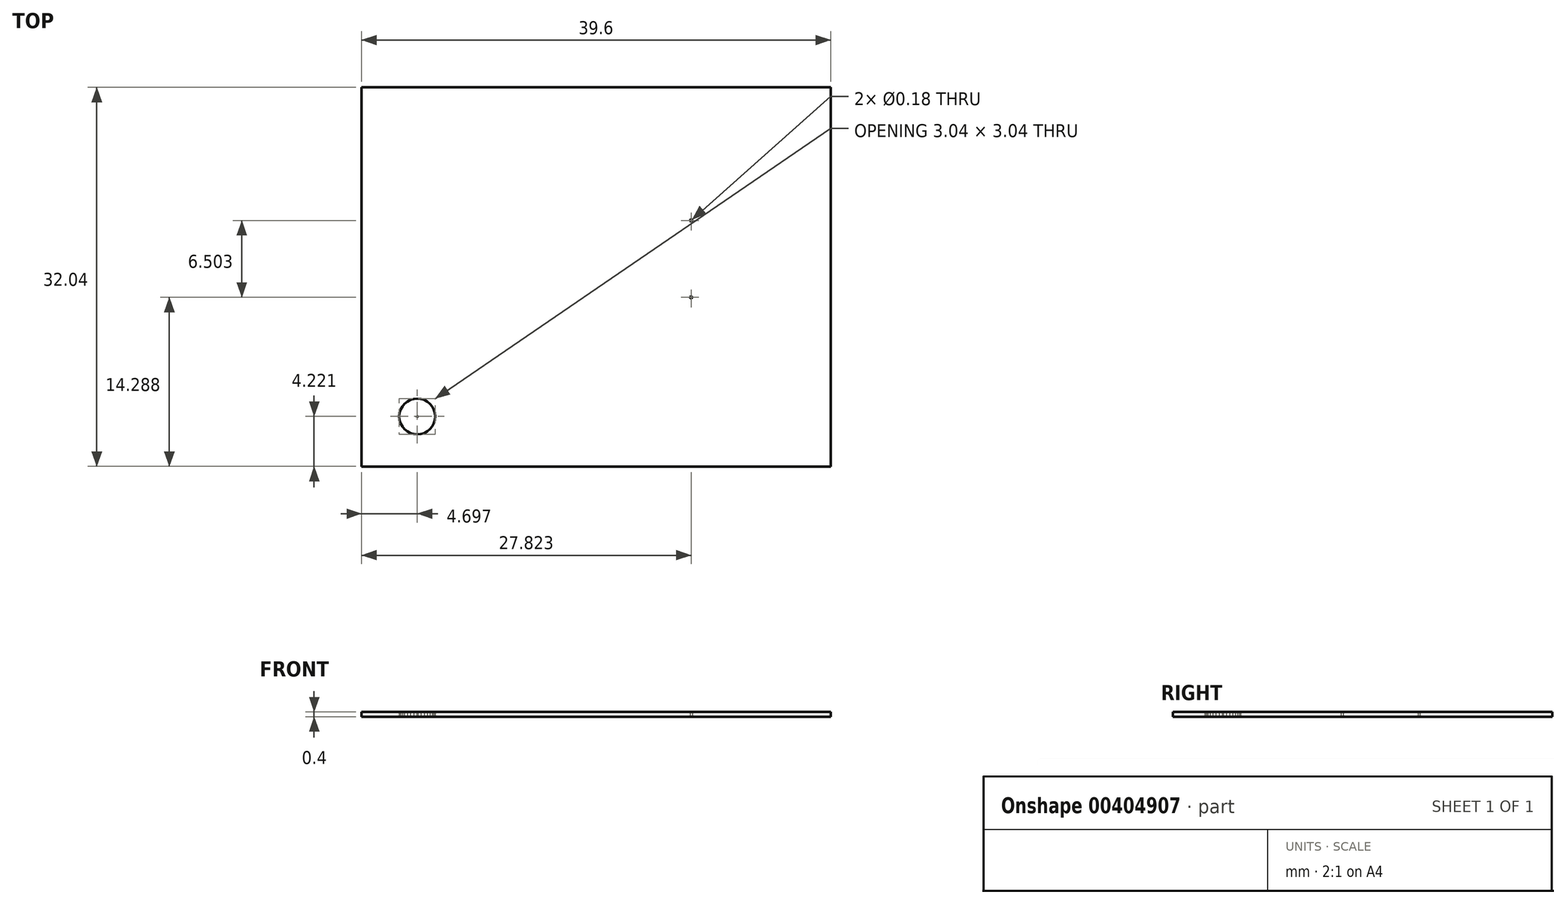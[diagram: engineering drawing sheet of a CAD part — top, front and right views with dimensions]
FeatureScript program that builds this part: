
annotation { "Feature Type Name" : "Feature", "Feature Type Description" : "" }
export const myFeature = defineFeature(function(context is Context, id is Id, definition is map)
    precondition{}
    {
        {
            var Q0;
            Q0=qCreatedBy(makeId("Top.planeOp"),FACE);
            var sketch = newSketch(context, id + "F0", { "sketchPlane" : qUnion([Q0])});
            skLineSegment(sketch, "E0", {"start": v(8.02, -8.23) * mm, "end": v(8.12, -8.23) * mm});
            skCircle(sketch, "E1", {"center": v(8.02, -8.23) * mm, "radius": 0.1 * mm});
            skLineSegment(sketch, "E2", {"start": v(8.02, -4.98) * mm, "end": v(8.12, -4.98) * mm});
            skCircle(sketch, "E3", {"center": v(8.02, -4.98) * mm, "radius": 0.1 * mm});
            skLineSegment(sketch, "E4", {"start": v(8.02, -1.73) * mm, "end": v(8.12, -1.73) * mm});
            skCircle(sketch, "E5", {"center": v(8.02, -1.73) * mm, "radius": 0.1 * mm});
            skLineSegment(sketch, "E6", {"start": v(8.02, 1.52) * mm, "end": v(8.12, 1.52) * mm});
            skCircle(sketch, "E7", {"center": v(8.02, 1.52) * mm, "radius": 0.1 * mm});
            skLineSegment(sketch, "E8", {"start": v(8.02, 4.77) * mm, "end": v(8.12, 4.77) * mm});
            skCircle(sketch, "E9", {"center": v(8.02, 4.77) * mm, "radius": 0.1 * mm});
            skLineSegment(sketch, "E10", {"start": v(8.02, 8.02) * mm, "end": v(8.12, 8.02) * mm});
            skCircle(sketch, "E11", {"center": v(8.02, 8.02) * mm, "radius": 0.1 * mm});
            skLineSegment(sketch, "E12", {"start": v(15.1, -11.8) * mm, "end": v(15.15, -11.8) * mm});
            skCircle(sketch, "E13", {"center": v(15.1, -11.8) * mm, "radius": 0.05 * mm});
            skLineSegment(sketch, "E14", {"start": v(15.1, 11.8) * mm, "end": v(15.15, 11.8) * mm});
            skCircle(sketch, "E15", {"center": v(15.1, 11.8) * mm, "radius": 0.05 * mm});
            skLineSegment(sketch, "E16", {"start": v(-15.1, -11.8) * mm, "end": v(-15.06, -11.8) * mm});
            skCircle(sketch, "E17", {"center": v(-15.1, -11.8) * mm, "radius": 0.05 * mm});
            skLineSegment(sketch, "E18", {"start": v(-15.1, 11.8) * mm, "end": v(-15.06, 11.8) * mm});
            skCircle(sketch, "E19", {"center": v(-15.1, 11.8) * mm, "radius": 0.05 * mm});
            skLineSegment(sketch, "E20", {"start": v(16.5, -12.38) * mm, "end": v(16.6, -12.1) * mm});
            skLineSegment(sketch, "E21", {"start": v(16.6, -12.1) * mm, "end": v(16.62, -11.8) * mm});
            skLineSegment(sketch, "E22", {"start": v(16.62, -11.8) * mm, "end": v(16.6, -11.5) * mm});
            skLineSegment(sketch, "E23", {"start": v(16.6, -11.5) * mm, "end": v(16.5, -11.22) * mm});
            skLineSegment(sketch, "E24", {"start": v(16.5, -11.22) * mm, "end": v(16.36, -10.96) * mm});
            skLineSegment(sketch, "E25", {"start": v(16.36, -10.96) * mm, "end": v(16.18, -10.73) * mm});
            skLineSegment(sketch, "E26", {"start": v(16.18, -10.73) * mm, "end": v(15.95, -10.54) * mm});
            skLineSegment(sketch, "E27", {"start": v(15.95, -10.54) * mm, "end": v(15.68, -10.4) * mm});
            skLineSegment(sketch, "E28", {"start": v(15.68, -10.4) * mm, "end": v(15.4, -10.31) * mm});
            skLineSegment(sketch, "E29", {"start": v(15.4, -10.31) * mm, "end": v(15.1, -10.28) * mm});
            skLineSegment(sketch, "E30", {"start": v(15.1, -10.28) * mm, "end": v(14.8, -10.31) * mm});
            skLineSegment(sketch, "E31", {"start": v(14.8, -10.31) * mm, "end": v(14.52, -10.4) * mm});
            skLineSegment(sketch, "E32", {"start": v(14.52, -10.4) * mm, "end": v(14.26, -10.54) * mm});
            skLineSegment(sketch, "E33", {"start": v(14.26, -10.54) * mm, "end": v(14.03, -10.73) * mm});
            skLineSegment(sketch, "E34", {"start": v(14.03, -10.73) * mm, "end": v(13.84, -10.96) * mm});
            skLineSegment(sketch, "E35", {"start": v(13.84, -10.96) * mm, "end": v(13.7, -11.22) * mm});
            skLineSegment(sketch, "E36", {"start": v(13.7, -11.22) * mm, "end": v(13.61, -11.5) * mm});
            skLineSegment(sketch, "E37", {"start": v(13.61, -11.5) * mm, "end": v(13.59, -11.8) * mm});
            skLineSegment(sketch, "E38", {"start": v(13.59, -11.8) * mm, "end": v(13.61, -12.1) * mm});
            skLineSegment(sketch, "E39", {"start": v(13.61, -12.1) * mm, "end": v(13.7, -12.38) * mm});
            skLineSegment(sketch, "E40", {"start": v(13.7, -12.38) * mm, "end": v(13.84, -12.64) * mm});
            skLineSegment(sketch, "E41", {"start": v(13.84, -12.64) * mm, "end": v(14.03, -12.87) * mm});
            skLineSegment(sketch, "E42", {"start": v(14.03, -12.87) * mm, "end": v(14.26, -13.06) * mm});
            skLineSegment(sketch, "E43", {"start": v(14.26, -13.06) * mm, "end": v(14.52, -13.2) * mm});
            skLineSegment(sketch, "E44", {"start": v(14.52, -13.2) * mm, "end": v(14.8, -13.29) * mm});
            skLineSegment(sketch, "E45", {"start": v(14.8, -13.29) * mm, "end": v(15.1, -13.32) * mm});
            skLineSegment(sketch, "E46", {"start": v(15.1, -13.32) * mm, "end": v(15.4, -13.29) * mm});
            skLineSegment(sketch, "E47", {"start": v(15.4, -13.29) * mm, "end": v(15.68, -13.2) * mm});
            skLineSegment(sketch, "E48", {"start": v(15.68, -13.2) * mm, "end": v(15.95, -13.06) * mm});
            skLineSegment(sketch, "E49", {"start": v(15.95, -13.06) * mm, "end": v(16.18, -12.87) * mm});
            skLineSegment(sketch, "E50", {"start": v(16.18, -12.87) * mm, "end": v(16.36, -12.64) * mm});
            skLineSegment(sketch, "E51", {"start": v(16.36, -12.64) * mm, "end": v(16.5, -12.38) * mm});
            skLineSegment(sketch, "E52", {"start": v(16.48, -12.37) * mm, "end": v(16.56, -12.09) * mm});
            skLineSegment(sketch, "E53", {"start": v(16.56, -12.09) * mm, "end": v(16.59, -11.8) * mm});
            skLineSegment(sketch, "E54", {"start": v(16.59, -11.8) * mm, "end": v(16.56, -11.5) * mm});
            skLineSegment(sketch, "E55", {"start": v(16.56, -11.5) * mm, "end": v(16.48, -11.23) * mm});
            skLineSegment(sketch, "E56", {"start": v(16.48, -11.23) * mm, "end": v(16.34, -10.97) * mm});
            skLineSegment(sketch, "E57", {"start": v(16.34, -10.97) * mm, "end": v(16.15, -10.75) * mm});
            skLineSegment(sketch, "E58", {"start": v(16.15, -10.75) * mm, "end": v(15.93, -10.56) * mm});
            skLineSegment(sketch, "E59", {"start": v(15.93, -10.56) * mm, "end": v(15.67, -10.43) * mm});
            skLineSegment(sketch, "E60", {"start": v(15.67, -10.43) * mm, "end": v(15.4, -10.34) * mm});
            skLineSegment(sketch, "E61", {"start": v(15.4, -10.34) * mm, "end": v(15.1, -10.31) * mm});
            skLineSegment(sketch, "E62", {"start": v(15.1, -10.31) * mm, "end": v(14.81, -10.34) * mm});
            skLineSegment(sketch, "E63", {"start": v(14.81, -10.34) * mm, "end": v(14.53, -10.43) * mm});
            skLineSegment(sketch, "E64", {"start": v(14.53, -10.43) * mm, "end": v(14.28, -10.56) * mm});
            skLineSegment(sketch, "E65", {"start": v(14.28, -10.56) * mm, "end": v(14.05, -10.75) * mm});
            skLineSegment(sketch, "E66", {"start": v(14.05, -10.75) * mm, "end": v(13.87, -10.97) * mm});
            skLineSegment(sketch, "E67", {"start": v(13.87, -10.97) * mm, "end": v(13.73, -11.23) * mm});
            skLineSegment(sketch, "E68", {"start": v(13.73, -11.23) * mm, "end": v(13.64, -11.5) * mm});
            skLineSegment(sketch, "E69", {"start": v(13.64, -11.5) * mm, "end": v(13.62, -11.8) * mm});
            skLineSegment(sketch, "E70", {"start": v(13.62, -11.8) * mm, "end": v(13.64, -12.09) * mm});
            skLineSegment(sketch, "E71", {"start": v(13.64, -12.09) * mm, "end": v(13.73, -12.37) * mm});
            skLineSegment(sketch, "E72", {"start": v(13.73, -12.37) * mm, "end": v(13.87, -12.62) * mm});
            skLineSegment(sketch, "E73", {"start": v(13.87, -12.62) * mm, "end": v(14.05, -12.85) * mm});
            skLineSegment(sketch, "E74", {"start": v(14.05, -12.85) * mm, "end": v(14.28, -13.03) * mm});
            skLineSegment(sketch, "E75", {"start": v(14.28, -13.03) * mm, "end": v(14.53, -13.17) * mm});
            skLineSegment(sketch, "E76", {"start": v(14.53, -13.17) * mm, "end": v(14.81, -13.26) * mm});
            skLineSegment(sketch, "E77", {"start": v(14.81, -13.26) * mm, "end": v(15.1, -13.29) * mm});
            skLineSegment(sketch, "E78", {"start": v(15.1, -13.29) * mm, "end": v(15.4, -13.26) * mm});
            skLineSegment(sketch, "E79", {"start": v(15.4, -13.26) * mm, "end": v(15.67, -13.17) * mm});
            skLineSegment(sketch, "E80", {"start": v(15.67, -13.17) * mm, "end": v(15.93, -13.03) * mm});
            skLineSegment(sketch, "E81", {"start": v(15.93, -13.03) * mm, "end": v(16.15, -12.85) * mm});
            skLineSegment(sketch, "E82", {"start": v(16.15, -12.85) * mm, "end": v(16.34, -12.62) * mm});
            skLineSegment(sketch, "E83", {"start": v(16.34, -12.62) * mm, "end": v(16.48, -12.37) * mm});
            skLineSegment(sketch, "E84", {"start": v(10.57, -8.15) * mm, "end": v(10.59, -8.1) * mm});
            skLineSegment(sketch, "E85", {"start": v(10.59, -8.1) * mm, "end": v(10.6, -8.07) * mm});
            skLineSegment(sketch, "E86", {"start": v(10.6, -8.07) * mm, "end": v(10.6, -8.02) * mm});
            skLineSegment(sketch, "E87", {"start": v(10.6, -8.02) * mm, "end": v(10.6, -1.65) * mm});
            skLineSegment(sketch, "E88", {"start": v(10.6, -1.65) * mm, "end": v(10.6, 4.72) * mm});
            skLineSegment(sketch, "E89", {"start": v(10.6, 4.72) * mm, "end": v(10.6, 8.97) * mm});
            skLineSegment(sketch, "E90", {"start": v(10.6, 8.97) * mm, "end": v(10.6, 9.01) * mm});
            skLineSegment(sketch, "E91", {"start": v(10.6, 9.01) * mm, "end": v(10.59, 9.05) * mm});
            skLineSegment(sketch, "E92", {"start": v(10.59, 9.05) * mm, "end": v(10.57, 9.1) * mm});
            skLineSegment(sketch, "E93", {"start": v(10.57, 9.1) * mm, "end": v(10.54, 9.13) * mm});
            skLineSegment(sketch, "E94", {"start": v(10.54, 9.13) * mm, "end": v(6.3, 13.37) * mm});
            skLineSegment(sketch, "E95", {"start": v(6.3, 13.37) * mm, "end": v(6.26, 13.4) * mm});
            skLineSegment(sketch, "E96", {"start": v(6.26, 13.4) * mm, "end": v(6.22, 13.42) * mm});
            skLineSegment(sketch, "E97", {"start": v(6.22, 13.42) * mm, "end": v(6.18, 13.43) * mm});
            skLineSegment(sketch, "E98", {"start": v(6.18, 13.43) * mm, "end": v(6.14, 13.44) * mm});
            skLineSegment(sketch, "E99", {"start": v(6.14, 13.44) * mm, "end": v(-0.94, 13.44) * mm});
            skLineSegment(sketch, "E100", {"start": v(-0.94, 13.44) * mm, "end": v(-7.08, 13.44) * mm});
            skLineSegment(sketch, "E101", {"start": v(-7.08, 13.44) * mm, "end": v(-7.12, 13.43) * mm});
            skLineSegment(sketch, "E102", {"start": v(-7.12, 13.43) * mm, "end": v(-7.16, 13.42) * mm});
            skLineSegment(sketch, "E103", {"start": v(-7.16, 13.42) * mm, "end": v(-7.2, 13.4) * mm});
            skLineSegment(sketch, "E104", {"start": v(-7.2, 13.4) * mm, "end": v(-7.24, 13.37) * mm});
            skLineSegment(sketch, "E105", {"start": v(-7.24, 13.37) * mm, "end": v(-12.9, 7.7) * mm});
            skLineSegment(sketch, "E106", {"start": v(-12.9, 7.7) * mm, "end": v(-12.93, 7.68) * mm});
            skLineSegment(sketch, "E107", {"start": v(-12.93, 7.68) * mm, "end": v(-12.95, 7.64) * mm});
            skLineSegment(sketch, "E108", {"start": v(-12.95, 7.64) * mm, "end": v(-12.96, 7.6) * mm});
            skLineSegment(sketch, "E109", {"start": v(-12.96, 7.6) * mm, "end": v(-12.97, 7.55) * mm});
            skLineSegment(sketch, "E110", {"start": v(-12.97, 7.55) * mm, "end": v(-12.97, 6.37) * mm});
            skLineSegment(sketch, "E111", {"start": v(-12.97, 6.37) * mm, "end": v(-13.03, 6.35) * mm});
            skLineSegment(sketch, "E112", {"start": v(-13.03, 6.35) * mm, "end": v(-13.16, 6.28) * mm});
            skLineSegment(sketch, "E113", {"start": v(-13.16, 6.28) * mm, "end": v(-13.27, 6.19) * mm});
            skLineSegment(sketch, "E114", {"start": v(-13.27, 6.19) * mm, "end": v(-13.36, 6.08) * mm});
            skLineSegment(sketch, "E115", {"start": v(-13.36, 6.08) * mm, "end": v(-13.43, 5.95) * mm});
            skLineSegment(sketch, "E116", {"start": v(-13.43, 5.95) * mm, "end": v(-13.47, 5.8) * mm});
            skLineSegment(sketch, "E117", {"start": v(-13.47, 5.8) * mm, "end": v(-13.49, 5.66) * mm});
            skLineSegment(sketch, "E118", {"start": v(-13.49, 5.66) * mm, "end": v(-13.47, 5.52) * mm});
            skLineSegment(sketch, "E119", {"start": v(-13.47, 5.52) * mm, "end": v(-13.43, 5.38) * mm});
            skLineSegment(sketch, "E120", {"start": v(-13.43, 5.38) * mm, "end": v(-13.36, 5.25) * mm});
            skLineSegment(sketch, "E121", {"start": v(-13.36, 5.25) * mm, "end": v(-13.27, 5.14) * mm});
            skLineSegment(sketch, "E122", {"start": v(-13.27, 5.14) * mm, "end": v(-13.16, 5.05) * mm});
            skLineSegment(sketch, "E123", {"start": v(-13.16, 5.05) * mm, "end": v(-13.03, 4.98) * mm});
            skLineSegment(sketch, "E124", {"start": v(-13.03, 4.98) * mm, "end": v(-12.89, 4.93) * mm});
            skLineSegment(sketch, "E125", {"start": v(-12.89, 4.93) * mm, "end": v(-12.74, 4.92) * mm});
            skLineSegment(sketch, "E126", {"start": v(-12.74, 4.92) * mm, "end": v(-12.6, 4.93) * mm});
            skLineSegment(sketch, "E127", {"start": v(-12.6, 4.93) * mm, "end": v(-12.46, 4.98) * mm});
            skLineSegment(sketch, "E128", {"start": v(-12.46, 4.98) * mm, "end": v(-12.33, 5.05) * mm});
            skLineSegment(sketch, "E129", {"start": v(-12.33, 5.05) * mm, "end": v(-12.22, 5.14) * mm});
            skLineSegment(sketch, "E130", {"start": v(-12.22, 5.14) * mm, "end": v(-12.12, 5.25) * mm});
            skLineSegment(sketch, "E131", {"start": v(-12.12, 5.25) * mm, "end": v(-12.06, 5.38) * mm});
            skLineSegment(sketch, "E132", {"start": v(-12.06, 5.38) * mm, "end": v(-12.01, 5.52) * mm});
            skLineSegment(sketch, "E133", {"start": v(-12.01, 5.52) * mm, "end": v(-12, 5.66) * mm});
            skLineSegment(sketch, "E134", {"start": v(-12, 5.66) * mm, "end": v(-12.01, 5.8) * mm});
            skLineSegment(sketch, "E135", {"start": v(-12.01, 5.8) * mm, "end": v(-12.06, 5.95) * mm});
            skLineSegment(sketch, "E136", {"start": v(-12.06, 5.95) * mm, "end": v(-12.12, 6.08) * mm});
            skLineSegment(sketch, "E137", {"start": v(-12.12, 6.08) * mm, "end": v(-12.22, 6.19) * mm});
            skLineSegment(sketch, "E138", {"start": v(-12.22, 6.19) * mm, "end": v(-12.33, 6.28) * mm});
            skLineSegment(sketch, "E139", {"start": v(-12.33, 6.28) * mm, "end": v(-12.46, 6.35) * mm});
            skLineSegment(sketch, "E140", {"start": v(-12.46, 6.35) * mm, "end": v(-12.52, 6.37) * mm});
            skLineSegment(sketch, "E141", {"start": v(-12.52, 6.37) * mm, "end": v(-12.52, 7.46) * mm});
            skLineSegment(sketch, "E142", {"start": v(-12.52, 7.46) * mm, "end": v(-6.99, 13) * mm});
            skLineSegment(sketch, "E143", {"start": v(-6.99, 13) * mm, "end": v(-1.17, 13) * mm});
            skLineSegment(sketch, "E144", {"start": v(-1.17, 13) * mm, "end": v(-1.17, 6.12) * mm});
            skLineSegment(sketch, "E145", {"start": v(-1.17, 6.12) * mm, "end": v(-1.18, 6.12) * mm});
            skLineSegment(sketch, "E146", {"start": v(-1.18, 6.12) * mm, "end": v(-3.54, 6.12) * mm});
            skLineSegment(sketch, "E147", {"start": v(-3.54, 6.12) * mm, "end": v(-3.56, 6.18) * mm});
            skLineSegment(sketch, "E148", {"start": v(-3.56, 6.18) * mm, "end": v(-3.63, 6.31) * mm});
            skLineSegment(sketch, "E149", {"start": v(-3.63, 6.31) * mm, "end": v(-3.72, 6.43) * mm});
            skLineSegment(sketch, "E150", {"start": v(-3.72, 6.43) * mm, "end": v(-3.83, 6.52) * mm});
            skLineSegment(sketch, "E151", {"start": v(-3.83, 6.52) * mm, "end": v(-3.96, 6.59) * mm});
            skLineSegment(sketch, "E152", {"start": v(-3.96, 6.59) * mm, "end": v(-4.1, 6.63) * mm});
            skLineSegment(sketch, "E153", {"start": v(-4.1, 6.63) * mm, "end": v(-4.25, 6.64) * mm});
            skLineSegment(sketch, "E154", {"start": v(-4.25, 6.64) * mm, "end": v(-4.4, 6.63) * mm});
            skLineSegment(sketch, "E155", {"start": v(-4.4, 6.63) * mm, "end": v(-4.53, 6.59) * mm});
            skLineSegment(sketch, "E156", {"start": v(-4.53, 6.59) * mm, "end": v(-4.66, 6.52) * mm});
            skLineSegment(sketch, "E157", {"start": v(-4.66, 6.52) * mm, "end": v(-4.77, 6.43) * mm});
            skLineSegment(sketch, "E158", {"start": v(-4.77, 6.43) * mm, "end": v(-4.87, 6.31) * mm});
            skLineSegment(sketch, "E159", {"start": v(-4.87, 6.31) * mm, "end": v(-4.93, 6.18) * mm});
            skLineSegment(sketch, "E160", {"start": v(-4.93, 6.18) * mm, "end": v(-4.98, 6.04) * mm});
            skLineSegment(sketch, "E161", {"start": v(-4.98, 6.04) * mm, "end": v(-5, 5.9) * mm});
            skLineSegment(sketch, "E162", {"start": v(-5, 5.9) * mm, "end": v(-4.98, 5.75) * mm});
            skLineSegment(sketch, "E163", {"start": v(-4.98, 5.75) * mm, "end": v(-4.93, 5.62) * mm});
            skLineSegment(sketch, "E164", {"start": v(-4.93, 5.62) * mm, "end": v(-4.87, 5.49) * mm});
            skLineSegment(sketch, "E165", {"start": v(-4.87, 5.49) * mm, "end": v(-4.77, 5.37) * mm});
            skLineSegment(sketch, "E166", {"start": v(-4.77, 5.37) * mm, "end": v(-4.66, 5.28) * mm});
            skLineSegment(sketch, "E167", {"start": v(-4.66, 5.28) * mm, "end": v(-4.53, 5.21) * mm});
            skLineSegment(sketch, "E168", {"start": v(-4.53, 5.21) * mm, "end": v(-4.4, 5.17) * mm});
            skLineSegment(sketch, "E169", {"start": v(-4.4, 5.17) * mm, "end": v(-4.25, 5.16) * mm});
            skLineSegment(sketch, "E170", {"start": v(-4.25, 5.16) * mm, "end": v(-4.1, 5.17) * mm});
            skLineSegment(sketch, "E171", {"start": v(-4.1, 5.17) * mm, "end": v(-3.96, 5.21) * mm});
            skLineSegment(sketch, "E172", {"start": v(-3.96, 5.21) * mm, "end": v(-3.83, 5.28) * mm});
            skLineSegment(sketch, "E173", {"start": v(-3.83, 5.28) * mm, "end": v(-3.72, 5.37) * mm});
            skLineSegment(sketch, "E174", {"start": v(-3.72, 5.37) * mm, "end": v(-3.63, 5.49) * mm});
            skLineSegment(sketch, "E175", {"start": v(-3.63, 5.49) * mm, "end": v(-3.56, 5.62) * mm});
            skLineSegment(sketch, "E176", {"start": v(-3.56, 5.62) * mm, "end": v(-3.54, 5.68) * mm});
            skLineSegment(sketch, "E177", {"start": v(-3.54, 5.68) * mm, "end": v(-1.27, 5.68) * mm});
            skLineSegment(sketch, "E178", {"start": v(-1.27, 5.68) * mm, "end": v(-1.17, 5.57) * mm});
            skLineSegment(sketch, "E179", {"start": v(-1.17, 5.57) * mm, "end": v(-1.17, -2.27) * mm});
            skLineSegment(sketch, "E180", {"start": v(-1.17, -2.27) * mm, "end": v(-1.27, -2.37) * mm});
            skLineSegment(sketch, "E181", {"start": v(-1.27, -2.37) * mm, "end": v(-3.54, -2.37) * mm});
            skLineSegment(sketch, "E182", {"start": v(-3.54, -2.37) * mm, "end": v(-3.56, -2.31) * mm});
            skLineSegment(sketch, "E183", {"start": v(-3.56, -2.31) * mm, "end": v(-3.63, -2.18) * mm});
            skLineSegment(sketch, "E184", {"start": v(-3.63, -2.18) * mm, "end": v(-3.72, -2.07) * mm});
            skLineSegment(sketch, "E185", {"start": v(-3.72, -2.07) * mm, "end": v(-3.83, -1.98) * mm});
            skLineSegment(sketch, "E186", {"start": v(-3.83, -1.98) * mm, "end": v(-3.96, -1.9) * mm});
            skLineSegment(sketch, "E187", {"start": v(-3.96, -1.9) * mm, "end": v(-4.1, -1.87) * mm});
            skLineSegment(sketch, "E188", {"start": v(-4.1, -1.87) * mm, "end": v(-4.25, -1.85) * mm});
            skLineSegment(sketch, "E189", {"start": v(-4.25, -1.85) * mm, "end": v(-4.4, -1.87) * mm});
            skLineSegment(sketch, "E190", {"start": v(-4.4, -1.87) * mm, "end": v(-4.53, -1.9) * mm});
            skLineSegment(sketch, "E191", {"start": v(-4.53, -1.9) * mm, "end": v(-4.66, -1.98) * mm});
            skLineSegment(sketch, "E192", {"start": v(-4.66, -1.98) * mm, "end": v(-4.77, -2.07) * mm});
            skLineSegment(sketch, "E193", {"start": v(-4.77, -2.07) * mm, "end": v(-4.87, -2.18) * mm});
            skLineSegment(sketch, "E194", {"start": v(-4.87, -2.18) * mm, "end": v(-4.93, -2.31) * mm});
            skLineSegment(sketch, "E195", {"start": v(-4.93, -2.31) * mm, "end": v(-4.98, -2.45) * mm});
            skLineSegment(sketch, "E196", {"start": v(-4.98, -2.45) * mm, "end": v(-5, -2.6) * mm});
            skLineSegment(sketch, "E197", {"start": v(-5, -2.6) * mm, "end": v(-4.98, -2.74) * mm});
            skLineSegment(sketch, "E198", {"start": v(-4.98, -2.74) * mm, "end": v(-4.93, -2.88) * mm});
            skLineSegment(sketch, "E199", {"start": v(-4.93, -2.88) * mm, "end": v(-4.87, -3) * mm});
            skLineSegment(sketch, "E200", {"start": v(-4.87, -3) * mm, "end": v(-4.77, -3.12) * mm});
            skLineSegment(sketch, "E201", {"start": v(-4.77, -3.12) * mm, "end": v(-4.66, -3.21) * mm});
            skLineSegment(sketch, "E202", {"start": v(-4.66, -3.21) * mm, "end": v(-4.53, -3.28) * mm});
            skLineSegment(sketch, "E203", {"start": v(-4.53, -3.28) * mm, "end": v(-4.4, -3.32) * mm});
            skLineSegment(sketch, "E204", {"start": v(-4.4, -3.32) * mm, "end": v(-4.25, -3.34) * mm});
            skLineSegment(sketch, "E205", {"start": v(-4.25, -3.34) * mm, "end": v(-4.1, -3.32) * mm});
            skLineSegment(sketch, "E206", {"start": v(-4.1, -3.32) * mm, "end": v(-3.96, -3.28) * mm});
            skLineSegment(sketch, "E207", {"start": v(-3.96, -3.28) * mm, "end": v(-3.83, -3.21) * mm});
            skLineSegment(sketch, "E208", {"start": v(-3.83, -3.21) * mm, "end": v(-3.72, -3.12) * mm});
            skLineSegment(sketch, "E209", {"start": v(-3.72, -3.12) * mm, "end": v(-3.63, -3) * mm});
            skLineSegment(sketch, "E210", {"start": v(-3.63, -3) * mm, "end": v(-3.56, -2.88) * mm});
            skLineSegment(sketch, "E211", {"start": v(-3.56, -2.88) * mm, "end": v(-3.54, -2.82) * mm});
            skLineSegment(sketch, "E212", {"start": v(-3.54, -2.82) * mm, "end": v(-1.18, -2.82) * mm});
            skLineSegment(sketch, "E213", {"start": v(-1.18, -2.82) * mm, "end": v(-1.17, -2.82) * mm});
            skLineSegment(sketch, "E214", {"start": v(-1.17, -2.82) * mm, "end": v(-1.17, -10.3) * mm});
            skLineSegment(sketch, "E215", {"start": v(-1.17, -10.3) * mm, "end": v(-1.74, -10.87) * mm});
            skLineSegment(sketch, "E216", {"start": v(-1.74, -10.87) * mm, "end": v(-3.54, -10.87) * mm});
            skLineSegment(sketch, "E217", {"start": v(-3.54, -10.87) * mm, "end": v(-3.56, -10.8) * mm});
            skLineSegment(sketch, "E218", {"start": v(-3.56, -10.8) * mm, "end": v(-3.63, -10.68) * mm});
            skLineSegment(sketch, "E219", {"start": v(-3.63, -10.68) * mm, "end": v(-3.72, -10.57) * mm});
            skLineSegment(sketch, "E220", {"start": v(-3.72, -10.57) * mm, "end": v(-3.83, -10.47) * mm});
            skLineSegment(sketch, "E221", {"start": v(-3.83, -10.47) * mm, "end": v(-3.96, -10.4) * mm});
            skLineSegment(sketch, "E222", {"start": v(-3.96, -10.4) * mm, "end": v(-4.1, -10.36) * mm});
            skLineSegment(sketch, "E223", {"start": v(-4.1, -10.36) * mm, "end": v(-4.25, -10.35) * mm});
            skLineSegment(sketch, "E224", {"start": v(-4.25, -10.35) * mm, "end": v(-4.4, -10.36) * mm});
            skLineSegment(sketch, "E225", {"start": v(-4.4, -10.36) * mm, "end": v(-4.53, -10.4) * mm});
            skLineSegment(sketch, "E226", {"start": v(-4.53, -10.4) * mm, "end": v(-4.66, -10.47) * mm});
            skLineSegment(sketch, "E227", {"start": v(-4.66, -10.47) * mm, "end": v(-4.77, -10.57) * mm});
            skLineSegment(sketch, "E228", {"start": v(-4.77, -10.57) * mm, "end": v(-4.87, -10.68) * mm});
            skLineSegment(sketch, "E229", {"start": v(-4.87, -10.68) * mm, "end": v(-4.93, -10.8) * mm});
            skLineSegment(sketch, "E230", {"start": v(-4.93, -10.8) * mm, "end": v(-4.98, -10.95) * mm});
            skLineSegment(sketch, "E231", {"start": v(-4.98, -10.95) * mm, "end": v(-5, -11.1) * mm});
            skLineSegment(sketch, "E232", {"start": v(-5, -11.1) * mm, "end": v(-4.98, -11.24) * mm});
            skLineSegment(sketch, "E233", {"start": v(-4.98, -11.24) * mm, "end": v(-4.93, -11.38) * mm});
            skLineSegment(sketch, "E234", {"start": v(-4.93, -11.38) * mm, "end": v(-4.87, -11.5) * mm});
            skLineSegment(sketch, "E235", {"start": v(-4.87, -11.5) * mm, "end": v(-4.77, -11.62) * mm});
            skLineSegment(sketch, "E236", {"start": v(-4.77, -11.62) * mm, "end": v(-4.66, -11.7) * mm});
            skLineSegment(sketch, "E237", {"start": v(-4.66, -11.7) * mm, "end": v(-4.53, -11.78) * mm});
            skLineSegment(sketch, "E238", {"start": v(-4.53, -11.78) * mm, "end": v(-4.4, -11.82) * mm});
            skLineSegment(sketch, "E239", {"start": v(-4.4, -11.82) * mm, "end": v(-4.25, -11.83) * mm});
            skLineSegment(sketch, "E240", {"start": v(-4.25, -11.83) * mm, "end": v(-4.1, -11.82) * mm});
            skLineSegment(sketch, "E241", {"start": v(-4.1, -11.82) * mm, "end": v(-3.96, -11.78) * mm});
            skLineSegment(sketch, "E242", {"start": v(-3.96, -11.78) * mm, "end": v(-3.83, -11.7) * mm});
            skLineSegment(sketch, "E243", {"start": v(-3.83, -11.7) * mm, "end": v(-3.72, -11.62) * mm});
            skLineSegment(sketch, "E244", {"start": v(-3.72, -11.62) * mm, "end": v(-3.63, -11.5) * mm});
            skLineSegment(sketch, "E245", {"start": v(-3.63, -11.5) * mm, "end": v(-3.56, -11.38) * mm});
            skLineSegment(sketch, "E246", {"start": v(-3.56, -11.38) * mm, "end": v(-3.54, -11.31) * mm});
            skLineSegment(sketch, "E247", {"start": v(-3.54, -11.31) * mm, "end": v(-1.65, -11.31) * mm});
            skLineSegment(sketch, "E248", {"start": v(-1.65, -11.31) * mm, "end": v(-1.6, -11.31) * mm});
            skLineSegment(sketch, "E249", {"start": v(-1.6, -11.31) * mm, "end": v(-1.57, -11.3) * mm});
            skLineSegment(sketch, "E250", {"start": v(-1.57, -11.3) * mm, "end": v(-1.53, -11.28) * mm});
            skLineSegment(sketch, "E251", {"start": v(-1.53, -11.28) * mm, "end": v(-1.5, -11.25) * mm});
            skLineSegment(sketch, "E252", {"start": v(-1.5, -11.25) * mm, "end": v(-0.79, -10.54) * mm});
            skLineSegment(sketch, "E253", {"start": v(-0.79, -10.54) * mm, "end": v(-0.76, -10.5) * mm});
            skLineSegment(sketch, "E254", {"start": v(-0.76, -10.5) * mm, "end": v(-0.74, -10.47) * mm});
            skLineSegment(sketch, "E255", {"start": v(-0.74, -10.47) * mm, "end": v(-0.72, -10.43) * mm});
            skLineSegment(sketch, "E256", {"start": v(-0.72, -10.43) * mm, "end": v(-0.72, -10.38) * mm});
            skLineSegment(sketch, "E257", {"start": v(-0.72, -10.38) * mm, "end": v(-0.72, -2.36) * mm});
            skLineSegment(sketch, "E258", {"start": v(-0.72, -2.36) * mm, "end": v(-0.72, 5.66) * mm});
            skLineSegment(sketch, "E259", {"start": v(-0.72, 5.66) * mm, "end": v(-0.72, 13) * mm});
            skLineSegment(sketch, "E260", {"start": v(-0.72, 13) * mm, "end": v(6.04, 13) * mm});
            skLineSegment(sketch, "E261", {"start": v(6.04, 13) * mm, "end": v(10.16, 8.87) * mm});
            skLineSegment(sketch, "E262", {"start": v(10.16, 8.87) * mm, "end": v(10.16, 4.94) * mm});
            skLineSegment(sketch, "E263", {"start": v(10.16, 4.94) * mm, "end": v(9.12, 4.94) * mm});
            skLineSegment(sketch, "E264", {"start": v(9.12, 4.94) * mm, "end": v(9.12, 4.99) * mm});
            skLineSegment(sketch, "E265", {"start": v(9.12, 4.99) * mm, "end": v(9.05, 5.2) * mm});
            skLineSegment(sketch, "E266", {"start": v(9.05, 5.2) * mm, "end": v(8.95, 5.4) * mm});
            skLineSegment(sketch, "E267", {"start": v(8.95, 5.4) * mm, "end": v(8.81, 5.56) * mm});
            skLineSegment(sketch, "E268", {"start": v(8.81, 5.56) * mm, "end": v(8.64, 5.7) * mm});
            skLineSegment(sketch, "E269", {"start": v(8.64, 5.7) * mm, "end": v(8.45, 5.8) * mm});
            skLineSegment(sketch, "E270", {"start": v(8.45, 5.8) * mm, "end": v(8.24, 5.87) * mm});
            skLineSegment(sketch, "E271", {"start": v(8.24, 5.87) * mm, "end": v(8.02, 5.89) * mm});
            skLineSegment(sketch, "E272", {"start": v(8.02, 5.89) * mm, "end": v(7.8, 5.87) * mm});
            skLineSegment(sketch, "E273", {"start": v(7.8, 5.87) * mm, "end": v(7.6, 5.8) * mm});
            skLineSegment(sketch, "E274", {"start": v(7.6, 5.8) * mm, "end": v(7.4, 5.7) * mm});
            skLineSegment(sketch, "E275", {"start": v(7.4, 5.7) * mm, "end": v(7.23, 5.56) * mm});
            skLineSegment(sketch, "E276", {"start": v(7.23, 5.56) * mm, "end": v(7.1, 5.4) * mm});
            skLineSegment(sketch, "E277", {"start": v(7.1, 5.4) * mm, "end": v(7, 5.2) * mm});
            skLineSegment(sketch, "E278", {"start": v(7, 5.2) * mm, "end": v(6.93, 4.99) * mm});
            skLineSegment(sketch, "E279", {"start": v(6.93, 4.99) * mm, "end": v(6.9, 4.77) * mm});
            skLineSegment(sketch, "E280", {"start": v(6.9, 4.77) * mm, "end": v(6.93, 4.55) * mm});
            skLineSegment(sketch, "E281", {"start": v(6.93, 4.55) * mm, "end": v(7, 4.35) * mm});
            skLineSegment(sketch, "E282", {"start": v(7, 4.35) * mm, "end": v(7.1, 4.15) * mm});
            skLineSegment(sketch, "E283", {"start": v(7.1, 4.15) * mm, "end": v(7.23, 3.98) * mm});
            skLineSegment(sketch, "E284", {"start": v(7.23, 3.98) * mm, "end": v(7.4, 3.84) * mm});
            skLineSegment(sketch, "E285", {"start": v(7.4, 3.84) * mm, "end": v(7.6, 3.74) * mm});
            skLineSegment(sketch, "E286", {"start": v(7.6, 3.74) * mm, "end": v(7.8, 3.68) * mm});
            skLineSegment(sketch, "E287", {"start": v(7.8, 3.68) * mm, "end": v(8.02, 3.66) * mm});
            skLineSegment(sketch, "E288", {"start": v(8.02, 3.66) * mm, "end": v(8.24, 3.68) * mm});
            skLineSegment(sketch, "E289", {"start": v(8.24, 3.68) * mm, "end": v(8.45, 3.74) * mm});
            skLineSegment(sketch, "E290", {"start": v(8.45, 3.74) * mm, "end": v(8.64, 3.84) * mm});
            skLineSegment(sketch, "E291", {"start": v(8.64, 3.84) * mm, "end": v(8.81, 3.98) * mm});
            skLineSegment(sketch, "E292", {"start": v(8.81, 3.98) * mm, "end": v(8.95, 4.15) * mm});
            skLineSegment(sketch, "E293", {"start": v(8.95, 4.15) * mm, "end": v(9.05, 4.35) * mm});
            skLineSegment(sketch, "E294", {"start": v(9.05, 4.35) * mm, "end": v(9.1, 4.5) * mm});
            skLineSegment(sketch, "E295", {"start": v(9.1, 4.5) * mm, "end": v(10.16, 4.5) * mm});
            skLineSegment(sketch, "E296", {"start": v(10.16, 4.5) * mm, "end": v(10.16, -1.5) * mm});
            skLineSegment(sketch, "E297", {"start": v(10.16, -1.5) * mm, "end": v(9.11, -1.5) * mm});
            skLineSegment(sketch, "E298", {"start": v(9.11, -1.5) * mm, "end": v(9.05, -1.3) * mm});
            skLineSegment(sketch, "E299", {"start": v(9.05, -1.3) * mm, "end": v(8.95, -1.11) * mm});
            skLineSegment(sketch, "E300", {"start": v(8.95, -1.11) * mm, "end": v(8.81, -0.94) * mm});
            skLineSegment(sketch, "E301", {"start": v(8.81, -0.94) * mm, "end": v(8.64, -0.8) * mm});
            skLineSegment(sketch, "E302", {"start": v(8.64, -0.8) * mm, "end": v(8.45, -0.7) * mm});
            skLineSegment(sketch, "E303", {"start": v(8.45, -0.7) * mm, "end": v(8.24, -0.64) * mm});
            skLineSegment(sketch, "E304", {"start": v(8.24, -0.64) * mm, "end": v(8.02, -0.62) * mm});
            skLineSegment(sketch, "E305", {"start": v(8.02, -0.62) * mm, "end": v(7.8, -0.64) * mm});
            skLineSegment(sketch, "E306", {"start": v(7.8, -0.64) * mm, "end": v(7.6, -0.7) * mm});
            skLineSegment(sketch, "E307", {"start": v(7.6, -0.7) * mm, "end": v(7.4, -0.8) * mm});
            skLineSegment(sketch, "E308", {"start": v(7.4, -0.8) * mm, "end": v(7.23, -0.94) * mm});
            skLineSegment(sketch, "E309", {"start": v(7.23, -0.94) * mm, "end": v(7.1, -1.11) * mm});
            skLineSegment(sketch, "E310", {"start": v(7.1, -1.11) * mm, "end": v(7, -1.3) * mm});
            skLineSegment(sketch, "E311", {"start": v(7, -1.3) * mm, "end": v(6.93, -1.51) * mm});
            skLineSegment(sketch, "E312", {"start": v(6.93, -1.51) * mm, "end": v(6.9, -1.73) * mm});
            skLineSegment(sketch, "E313", {"start": v(6.9, -1.73) * mm, "end": v(6.93, -1.95) * mm});
            skLineSegment(sketch, "E314", {"start": v(6.93, -1.95) * mm, "end": v(7, -2.16) * mm});
            skLineSegment(sketch, "E315", {"start": v(7, -2.16) * mm, "end": v(7.1, -2.35) * mm});
            skLineSegment(sketch, "E316", {"start": v(7.1, -2.35) * mm, "end": v(7.23, -2.52) * mm});
            skLineSegment(sketch, "E317", {"start": v(7.23, -2.52) * mm, "end": v(7.4, -2.66) * mm});
            skLineSegment(sketch, "E318", {"start": v(7.4, -2.66) * mm, "end": v(7.6, -2.76) * mm});
            skLineSegment(sketch, "E319", {"start": v(7.6, -2.76) * mm, "end": v(7.8, -2.83) * mm});
            skLineSegment(sketch, "E320", {"start": v(7.8, -2.83) * mm, "end": v(8.02, -2.85) * mm});
            skLineSegment(sketch, "E321", {"start": v(8.02, -2.85) * mm, "end": v(8.24, -2.83) * mm});
            skLineSegment(sketch, "E322", {"start": v(8.24, -2.83) * mm, "end": v(8.45, -2.76) * mm});
            skLineSegment(sketch, "E323", {"start": v(8.45, -2.76) * mm, "end": v(8.64, -2.66) * mm});
            skLineSegment(sketch, "E324", {"start": v(8.64, -2.66) * mm, "end": v(8.81, -2.52) * mm});
            skLineSegment(sketch, "E325", {"start": v(8.81, -2.52) * mm, "end": v(8.95, -2.35) * mm});
            skLineSegment(sketch, "E326", {"start": v(8.95, -2.35) * mm, "end": v(9.05, -2.16) * mm});
            skLineSegment(sketch, "E327", {"start": v(9.05, -2.16) * mm, "end": v(9.11, -1.96) * mm});
            skLineSegment(sketch, "E328", {"start": v(9.11, -1.96) * mm, "end": v(10.16, -1.96) * mm});
            skLineSegment(sketch, "E329", {"start": v(10.16, -1.96) * mm, "end": v(10.16, -7.93) * mm});
            skLineSegment(sketch, "E330", {"start": v(10.16, -7.93) * mm, "end": v(10.08, -8.01) * mm});
            skLineSegment(sketch, "E331", {"start": v(10.08, -8.01) * mm, "end": v(9.11, -8.01) * mm});
            skLineSegment(sketch, "E332", {"start": v(9.11, -8.01) * mm, "end": v(9.05, -7.8) * mm});
            skLineSegment(sketch, "E333", {"start": v(9.05, -7.8) * mm, "end": v(8.95, -7.62) * mm});
            skLineSegment(sketch, "E334", {"start": v(8.95, -7.62) * mm, "end": v(8.81, -7.45) * mm});
            skLineSegment(sketch, "E335", {"start": v(8.81, -7.45) * mm, "end": v(8.64, -7.3) * mm});
            skLineSegment(sketch, "E336", {"start": v(8.64, -7.3) * mm, "end": v(8.45, -7.2) * mm});
            skLineSegment(sketch, "E337", {"start": v(8.45, -7.2) * mm, "end": v(8.24, -7.14) * mm});
            skLineSegment(sketch, "E338", {"start": v(8.24, -7.14) * mm, "end": v(8.02, -7.12) * mm});
            skLineSegment(sketch, "E339", {"start": v(8.02, -7.12) * mm, "end": v(7.8, -7.14) * mm});
            skLineSegment(sketch, "E340", {"start": v(7.8, -7.14) * mm, "end": v(7.6, -7.2) * mm});
            skLineSegment(sketch, "E341", {"start": v(7.6, -7.2) * mm, "end": v(7.4, -7.3) * mm});
            skLineSegment(sketch, "E342", {"start": v(7.4, -7.3) * mm, "end": v(7.23, -7.45) * mm});
            skLineSegment(sketch, "E343", {"start": v(7.23, -7.45) * mm, "end": v(7.1, -7.62) * mm});
            skLineSegment(sketch, "E344", {"start": v(7.1, -7.62) * mm, "end": v(7, -7.8) * mm});
            skLineSegment(sketch, "E345", {"start": v(7, -7.8) * mm, "end": v(6.93, -8.02) * mm});
            skLineSegment(sketch, "E346", {"start": v(6.93, -8.02) * mm, "end": v(6.9, -8.23) * mm});
            skLineSegment(sketch, "E347", {"start": v(6.9, -8.23) * mm, "end": v(6.93, -8.45) * mm});
            skLineSegment(sketch, "E348", {"start": v(6.93, -8.45) * mm, "end": v(7, -8.66) * mm});
            skLineSegment(sketch, "E349", {"start": v(7, -8.66) * mm, "end": v(7.1, -8.85) * mm});
            skLineSegment(sketch, "E350", {"start": v(7.1, -8.85) * mm, "end": v(7.23, -9.02) * mm});
            skLineSegment(sketch, "E351", {"start": v(7.23, -9.02) * mm, "end": v(7.4, -9.16) * mm});
            skLineSegment(sketch, "E352", {"start": v(7.4, -9.16) * mm, "end": v(7.6, -9.26) * mm});
            skLineSegment(sketch, "E353", {"start": v(7.6, -9.26) * mm, "end": v(7.8, -9.33) * mm});
            skLineSegment(sketch, "E354", {"start": v(7.8, -9.33) * mm, "end": v(8.02, -9.35) * mm});
            skLineSegment(sketch, "E355", {"start": v(8.02, -9.35) * mm, "end": v(8.24, -9.33) * mm});
            skLineSegment(sketch, "E356", {"start": v(8.24, -9.33) * mm, "end": v(8.45, -9.26) * mm});
            skLineSegment(sketch, "E357", {"start": v(8.45, -9.26) * mm, "end": v(8.64, -9.16) * mm});
            skLineSegment(sketch, "E358", {"start": v(8.64, -9.16) * mm, "end": v(8.81, -9.02) * mm});
            skLineSegment(sketch, "E359", {"start": v(8.81, -9.02) * mm, "end": v(8.95, -8.85) * mm});
            skLineSegment(sketch, "E360", {"start": v(8.95, -8.85) * mm, "end": v(9.05, -8.66) * mm});
            skLineSegment(sketch, "E361", {"start": v(9.05, -8.66) * mm, "end": v(9.11, -8.46) * mm});
            skLineSegment(sketch, "E362", {"start": v(9.11, -8.46) * mm, "end": v(10.17, -8.46) * mm});
            skLineSegment(sketch, "E363", {"start": v(10.17, -8.46) * mm, "end": v(10.22, -8.45) * mm});
            skLineSegment(sketch, "E364", {"start": v(10.22, -8.45) * mm, "end": v(10.26, -8.44) * mm});
            skLineSegment(sketch, "E365", {"start": v(10.26, -8.44) * mm, "end": v(10.3, -8.42) * mm});
            skLineSegment(sketch, "E366", {"start": v(10.3, -8.42) * mm, "end": v(10.33, -8.4) * mm});
            skLineSegment(sketch, "E367", {"start": v(10.33, -8.4) * mm, "end": v(10.54, -8.18) * mm});
            skLineSegment(sketch, "E368", {"start": v(10.54, -8.18) * mm, "end": v(10.57, -8.15) * mm});
            skLineSegment(sketch, "E369", {"start": v(9.15, -8.01) * mm, "end": v(9.08, -7.8) * mm});
            skLineSegment(sketch, "E370", {"start": v(9.08, -7.8) * mm, "end": v(8.98, -7.6) * mm});
            skLineSegment(sketch, "E371", {"start": v(8.98, -7.6) * mm, "end": v(8.83, -7.42) * mm});
            skLineSegment(sketch, "E372", {"start": v(8.83, -7.42) * mm, "end": v(8.66, -7.28) * mm});
            skLineSegment(sketch, "E373", {"start": v(8.66, -7.28) * mm, "end": v(8.46, -7.18) * mm});
            skLineSegment(sketch, "E374", {"start": v(8.46, -7.18) * mm, "end": v(8.25, -7.11) * mm});
            skLineSegment(sketch, "E375", {"start": v(8.25, -7.11) * mm, "end": v(8.02, -7.09) * mm});
            skLineSegment(sketch, "E376", {"start": v(8.02, -7.09) * mm, "end": v(7.8, -7.11) * mm});
            skLineSegment(sketch, "E377", {"start": v(7.8, -7.11) * mm, "end": v(7.58, -7.18) * mm});
            skLineSegment(sketch, "E378", {"start": v(7.58, -7.18) * mm, "end": v(7.39, -7.28) * mm});
            skLineSegment(sketch, "E379", {"start": v(7.39, -7.28) * mm, "end": v(7.21, -7.42) * mm});
            skLineSegment(sketch, "E380", {"start": v(7.21, -7.42) * mm, "end": v(7.07, -7.6) * mm});
            skLineSegment(sketch, "E381", {"start": v(7.07, -7.6) * mm, "end": v(6.96, -7.8) * mm});
            skLineSegment(sketch, "E382", {"start": v(6.96, -7.8) * mm, "end": v(6.9, -8.01) * mm});
            skLineSegment(sketch, "E383", {"start": v(6.9, -8.01) * mm, "end": v(6.88, -8.23) * mm});
            skLineSegment(sketch, "E384", {"start": v(6.88, -8.23) * mm, "end": v(6.9, -8.46) * mm});
            skLineSegment(sketch, "E385", {"start": v(6.9, -8.46) * mm, "end": v(6.96, -8.67) * mm});
            skLineSegment(sketch, "E386", {"start": v(6.96, -8.67) * mm, "end": v(7.07, -8.87) * mm});
            skLineSegment(sketch, "E387", {"start": v(7.07, -8.87) * mm, "end": v(7.21, -9.05) * mm});
            skLineSegment(sketch, "E388", {"start": v(7.21, -9.05) * mm, "end": v(7.39, -9.19) * mm});
            skLineSegment(sketch, "E389", {"start": v(7.39, -9.19) * mm, "end": v(7.58, -9.3) * mm});
            skLineSegment(sketch, "E390", {"start": v(7.58, -9.3) * mm, "end": v(7.8, -9.36) * mm});
            skLineSegment(sketch, "E391", {"start": v(7.8, -9.36) * mm, "end": v(8.02, -9.38) * mm});
            skLineSegment(sketch, "E392", {"start": v(8.02, -9.38) * mm, "end": v(8.25, -9.36) * mm});
            skLineSegment(sketch, "E393", {"start": v(8.25, -9.36) * mm, "end": v(8.46, -9.3) * mm});
            skLineSegment(sketch, "E394", {"start": v(8.46, -9.3) * mm, "end": v(8.66, -9.19) * mm});
            skLineSegment(sketch, "E395", {"start": v(8.66, -9.19) * mm, "end": v(8.83, -9.05) * mm});
            skLineSegment(sketch, "E396", {"start": v(8.83, -9.05) * mm, "end": v(8.98, -8.87) * mm});
            skLineSegment(sketch, "E397", {"start": v(8.98, -8.87) * mm, "end": v(9.08, -8.67) * mm});
            skLineSegment(sketch, "E398", {"start": v(9.08, -8.67) * mm, "end": v(9.15, -8.46) * mm});
            skLineSegment(sketch, "E399", {"start": v(9.04, -5.84) * mm, "end": v(9.1, -5.74) * mm});
            skLineSegment(sketch, "E400", {"start": v(9.1, -5.74) * mm, "end": v(9.13, -5.63) * mm});
            skLineSegment(sketch, "E401", {"start": v(9.13, -5.63) * mm, "end": v(9.13, -5.56) * mm});
            skLineSegment(sketch, "E402", {"start": v(9.13, -5.56) * mm, "end": v(9.14, -5.56) * mm});
            skLineSegment(sketch, "E403", {"start": v(9.14, -5.56) * mm, "end": v(9.14, -5.51) * mm});
            skLineSegment(sketch, "E404", {"start": v(9.14, -5.51) * mm, "end": v(9.14, -4.45) * mm});
            skLineSegment(sketch, "E405", {"start": v(9.14, -4.45) * mm, "end": v(9.14, -4.4) * mm});
            skLineSegment(sketch, "E406", {"start": v(9.14, -4.4) * mm, "end": v(9.13, -4.4) * mm});
            skLineSegment(sketch, "E407", {"start": v(9.13, -4.4) * mm, "end": v(9.13, -4.34) * mm});
            skLineSegment(sketch, "E408", {"start": v(9.13, -4.34) * mm, "end": v(9.1, -4.23) * mm});
            skLineSegment(sketch, "E409", {"start": v(9.1, -4.23) * mm, "end": v(9.04, -4.13) * mm});
            skLineSegment(sketch, "E410", {"start": v(9.04, -4.13) * mm, "end": v(8.97, -4.04) * mm});
            skLineSegment(sketch, "E411", {"start": v(8.97, -4.04) * mm, "end": v(8.88, -3.97) * mm});
            skLineSegment(sketch, "E412", {"start": v(8.88, -3.97) * mm, "end": v(8.78, -3.91) * mm});
            skLineSegment(sketch, "E413", {"start": v(8.78, -3.91) * mm, "end": v(8.67, -3.88) * mm});
            skLineSegment(sketch, "E414", {"start": v(8.67, -3.88) * mm, "end": v(8.6, -3.87) * mm});
            skLineSegment(sketch, "E415", {"start": v(8.6, -3.87) * mm, "end": v(8.6, -3.87) * mm});
            skLineSegment(sketch, "E416", {"start": v(8.6, -3.87) * mm, "end": v(8.55, -3.87) * mm});
            skLineSegment(sketch, "E417", {"start": v(8.55, -3.87) * mm, "end": v(7.5, -3.87) * mm});
            skLineSegment(sketch, "E418", {"start": v(7.5, -3.87) * mm, "end": v(7.44, -3.87) * mm});
            skLineSegment(sketch, "E419", {"start": v(7.44, -3.87) * mm, "end": v(7.44, -3.87) * mm});
            skLineSegment(sketch, "E420", {"start": v(7.44, -3.87) * mm, "end": v(7.38, -3.88) * mm});
            skLineSegment(sketch, "E421", {"start": v(7.38, -3.88) * mm, "end": v(7.27, -3.91) * mm});
            skLineSegment(sketch, "E422", {"start": v(7.27, -3.91) * mm, "end": v(7.17, -3.97) * mm});
            skLineSegment(sketch, "E423", {"start": v(7.17, -3.97) * mm, "end": v(7.08, -4.04) * mm});
            skLineSegment(sketch, "E424", {"start": v(7.08, -4.04) * mm, "end": v(7, -4.13) * mm});
            skLineSegment(sketch, "E425", {"start": v(7, -4.13) * mm, "end": v(6.95, -4.23) * mm});
            skLineSegment(sketch, "E426", {"start": v(6.95, -4.23) * mm, "end": v(6.92, -4.34) * mm});
            skLineSegment(sketch, "E427", {"start": v(6.92, -4.34) * mm, "end": v(6.91, -4.4) * mm});
            skLineSegment(sketch, "E428", {"start": v(6.91, -4.4) * mm, "end": v(6.9, -4.4) * mm});
            skLineSegment(sketch, "E429", {"start": v(6.9, -4.4) * mm, "end": v(6.9, -4.45) * mm});
            skLineSegment(sketch, "E430", {"start": v(6.9, -4.45) * mm, "end": v(6.9, -5.51) * mm});
            skLineSegment(sketch, "E431", {"start": v(6.9, -5.51) * mm, "end": v(6.9, -5.56) * mm});
            skLineSegment(sketch, "E432", {"start": v(6.9, -5.56) * mm, "end": v(6.91, -5.56) * mm});
            skLineSegment(sketch, "E433", {"start": v(6.91, -5.56) * mm, "end": v(6.92, -5.63) * mm});
            skLineSegment(sketch, "E434", {"start": v(6.92, -5.63) * mm, "end": v(6.95, -5.74) * mm});
            skLineSegment(sketch, "E435", {"start": v(6.95, -5.74) * mm, "end": v(6.95, -5.74) * mm});
            skLineSegment(sketch, "E436", {"start": v(6.95, -5.74) * mm, "end": v(5.03, -7.66) * mm});
            skLineSegment(sketch, "E437", {"start": v(5.03, -7.66) * mm, "end": v(5, -7.7) * mm});
            skLineSegment(sketch, "E438", {"start": v(5, -7.7) * mm, "end": v(4.99, -7.73) * mm});
            skLineSegment(sketch, "E439", {"start": v(4.99, -7.73) * mm, "end": v(4.97, -7.77) * mm});
            skLineSegment(sketch, "E440", {"start": v(4.97, -7.77) * mm, "end": v(4.97, -7.82) * mm});
            skLineSegment(sketch, "E441", {"start": v(4.97, -7.82) * mm, "end": v(4.97, -9.35) * mm});
            skLineSegment(sketch, "E442", {"start": v(4.97, -9.35) * mm, "end": v(3.51, -10.8) * mm});
            skLineSegment(sketch, "E443", {"start": v(3.51, -10.8) * mm, "end": v(3.45, -10.68) * mm});
            skLineSegment(sketch, "E444", {"start": v(3.45, -10.68) * mm, "end": v(3.36, -10.57) * mm});
            skLineSegment(sketch, "E445", {"start": v(3.36, -10.57) * mm, "end": v(3.24, -10.47) * mm});
            skLineSegment(sketch, "E446", {"start": v(3.24, -10.47) * mm, "end": v(3.12, -10.4) * mm});
            skLineSegment(sketch, "E447", {"start": v(3.12, -10.4) * mm, "end": v(2.98, -10.36) * mm});
            skLineSegment(sketch, "E448", {"start": v(2.98, -10.36) * mm, "end": v(2.83, -10.35) * mm});
            skLineSegment(sketch, "E449", {"start": v(2.83, -10.35) * mm, "end": v(2.69, -10.36) * mm});
            skLineSegment(sketch, "E450", {"start": v(2.69, -10.36) * mm, "end": v(2.55, -10.4) * mm});
            skLineSegment(sketch, "E451", {"start": v(2.55, -10.4) * mm, "end": v(2.42, -10.47) * mm});
            skLineSegment(sketch, "E452", {"start": v(2.42, -10.47) * mm, "end": v(2.3, -10.57) * mm});
            skLineSegment(sketch, "E453", {"start": v(2.3, -10.57) * mm, "end": v(2.21, -10.68) * mm});
            skLineSegment(sketch, "E454", {"start": v(2.21, -10.68) * mm, "end": v(2.15, -10.8) * mm});
            skLineSegment(sketch, "E455", {"start": v(2.15, -10.8) * mm, "end": v(2.1, -10.95) * mm});
            skLineSegment(sketch, "E456", {"start": v(2.1, -10.95) * mm, "end": v(2.09, -11.1) * mm});
            skLineSegment(sketch, "E457", {"start": v(2.09, -11.1) * mm, "end": v(2.1, -11.24) * mm});
            skLineSegment(sketch, "E458", {"start": v(2.1, -11.24) * mm, "end": v(2.15, -11.38) * mm});
            skLineSegment(sketch, "E459", {"start": v(2.15, -11.38) * mm, "end": v(2.21, -11.5) * mm});
            skLineSegment(sketch, "E460", {"start": v(2.21, -11.5) * mm, "end": v(2.3, -11.62) * mm});
            skLineSegment(sketch, "E461", {"start": v(2.3, -11.62) * mm, "end": v(2.42, -11.7) * mm});
            skLineSegment(sketch, "E462", {"start": v(2.42, -11.7) * mm, "end": v(2.55, -11.78) * mm});
            skLineSegment(sketch, "E463", {"start": v(2.55, -11.78) * mm, "end": v(2.69, -11.82) * mm});
            skLineSegment(sketch, "E464", {"start": v(2.69, -11.82) * mm, "end": v(2.83, -11.83) * mm});
            skLineSegment(sketch, "E465", {"start": v(2.83, -11.83) * mm, "end": v(2.98, -11.82) * mm});
            skLineSegment(sketch, "E466", {"start": v(2.98, -11.82) * mm, "end": v(3.12, -11.78) * mm});
            skLineSegment(sketch, "E467", {"start": v(3.12, -11.78) * mm, "end": v(3.24, -11.7) * mm});
            skLineSegment(sketch, "E468", {"start": v(3.24, -11.7) * mm, "end": v(3.36, -11.62) * mm});
            skLineSegment(sketch, "E469", {"start": v(3.36, -11.62) * mm, "end": v(3.45, -11.5) * mm});
            skLineSegment(sketch, "E470", {"start": v(3.45, -11.5) * mm, "end": v(3.52, -11.38) * mm});
            skLineSegment(sketch, "E471", {"start": v(3.52, -11.38) * mm, "end": v(3.54, -11.31) * mm});
            skLineSegment(sketch, "E472", {"start": v(3.54, -11.31) * mm, "end": v(3.54, -11.31) * mm});
            skLineSegment(sketch, "E473", {"start": v(3.54, -11.31) * mm, "end": v(3.58, -11.31) * mm});
            skLineSegment(sketch, "E474", {"start": v(3.58, -11.31) * mm, "end": v(3.63, -11.3) * mm});
            skLineSegment(sketch, "E475", {"start": v(3.63, -11.3) * mm, "end": v(3.66, -11.28) * mm});
            skLineSegment(sketch, "E476", {"start": v(3.66, -11.28) * mm, "end": v(3.7, -11.25) * mm});
            skLineSegment(sketch, "E477", {"start": v(3.7, -11.25) * mm, "end": v(5.35, -9.6) * mm});
            skLineSegment(sketch, "E478", {"start": v(5.35, -9.6) * mm, "end": v(5.38, -9.56) * mm});
            skLineSegment(sketch, "E479", {"start": v(5.38, -9.56) * mm, "end": v(5.4, -9.52) * mm});
            skLineSegment(sketch, "E480", {"start": v(5.4, -9.52) * mm, "end": v(5.41, -9.48) * mm});
            skLineSegment(sketch, "E481", {"start": v(5.41, -9.48) * mm, "end": v(5.41, -9.44) * mm});
            skLineSegment(sketch, "E482", {"start": v(5.41, -9.44) * mm, "end": v(5.41, -7.9) * mm});
            skLineSegment(sketch, "E483", {"start": v(5.41, -7.9) * mm, "end": v(7.27, -6.05) * mm});
            skLineSegment(sketch, "E484", {"start": v(7.27, -6.05) * mm, "end": v(7.27, -6.05) * mm});
            skLineSegment(sketch, "E485", {"start": v(7.27, -6.05) * mm, "end": v(7.38, -6.09) * mm});
            skLineSegment(sketch, "E486", {"start": v(7.38, -6.09) * mm, "end": v(7.44, -6.1) * mm});
            skLineSegment(sketch, "E487", {"start": v(7.44, -6.1) * mm, "end": v(7.44, -6.1) * mm});
            skLineSegment(sketch, "E488", {"start": v(7.44, -6.1) * mm, "end": v(7.5, -6.1) * mm});
            skLineSegment(sketch, "E489", {"start": v(7.5, -6.1) * mm, "end": v(8.55, -6.1) * mm});
            skLineSegment(sketch, "E490", {"start": v(8.55, -6.1) * mm, "end": v(8.6, -6.1) * mm});
            skLineSegment(sketch, "E491", {"start": v(8.6, -6.1) * mm, "end": v(8.6, -6.1) * mm});
            skLineSegment(sketch, "E492", {"start": v(8.6, -6.1) * mm, "end": v(8.67, -6.09) * mm});
            skLineSegment(sketch, "E493", {"start": v(8.67, -6.09) * mm, "end": v(8.78, -6.05) * mm});
            skLineSegment(sketch, "E494", {"start": v(8.78, -6.05) * mm, "end": v(8.88, -6) * mm});
            skLineSegment(sketch, "E495", {"start": v(8.88, -6) * mm, "end": v(8.97, -5.93) * mm});
            skLineSegment(sketch, "E496", {"start": v(8.97, -5.93) * mm, "end": v(9.04, -5.84) * mm});
            skLineSegment(sketch, "E497", {"start": v(8.64, -6.13) * mm, "end": v(8.64, -6.12) * mm});
            skLineSegment(sketch, "E498", {"start": v(8.64, -6.12) * mm, "end": v(8.56, -6.13) * mm});
            skLineSegment(sketch, "E499", {"start": v(8.56, -6.13) * mm, "end": v(8.64, -6.13) * mm});
            skLineSegment(sketch, "E500", {"start": v(7.5, -6.13) * mm, "end": v(8.55, -6.13) * mm});
            skLineSegment(sketch, "E501", {"start": v(7.48, -6.13) * mm, "end": v(7.41, -6.12) * mm});
            skLineSegment(sketch, "E502", {"start": v(7.41, -6.12) * mm, "end": v(7.41, -6.13) * mm});
            skLineSegment(sketch, "E503", {"start": v(7.41, -6.13) * mm, "end": v(7.48, -6.13) * mm});
            skLineSegment(sketch, "E504", {"start": v(8.64, -3.84) * mm, "end": v(8.64, -3.84) * mm});
            skLineSegment(sketch, "E505", {"start": v(8.64, -3.84) * mm, "end": v(8.56, -3.84) * mm});
            skLineSegment(sketch, "E506", {"start": v(8.56, -3.84) * mm, "end": v(8.64, -3.84) * mm});
            skLineSegment(sketch, "E507", {"start": v(8.55, -3.84) * mm, "end": v(7.5, -3.84) * mm});
            skLineSegment(sketch, "E508", {"start": v(9.15, -1.5) * mm, "end": v(9.08, -1.3) * mm});
            skLineSegment(sketch, "E509", {"start": v(9.08, -1.3) * mm, "end": v(8.98, -1.1) * mm});
            skLineSegment(sketch, "E510", {"start": v(8.98, -1.1) * mm, "end": v(8.83, -0.92) * mm});
            skLineSegment(sketch, "E511", {"start": v(8.83, -0.92) * mm, "end": v(8.66, -0.78) * mm});
            skLineSegment(sketch, "E512", {"start": v(8.66, -0.78) * mm, "end": v(8.46, -0.67) * mm});
            skLineSegment(sketch, "E513", {"start": v(8.46, -0.67) * mm, "end": v(8.25, -0.6) * mm});
            skLineSegment(sketch, "E514", {"start": v(8.25, -0.6) * mm, "end": v(8.02, -0.59) * mm});
            skLineSegment(sketch, "E515", {"start": v(8.02, -0.59) * mm, "end": v(7.8, -0.6) * mm});
            skLineSegment(sketch, "E516", {"start": v(7.8, -0.6) * mm, "end": v(7.58, -0.67) * mm});
            skLineSegment(sketch, "E517", {"start": v(7.58, -0.67) * mm, "end": v(7.39, -0.78) * mm});
            skLineSegment(sketch, "E518", {"start": v(7.39, -0.78) * mm, "end": v(7.21, -0.92) * mm});
            skLineSegment(sketch, "E519", {"start": v(7.21, -0.92) * mm, "end": v(7.07, -1.1) * mm});
            skLineSegment(sketch, "E520", {"start": v(7.07, -1.1) * mm, "end": v(6.96, -1.3) * mm});
            skLineSegment(sketch, "E521", {"start": v(6.96, -1.3) * mm, "end": v(6.9, -1.5) * mm});
            skLineSegment(sketch, "E522", {"start": v(6.9, -1.5) * mm, "end": v(6.88, -1.73) * mm});
            skLineSegment(sketch, "E523", {"start": v(6.88, -1.73) * mm, "end": v(6.9, -1.96) * mm});
            skLineSegment(sketch, "E524", {"start": v(6.9, -1.96) * mm, "end": v(6.96, -2.17) * mm});
            skLineSegment(sketch, "E525", {"start": v(6.96, -2.17) * mm, "end": v(7.07, -2.37) * mm});
            skLineSegment(sketch, "E526", {"start": v(7.07, -2.37) * mm, "end": v(7.21, -2.54) * mm});
            skLineSegment(sketch, "E527", {"start": v(7.21, -2.54) * mm, "end": v(7.39, -2.68) * mm});
            skLineSegment(sketch, "E528", {"start": v(7.39, -2.68) * mm, "end": v(7.58, -2.8) * mm});
            skLineSegment(sketch, "E529", {"start": v(7.58, -2.8) * mm, "end": v(7.8, -2.86) * mm});
            skLineSegment(sketch, "E530", {"start": v(7.8, -2.86) * mm, "end": v(8.02, -2.88) * mm});
            skLineSegment(sketch, "E531", {"start": v(8.02, -2.88) * mm, "end": v(8.25, -2.86) * mm});
            skLineSegment(sketch, "E532", {"start": v(8.25, -2.86) * mm, "end": v(8.46, -2.8) * mm});
            skLineSegment(sketch, "E533", {"start": v(8.46, -2.8) * mm, "end": v(8.66, -2.68) * mm});
            skLineSegment(sketch, "E534", {"start": v(8.66, -2.68) * mm, "end": v(8.83, -2.54) * mm});
            skLineSegment(sketch, "E535", {"start": v(8.83, -2.54) * mm, "end": v(8.98, -2.37) * mm});
            skLineSegment(sketch, "E536", {"start": v(8.98, -2.37) * mm, "end": v(9.08, -2.17) * mm});
            skLineSegment(sketch, "E537", {"start": v(9.08, -2.17) * mm, "end": v(9.15, -1.96) * mm});
            skLineSegment(sketch, "E538", {"start": v(7.48, -3.84) * mm, "end": v(7.41, -3.84) * mm});
            skLineSegment(sketch, "E539", {"start": v(7.41, -3.84) * mm, "end": v(7.41, -3.84) * mm});
            skLineSegment(sketch, "E540", {"start": v(7.41, -3.84) * mm, "end": v(7.48, -3.84) * mm});
            skLineSegment(sketch, "E541", {"start": v(3.54, -10.78) * mm, "end": v(3.48, -10.66) * mm});
            skLineSegment(sketch, "E542", {"start": v(3.48, -10.66) * mm, "end": v(3.38, -10.54) * mm});
            skLineSegment(sketch, "E543", {"start": v(3.38, -10.54) * mm, "end": v(3.26, -10.45) * mm});
            skLineSegment(sketch, "E544", {"start": v(3.26, -10.45) * mm, "end": v(3.13, -10.38) * mm});
            skLineSegment(sketch, "E545", {"start": v(3.13, -10.38) * mm, "end": v(2.98, -10.33) * mm});
            skLineSegment(sketch, "E546", {"start": v(2.98, -10.33) * mm, "end": v(2.83, -10.32) * mm});
            skLineSegment(sketch, "E547", {"start": v(2.83, -10.32) * mm, "end": v(2.68, -10.33) * mm});
            skLineSegment(sketch, "E548", {"start": v(2.68, -10.33) * mm, "end": v(2.54, -10.38) * mm});
            skLineSegment(sketch, "E549", {"start": v(2.54, -10.38) * mm, "end": v(2.4, -10.45) * mm});
            skLineSegment(sketch, "E550", {"start": v(2.4, -10.45) * mm, "end": v(2.28, -10.54) * mm});
            skLineSegment(sketch, "E551", {"start": v(2.28, -10.54) * mm, "end": v(2.19, -10.66) * mm});
            skLineSegment(sketch, "E552", {"start": v(2.19, -10.66) * mm, "end": v(2.12, -10.8) * mm});
            skLineSegment(sketch, "E553", {"start": v(2.12, -10.8) * mm, "end": v(2.07, -10.94) * mm});
            skLineSegment(sketch, "E554", {"start": v(2.07, -10.94) * mm, "end": v(2.06, -11.1) * mm});
            skLineSegment(sketch, "E555", {"start": v(2.06, -11.1) * mm, "end": v(2.07, -11.24) * mm});
            skLineSegment(sketch, "E556", {"start": v(2.07, -11.24) * mm, "end": v(2.12, -11.39) * mm});
            skLineSegment(sketch, "E557", {"start": v(2.12, -11.39) * mm, "end": v(2.19, -11.52) * mm});
            skLineSegment(sketch, "E558", {"start": v(2.19, -11.52) * mm, "end": v(2.28, -11.64) * mm});
            skLineSegment(sketch, "E559", {"start": v(2.28, -11.64) * mm, "end": v(2.4, -11.73) * mm});
            skLineSegment(sketch, "E560", {"start": v(2.4, -11.73) * mm, "end": v(2.54, -11.8) * mm});
            skLineSegment(sketch, "E561", {"start": v(2.54, -11.8) * mm, "end": v(2.68, -11.85) * mm});
            skLineSegment(sketch, "E562", {"start": v(2.68, -11.85) * mm, "end": v(2.83, -11.87) * mm});
            skLineSegment(sketch, "E563", {"start": v(2.83, -11.87) * mm, "end": v(2.98, -11.85) * mm});
            skLineSegment(sketch, "E564", {"start": v(2.98, -11.85) * mm, "end": v(3.13, -11.8) * mm});
            skLineSegment(sketch, "E565", {"start": v(3.13, -11.8) * mm, "end": v(3.26, -11.73) * mm});
            skLineSegment(sketch, "E566", {"start": v(3.26, -11.73) * mm, "end": v(3.38, -11.64) * mm});
            skLineSegment(sketch, "E567", {"start": v(3.38, -11.64) * mm, "end": v(3.48, -11.52) * mm});
            skLineSegment(sketch, "E568", {"start": v(3.48, -11.52) * mm, "end": v(3.55, -11.39) * mm});
            skLineSegment(sketch, "E569", {"start": v(3.55, -11.39) * mm, "end": v(3.57, -11.31) * mm});
            skLineSegment(sketch, "E570", {"start": v(2.6, -7.96) * mm, "end": v(2.06, -7.96) * mm});
            skLineSegment(sketch, "E571", {"start": v(2.06, -7.96) * mm, "end": v(2.06, -9.5) * mm});
            skLineSegment(sketch, "E572", {"start": v(2.06, -9.5) * mm, "end": v(3.6, -9.5) * mm});
            skLineSegment(sketch, "E573", {"start": v(3.6, -9.5) * mm, "end": v(3.6, -7.96) * mm});
            skLineSegment(sketch, "E574", {"start": v(3.6, -7.96) * mm, "end": v(3.06, -7.96) * mm});
            skLineSegment(sketch, "E575", {"start": v(3.58, -9.47) * mm, "end": v(3.58, -7.99) * mm});
            skLineSegment(sketch, "E576", {"start": v(3.58, -7.99) * mm, "end": v(3.06, -7.99) * mm});
            skLineSegment(sketch, "E577", {"start": v(3.06, -7.99) * mm, "end": v(3.06, -6.13) * mm});
            skLineSegment(sketch, "E578", {"start": v(3.06, -6.13) * mm, "end": v(3.12, -6.11) * mm});
            skLineSegment(sketch, "E579", {"start": v(3.12, -6.11) * mm, "end": v(3.24, -6.05) * mm});
            skLineSegment(sketch, "E580", {"start": v(3.24, -6.05) * mm, "end": v(3.36, -5.95) * mm});
            skLineSegment(sketch, "E581", {"start": v(3.36, -5.95) * mm, "end": v(3.45, -5.84) * mm});
            skLineSegment(sketch, "E582", {"start": v(3.45, -5.84) * mm, "end": v(3.52, -5.71) * mm});
            skLineSegment(sketch, "E583", {"start": v(3.52, -5.71) * mm, "end": v(3.56, -5.57) * mm});
            skLineSegment(sketch, "E584", {"start": v(3.56, -5.57) * mm, "end": v(3.58, -5.43) * mm});
            skLineSegment(sketch, "E585", {"start": v(3.58, -5.43) * mm, "end": v(3.56, -5.28) * mm});
            skLineSegment(sketch, "E586", {"start": v(3.56, -5.28) * mm, "end": v(3.52, -5.14) * mm});
            skLineSegment(sketch, "E587", {"start": v(3.52, -5.14) * mm, "end": v(3.45, -5.01) * mm});
            skLineSegment(sketch, "E588", {"start": v(3.45, -5.01) * mm, "end": v(3.36, -4.9) * mm});
            skLineSegment(sketch, "E589", {"start": v(3.36, -4.9) * mm, "end": v(3.24, -4.8) * mm});
            skLineSegment(sketch, "E590", {"start": v(3.24, -4.8) * mm, "end": v(3.12, -4.74) * mm});
            skLineSegment(sketch, "E591", {"start": v(3.12, -4.74) * mm, "end": v(2.98, -4.7) * mm});
            skLineSegment(sketch, "E592", {"start": v(2.98, -4.7) * mm, "end": v(2.83, -4.68) * mm});
            skLineSegment(sketch, "E593", {"start": v(2.83, -4.68) * mm, "end": v(2.69, -4.7) * mm});
            skLineSegment(sketch, "E594", {"start": v(2.69, -4.7) * mm, "end": v(2.55, -4.74) * mm});
            skLineSegment(sketch, "E595", {"start": v(2.55, -4.74) * mm, "end": v(2.42, -4.8) * mm});
            skLineSegment(sketch, "E596", {"start": v(2.42, -4.8) * mm, "end": v(2.3, -4.9) * mm});
            skLineSegment(sketch, "E597", {"start": v(2.3, -4.9) * mm, "end": v(2.21, -5.01) * mm});
            skLineSegment(sketch, "E598", {"start": v(2.21, -5.01) * mm, "end": v(2.15, -5.14) * mm});
            skLineSegment(sketch, "E599", {"start": v(2.15, -5.14) * mm, "end": v(2.1, -5.28) * mm});
            skLineSegment(sketch, "E600", {"start": v(2.1, -5.28) * mm, "end": v(2.09, -5.43) * mm});
            skLineSegment(sketch, "E601", {"start": v(2.09, -5.43) * mm, "end": v(2.1, -5.57) * mm});
            skLineSegment(sketch, "E602", {"start": v(2.1, -5.57) * mm, "end": v(2.15, -5.71) * mm});
            skLineSegment(sketch, "E603", {"start": v(2.15, -5.71) * mm, "end": v(2.21, -5.84) * mm});
            skLineSegment(sketch, "E604", {"start": v(2.21, -5.84) * mm, "end": v(2.3, -5.95) * mm});
            skLineSegment(sketch, "E605", {"start": v(2.3, -5.95) * mm, "end": v(2.42, -6.05) * mm});
            skLineSegment(sketch, "E606", {"start": v(2.42, -6.05) * mm, "end": v(2.55, -6.11) * mm});
            skLineSegment(sketch, "E607", {"start": v(2.55, -6.11) * mm, "end": v(2.6, -6.13) * mm});
            skLineSegment(sketch, "E608", {"start": v(2.6, -6.13) * mm, "end": v(2.6, -7.99) * mm});
            skLineSegment(sketch, "E609", {"start": v(2.6, -7.99) * mm, "end": v(2.09, -7.99) * mm});
            skLineSegment(sketch, "E610", {"start": v(2.09, -7.99) * mm, "end": v(2.09, -9.47) * mm});
            skLineSegment(sketch, "E611", {"start": v(2.09, -9.47) * mm, "end": v(3.58, -9.47) * mm});
            skLineSegment(sketch, "E612", {"start": v(8.97, 0.57) * mm, "end": v(9.04, 0.66) * mm});
            skLineSegment(sketch, "E613", {"start": v(9.04, 0.66) * mm, "end": v(9.1, 0.76) * mm});
            skLineSegment(sketch, "E614", {"start": v(9.1, 0.76) * mm, "end": v(9.13, 0.87) * mm});
            skLineSegment(sketch, "E615", {"start": v(9.13, 0.87) * mm, "end": v(9.13, 0.94) * mm});
            skLineSegment(sketch, "E616", {"start": v(9.13, 0.94) * mm, "end": v(9.14, 0.94) * mm});
            skLineSegment(sketch, "E617", {"start": v(9.14, 0.94) * mm, "end": v(9.14, 0.99) * mm});
            skLineSegment(sketch, "E618", {"start": v(9.14, 0.99) * mm, "end": v(9.14, 2.06) * mm});
            skLineSegment(sketch, "E619", {"start": v(9.14, 2.06) * mm, "end": v(9.14, 2.1) * mm});
            skLineSegment(sketch, "E620", {"start": v(9.14, 2.1) * mm, "end": v(9.13, 2.1) * mm});
            skLineSegment(sketch, "E621", {"start": v(9.13, 2.1) * mm, "end": v(9.13, 2.17) * mm});
            skLineSegment(sketch, "E622", {"start": v(9.13, 2.17) * mm, "end": v(9.1, 2.28) * mm});
            skLineSegment(sketch, "E623", {"start": v(9.1, 2.28) * mm, "end": v(9.04, 2.38) * mm});
            skLineSegment(sketch, "E624", {"start": v(9.04, 2.38) * mm, "end": v(8.97, 2.46) * mm});
            skLineSegment(sketch, "E625", {"start": v(8.97, 2.46) * mm, "end": v(8.88, 2.54) * mm});
            skLineSegment(sketch, "E626", {"start": v(8.88, 2.54) * mm, "end": v(8.78, 2.6) * mm});
            skLineSegment(sketch, "E627", {"start": v(8.78, 2.6) * mm, "end": v(8.67, 2.62) * mm});
            skLineSegment(sketch, "E628", {"start": v(8.67, 2.62) * mm, "end": v(8.6, 2.63) * mm});
            skLineSegment(sketch, "E629", {"start": v(8.6, 2.63) * mm, "end": v(8.6, 2.63) * mm});
            skLineSegment(sketch, "E630", {"start": v(8.6, 2.63) * mm, "end": v(8.55, 2.63) * mm});
            skLineSegment(sketch, "E631", {"start": v(8.55, 2.63) * mm, "end": v(7.5, 2.63) * mm});
            skLineSegment(sketch, "E632", {"start": v(7.5, 2.63) * mm, "end": v(7.44, 2.63) * mm});
            skLineSegment(sketch, "E633", {"start": v(7.44, 2.63) * mm, "end": v(7.44, 2.63) * mm});
            skLineSegment(sketch, "E634", {"start": v(7.44, 2.63) * mm, "end": v(7.38, 2.62) * mm});
            skLineSegment(sketch, "E635", {"start": v(7.38, 2.62) * mm, "end": v(7.27, 2.6) * mm});
            skLineSegment(sketch, "E636", {"start": v(7.27, 2.6) * mm, "end": v(7.17, 2.54) * mm});
            skLineSegment(sketch, "E637", {"start": v(7.17, 2.54) * mm, "end": v(7.08, 2.46) * mm});
            skLineSegment(sketch, "E638", {"start": v(7.08, 2.46) * mm, "end": v(7, 2.38) * mm});
            skLineSegment(sketch, "E639", {"start": v(7, 2.38) * mm, "end": v(6.95, 2.28) * mm});
            skLineSegment(sketch, "E640", {"start": v(6.95, 2.28) * mm, "end": v(6.92, 2.17) * mm});
            skLineSegment(sketch, "E641", {"start": v(6.92, 2.17) * mm, "end": v(6.91, 2.1) * mm});
            skLineSegment(sketch, "E642", {"start": v(6.91, 2.1) * mm, "end": v(6.9, 2.1) * mm});
            skLineSegment(sketch, "E643", {"start": v(6.9, 2.1) * mm, "end": v(6.9, 2.06) * mm});
            skLineSegment(sketch, "E644", {"start": v(6.9, 2.06) * mm, "end": v(6.9, 0.99) * mm});
            skLineSegment(sketch, "E645", {"start": v(6.9, 0.99) * mm, "end": v(6.9, 0.94) * mm});
            skLineSegment(sketch, "E646", {"start": v(6.9, 0.94) * mm, "end": v(6.91, 0.94) * mm});
            skLineSegment(sketch, "E647", {"start": v(6.91, 0.94) * mm, "end": v(6.92, 0.87) * mm});
            skLineSegment(sketch, "E648", {"start": v(6.92, 0.87) * mm, "end": v(6.95, 0.76) * mm});
            skLineSegment(sketch, "E649", {"start": v(6.95, 0.76) * mm, "end": v(6.95, 0.76) * mm});
            skLineSegment(sketch, "E650", {"start": v(6.95, 0.76) * mm, "end": v(3.82, -2.37) * mm});
            skLineSegment(sketch, "E651", {"start": v(3.82, -2.37) * mm, "end": v(3.54, -2.37) * mm});
            skLineSegment(sketch, "E652", {"start": v(3.54, -2.37) * mm, "end": v(3.52, -2.31) * mm});
            skLineSegment(sketch, "E653", {"start": v(3.52, -2.31) * mm, "end": v(3.45, -2.18) * mm});
            skLineSegment(sketch, "E654", {"start": v(3.45, -2.18) * mm, "end": v(3.36, -2.07) * mm});
            skLineSegment(sketch, "E655", {"start": v(3.36, -2.07) * mm, "end": v(3.24, -1.98) * mm});
            skLineSegment(sketch, "E656", {"start": v(3.24, -1.98) * mm, "end": v(3.12, -1.9) * mm});
            skLineSegment(sketch, "E657", {"start": v(3.12, -1.9) * mm, "end": v(2.98, -1.87) * mm});
            skLineSegment(sketch, "E658", {"start": v(2.98, -1.87) * mm, "end": v(2.83, -1.85) * mm});
            skLineSegment(sketch, "E659", {"start": v(2.83, -1.85) * mm, "end": v(2.69, -1.87) * mm});
            skLineSegment(sketch, "E660", {"start": v(2.69, -1.87) * mm, "end": v(2.55, -1.9) * mm});
            skLineSegment(sketch, "E661", {"start": v(2.55, -1.9) * mm, "end": v(2.42, -1.98) * mm});
            skLineSegment(sketch, "E662", {"start": v(2.42, -1.98) * mm, "end": v(2.3, -2.07) * mm});
            skLineSegment(sketch, "E663", {"start": v(2.3, -2.07) * mm, "end": v(2.21, -2.18) * mm});
            skLineSegment(sketch, "E664", {"start": v(2.21, -2.18) * mm, "end": v(2.15, -2.31) * mm});
            skLineSegment(sketch, "E665", {"start": v(2.15, -2.31) * mm, "end": v(2.1, -2.45) * mm});
            skLineSegment(sketch, "E666", {"start": v(2.1, -2.45) * mm, "end": v(2.09, -2.6) * mm});
            skLineSegment(sketch, "E667", {"start": v(2.09, -2.6) * mm, "end": v(2.1, -2.74) * mm});
            skLineSegment(sketch, "E668", {"start": v(2.1, -2.74) * mm, "end": v(2.15, -2.88) * mm});
            skLineSegment(sketch, "E669", {"start": v(2.15, -2.88) * mm, "end": v(2.21, -3) * mm});
            skLineSegment(sketch, "E670", {"start": v(2.21, -3) * mm, "end": v(2.3, -3.12) * mm});
            skLineSegment(sketch, "E671", {"start": v(2.3, -3.12) * mm, "end": v(2.42, -3.21) * mm});
            skLineSegment(sketch, "E672", {"start": v(2.42, -3.21) * mm, "end": v(2.55, -3.28) * mm});
            skLineSegment(sketch, "E673", {"start": v(2.55, -3.28) * mm, "end": v(2.69, -3.32) * mm});
            skLineSegment(sketch, "E674", {"start": v(2.69, -3.32) * mm, "end": v(2.83, -3.34) * mm});
            skLineSegment(sketch, "E675", {"start": v(2.83, -3.34) * mm, "end": v(2.98, -3.32) * mm});
            skLineSegment(sketch, "E676", {"start": v(2.98, -3.32) * mm, "end": v(3.12, -3.28) * mm});
            skLineSegment(sketch, "E677", {"start": v(3.12, -3.28) * mm, "end": v(3.24, -3.21) * mm});
            skLineSegment(sketch, "E678", {"start": v(3.24, -3.21) * mm, "end": v(3.36, -3.12) * mm});
            skLineSegment(sketch, "E679", {"start": v(3.36, -3.12) * mm, "end": v(3.45, -3) * mm});
            skLineSegment(sketch, "E680", {"start": v(3.45, -3) * mm, "end": v(3.52, -2.88) * mm});
            skLineSegment(sketch, "E681", {"start": v(3.52, -2.88) * mm, "end": v(3.54, -2.82) * mm});
            skLineSegment(sketch, "E682", {"start": v(3.54, -2.82) * mm, "end": v(3.9, -2.82) * mm});
            skLineSegment(sketch, "E683", {"start": v(3.9, -2.82) * mm, "end": v(3.95, -2.81) * mm});
            skLineSegment(sketch, "E684", {"start": v(3.95, -2.81) * mm, "end": v(4, -2.8) * mm});
            skLineSegment(sketch, "E685", {"start": v(4, -2.8) * mm, "end": v(4.03, -2.78) * mm});
            skLineSegment(sketch, "E686", {"start": v(4.03, -2.78) * mm, "end": v(4.07, -2.75) * mm});
            skLineSegment(sketch, "E687", {"start": v(4.07, -2.75) * mm, "end": v(7.27, 0.45) * mm});
            skLineSegment(sketch, "E688", {"start": v(7.27, 0.45) * mm, "end": v(7.27, 0.45) * mm});
            skLineSegment(sketch, "E689", {"start": v(7.27, 0.45) * mm, "end": v(7.38, 0.42) * mm});
            skLineSegment(sketch, "E690", {"start": v(7.38, 0.42) * mm, "end": v(7.44, 0.4) * mm});
            skLineSegment(sketch, "E691", {"start": v(7.44, 0.4) * mm, "end": v(7.44, 0.4) * mm});
            skLineSegment(sketch, "E692", {"start": v(7.44, 0.4) * mm, "end": v(7.5, 0.4) * mm});
            skLineSegment(sketch, "E693", {"start": v(7.5, 0.4) * mm, "end": v(8.55, 0.4) * mm});
            skLineSegment(sketch, "E694", {"start": v(8.55, 0.4) * mm, "end": v(8.6, 0.4) * mm});
            skLineSegment(sketch, "E695", {"start": v(8.6, 0.4) * mm, "end": v(8.6, 0.4) * mm});
            skLineSegment(sketch, "E696", {"start": v(8.6, 0.4) * mm, "end": v(8.67, 0.42) * mm});
            skLineSegment(sketch, "E697", {"start": v(8.67, 0.42) * mm, "end": v(8.78, 0.45) * mm});
            skLineSegment(sketch, "E698", {"start": v(8.78, 0.45) * mm, "end": v(8.88, 0.5) * mm});
            skLineSegment(sketch, "E699", {"start": v(8.88, 0.5) * mm, "end": v(8.97, 0.57) * mm});
            skLineSegment(sketch, "E700", {"start": v(8.64, 0.37) * mm, "end": v(8.64, 0.38) * mm});
            skLineSegment(sketch, "E701", {"start": v(8.64, 0.38) * mm, "end": v(8.56, 0.37) * mm});
            skLineSegment(sketch, "E702", {"start": v(8.56, 0.37) * mm, "end": v(8.64, 0.37) * mm});
            skLineSegment(sketch, "E703", {"start": v(3.06, -6.17) * mm, "end": v(3.13, -6.14) * mm});
            skLineSegment(sketch, "E704", {"start": v(3.13, -6.14) * mm, "end": v(3.26, -6.07) * mm});
            skLineSegment(sketch, "E705", {"start": v(3.26, -6.07) * mm, "end": v(3.38, -5.98) * mm});
            skLineSegment(sketch, "E706", {"start": v(3.38, -5.98) * mm, "end": v(3.48, -5.86) * mm});
            skLineSegment(sketch, "E707", {"start": v(3.48, -5.86) * mm, "end": v(3.55, -5.72) * mm});
            skLineSegment(sketch, "E708", {"start": v(3.55, -5.72) * mm, "end": v(3.6, -5.58) * mm});
            skLineSegment(sketch, "E709", {"start": v(3.6, -5.58) * mm, "end": v(3.6, -5.43) * mm});
            skLineSegment(sketch, "E710", {"start": v(3.6, -5.43) * mm, "end": v(3.6, -5.28) * mm});
            skLineSegment(sketch, "E711", {"start": v(3.6, -5.28) * mm, "end": v(3.55, -5.13) * mm});
            skLineSegment(sketch, "E712", {"start": v(3.55, -5.13) * mm, "end": v(3.48, -5) * mm});
            skLineSegment(sketch, "E713", {"start": v(3.48, -5) * mm, "end": v(3.38, -4.88) * mm});
            skLineSegment(sketch, "E714", {"start": v(3.38, -4.88) * mm, "end": v(3.26, -4.78) * mm});
            skLineSegment(sketch, "E715", {"start": v(3.26, -4.78) * mm, "end": v(3.13, -4.71) * mm});
            skLineSegment(sketch, "E716", {"start": v(3.13, -4.71) * mm, "end": v(2.98, -4.67) * mm});
            skLineSegment(sketch, "E717", {"start": v(2.98, -4.67) * mm, "end": v(2.83, -4.65) * mm});
            skLineSegment(sketch, "E718", {"start": v(2.83, -4.65) * mm, "end": v(2.68, -4.67) * mm});
            skLineSegment(sketch, "E719", {"start": v(2.68, -4.67) * mm, "end": v(2.54, -4.71) * mm});
            skLineSegment(sketch, "E720", {"start": v(2.54, -4.71) * mm, "end": v(2.4, -4.78) * mm});
            skLineSegment(sketch, "E721", {"start": v(2.4, -4.78) * mm, "end": v(2.28, -4.88) * mm});
            skLineSegment(sketch, "E722", {"start": v(2.28, -4.88) * mm, "end": v(2.19, -5) * mm});
            skLineSegment(sketch, "E723", {"start": v(2.19, -5) * mm, "end": v(2.12, -5.13) * mm});
            skLineSegment(sketch, "E724", {"start": v(2.12, -5.13) * mm, "end": v(2.07, -5.28) * mm});
            skLineSegment(sketch, "E725", {"start": v(2.07, -5.28) * mm, "end": v(2.06, -5.43) * mm});
            skLineSegment(sketch, "E726", {"start": v(2.06, -5.43) * mm, "end": v(2.07, -5.58) * mm});
            skLineSegment(sketch, "E727", {"start": v(2.07, -5.58) * mm, "end": v(2.12, -5.72) * mm});
            skLineSegment(sketch, "E728", {"start": v(2.12, -5.72) * mm, "end": v(2.19, -5.86) * mm});
            skLineSegment(sketch, "E729", {"start": v(2.19, -5.86) * mm, "end": v(2.28, -5.98) * mm});
            skLineSegment(sketch, "E730", {"start": v(2.28, -5.98) * mm, "end": v(2.4, -6.07) * mm});
            skLineSegment(sketch, "E731", {"start": v(2.4, -6.07) * mm, "end": v(2.54, -6.14) * mm});
            skLineSegment(sketch, "E732", {"start": v(2.54, -6.14) * mm, "end": v(2.6, -6.17) * mm});
            skLineSegment(sketch, "E733", {"start": v(7.5, 0.37) * mm, "end": v(8.55, 0.37) * mm});
            skLineSegment(sketch, "E734", {"start": v(7.48, 0.37) * mm, "end": v(7.41, 0.38) * mm});
            skLineSegment(sketch, "E735", {"start": v(7.41, 0.38) * mm, "end": v(7.41, 0.37) * mm});
            skLineSegment(sketch, "E736", {"start": v(7.41, 0.37) * mm, "end": v(7.48, 0.37) * mm});
            skLineSegment(sketch, "E737", {"start": v(3.57, -2.37) * mm, "end": v(3.55, -2.3) * mm});
            skLineSegment(sketch, "E738", {"start": v(3.55, -2.3) * mm, "end": v(3.48, -2.17) * mm});
            skLineSegment(sketch, "E739", {"start": v(3.48, -2.17) * mm, "end": v(3.38, -2.05) * mm});
            skLineSegment(sketch, "E740", {"start": v(3.38, -2.05) * mm, "end": v(3.26, -1.95) * mm});
            skLineSegment(sketch, "E741", {"start": v(3.26, -1.95) * mm, "end": v(3.13, -1.88) * mm});
            skLineSegment(sketch, "E742", {"start": v(3.13, -1.88) * mm, "end": v(2.98, -1.84) * mm});
            skLineSegment(sketch, "E743", {"start": v(2.98, -1.84) * mm, "end": v(2.83, -1.82) * mm});
            skLineSegment(sketch, "E744", {"start": v(2.83, -1.82) * mm, "end": v(2.68, -1.84) * mm});
            skLineSegment(sketch, "E745", {"start": v(2.68, -1.84) * mm, "end": v(2.54, -1.88) * mm});
            skLineSegment(sketch, "E746", {"start": v(2.54, -1.88) * mm, "end": v(2.4, -1.95) * mm});
            skLineSegment(sketch, "E747", {"start": v(2.4, -1.95) * mm, "end": v(2.28, -2.05) * mm});
            skLineSegment(sketch, "E748", {"start": v(2.28, -2.05) * mm, "end": v(2.19, -2.17) * mm});
            skLineSegment(sketch, "E749", {"start": v(2.19, -2.17) * mm, "end": v(2.12, -2.3) * mm});
            skLineSegment(sketch, "E750", {"start": v(2.12, -2.3) * mm, "end": v(2.07, -2.44) * mm});
            skLineSegment(sketch, "E751", {"start": v(2.07, -2.44) * mm, "end": v(2.06, -2.6) * mm});
            skLineSegment(sketch, "E752", {"start": v(2.06, -2.6) * mm, "end": v(2.07, -2.75) * mm});
            skLineSegment(sketch, "E753", {"start": v(2.07, -2.75) * mm, "end": v(2.12, -2.9) * mm});
            skLineSegment(sketch, "E754", {"start": v(2.12, -2.9) * mm, "end": v(2.19, -3.03) * mm});
            skLineSegment(sketch, "E755", {"start": v(2.19, -3.03) * mm, "end": v(2.28, -3.14) * mm});
            skLineSegment(sketch, "E756", {"start": v(2.28, -3.14) * mm, "end": v(2.4, -3.24) * mm});
            skLineSegment(sketch, "E757", {"start": v(2.4, -3.24) * mm, "end": v(2.54, -3.31) * mm});
            skLineSegment(sketch, "E758", {"start": v(2.54, -3.31) * mm, "end": v(2.68, -3.36) * mm});
            skLineSegment(sketch, "E759", {"start": v(2.68, -3.36) * mm, "end": v(2.83, -3.37) * mm});
            skLineSegment(sketch, "E760", {"start": v(2.83, -3.37) * mm, "end": v(2.98, -3.36) * mm});
            skLineSegment(sketch, "E761", {"start": v(2.98, -3.36) * mm, "end": v(3.13, -3.31) * mm});
            skLineSegment(sketch, "E762", {"start": v(3.13, -3.31) * mm, "end": v(3.26, -3.24) * mm});
            skLineSegment(sketch, "E763", {"start": v(3.26, -3.24) * mm, "end": v(3.38, -3.14) * mm});
            skLineSegment(sketch, "E764", {"start": v(3.38, -3.14) * mm, "end": v(3.48, -3.03) * mm});
            skLineSegment(sketch, "E765", {"start": v(3.48, -3.03) * mm, "end": v(3.55, -2.9) * mm});
            skLineSegment(sketch, "E766", {"start": v(3.55, -2.9) * mm, "end": v(3.57, -2.82) * mm});
            skLineSegment(sketch, "E767", {"start": v(8.64, 2.66) * mm, "end": v(8.64, 2.67) * mm});
            skLineSegment(sketch, "E768", {"start": v(8.64, 2.67) * mm, "end": v(8.56, 2.67) * mm});
            skLineSegment(sketch, "E769", {"start": v(8.56, 2.67) * mm, "end": v(8.64, 2.66) * mm});
            skLineSegment(sketch, "E770", {"start": v(8.55, 2.67) * mm, "end": v(7.5, 2.67) * mm});
            skLineSegment(sketch, "E771", {"start": v(7.48, 2.67) * mm, "end": v(7.41, 2.67) * mm});
            skLineSegment(sketch, "E772", {"start": v(7.41, 2.67) * mm, "end": v(7.41, 2.66) * mm});
            skLineSegment(sketch, "E773", {"start": v(7.41, 2.66) * mm, "end": v(7.48, 2.67) * mm});
            skLineSegment(sketch, "E774", {"start": v(9.15, 4.94) * mm, "end": v(9.15, 5) * mm});
            skLineSegment(sketch, "E775", {"start": v(9.15, 5) * mm, "end": v(9.08, 5.21) * mm});
            skLineSegment(sketch, "E776", {"start": v(9.08, 5.21) * mm, "end": v(8.98, 5.4) * mm});
            skLineSegment(sketch, "E777", {"start": v(8.98, 5.4) * mm, "end": v(8.83, 5.58) * mm});
            skLineSegment(sketch, "E778", {"start": v(8.83, 5.58) * mm, "end": v(8.66, 5.72) * mm});
            skLineSegment(sketch, "E779", {"start": v(8.66, 5.72) * mm, "end": v(8.46, 5.83) * mm});
            skLineSegment(sketch, "E780", {"start": v(8.46, 5.83) * mm, "end": v(8.25, 5.9) * mm});
            skLineSegment(sketch, "E781", {"start": v(8.25, 5.9) * mm, "end": v(8.02, 5.92) * mm});
            skLineSegment(sketch, "E782", {"start": v(8.02, 5.92) * mm, "end": v(7.8, 5.9) * mm});
            skLineSegment(sketch, "E783", {"start": v(7.8, 5.9) * mm, "end": v(7.58, 5.83) * mm});
            skLineSegment(sketch, "E784", {"start": v(7.58, 5.83) * mm, "end": v(7.39, 5.72) * mm});
            skLineSegment(sketch, "E785", {"start": v(7.39, 5.72) * mm, "end": v(7.21, 5.58) * mm});
            skLineSegment(sketch, "E786", {"start": v(7.21, 5.58) * mm, "end": v(7.07, 5.4) * mm});
            skLineSegment(sketch, "E787", {"start": v(7.07, 5.4) * mm, "end": v(6.96, 5.21) * mm});
            skLineSegment(sketch, "E788", {"start": v(6.96, 5.21) * mm, "end": v(6.9, 5) * mm});
            skLineSegment(sketch, "E789", {"start": v(6.9, 5) * mm, "end": v(6.88, 4.77) * mm});
            skLineSegment(sketch, "E790", {"start": v(6.88, 4.77) * mm, "end": v(6.9, 4.55) * mm});
            skLineSegment(sketch, "E791", {"start": v(6.9, 4.55) * mm, "end": v(6.96, 4.33) * mm});
            skLineSegment(sketch, "E792", {"start": v(6.96, 4.33) * mm, "end": v(7.07, 4.14) * mm});
            skLineSegment(sketch, "E793", {"start": v(7.07, 4.14) * mm, "end": v(7.21, 3.96) * mm});
            skLineSegment(sketch, "E794", {"start": v(7.21, 3.96) * mm, "end": v(7.39, 3.82) * mm});
            skLineSegment(sketch, "E795", {"start": v(7.39, 3.82) * mm, "end": v(7.58, 3.71) * mm});
            skLineSegment(sketch, "E796", {"start": v(7.58, 3.71) * mm, "end": v(7.8, 3.65) * mm});
            skLineSegment(sketch, "E797", {"start": v(7.8, 3.65) * mm, "end": v(8.02, 3.63) * mm});
            skLineSegment(sketch, "E798", {"start": v(8.02, 3.63) * mm, "end": v(8.25, 3.65) * mm});
            skLineSegment(sketch, "E799", {"start": v(8.25, 3.65) * mm, "end": v(8.46, 3.71) * mm});
            skLineSegment(sketch, "E800", {"start": v(8.46, 3.71) * mm, "end": v(8.66, 3.82) * mm});
            skLineSegment(sketch, "E801", {"start": v(8.66, 3.82) * mm, "end": v(8.83, 3.96) * mm});
            skLineSegment(sketch, "E802", {"start": v(8.83, 3.96) * mm, "end": v(8.98, 4.14) * mm});
            skLineSegment(sketch, "E803", {"start": v(8.98, 4.14) * mm, "end": v(9.08, 4.33) * mm});
            skLineSegment(sketch, "E804", {"start": v(9.08, 4.33) * mm, "end": v(9.13, 4.5) * mm});
            skLineSegment(sketch, "E805", {"start": v(2.6, 0.54) * mm, "end": v(2.06, 0.54) * mm});
            skLineSegment(sketch, "E806", {"start": v(2.06, 0.54) * mm, "end": v(2.06, -1.01) * mm});
            skLineSegment(sketch, "E807", {"start": v(2.06, -1.01) * mm, "end": v(3.6, -1.01) * mm});
            skLineSegment(sketch, "E808", {"start": v(3.6, -1.01) * mm, "end": v(3.6, 0.54) * mm});
            skLineSegment(sketch, "E809", {"start": v(3.6, 0.54) * mm, "end": v(3.06, 0.54) * mm});
            skLineSegment(sketch, "E810", {"start": v(3.58, -0.98) * mm, "end": v(3.58, 0.5) * mm});
            skLineSegment(sketch, "E811", {"start": v(3.58, 0.5) * mm, "end": v(3.06, 0.5) * mm});
            skLineSegment(sketch, "E812", {"start": v(3.06, 0.5) * mm, "end": v(3.06, 2.36) * mm});
            skLineSegment(sketch, "E813", {"start": v(3.06, 2.36) * mm, "end": v(3.12, 2.38) * mm});
            skLineSegment(sketch, "E814", {"start": v(3.12, 2.38) * mm, "end": v(3.24, 2.45) * mm});
            skLineSegment(sketch, "E815", {"start": v(3.24, 2.45) * mm, "end": v(3.36, 2.54) * mm});
            skLineSegment(sketch, "E816", {"start": v(3.36, 2.54) * mm, "end": v(3.45, 2.66) * mm});
            skLineSegment(sketch, "E817", {"start": v(3.45, 2.66) * mm, "end": v(3.52, 2.78) * mm});
            skLineSegment(sketch, "E818", {"start": v(3.52, 2.78) * mm, "end": v(3.56, 2.92) * mm});
            skLineSegment(sketch, "E819", {"start": v(3.56, 2.92) * mm, "end": v(3.58, 3.07) * mm});
            skLineSegment(sketch, "E820", {"start": v(3.58, 3.07) * mm, "end": v(3.56, 3.21) * mm});
            skLineSegment(sketch, "E821", {"start": v(3.56, 3.21) * mm, "end": v(3.52, 3.35) * mm});
            skLineSegment(sketch, "E822", {"start": v(3.52, 3.35) * mm, "end": v(3.45, 3.48) * mm});
            skLineSegment(sketch, "E823", {"start": v(3.45, 3.48) * mm, "end": v(3.36, 3.6) * mm});
            skLineSegment(sketch, "E824", {"start": v(3.36, 3.6) * mm, "end": v(3.24, 3.69) * mm});
            skLineSegment(sketch, "E825", {"start": v(3.24, 3.69) * mm, "end": v(3.12, 3.75) * mm});
            skLineSegment(sketch, "E826", {"start": v(3.12, 3.75) * mm, "end": v(2.98, 3.8) * mm});
            skLineSegment(sketch, "E827", {"start": v(2.98, 3.8) * mm, "end": v(2.83, 3.81) * mm});
            skLineSegment(sketch, "E828", {"start": v(2.83, 3.81) * mm, "end": v(2.69, 3.8) * mm});
            skLineSegment(sketch, "E829", {"start": v(2.69, 3.8) * mm, "end": v(2.55, 3.75) * mm});
            skLineSegment(sketch, "E830", {"start": v(2.55, 3.75) * mm, "end": v(2.42, 3.69) * mm});
            skLineSegment(sketch, "E831", {"start": v(2.42, 3.69) * mm, "end": v(2.3, 3.6) * mm});
            skLineSegment(sketch, "E832", {"start": v(2.3, 3.6) * mm, "end": v(2.21, 3.48) * mm});
            skLineSegment(sketch, "E833", {"start": v(2.21, 3.48) * mm, "end": v(2.15, 3.35) * mm});
            skLineSegment(sketch, "E834", {"start": v(2.15, 3.35) * mm, "end": v(2.1, 3.21) * mm});
            skLineSegment(sketch, "E835", {"start": v(2.1, 3.21) * mm, "end": v(2.09, 3.07) * mm});
            skLineSegment(sketch, "E836", {"start": v(2.09, 3.07) * mm, "end": v(2.1, 2.92) * mm});
            skLineSegment(sketch, "E837", {"start": v(2.1, 2.92) * mm, "end": v(2.15, 2.78) * mm});
            skLineSegment(sketch, "E838", {"start": v(2.15, 2.78) * mm, "end": v(2.21, 2.66) * mm});
            skLineSegment(sketch, "E839", {"start": v(2.21, 2.66) * mm, "end": v(2.3, 2.54) * mm});
            skLineSegment(sketch, "E840", {"start": v(2.3, 2.54) * mm, "end": v(2.42, 2.45) * mm});
            skLineSegment(sketch, "E841", {"start": v(2.42, 2.45) * mm, "end": v(2.55, 2.38) * mm});
            skLineSegment(sketch, "E842", {"start": v(2.55, 2.38) * mm, "end": v(2.6, 2.36) * mm});
            skLineSegment(sketch, "E843", {"start": v(2.6, 2.36) * mm, "end": v(2.6, 0.5) * mm});
            skLineSegment(sketch, "E844", {"start": v(2.6, 0.5) * mm, "end": v(2.09, 0.5) * mm});
            skLineSegment(sketch, "E845", {"start": v(2.09, 0.5) * mm, "end": v(2.09, -0.98) * mm});
            skLineSegment(sketch, "E846", {"start": v(2.09, -0.98) * mm, "end": v(3.58, -0.98) * mm});
            skLineSegment(sketch, "E847", {"start": v(3.06, 2.33) * mm, "end": v(3.13, 2.35) * mm});
            skLineSegment(sketch, "E848", {"start": v(3.13, 2.35) * mm, "end": v(3.26, 2.42) * mm});
            skLineSegment(sketch, "E849", {"start": v(3.26, 2.42) * mm, "end": v(3.38, 2.52) * mm});
            skLineSegment(sketch, "E850", {"start": v(3.38, 2.52) * mm, "end": v(3.48, 2.64) * mm});
            skLineSegment(sketch, "E851", {"start": v(3.48, 2.64) * mm, "end": v(3.55, 2.77) * mm});
            skLineSegment(sketch, "E852", {"start": v(3.55, 2.77) * mm, "end": v(3.6, 2.92) * mm});
            skLineSegment(sketch, "E853", {"start": v(3.6, 2.92) * mm, "end": v(3.6, 3.07) * mm});
            skLineSegment(sketch, "E854", {"start": v(3.6, 3.07) * mm, "end": v(3.6, 3.22) * mm});
            skLineSegment(sketch, "E855", {"start": v(3.6, 3.22) * mm, "end": v(3.55, 3.36) * mm});
            skLineSegment(sketch, "E856", {"start": v(3.55, 3.36) * mm, "end": v(3.48, 3.5) * mm});
            skLineSegment(sketch, "E857", {"start": v(3.48, 3.5) * mm, "end": v(3.38, 3.62) * mm});
            skLineSegment(sketch, "E858", {"start": v(3.38, 3.62) * mm, "end": v(3.26, 3.71) * mm});
            skLineSegment(sketch, "E859", {"start": v(3.26, 3.71) * mm, "end": v(3.13, 3.78) * mm});
            skLineSegment(sketch, "E860", {"start": v(3.13, 3.78) * mm, "end": v(2.98, 3.83) * mm});
            skLineSegment(sketch, "E861", {"start": v(2.98, 3.83) * mm, "end": v(2.83, 3.84) * mm});
            skLineSegment(sketch, "E862", {"start": v(2.83, 3.84) * mm, "end": v(2.68, 3.83) * mm});
            skLineSegment(sketch, "E863", {"start": v(2.68, 3.83) * mm, "end": v(2.54, 3.78) * mm});
            skLineSegment(sketch, "E864", {"start": v(2.54, 3.78) * mm, "end": v(2.4, 3.71) * mm});
            skLineSegment(sketch, "E865", {"start": v(2.4, 3.71) * mm, "end": v(2.28, 3.62) * mm});
            skLineSegment(sketch, "E866", {"start": v(2.28, 3.62) * mm, "end": v(2.19, 3.5) * mm});
            skLineSegment(sketch, "E867", {"start": v(2.19, 3.5) * mm, "end": v(2.12, 3.36) * mm});
            skLineSegment(sketch, "E868", {"start": v(2.12, 3.36) * mm, "end": v(2.07, 3.22) * mm});
            skLineSegment(sketch, "E869", {"start": v(2.07, 3.22) * mm, "end": v(2.06, 3.07) * mm});
            skLineSegment(sketch, "E870", {"start": v(2.06, 3.07) * mm, "end": v(2.07, 2.92) * mm});
            skLineSegment(sketch, "E871", {"start": v(2.07, 2.92) * mm, "end": v(2.12, 2.77) * mm});
            skLineSegment(sketch, "E872", {"start": v(2.12, 2.77) * mm, "end": v(2.19, 2.64) * mm});
            skLineSegment(sketch, "E873", {"start": v(2.19, 2.64) * mm, "end": v(2.28, 2.52) * mm});
            skLineSegment(sketch, "E874", {"start": v(2.28, 2.52) * mm, "end": v(2.4, 2.42) * mm});
            skLineSegment(sketch, "E875", {"start": v(2.4, 2.42) * mm, "end": v(2.54, 2.35) * mm});
            skLineSegment(sketch, "E876", {"start": v(2.54, 2.35) * mm, "end": v(2.6, 2.33) * mm});
            skLineSegment(sketch, "E877", {"start": v(8.88, 7) * mm, "end": v(8.97, 7.08) * mm});
            skLineSegment(sketch, "E878", {"start": v(8.97, 7.08) * mm, "end": v(9.04, 7.17) * mm});
            skLineSegment(sketch, "E879", {"start": v(9.04, 7.17) * mm, "end": v(9.1, 7.27) * mm});
            skLineSegment(sketch, "E880", {"start": v(9.1, 7.27) * mm, "end": v(9.13, 7.38) * mm});
            skLineSegment(sketch, "E881", {"start": v(9.13, 7.38) * mm, "end": v(9.13, 7.44) * mm});
            skLineSegment(sketch, "E882", {"start": v(9.13, 7.44) * mm, "end": v(9.14, 7.44) * mm});
            skLineSegment(sketch, "E883", {"start": v(9.14, 7.44) * mm, "end": v(9.14, 7.5) * mm});
            skLineSegment(sketch, "E884", {"start": v(9.14, 7.5) * mm, "end": v(9.14, 8.56) * mm});
            skLineSegment(sketch, "E885", {"start": v(9.14, 8.56) * mm, "end": v(9.14, 8.6) * mm});
            skLineSegment(sketch, "E886", {"start": v(9.14, 8.6) * mm, "end": v(9.13, 8.6) * mm});
            skLineSegment(sketch, "E887", {"start": v(9.13, 8.6) * mm, "end": v(9.13, 8.67) * mm});
            skLineSegment(sketch, "E888", {"start": v(9.13, 8.67) * mm, "end": v(9.1, 8.78) * mm});
            skLineSegment(sketch, "E889", {"start": v(9.1, 8.78) * mm, "end": v(9.04, 8.88) * mm});
            skLineSegment(sketch, "E890", {"start": v(9.04, 8.88) * mm, "end": v(8.97, 8.97) * mm});
            skLineSegment(sketch, "E891", {"start": v(8.97, 8.97) * mm, "end": v(8.88, 9.04) * mm});
            skLineSegment(sketch, "E892", {"start": v(8.88, 9.04) * mm, "end": v(8.78, 9.1) * mm});
            skLineSegment(sketch, "E893", {"start": v(8.78, 9.1) * mm, "end": v(8.67, 9.13) * mm});
            skLineSegment(sketch, "E894", {"start": v(8.67, 9.13) * mm, "end": v(8.6, 9.13) * mm});
            skLineSegment(sketch, "E895", {"start": v(8.6, 9.13) * mm, "end": v(8.6, 9.14) * mm});
            skLineSegment(sketch, "E896", {"start": v(8.6, 9.14) * mm, "end": v(8.55, 9.14) * mm});
            skLineSegment(sketch, "E897", {"start": v(8.55, 9.14) * mm, "end": v(7.5, 9.14) * mm});
            skLineSegment(sketch, "E898", {"start": v(7.5, 9.14) * mm, "end": v(7.44, 9.14) * mm});
            skLineSegment(sketch, "E899", {"start": v(7.44, 9.14) * mm, "end": v(7.44, 9.13) * mm});
            skLineSegment(sketch, "E900", {"start": v(7.44, 9.13) * mm, "end": v(7.38, 9.13) * mm});
            skLineSegment(sketch, "E901", {"start": v(7.38, 9.13) * mm, "end": v(7.27, 9.1) * mm});
            skLineSegment(sketch, "E902", {"start": v(7.27, 9.1) * mm, "end": v(7.17, 9.04) * mm});
            skLineSegment(sketch, "E903", {"start": v(7.17, 9.04) * mm, "end": v(7.08, 8.97) * mm});
            skLineSegment(sketch, "E904", {"start": v(7.08, 8.97) * mm, "end": v(7, 8.88) * mm});
            skLineSegment(sketch, "E905", {"start": v(7, 8.88) * mm, "end": v(6.95, 8.78) * mm});
            skLineSegment(sketch, "E906", {"start": v(6.95, 8.78) * mm, "end": v(6.92, 8.67) * mm});
            skLineSegment(sketch, "E907", {"start": v(6.92, 8.67) * mm, "end": v(6.91, 8.6) * mm});
            skLineSegment(sketch, "E908", {"start": v(6.91, 8.6) * mm, "end": v(6.9, 8.6) * mm});
            skLineSegment(sketch, "E909", {"start": v(6.9, 8.6) * mm, "end": v(6.9, 8.56) * mm});
            skLineSegment(sketch, "E910", {"start": v(6.9, 8.56) * mm, "end": v(6.9, 8.25) * mm});
            skLineSegment(sketch, "E911", {"start": v(6.9, 8.25) * mm, "end": v(6.6, 8.25) * mm});
            skLineSegment(sketch, "E912", {"start": v(6.6, 8.25) * mm, "end": v(6.56, 8.24) * mm});
            skLineSegment(sketch, "E913", {"start": v(6.56, 8.24) * mm, "end": v(6.52, 8.23) * mm});
            skLineSegment(sketch, "E914", {"start": v(6.52, 8.23) * mm, "end": v(6.48, 8.2) * mm});
            skLineSegment(sketch, "E915", {"start": v(6.48, 8.2) * mm, "end": v(6.45, 8.18) * mm});
            skLineSegment(sketch, "E916", {"start": v(6.45, 8.18) * mm, "end": v(4.4, 6.12) * mm});
            skLineSegment(sketch, "E917", {"start": v(4.4, 6.12) * mm, "end": v(3.54, 6.12) * mm});
            skLineSegment(sketch, "E918", {"start": v(3.54, 6.12) * mm, "end": v(3.52, 6.18) * mm});
            skLineSegment(sketch, "E919", {"start": v(3.52, 6.18) * mm, "end": v(3.45, 6.31) * mm});
            skLineSegment(sketch, "E920", {"start": v(3.45, 6.31) * mm, "end": v(3.36, 6.43) * mm});
            skLineSegment(sketch, "E921", {"start": v(3.36, 6.43) * mm, "end": v(3.24, 6.52) * mm});
            skLineSegment(sketch, "E922", {"start": v(3.24, 6.52) * mm, "end": v(3.12, 6.59) * mm});
            skLineSegment(sketch, "E923", {"start": v(3.12, 6.59) * mm, "end": v(2.98, 6.63) * mm});
            skLineSegment(sketch, "E924", {"start": v(2.98, 6.63) * mm, "end": v(2.83, 6.64) * mm});
            skLineSegment(sketch, "E925", {"start": v(2.83, 6.64) * mm, "end": v(2.69, 6.63) * mm});
            skLineSegment(sketch, "E926", {"start": v(2.69, 6.63) * mm, "end": v(2.55, 6.59) * mm});
            skLineSegment(sketch, "E927", {"start": v(2.55, 6.59) * mm, "end": v(2.42, 6.52) * mm});
            skLineSegment(sketch, "E928", {"start": v(2.42, 6.52) * mm, "end": v(2.3, 6.43) * mm});
            skLineSegment(sketch, "E929", {"start": v(2.3, 6.43) * mm, "end": v(2.21, 6.31) * mm});
            skLineSegment(sketch, "E930", {"start": v(2.21, 6.31) * mm, "end": v(2.15, 6.18) * mm});
            skLineSegment(sketch, "E931", {"start": v(2.15, 6.18) * mm, "end": v(2.1, 6.04) * mm});
            skLineSegment(sketch, "E932", {"start": v(2.1, 6.04) * mm, "end": v(2.09, 5.9) * mm});
            skLineSegment(sketch, "E933", {"start": v(2.09, 5.9) * mm, "end": v(2.1, 5.75) * mm});
            skLineSegment(sketch, "E934", {"start": v(2.1, 5.75) * mm, "end": v(2.15, 5.62) * mm});
            skLineSegment(sketch, "E935", {"start": v(2.15, 5.62) * mm, "end": v(2.21, 5.49) * mm});
            skLineSegment(sketch, "E936", {"start": v(2.21, 5.49) * mm, "end": v(2.3, 5.37) * mm});
            skLineSegment(sketch, "E937", {"start": v(2.3, 5.37) * mm, "end": v(2.42, 5.28) * mm});
            skLineSegment(sketch, "E938", {"start": v(2.42, 5.28) * mm, "end": v(2.55, 5.21) * mm});
            skLineSegment(sketch, "E939", {"start": v(2.55, 5.21) * mm, "end": v(2.69, 5.17) * mm});
            skLineSegment(sketch, "E940", {"start": v(2.69, 5.17) * mm, "end": v(2.83, 5.16) * mm});
            skLineSegment(sketch, "E941", {"start": v(2.83, 5.16) * mm, "end": v(2.98, 5.17) * mm});
            skLineSegment(sketch, "E942", {"start": v(2.98, 5.17) * mm, "end": v(3.12, 5.21) * mm});
            skLineSegment(sketch, "E943", {"start": v(3.12, 5.21) * mm, "end": v(3.24, 5.28) * mm});
            skLineSegment(sketch, "E944", {"start": v(3.24, 5.28) * mm, "end": v(3.36, 5.37) * mm});
            skLineSegment(sketch, "E945", {"start": v(3.36, 5.37) * mm, "end": v(3.45, 5.49) * mm});
            skLineSegment(sketch, "E946", {"start": v(3.45, 5.49) * mm, "end": v(3.52, 5.62) * mm});
            skLineSegment(sketch, "E947", {"start": v(3.52, 5.62) * mm, "end": v(3.54, 5.68) * mm});
            skLineSegment(sketch, "E948", {"start": v(3.54, 5.68) * mm, "end": v(4.48, 5.68) * mm});
            skLineSegment(sketch, "E949", {"start": v(4.48, 5.68) * mm, "end": v(4.53, 5.68) * mm});
            skLineSegment(sketch, "E950", {"start": v(4.53, 5.68) * mm, "end": v(4.57, 5.7) * mm});
            skLineSegment(sketch, "E951", {"start": v(4.57, 5.7) * mm, "end": v(4.6, 5.71) * mm});
            skLineSegment(sketch, "E952", {"start": v(4.6, 5.71) * mm, "end": v(4.64, 5.74) * mm});
            skLineSegment(sketch, "E953", {"start": v(4.64, 5.74) * mm, "end": v(6.7, 7.8) * mm});
            skLineSegment(sketch, "E954", {"start": v(6.7, 7.8) * mm, "end": v(6.9, 7.8) * mm});
            skLineSegment(sketch, "E955", {"start": v(6.9, 7.8) * mm, "end": v(6.9, 7.5) * mm});
            skLineSegment(sketch, "E956", {"start": v(6.9, 7.5) * mm, "end": v(6.9, 7.44) * mm});
            skLineSegment(sketch, "E957", {"start": v(6.9, 7.44) * mm, "end": v(6.91, 7.44) * mm});
            skLineSegment(sketch, "E958", {"start": v(6.91, 7.44) * mm, "end": v(6.92, 7.38) * mm});
            skLineSegment(sketch, "E959", {"start": v(6.92, 7.38) * mm, "end": v(6.95, 7.27) * mm});
            skLineSegment(sketch, "E960", {"start": v(6.95, 7.27) * mm, "end": v(7, 7.17) * mm});
            skLineSegment(sketch, "E961", {"start": v(7, 7.17) * mm, "end": v(7.08, 7.08) * mm});
            skLineSegment(sketch, "E962", {"start": v(7.08, 7.08) * mm, "end": v(7.17, 7) * mm});
            skLineSegment(sketch, "E963", {"start": v(7.17, 7) * mm, "end": v(7.27, 6.95) * mm});
            skLineSegment(sketch, "E964", {"start": v(7.27, 6.95) * mm, "end": v(7.38, 6.92) * mm});
            skLineSegment(sketch, "E965", {"start": v(7.38, 6.92) * mm, "end": v(7.44, 6.91) * mm});
            skLineSegment(sketch, "E966", {"start": v(7.44, 6.91) * mm, "end": v(7.44, 6.9) * mm});
            skLineSegment(sketch, "E967", {"start": v(7.44, 6.9) * mm, "end": v(7.5, 6.9) * mm});
            skLineSegment(sketch, "E968", {"start": v(7.5, 6.9) * mm, "end": v(8.55, 6.9) * mm});
            skLineSegment(sketch, "E969", {"start": v(8.55, 6.9) * mm, "end": v(8.6, 6.9) * mm});
            skLineSegment(sketch, "E970", {"start": v(8.6, 6.9) * mm, "end": v(8.6, 6.91) * mm});
            skLineSegment(sketch, "E971", {"start": v(8.6, 6.91) * mm, "end": v(8.67, 6.92) * mm});
            skLineSegment(sketch, "E972", {"start": v(8.67, 6.92) * mm, "end": v(8.78, 6.95) * mm});
            skLineSegment(sketch, "E973", {"start": v(8.78, 6.95) * mm, "end": v(8.88, 7) * mm});
            skLineSegment(sketch, "E974", {"start": v(8.64, 6.88) * mm, "end": v(8.64, 6.88) * mm});
            skLineSegment(sketch, "E975", {"start": v(8.64, 6.88) * mm, "end": v(8.56, 6.88) * mm});
            skLineSegment(sketch, "E976", {"start": v(8.56, 6.88) * mm, "end": v(8.64, 6.88) * mm});
            skLineSegment(sketch, "E977", {"start": v(-3.51, -10.87) * mm, "end": v(-3.53, -10.8) * mm});
            skLineSegment(sketch, "E978", {"start": v(-3.53, -10.8) * mm, "end": v(-3.6, -10.66) * mm});
            skLineSegment(sketch, "E979", {"start": v(-3.6, -10.66) * mm, "end": v(-3.7, -10.54) * mm});
            skLineSegment(sketch, "E980", {"start": v(-3.7, -10.54) * mm, "end": v(-3.82, -10.45) * mm});
            skLineSegment(sketch, "E981", {"start": v(-3.82, -10.45) * mm, "end": v(-3.95, -10.38) * mm});
            skLineSegment(sketch, "E982", {"start": v(-3.95, -10.38) * mm, "end": v(-4.1, -10.33) * mm});
            skLineSegment(sketch, "E983", {"start": v(-4.1, -10.33) * mm, "end": v(-4.25, -10.32) * mm});
            skLineSegment(sketch, "E984", {"start": v(-4.25, -10.32) * mm, "end": v(-4.4, -10.33) * mm});
            skLineSegment(sketch, "E985", {"start": v(-4.4, -10.33) * mm, "end": v(-4.54, -10.38) * mm});
            skLineSegment(sketch, "E986", {"start": v(-4.54, -10.38) * mm, "end": v(-4.68, -10.45) * mm});
            skLineSegment(sketch, "E987", {"start": v(-4.68, -10.45) * mm, "end": v(-4.8, -10.54) * mm});
            skLineSegment(sketch, "E988", {"start": v(-4.8, -10.54) * mm, "end": v(-4.9, -10.66) * mm});
            skLineSegment(sketch, "E989", {"start": v(-4.9, -10.66) * mm, "end": v(-4.96, -10.8) * mm});
            skLineSegment(sketch, "E990", {"start": v(-4.96, -10.8) * mm, "end": v(-5, -10.94) * mm});
            skLineSegment(sketch, "E991", {"start": v(-5, -10.94) * mm, "end": v(-5.02, -11.1) * mm});
            skLineSegment(sketch, "E992", {"start": v(-5.02, -11.1) * mm, "end": v(-5, -11.24) * mm});
            skLineSegment(sketch, "E993", {"start": v(-5, -11.24) * mm, "end": v(-4.96, -11.39) * mm});
            skLineSegment(sketch, "E994", {"start": v(-4.96, -11.39) * mm, "end": v(-4.9, -11.52) * mm});
            skLineSegment(sketch, "E995", {"start": v(-4.9, -11.52) * mm, "end": v(-4.8, -11.64) * mm});
            skLineSegment(sketch, "E996", {"start": v(-4.8, -11.64) * mm, "end": v(-4.68, -11.73) * mm});
            skLineSegment(sketch, "E997", {"start": v(-4.68, -11.73) * mm, "end": v(-4.54, -11.8) * mm});
            skLineSegment(sketch, "E998", {"start": v(-4.54, -11.8) * mm, "end": v(-4.4, -11.85) * mm});
            skLineSegment(sketch, "E999", {"start": v(-4.4, -11.85) * mm, "end": v(-4.25, -11.87) * mm});
            skLineSegment(sketch, "E1000", {"start": v(-4.25, -11.87) * mm, "end": v(-4.1, -11.85) * mm});
            skLineSegment(sketch, "E1001", {"start": v(-4.1, -11.85) * mm, "end": v(-3.95, -11.8) * mm});
            skLineSegment(sketch, "E1002", {"start": v(-3.95, -11.8) * mm, "end": v(-3.82, -11.73) * mm});
            skLineSegment(sketch, "E1003", {"start": v(-3.82, -11.73) * mm, "end": v(-3.7, -11.64) * mm});
            skLineSegment(sketch, "E1004", {"start": v(-3.7, -11.64) * mm, "end": v(-3.6, -11.52) * mm});
            skLineSegment(sketch, "E1005", {"start": v(-3.6, -11.52) * mm, "end": v(-3.53, -11.39) * mm});
            skLineSegment(sketch, "E1006", {"start": v(-3.53, -11.39) * mm, "end": v(-3.51, -11.31) * mm});
            skLineSegment(sketch, "E1007", {"start": v(7.5, 6.88) * mm, "end": v(8.55, 6.88) * mm});
            skLineSegment(sketch, "E1008", {"start": v(7.48, 6.88) * mm, "end": v(7.41, 6.88) * mm});
            skLineSegment(sketch, "E1009", {"start": v(7.41, 6.88) * mm, "end": v(7.41, 6.88) * mm});
            skLineSegment(sketch, "E1010", {"start": v(7.41, 6.88) * mm, "end": v(7.48, 6.88) * mm});
            skLineSegment(sketch, "E1011", {"start": v(15.4, 10.31) * mm, "end": v(15.68, 10.4) * mm});
            skLineSegment(sketch, "E1012", {"start": v(15.68, 10.4) * mm, "end": v(15.95, 10.54) * mm});
            skLineSegment(sketch, "E1013", {"start": v(15.95, 10.54) * mm, "end": v(16.18, 10.73) * mm});
            skLineSegment(sketch, "E1014", {"start": v(16.18, 10.73) * mm, "end": v(16.36, 10.96) * mm});
            skLineSegment(sketch, "E1015", {"start": v(16.36, 10.96) * mm, "end": v(16.5, 11.22) * mm});
            skLineSegment(sketch, "E1016", {"start": v(16.5, 11.22) * mm, "end": v(16.6, 11.5) * mm});
            skLineSegment(sketch, "E1017", {"start": v(16.6, 11.5) * mm, "end": v(16.62, 11.8) * mm});
            skLineSegment(sketch, "E1018", {"start": v(16.62, 11.8) * mm, "end": v(16.6, 12.1) * mm});
            skLineSegment(sketch, "E1019", {"start": v(16.6, 12.1) * mm, "end": v(16.5, 12.38) * mm});
            skLineSegment(sketch, "E1020", {"start": v(16.5, 12.38) * mm, "end": v(16.36, 12.64) * mm});
            skLineSegment(sketch, "E1021", {"start": v(16.36, 12.64) * mm, "end": v(16.18, 12.87) * mm});
            skLineSegment(sketch, "E1022", {"start": v(16.18, 12.87) * mm, "end": v(15.95, 13.06) * mm});
            skLineSegment(sketch, "E1023", {"start": v(15.95, 13.06) * mm, "end": v(15.68, 13.2) * mm});
            skLineSegment(sketch, "E1024", {"start": v(15.68, 13.2) * mm, "end": v(15.4, 13.29) * mm});
            skLineSegment(sketch, "E1025", {"start": v(15.4, 13.29) * mm, "end": v(15.1, 13.32) * mm});
            skLineSegment(sketch, "E1026", {"start": v(15.1, 13.32) * mm, "end": v(14.8, 13.29) * mm});
            skLineSegment(sketch, "E1027", {"start": v(14.8, 13.29) * mm, "end": v(14.52, 13.2) * mm});
            skLineSegment(sketch, "E1028", {"start": v(14.52, 13.2) * mm, "end": v(14.26, 13.06) * mm});
            skLineSegment(sketch, "E1029", {"start": v(14.26, 13.06) * mm, "end": v(14.03, 12.87) * mm});
            skLineSegment(sketch, "E1030", {"start": v(14.03, 12.87) * mm, "end": v(13.84, 12.64) * mm});
            skLineSegment(sketch, "E1031", {"start": v(13.84, 12.64) * mm, "end": v(13.7, 12.38) * mm});
            skLineSegment(sketch, "E1032", {"start": v(13.7, 12.38) * mm, "end": v(13.61, 12.1) * mm});
            skLineSegment(sketch, "E1033", {"start": v(13.61, 12.1) * mm, "end": v(13.59, 11.8) * mm});
            skLineSegment(sketch, "E1034", {"start": v(13.59, 11.8) * mm, "end": v(13.61, 11.5) * mm});
            skLineSegment(sketch, "E1035", {"start": v(13.61, 11.5) * mm, "end": v(13.7, 11.22) * mm});
            skLineSegment(sketch, "E1036", {"start": v(13.7, 11.22) * mm, "end": v(13.84, 10.96) * mm});
            skLineSegment(sketch, "E1037", {"start": v(13.84, 10.96) * mm, "end": v(14.03, 10.73) * mm});
            skLineSegment(sketch, "E1038", {"start": v(14.03, 10.73) * mm, "end": v(14.26, 10.54) * mm});
            skLineSegment(sketch, "E1039", {"start": v(14.26, 10.54) * mm, "end": v(14.52, 10.4) * mm});
            skLineSegment(sketch, "E1040", {"start": v(14.52, 10.4) * mm, "end": v(14.8, 10.31) * mm});
            skLineSegment(sketch, "E1041", {"start": v(14.8, 10.31) * mm, "end": v(15.1, 10.28) * mm});
            skLineSegment(sketch, "E1042", {"start": v(15.1, 10.28) * mm, "end": v(15.4, 10.31) * mm});
            skLineSegment(sketch, "E1043", {"start": v(15.4, 10.34) * mm, "end": v(15.67, 10.43) * mm});
            skLineSegment(sketch, "E1044", {"start": v(15.67, 10.43) * mm, "end": v(15.93, 10.56) * mm});
            skLineSegment(sketch, "E1045", {"start": v(15.93, 10.56) * mm, "end": v(16.15, 10.75) * mm});
            skLineSegment(sketch, "E1046", {"start": v(16.15, 10.75) * mm, "end": v(16.34, 10.97) * mm});
            skLineSegment(sketch, "E1047", {"start": v(16.34, 10.97) * mm, "end": v(16.48, 11.23) * mm});
            skLineSegment(sketch, "E1048", {"start": v(16.48, 11.23) * mm, "end": v(16.56, 11.5) * mm});
            skLineSegment(sketch, "E1049", {"start": v(16.56, 11.5) * mm, "end": v(16.59, 11.8) * mm});
            skLineSegment(sketch, "E1050", {"start": v(16.59, 11.8) * mm, "end": v(16.56, 12.09) * mm});
            skLineSegment(sketch, "E1051", {"start": v(16.56, 12.09) * mm, "end": v(16.48, 12.37) * mm});
            skLineSegment(sketch, "E1052", {"start": v(16.48, 12.37) * mm, "end": v(16.34, 12.63) * mm});
            skLineSegment(sketch, "E1053", {"start": v(16.34, 12.63) * mm, "end": v(16.15, 12.85) * mm});
            skLineSegment(sketch, "E1054", {"start": v(16.15, 12.85) * mm, "end": v(15.93, 13.04) * mm});
            skLineSegment(sketch, "E1055", {"start": v(15.93, 13.04) * mm, "end": v(15.67, 13.17) * mm});
            skLineSegment(sketch, "E1056", {"start": v(15.67, 13.17) * mm, "end": v(15.4, 13.26) * mm});
            skLineSegment(sketch, "E1057", {"start": v(15.4, 13.26) * mm, "end": v(15.1, 13.29) * mm});
            skLineSegment(sketch, "E1058", {"start": v(15.1, 13.29) * mm, "end": v(14.81, 13.26) * mm});
            skLineSegment(sketch, "E1059", {"start": v(14.81, 13.26) * mm, "end": v(14.53, 13.17) * mm});
            skLineSegment(sketch, "E1060", {"start": v(14.53, 13.17) * mm, "end": v(14.28, 13.04) * mm});
            skLineSegment(sketch, "E1061", {"start": v(14.28, 13.04) * mm, "end": v(14.05, 12.85) * mm});
            skLineSegment(sketch, "E1062", {"start": v(14.05, 12.85) * mm, "end": v(13.87, 12.63) * mm});
            skLineSegment(sketch, "E1063", {"start": v(13.87, 12.63) * mm, "end": v(13.73, 12.37) * mm});
            skLineSegment(sketch, "E1064", {"start": v(13.73, 12.37) * mm, "end": v(13.64, 12.09) * mm});
            skLineSegment(sketch, "E1065", {"start": v(13.64, 12.09) * mm, "end": v(13.62, 11.8) * mm});
            skLineSegment(sketch, "E1066", {"start": v(13.62, 11.8) * mm, "end": v(13.64, 11.5) * mm});
            skLineSegment(sketch, "E1067", {"start": v(13.64, 11.5) * mm, "end": v(13.73, 11.23) * mm});
            skLineSegment(sketch, "E1068", {"start": v(13.73, 11.23) * mm, "end": v(13.87, 10.97) * mm});
            skLineSegment(sketch, "E1069", {"start": v(13.87, 10.97) * mm, "end": v(14.05, 10.75) * mm});
            skLineSegment(sketch, "E1070", {"start": v(14.05, 10.75) * mm, "end": v(14.28, 10.56) * mm});
            skLineSegment(sketch, "E1071", {"start": v(14.28, 10.56) * mm, "end": v(14.53, 10.43) * mm});
            skLineSegment(sketch, "E1072", {"start": v(14.53, 10.43) * mm, "end": v(14.81, 10.34) * mm});
            skLineSegment(sketch, "E1073", {"start": v(14.81, 10.34) * mm, "end": v(15.1, 10.31) * mm});
            skLineSegment(sketch, "E1074", {"start": v(15.1, 10.31) * mm, "end": v(15.4, 10.34) * mm});
            skLineSegment(sketch, "E1075", {"start": v(-4.99, -8.95) * mm, "end": v(-4.96, -9.03) * mm});
            skLineSegment(sketch, "E1076", {"start": v(-4.96, -9.03) * mm, "end": v(-4.9, -9.16) * mm});
            skLineSegment(sketch, "E1077", {"start": v(-4.9, -9.16) * mm, "end": v(-4.8, -9.28) * mm});
            skLineSegment(sketch, "E1078", {"start": v(-4.8, -9.28) * mm, "end": v(-4.68, -9.37) * mm});
            skLineSegment(sketch, "E1079", {"start": v(-4.68, -9.37) * mm, "end": v(-4.54, -9.45) * mm});
            skLineSegment(sketch, "E1080", {"start": v(-4.54, -9.45) * mm, "end": v(-4.4, -9.5) * mm});
            skLineSegment(sketch, "E1081", {"start": v(-4.4, -9.5) * mm, "end": v(-4.25, -9.5) * mm});
            skLineSegment(sketch, "E1082", {"start": v(-4.25, -9.5) * mm, "end": v(-4.1, -9.5) * mm});
            skLineSegment(sketch, "E1083", {"start": v(-4.1, -9.5) * mm, "end": v(-3.95, -9.45) * mm});
            skLineSegment(sketch, "E1084", {"start": v(-3.95, -9.45) * mm, "end": v(-3.82, -9.37) * mm});
            skLineSegment(sketch, "E1085", {"start": v(-3.82, -9.37) * mm, "end": v(-3.7, -9.28) * mm});
            skLineSegment(sketch, "E1086", {"start": v(-3.7, -9.28) * mm, "end": v(-3.6, -9.16) * mm});
            skLineSegment(sketch, "E1087", {"start": v(-3.6, -9.16) * mm, "end": v(-3.53, -9.03) * mm});
            skLineSegment(sketch, "E1088", {"start": v(-3.53, -9.03) * mm, "end": v(-3.49, -8.88) * mm});
            skLineSegment(sketch, "E1089", {"start": v(-3.49, -8.88) * mm, "end": v(-3.47, -8.73) * mm});
            skLineSegment(sketch, "E1090", {"start": v(-3.47, -8.73) * mm, "end": v(-3.49, -8.58) * mm});
            skLineSegment(sketch, "E1091", {"start": v(-3.49, -8.58) * mm, "end": v(-3.53, -8.43) * mm});
            skLineSegment(sketch, "E1092", {"start": v(-3.53, -8.43) * mm, "end": v(-3.6, -8.3) * mm});
            skLineSegment(sketch, "E1093", {"start": v(-3.6, -8.3) * mm, "end": v(-3.7, -8.18) * mm});
            skLineSegment(sketch, "E1094", {"start": v(-3.7, -8.18) * mm, "end": v(-3.82, -8.09) * mm});
            skLineSegment(sketch, "E1095", {"start": v(-3.82, -8.09) * mm, "end": v(-3.95, -8.02) * mm});
            skLineSegment(sketch, "E1096", {"start": v(-3.95, -8.02) * mm, "end": v(-4.1, -7.97) * mm});
            skLineSegment(sketch, "E1097", {"start": v(-4.1, -7.97) * mm, "end": v(-4.25, -7.96) * mm});
            skLineSegment(sketch, "E1098", {"start": v(-4.25, -7.96) * mm, "end": v(-4.4, -7.97) * mm});
            skLineSegment(sketch, "E1099", {"start": v(-4.4, -7.97) * mm, "end": v(-4.54, -8.02) * mm});
            skLineSegment(sketch, "E1100", {"start": v(-4.54, -8.02) * mm, "end": v(-4.68, -8.09) * mm});
            skLineSegment(sketch, "E1101", {"start": v(-4.68, -8.09) * mm, "end": v(-4.8, -8.18) * mm});
            skLineSegment(sketch, "E1102", {"start": v(-4.8, -8.18) * mm, "end": v(-4.9, -8.3) * mm});
            skLineSegment(sketch, "E1103", {"start": v(-4.9, -8.3) * mm, "end": v(-4.96, -8.43) * mm});
            skLineSegment(sketch, "E1104", {"start": v(-4.96, -8.43) * mm, "end": v(-4.99, -8.5) * mm});
            skLineSegment(sketch, "E1105", {"start": v(-3.52, -8.88) * mm, "end": v(-3.5, -8.73) * mm});
            skLineSegment(sketch, "E1106", {"start": v(-3.5, -8.73) * mm, "end": v(-3.52, -8.59) * mm});
            skLineSegment(sketch, "E1107", {"start": v(-3.52, -8.59) * mm, "end": v(-3.56, -8.45) * mm});
            skLineSegment(sketch, "E1108", {"start": v(-3.56, -8.45) * mm, "end": v(-3.63, -8.32) * mm});
            skLineSegment(sketch, "E1109", {"start": v(-3.63, -8.32) * mm, "end": v(-3.72, -8.2) * mm});
            skLineSegment(sketch, "E1110", {"start": v(-3.72, -8.2) * mm, "end": v(-3.83, -8.11) * mm});
            skLineSegment(sketch, "E1111", {"start": v(-3.83, -8.11) * mm, "end": v(-3.96, -8.04) * mm});
            skLineSegment(sketch, "E1112", {"start": v(-3.96, -8.04) * mm, "end": v(-4.1, -8) * mm});
            skLineSegment(sketch, "E1113", {"start": v(-4.1, -8) * mm, "end": v(-4.25, -7.99) * mm});
            skLineSegment(sketch, "E1114", {"start": v(-4.25, -7.99) * mm, "end": v(-4.4, -8) * mm});
            skLineSegment(sketch, "E1115", {"start": v(-4.4, -8) * mm, "end": v(-4.53, -8.04) * mm});
            skLineSegment(sketch, "E1116", {"start": v(-4.53, -8.04) * mm, "end": v(-4.66, -8.11) * mm});
            skLineSegment(sketch, "E1117", {"start": v(-4.66, -8.11) * mm, "end": v(-4.77, -8.2) * mm});
            skLineSegment(sketch, "E1118", {"start": v(-4.77, -8.2) * mm, "end": v(-4.87, -8.32) * mm});
            skLineSegment(sketch, "E1119", {"start": v(-4.87, -8.32) * mm, "end": v(-4.93, -8.45) * mm});
            skLineSegment(sketch, "E1120", {"start": v(-4.93, -8.45) * mm, "end": v(-4.95, -8.5) * mm});
            skLineSegment(sketch, "E1121", {"start": v(-4.95, -8.5) * mm, "end": v(-8.73, -8.5) * mm});
            skLineSegment(sketch, "E1122", {"start": v(-8.73, -8.5) * mm, "end": v(-8.77, -8.51) * mm});
            skLineSegment(sketch, "E1123", {"start": v(-8.77, -8.51) * mm, "end": v(-8.82, -8.52) * mm});
            skLineSegment(sketch, "E1124", {"start": v(-8.82, -8.52) * mm, "end": v(-8.86, -8.55) * mm});
            skLineSegment(sketch, "E1125", {"start": v(-8.86, -8.55) * mm, "end": v(-8.89, -8.57) * mm});
            skLineSegment(sketch, "E1126", {"start": v(-8.89, -8.57) * mm, "end": v(-9.33, -9.01) * mm});
            skLineSegment(sketch, "E1127", {"start": v(-9.33, -9.01) * mm, "end": v(-9.34, -9) * mm});
            skLineSegment(sketch, "E1128", {"start": v(-9.34, -9) * mm, "end": v(-9.41, -8.96) * mm});
            skLineSegment(sketch, "E1129", {"start": v(-9.41, -8.96) * mm, "end": v(-9.49, -8.94) * mm});
            skLineSegment(sketch, "E1130", {"start": v(-9.49, -8.94) * mm, "end": v(-9.52, -8.94) * mm});
            skLineSegment(sketch, "E1131", {"start": v(-9.52, -8.94) * mm, "end": v(-9.52, -8.93) * mm});
            skLineSegment(sketch, "E1132", {"start": v(-9.52, -8.93) * mm, "end": v(-9.56, -8.93) * mm});
            skLineSegment(sketch, "E1133", {"start": v(-9.56, -8.93) * mm, "end": v(-9.69, -8.93) * mm});
            skLineSegment(sketch, "E1134", {"start": v(-9.69, -8.93) * mm, "end": v(-9.69, -5.66) * mm});
            skLineSegment(sketch, "E1135", {"start": v(-9.69, -5.66) * mm, "end": v(-9.7, -5.62) * mm});
            skLineSegment(sketch, "E1136", {"start": v(-9.7, -5.62) * mm, "end": v(-9.7, -5.58) * mm});
            skLineSegment(sketch, "E1137", {"start": v(-9.7, -5.58) * mm, "end": v(-9.73, -5.54) * mm});
            skLineSegment(sketch, "E1138", {"start": v(-9.73, -5.54) * mm, "end": v(-9.75, -5.5) * mm});
            skLineSegment(sketch, "E1139", {"start": v(-9.75, -5.5) * mm, "end": v(-11.64, -3.62) * mm});
            skLineSegment(sketch, "E1140", {"start": v(-11.64, -3.62) * mm, "end": v(-11.67, -3.59) * mm});
            skLineSegment(sketch, "E1141", {"start": v(-11.67, -3.59) * mm, "end": v(-11.71, -3.57) * mm});
            skLineSegment(sketch, "E1142", {"start": v(-11.71, -3.57) * mm, "end": v(-11.76, -3.56) * mm});
            skLineSegment(sketch, "E1143", {"start": v(-11.76, -3.56) * mm, "end": v(-11.8, -3.55) * mm});
            skLineSegment(sketch, "E1144", {"start": v(-11.8, -3.55) * mm, "end": v(-12, -3.55) * mm});
            skLineSegment(sketch, "E1145", {"start": v(-12, -3.55) * mm, "end": v(-12, -3.43) * mm});
            skLineSegment(sketch, "E1146", {"start": v(-12, -3.43) * mm, "end": v(-12, -3.38) * mm});
            skLineSegment(sketch, "E1147", {"start": v(-12, -3.38) * mm, "end": v(-12, -3.38) * mm});
            skLineSegment(sketch, "E1148", {"start": v(-12, -3.38) * mm, "end": v(-12, -3.35) * mm});
            skLineSegment(sketch, "E1149", {"start": v(-12, -3.35) * mm, "end": v(-12.03, -3.28) * mm});
            skLineSegment(sketch, "E1150", {"start": v(-12.03, -3.28) * mm, "end": v(-12.07, -3.2) * mm});
            skLineSegment(sketch, "E1151", {"start": v(-12.07, -3.2) * mm, "end": v(-12.12, -3.15) * mm});
            skLineSegment(sketch, "E1152", {"start": v(-12.12, -3.15) * mm, "end": v(-12.18, -3.1) * mm});
            skLineSegment(sketch, "E1153", {"start": v(-12.18, -3.1) * mm, "end": v(-12.24, -3.06) * mm});
            skLineSegment(sketch, "E1154", {"start": v(-12.24, -3.06) * mm, "end": v(-12.32, -3.04) * mm});
            skLineSegment(sketch, "E1155", {"start": v(-12.32, -3.04) * mm, "end": v(-12.35, -3.04) * mm});
            skLineSegment(sketch, "E1156", {"start": v(-12.35, -3.04) * mm, "end": v(-12.35, -3.03) * mm});
            skLineSegment(sketch, "E1157", {"start": v(-12.35, -3.03) * mm, "end": v(-12.4, -3.03) * mm});
            skLineSegment(sketch, "E1158", {"start": v(-12.4, -3.03) * mm, "end": v(-13.1, -3.03) * mm});
            skLineSegment(sketch, "E1159", {"start": v(-13.1, -3.03) * mm, "end": v(-13.14, -3.03) * mm});
            skLineSegment(sketch, "E1160", {"start": v(-13.14, -3.03) * mm, "end": v(-13.14, -3.04) * mm});
            skLineSegment(sketch, "E1161", {"start": v(-13.14, -3.04) * mm, "end": v(-13.17, -3.04) * mm});
            skLineSegment(sketch, "E1162", {"start": v(-13.17, -3.04) * mm, "end": v(-13.24, -3.06) * mm});
            skLineSegment(sketch, "E1163", {"start": v(-13.24, -3.06) * mm, "end": v(-13.31, -3.1) * mm});
            skLineSegment(sketch, "E1164", {"start": v(-13.31, -3.1) * mm, "end": v(-13.37, -3.15) * mm});
            skLineSegment(sketch, "E1165", {"start": v(-13.37, -3.15) * mm, "end": v(-13.42, -3.2) * mm});
            skLineSegment(sketch, "E1166", {"start": v(-13.42, -3.2) * mm, "end": v(-13.46, -3.28) * mm});
            skLineSegment(sketch, "E1167", {"start": v(-13.46, -3.28) * mm, "end": v(-13.48, -3.35) * mm});
            skLineSegment(sketch, "E1168", {"start": v(-13.48, -3.35) * mm, "end": v(-13.48, -3.38) * mm});
            skLineSegment(sketch, "E1169", {"start": v(-13.48, -3.38) * mm, "end": v(-13.49, -3.38) * mm});
            skLineSegment(sketch, "E1170", {"start": v(-13.49, -3.38) * mm, "end": v(-13.49, -3.43) * mm});
            skLineSegment(sketch, "E1171", {"start": v(-13.49, -3.43) * mm, "end": v(-13.49, -4.12) * mm});
            skLineSegment(sketch, "E1172", {"start": v(-13.49, -4.12) * mm, "end": v(-13.49, -4.17) * mm});
            skLineSegment(sketch, "E1173", {"start": v(-13.49, -4.17) * mm, "end": v(-13.48, -4.17) * mm});
            skLineSegment(sketch, "E1174", {"start": v(-13.48, -4.17) * mm, "end": v(-13.48, -4.2) * mm});
            skLineSegment(sketch, "E1175", {"start": v(-13.48, -4.2) * mm, "end": v(-13.46, -4.28) * mm});
            skLineSegment(sketch, "E1176", {"start": v(-13.46, -4.28) * mm, "end": v(-13.42, -4.34) * mm});
            skLineSegment(sketch, "E1177", {"start": v(-13.42, -4.34) * mm, "end": v(-13.37, -4.4) * mm});
            skLineSegment(sketch, "E1178", {"start": v(-13.37, -4.4) * mm, "end": v(-13.31, -4.45) * mm});
            skLineSegment(sketch, "E1179", {"start": v(-13.31, -4.45) * mm, "end": v(-13.24, -4.49) * mm});
            skLineSegment(sketch, "E1180", {"start": v(-13.24, -4.49) * mm, "end": v(-13.17, -4.51) * mm});
            skLineSegment(sketch, "E1181", {"start": v(-13.17, -4.51) * mm, "end": v(-13.14, -4.51) * mm});
            skLineSegment(sketch, "E1182", {"start": v(-13.14, -4.51) * mm, "end": v(-13.14, -4.52) * mm});
            skLineSegment(sketch, "E1183", {"start": v(-13.14, -4.52) * mm, "end": v(-13.1, -4.52) * mm});
            skLineSegment(sketch, "E1184", {"start": v(-13.1, -4.52) * mm, "end": v(-12.4, -4.52) * mm});
            skLineSegment(sketch, "E1185", {"start": v(-12.4, -4.52) * mm, "end": v(-12.35, -4.52) * mm});
            skLineSegment(sketch, "E1186", {"start": v(-12.35, -4.52) * mm, "end": v(-12.35, -4.51) * mm});
            skLineSegment(sketch, "E1187", {"start": v(-12.35, -4.51) * mm, "end": v(-12.32, -4.51) * mm});
            skLineSegment(sketch, "E1188", {"start": v(-12.32, -4.51) * mm, "end": v(-12.24, -4.49) * mm});
            skLineSegment(sketch, "E1189", {"start": v(-12.24, -4.49) * mm, "end": v(-12.18, -4.45) * mm});
            skLineSegment(sketch, "E1190", {"start": v(-12.18, -4.45) * mm, "end": v(-12.12, -4.4) * mm});
            skLineSegment(sketch, "E1191", {"start": v(-12.12, -4.4) * mm, "end": v(-12.07, -4.34) * mm});
            skLineSegment(sketch, "E1192", {"start": v(-12.07, -4.34) * mm, "end": v(-12.03, -4.28) * mm});
            skLineSegment(sketch, "E1193", {"start": v(-12.03, -4.28) * mm, "end": v(-12, -4.2) * mm});
            skLineSegment(sketch, "E1194", {"start": v(-12, -4.2) * mm, "end": v(-12, -4.17) * mm});
            skLineSegment(sketch, "E1195", {"start": v(-12, -4.17) * mm, "end": v(-12, -4.17) * mm});
            skLineSegment(sketch, "E1196", {"start": v(-12, -4.17) * mm, "end": v(-12, -4.12) * mm});
            skLineSegment(sketch, "E1197", {"start": v(-12, -4.12) * mm, "end": v(-12, -4) * mm});
            skLineSegment(sketch, "E1198", {"start": v(-12, -4) * mm, "end": v(-11.9, -4) * mm});
            skLineSegment(sketch, "E1199", {"start": v(-11.9, -4) * mm, "end": v(-10.13, -5.76) * mm});
            skLineSegment(sketch, "E1200", {"start": v(-10.13, -5.76) * mm, "end": v(-10.13, -8.93) * mm});
            skLineSegment(sketch, "E1201", {"start": v(-10.13, -8.93) * mm, "end": v(-10.26, -8.93) * mm});
            skLineSegment(sketch, "E1202", {"start": v(-10.26, -8.93) * mm, "end": v(-10.3, -8.93) * mm});
            skLineSegment(sketch, "E1203", {"start": v(-10.3, -8.93) * mm, "end": v(-10.3, -8.94) * mm});
            skLineSegment(sketch, "E1204", {"start": v(-10.3, -8.94) * mm, "end": v(-10.34, -8.94) * mm});
            skLineSegment(sketch, "E1205", {"start": v(-10.34, -8.94) * mm, "end": v(-10.41, -8.96) * mm});
            skLineSegment(sketch, "E1206", {"start": v(-10.41, -8.96) * mm, "end": v(-10.48, -9) * mm});
            skLineSegment(sketch, "E1207", {"start": v(-10.48, -9) * mm, "end": v(-10.54, -9.05) * mm});
            skLineSegment(sketch, "E1208", {"start": v(-10.54, -9.05) * mm, "end": v(-10.59, -9.1) * mm});
            skLineSegment(sketch, "E1209", {"start": v(-10.59, -9.1) * mm, "end": v(-10.62, -9.18) * mm});
            skLineSegment(sketch, "E1210", {"start": v(-10.62, -9.18) * mm, "end": v(-10.65, -9.25) * mm});
            skLineSegment(sketch, "E1211", {"start": v(-10.65, -9.25) * mm, "end": v(-10.65, -9.28) * mm});
            skLineSegment(sketch, "E1212", {"start": v(-10.65, -9.28) * mm, "end": v(-10.65, -9.28) * mm});
            skLineSegment(sketch, "E1213", {"start": v(-10.65, -9.28) * mm, "end": v(-10.65, -9.33) * mm});
            skLineSegment(sketch, "E1214", {"start": v(-10.65, -9.33) * mm, "end": v(-10.65, -10.02) * mm});
            skLineSegment(sketch, "E1215", {"start": v(-10.65, -10.02) * mm, "end": v(-10.65, -10.07) * mm});
            skLineSegment(sketch, "E1216", {"start": v(-10.65, -10.07) * mm, "end": v(-10.65, -10.07) * mm});
            skLineSegment(sketch, "E1217", {"start": v(-10.65, -10.07) * mm, "end": v(-10.65, -10.1) * mm});
            skLineSegment(sketch, "E1218", {"start": v(-10.65, -10.1) * mm, "end": v(-10.62, -10.17) * mm});
            skLineSegment(sketch, "E1219", {"start": v(-10.62, -10.17) * mm, "end": v(-10.59, -10.24) * mm});
            skLineSegment(sketch, "E1220", {"start": v(-10.59, -10.24) * mm, "end": v(-10.54, -10.3) * mm});
            skLineSegment(sketch, "E1221", {"start": v(-10.54, -10.3) * mm, "end": v(-10.48, -10.35) * mm});
            skLineSegment(sketch, "E1222", {"start": v(-10.48, -10.35) * mm, "end": v(-10.41, -10.39) * mm});
            skLineSegment(sketch, "E1223", {"start": v(-10.41, -10.39) * mm, "end": v(-10.34, -10.41) * mm});
            skLineSegment(sketch, "E1224", {"start": v(-10.34, -10.41) * mm, "end": v(-10.3, -10.41) * mm});
            skLineSegment(sketch, "E1225", {"start": v(-10.3, -10.41) * mm, "end": v(-10.3, -10.42) * mm});
            skLineSegment(sketch, "E1226", {"start": v(-10.3, -10.42) * mm, "end": v(-10.26, -10.42) * mm});
            skLineSegment(sketch, "E1227", {"start": v(-10.26, -10.42) * mm, "end": v(-9.56, -10.42) * mm});
            skLineSegment(sketch, "E1228", {"start": v(-9.56, -10.42) * mm, "end": v(-9.52, -10.42) * mm});
            skLineSegment(sketch, "E1229", {"start": v(-9.52, -10.42) * mm, "end": v(-9.52, -10.41) * mm});
            skLineSegment(sketch, "E1230", {"start": v(-9.52, -10.41) * mm, "end": v(-9.49, -10.41) * mm});
            skLineSegment(sketch, "E1231", {"start": v(-9.49, -10.41) * mm, "end": v(-9.41, -10.39) * mm});
            skLineSegment(sketch, "E1232", {"start": v(-9.41, -10.39) * mm, "end": v(-9.34, -10.35) * mm});
            skLineSegment(sketch, "E1233", {"start": v(-9.34, -10.35) * mm, "end": v(-9.28, -10.3) * mm});
            skLineSegment(sketch, "E1234", {"start": v(-9.28, -10.3) * mm, "end": v(-9.23, -10.24) * mm});
            skLineSegment(sketch, "E1235", {"start": v(-9.23, -10.24) * mm, "end": v(-9.2, -10.17) * mm});
            skLineSegment(sketch, "E1236", {"start": v(-9.2, -10.17) * mm, "end": v(-9.18, -10.1) * mm});
            skLineSegment(sketch, "E1237", {"start": v(-9.18, -10.1) * mm, "end": v(-9.17, -10.07) * mm});
            skLineSegment(sketch, "E1238", {"start": v(-9.17, -10.07) * mm, "end": v(-9.17, -10.07) * mm});
            skLineSegment(sketch, "E1239", {"start": v(-9.17, -10.07) * mm, "end": v(-9.17, -10.02) * mm});
            skLineSegment(sketch, "E1240", {"start": v(-9.17, -10.02) * mm, "end": v(-9.17, -9.48) * mm});
            skLineSegment(sketch, "E1241", {"start": v(-9.17, -9.48) * mm, "end": v(-8.64, -8.95) * mm});
            skLineSegment(sketch, "E1242", {"start": v(-8.64, -8.95) * mm, "end": v(-4.95, -8.95) * mm});
            skLineSegment(sketch, "E1243", {"start": v(-4.95, -8.95) * mm, "end": v(-4.93, -9.02) * mm});
            skLineSegment(sketch, "E1244", {"start": v(-4.93, -9.02) * mm, "end": v(-4.87, -9.14) * mm});
            skLineSegment(sketch, "E1245", {"start": v(-4.87, -9.14) * mm, "end": v(-4.77, -9.26) * mm});
            skLineSegment(sketch, "E1246", {"start": v(-4.77, -9.26) * mm, "end": v(-4.66, -9.35) * mm});
            skLineSegment(sketch, "E1247", {"start": v(-4.66, -9.35) * mm, "end": v(-4.53, -9.42) * mm});
            skLineSegment(sketch, "E1248", {"start": v(-4.53, -9.42) * mm, "end": v(-4.4, -9.46) * mm});
            skLineSegment(sketch, "E1249", {"start": v(-4.4, -9.46) * mm, "end": v(-4.25, -9.47) * mm});
            skLineSegment(sketch, "E1250", {"start": v(-4.25, -9.47) * mm, "end": v(-4.1, -9.46) * mm});
            skLineSegment(sketch, "E1251", {"start": v(-4.1, -9.46) * mm, "end": v(-3.96, -9.42) * mm});
            skLineSegment(sketch, "E1252", {"start": v(-3.96, -9.42) * mm, "end": v(-3.83, -9.35) * mm});
            skLineSegment(sketch, "E1253", {"start": v(-3.83, -9.35) * mm, "end": v(-3.72, -9.26) * mm});
            skLineSegment(sketch, "E1254", {"start": v(-3.72, -9.26) * mm, "end": v(-3.63, -9.14) * mm});
            skLineSegment(sketch, "E1255", {"start": v(-3.63, -9.14) * mm, "end": v(-3.56, -9.02) * mm});
            skLineSegment(sketch, "E1256", {"start": v(-3.56, -9.02) * mm, "end": v(-3.52, -8.88) * mm});
            skLineSegment(sketch, "E1257", {"start": v(-3.47, -5.85) * mm, "end": v(-3.47, -5.77) * mm});
            skLineSegment(sketch, "E1258", {"start": v(-3.47, -5.77) * mm, "end": v(-3.48, -5.85) * mm});
            skLineSegment(sketch, "E1259", {"start": v(-3.48, -5.85) * mm, "end": v(-3.47, -5.85) * mm});
            skLineSegment(sketch, "E1260", {"start": v(-3.47, -5.77) * mm, "end": v(-3.47, -5.08) * mm});
            skLineSegment(sketch, "E1261", {"start": v(-3.53, -5.93) * mm, "end": v(-3.51, -5.85) * mm});
            skLineSegment(sketch, "E1262", {"start": v(-3.51, -5.85) * mm, "end": v(-3.5, -5.82) * mm});
            skLineSegment(sketch, "E1263", {"start": v(-3.5, -5.82) * mm, "end": v(-3.5, -5.82) * mm});
            skLineSegment(sketch, "E1264", {"start": v(-3.5, -5.82) * mm, "end": v(-3.5, -5.77) * mm});
            skLineSegment(sketch, "E1265", {"start": v(-3.5, -5.77) * mm, "end": v(-3.5, -5.08) * mm});
            skLineSegment(sketch, "E1266", {"start": v(-3.5, -5.08) * mm, "end": v(-3.5, -5.03) * mm});
            skLineSegment(sketch, "E1267", {"start": v(-3.5, -5.03) * mm, "end": v(-3.5, -5.03) * mm});
            skLineSegment(sketch, "E1268", {"start": v(-3.5, -5.03) * mm, "end": v(-3.51, -5) * mm});
            skLineSegment(sketch, "E1269", {"start": v(-3.51, -5) * mm, "end": v(-3.53, -4.93) * mm});
            skLineSegment(sketch, "E1270", {"start": v(-3.53, -4.93) * mm, "end": v(-3.57, -4.86) * mm});
            skLineSegment(sketch, "E1271", {"start": v(-3.57, -4.86) * mm, "end": v(-3.62, -4.8) * mm});
            skLineSegment(sketch, "E1272", {"start": v(-3.62, -4.8) * mm, "end": v(-3.68, -4.75) * mm});
            skLineSegment(sketch, "E1273", {"start": v(-3.68, -4.75) * mm, "end": v(-3.75, -4.71) * mm});
            skLineSegment(sketch, "E1274", {"start": v(-3.75, -4.71) * mm, "end": v(-3.82, -4.7) * mm});
            skLineSegment(sketch, "E1275", {"start": v(-3.82, -4.7) * mm, "end": v(-3.85, -4.69) * mm});
            skLineSegment(sketch, "E1276", {"start": v(-3.85, -4.69) * mm, "end": v(-3.85, -4.68) * mm});
            skLineSegment(sketch, "E1277", {"start": v(-3.85, -4.68) * mm, "end": v(-3.9, -4.68) * mm});
            skLineSegment(sketch, "E1278", {"start": v(-3.9, -4.68) * mm, "end": v(-4.6, -4.68) * mm});
            skLineSegment(sketch, "E1279", {"start": v(-4.6, -4.68) * mm, "end": v(-4.64, -4.68) * mm});
            skLineSegment(sketch, "E1280", {"start": v(-4.64, -4.68) * mm, "end": v(-4.64, -4.69) * mm});
            skLineSegment(sketch, "E1281", {"start": v(-4.64, -4.69) * mm, "end": v(-4.67, -4.7) * mm});
            skLineSegment(sketch, "E1282", {"start": v(-4.67, -4.7) * mm, "end": v(-4.75, -4.71) * mm});
            skLineSegment(sketch, "E1283", {"start": v(-4.75, -4.71) * mm, "end": v(-4.82, -4.75) * mm});
            skLineSegment(sketch, "E1284", {"start": v(-4.82, -4.75) * mm, "end": v(-4.88, -4.8) * mm});
            skLineSegment(sketch, "E1285", {"start": v(-4.88, -4.8) * mm, "end": v(-4.92, -4.86) * mm});
            skLineSegment(sketch, "E1286", {"start": v(-4.92, -4.86) * mm, "end": v(-4.96, -4.93) * mm});
            skLineSegment(sketch, "E1287", {"start": v(-4.96, -4.93) * mm, "end": v(-4.98, -5) * mm});
            skLineSegment(sketch, "E1288", {"start": v(-4.98, -5) * mm, "end": v(-4.99, -5.03) * mm});
            skLineSegment(sketch, "E1289", {"start": v(-4.99, -5.03) * mm, "end": v(-5, -5.03) * mm});
            skLineSegment(sketch, "E1290", {"start": v(-5, -5.03) * mm, "end": v(-5, -5.08) * mm});
            skLineSegment(sketch, "E1291", {"start": v(-5, -5.08) * mm, "end": v(-5, -5.2) * mm});
            skLineSegment(sketch, "E1292", {"start": v(-5, -5.2) * mm, "end": v(-7.1, -5.2) * mm});
            skLineSegment(sketch, "E1293", {"start": v(-7.1, -5.2) * mm, "end": v(-7.1, -5.2) * mm});
            skLineSegment(sketch, "E1294", {"start": v(-7.1, -5.2) * mm, "end": v(-7.1, -5.15) * mm});
            skLineSegment(sketch, "E1295", {"start": v(-7.1, -5.15) * mm, "end": v(-7.1, -5.1) * mm});
            skLineSegment(sketch, "E1296", {"start": v(-7.1, -5.1) * mm, "end": v(-7.13, -5.07) * mm});
            skLineSegment(sketch, "E1297", {"start": v(-7.13, -5.07) * mm, "end": v(-7.16, -5.03) * mm});
            skLineSegment(sketch, "E1298", {"start": v(-7.16, -5.03) * mm, "end": v(-9.25, -2.94) * mm});
            skLineSegment(sketch, "E1299", {"start": v(-9.25, -2.94) * mm, "end": v(-9.22, -2.88) * mm});
            skLineSegment(sketch, "E1300", {"start": v(-9.22, -2.88) * mm, "end": v(-9.18, -2.74) * mm});
            skLineSegment(sketch, "E1301", {"start": v(-9.18, -2.74) * mm, "end": v(-9.17, -2.6) * mm});
            skLineSegment(sketch, "E1302", {"start": v(-9.17, -2.6) * mm, "end": v(-9.18, -2.45) * mm});
            skLineSegment(sketch, "E1303", {"start": v(-9.18, -2.45) * mm, "end": v(-9.22, -2.31) * mm});
            skLineSegment(sketch, "E1304", {"start": v(-9.22, -2.31) * mm, "end": v(-9.3, -2.18) * mm});
            skLineSegment(sketch, "E1305", {"start": v(-9.3, -2.18) * mm, "end": v(-9.39, -2.07) * mm});
            skLineSegment(sketch, "E1306", {"start": v(-9.39, -2.07) * mm, "end": v(-9.5, -1.98) * mm});
            skLineSegment(sketch, "E1307", {"start": v(-9.5, -1.98) * mm, "end": v(-9.63, -1.9) * mm});
            skLineSegment(sketch, "E1308", {"start": v(-9.63, -1.9) * mm, "end": v(-9.77, -1.87) * mm});
            skLineSegment(sketch, "E1309", {"start": v(-9.77, -1.87) * mm, "end": v(-9.91, -1.85) * mm});
            skLineSegment(sketch, "E1310", {"start": v(-9.91, -1.85) * mm, "end": v(-10.06, -1.87) * mm});
            skLineSegment(sketch, "E1311", {"start": v(-10.06, -1.87) * mm, "end": v(-10.2, -1.9) * mm});
            skLineSegment(sketch, "E1312", {"start": v(-10.2, -1.9) * mm, "end": v(-10.32, -1.98) * mm});
            skLineSegment(sketch, "E1313", {"start": v(-10.32, -1.98) * mm, "end": v(-10.44, -2.07) * mm});
            skLineSegment(sketch, "E1314", {"start": v(-10.44, -2.07) * mm, "end": v(-10.53, -2.18) * mm});
            skLineSegment(sketch, "E1315", {"start": v(-10.53, -2.18) * mm, "end": v(-10.6, -2.31) * mm});
            skLineSegment(sketch, "E1316", {"start": v(-10.6, -2.31) * mm, "end": v(-10.62, -2.37) * mm});
            skLineSegment(sketch, "E1317", {"start": v(-10.62, -2.37) * mm, "end": v(-13.36, -2.37) * mm});
            skLineSegment(sketch, "E1318", {"start": v(-13.36, -2.37) * mm, "end": v(-13.94, -1.8) * mm});
            skLineSegment(sketch, "E1319", {"start": v(-13.94, -1.8) * mm, "end": v(-13.94, -0.39) * mm});
            skLineSegment(sketch, "E1320", {"start": v(-13.94, -0.39) * mm, "end": v(-11.96, -0.39) * mm});
            skLineSegment(sketch, "E1321", {"start": v(-11.96, -0.39) * mm, "end": v(-11.92, -0.38) * mm});
            skLineSegment(sketch, "E1322", {"start": v(-11.92, -0.38) * mm, "end": v(-11.88, -0.37) * mm});
            skLineSegment(sketch, "E1323", {"start": v(-11.88, -0.37) * mm, "end": v(-11.84, -0.35) * mm});
            skLineSegment(sketch, "E1324", {"start": v(-11.84, -0.35) * mm, "end": v(-11.8, -0.32) * mm});
            skLineSegment(sketch, "E1325", {"start": v(-11.8, -0.32) * mm, "end": v(-9.82, 1.66) * mm});
            skLineSegment(sketch, "E1326", {"start": v(-9.82, 1.66) * mm, "end": v(-5.43, 1.66) * mm});
            skLineSegment(sketch, "E1327", {"start": v(-5.43, 1.66) * mm, "end": v(-5.38, 1.67) * mm});
            skLineSegment(sketch, "E1328", {"start": v(-5.38, 1.67) * mm, "end": v(-5.34, 1.68) * mm});
            skLineSegment(sketch, "E1329", {"start": v(-5.34, 1.68) * mm, "end": v(-5.3, 1.7) * mm});
            skLineSegment(sketch, "E1330", {"start": v(-5.3, 1.7) * mm, "end": v(-5.27, 1.73) * mm});
            skLineSegment(sketch, "E1331", {"start": v(-5.27, 1.73) * mm, "end": v(-4.67, 2.33) * mm});
            skLineSegment(sketch, "E1332", {"start": v(-4.67, 2.33) * mm, "end": v(-4.64, 2.33) * mm});
            skLineSegment(sketch, "E1333", {"start": v(-4.64, 2.33) * mm, "end": v(-4.64, 2.32) * mm});
            skLineSegment(sketch, "E1334", {"start": v(-4.64, 2.32) * mm, "end": v(-4.6, 2.32) * mm});
            skLineSegment(sketch, "E1335", {"start": v(-4.6, 2.32) * mm, "end": v(-3.9, 2.32) * mm});
            skLineSegment(sketch, "E1336", {"start": v(-3.9, 2.32) * mm, "end": v(-3.85, 2.32) * mm});
            skLineSegment(sketch, "E1337", {"start": v(-3.85, 2.32) * mm, "end": v(-3.85, 2.33) * mm});
            skLineSegment(sketch, "E1338", {"start": v(-3.85, 2.33) * mm, "end": v(-3.82, 2.33) * mm});
            skLineSegment(sketch, "E1339", {"start": v(-3.82, 2.33) * mm, "end": v(-3.75, 2.35) * mm});
            skLineSegment(sketch, "E1340", {"start": v(-3.75, 2.35) * mm, "end": v(-3.68, 2.4) * mm});
            skLineSegment(sketch, "E1341", {"start": v(-3.68, 2.4) * mm, "end": v(-3.62, 2.44) * mm});
            skLineSegment(sketch, "E1342", {"start": v(-3.62, 2.44) * mm, "end": v(-3.57, 2.5) * mm});
            skLineSegment(sketch, "E1343", {"start": v(-3.57, 2.5) * mm, "end": v(-3.53, 2.57) * mm});
            skLineSegment(sketch, "E1344", {"start": v(-3.53, 2.57) * mm, "end": v(-3.51, 2.64) * mm});
            skLineSegment(sketch, "E1345", {"start": v(-3.51, 2.64) * mm, "end": v(-3.5, 2.67) * mm});
            skLineSegment(sketch, "E1346", {"start": v(-3.5, 2.67) * mm, "end": v(-3.5, 2.67) * mm});
            skLineSegment(sketch, "E1347", {"start": v(-3.5, 2.67) * mm, "end": v(-3.5, 2.72) * mm});
            skLineSegment(sketch, "E1348", {"start": v(-3.5, 2.72) * mm, "end": v(-3.5, 3.42) * mm});
            skLineSegment(sketch, "E1349", {"start": v(-3.5, 3.42) * mm, "end": v(-3.5, 3.46) * mm});
            skLineSegment(sketch, "E1350", {"start": v(-3.5, 3.46) * mm, "end": v(-3.5, 3.46) * mm});
            skLineSegment(sketch, "E1351", {"start": v(-3.5, 3.46) * mm, "end": v(-3.51, 3.5) * mm});
            skLineSegment(sketch, "E1352", {"start": v(-3.51, 3.5) * mm, "end": v(-3.53, 3.57) * mm});
            skLineSegment(sketch, "E1353", {"start": v(-3.53, 3.57) * mm, "end": v(-3.57, 3.64) * mm});
            skLineSegment(sketch, "E1354", {"start": v(-3.57, 3.64) * mm, "end": v(-3.62, 3.7) * mm});
            skLineSegment(sketch, "E1355", {"start": v(-3.62, 3.7) * mm, "end": v(-3.68, 3.74) * mm});
            skLineSegment(sketch, "E1356", {"start": v(-3.68, 3.74) * mm, "end": v(-3.75, 3.78) * mm});
            skLineSegment(sketch, "E1357", {"start": v(-3.75, 3.78) * mm, "end": v(-3.82, 3.8) * mm});
            skLineSegment(sketch, "E1358", {"start": v(-3.82, 3.8) * mm, "end": v(-3.85, 3.8) * mm});
            skLineSegment(sketch, "E1359", {"start": v(-3.85, 3.8) * mm, "end": v(-3.85, 3.81) * mm});
            skLineSegment(sketch, "E1360", {"start": v(-3.85, 3.81) * mm, "end": v(-3.9, 3.81) * mm});
            skLineSegment(sketch, "E1361", {"start": v(-3.9, 3.81) * mm, "end": v(-4.6, 3.81) * mm});
            skLineSegment(sketch, "E1362", {"start": v(-4.6, 3.81) * mm, "end": v(-4.64, 3.81) * mm});
            skLineSegment(sketch, "E1363", {"start": v(-4.64, 3.81) * mm, "end": v(-4.64, 3.8) * mm});
            skLineSegment(sketch, "E1364", {"start": v(-4.64, 3.8) * mm, "end": v(-4.67, 3.8) * mm});
            skLineSegment(sketch, "E1365", {"start": v(-4.67, 3.8) * mm, "end": v(-4.75, 3.78) * mm});
            skLineSegment(sketch, "E1366", {"start": v(-4.75, 3.78) * mm, "end": v(-4.82, 3.74) * mm});
            skLineSegment(sketch, "E1367", {"start": v(-4.82, 3.74) * mm, "end": v(-4.88, 3.7) * mm});
            skLineSegment(sketch, "E1368", {"start": v(-4.88, 3.7) * mm, "end": v(-4.92, 3.64) * mm});
            skLineSegment(sketch, "E1369", {"start": v(-4.92, 3.64) * mm, "end": v(-4.96, 3.57) * mm});
            skLineSegment(sketch, "E1370", {"start": v(-4.96, 3.57) * mm, "end": v(-4.98, 3.5) * mm});
            skLineSegment(sketch, "E1371", {"start": v(-4.98, 3.5) * mm, "end": v(-4.99, 3.46) * mm});
            skLineSegment(sketch, "E1372", {"start": v(-4.99, 3.46) * mm, "end": v(-5, 3.46) * mm});
            skLineSegment(sketch, "E1373", {"start": v(-5, 3.46) * mm, "end": v(-5, 3.42) * mm});
            skLineSegment(sketch, "E1374", {"start": v(-5, 3.42) * mm, "end": v(-5, 2.72) * mm});
            skLineSegment(sketch, "E1375", {"start": v(-5, 2.72) * mm, "end": v(-5, 2.67) * mm});
            skLineSegment(sketch, "E1376", {"start": v(-5, 2.67) * mm, "end": v(-4.99, 2.67) * mm});
            skLineSegment(sketch, "E1377", {"start": v(-4.99, 2.67) * mm, "end": v(-4.98, 2.65) * mm});
            skLineSegment(sketch, "E1378", {"start": v(-4.98, 2.65) * mm, "end": v(-5.52, 2.11) * mm});
            skLineSegment(sketch, "E1379", {"start": v(-5.52, 2.11) * mm, "end": v(-9.91, 2.11) * mm});
            skLineSegment(sketch, "E1380", {"start": v(-9.91, 2.11) * mm, "end": v(-9.95, 2.1) * mm});
            skLineSegment(sketch, "E1381", {"start": v(-9.95, 2.1) * mm, "end": v(-10, 2.1) * mm});
            skLineSegment(sketch, "E1382", {"start": v(-10, 2.1) * mm, "end": v(-10.04, 2.07) * mm});
            skLineSegment(sketch, "E1383", {"start": v(-10.04, 2.07) * mm, "end": v(-10.07, 2.05) * mm});
            skLineSegment(sketch, "E1384", {"start": v(-10.07, 2.05) * mm, "end": v(-12.06, 0.06) * mm});
            skLineSegment(sketch, "E1385", {"start": v(-12.06, 0.06) * mm, "end": v(-13.94, 0.06) * mm});
            skLineSegment(sketch, "E1386", {"start": v(-13.94, 0.06) * mm, "end": v(-13.94, 2.27) * mm});
            skLineSegment(sketch, "E1387", {"start": v(-13.94, 2.27) * mm, "end": v(-13.34, 2.86) * mm});
            skLineSegment(sketch, "E1388", {"start": v(-13.34, 2.86) * mm, "end": v(-13.27, 2.78) * mm});
            skLineSegment(sketch, "E1389", {"start": v(-13.27, 2.78) * mm, "end": v(-13.16, 2.69) * mm});
            skLineSegment(sketch, "E1390", {"start": v(-13.16, 2.69) * mm, "end": v(-13.03, 2.62) * mm});
            skLineSegment(sketch, "E1391", {"start": v(-13.03, 2.62) * mm, "end": v(-12.89, 2.57) * mm});
            skLineSegment(sketch, "E1392", {"start": v(-12.89, 2.57) * mm, "end": v(-12.74, 2.56) * mm});
            skLineSegment(sketch, "E1393", {"start": v(-12.74, 2.56) * mm, "end": v(-12.6, 2.57) * mm});
            skLineSegment(sketch, "E1394", {"start": v(-12.6, 2.57) * mm, "end": v(-12.46, 2.62) * mm});
            skLineSegment(sketch, "E1395", {"start": v(-12.46, 2.62) * mm, "end": v(-12.33, 2.69) * mm});
            skLineSegment(sketch, "E1396", {"start": v(-12.33, 2.69) * mm, "end": v(-12.22, 2.78) * mm});
            skLineSegment(sketch, "E1397", {"start": v(-12.22, 2.78) * mm, "end": v(-12.12, 2.9) * mm});
            skLineSegment(sketch, "E1398", {"start": v(-12.12, 2.9) * mm, "end": v(-12.06, 3.02) * mm});
            skLineSegment(sketch, "E1399", {"start": v(-12.06, 3.02) * mm, "end": v(-12.01, 3.16) * mm});
            skLineSegment(sketch, "E1400", {"start": v(-12.01, 3.16) * mm, "end": v(-12, 3.3) * mm});
            skLineSegment(sketch, "E1401", {"start": v(-12, 3.3) * mm, "end": v(-12.01, 3.45) * mm});
            skLineSegment(sketch, "E1402", {"start": v(-12.01, 3.45) * mm, "end": v(-12.06, 3.59) * mm});
            skLineSegment(sketch, "E1403", {"start": v(-12.06, 3.59) * mm, "end": v(-12.09, 3.64) * mm});
            skLineSegment(sketch, "E1404", {"start": v(-12.09, 3.64) * mm, "end": v(-6.1, 9.64) * mm});
            skLineSegment(sketch, "E1405", {"start": v(-6.1, 9.64) * mm, "end": v(-4.83, 10.9) * mm});
            skLineSegment(sketch, "E1406", {"start": v(-4.83, 10.9) * mm, "end": v(-4.82, 10.89) * mm});
            skLineSegment(sketch, "E1407", {"start": v(-4.82, 10.89) * mm, "end": v(-4.75, 10.85) * mm});
            skLineSegment(sketch, "E1408", {"start": v(-4.75, 10.85) * mm, "end": v(-4.67, 10.83) * mm});
            skLineSegment(sketch, "E1409", {"start": v(-4.67, 10.83) * mm, "end": v(-4.64, 10.82) * mm});
            skLineSegment(sketch, "E1410", {"start": v(-4.64, 10.82) * mm, "end": v(-4.64, 10.82) * mm});
            skLineSegment(sketch, "E1411", {"start": v(-4.64, 10.82) * mm, "end": v(-4.6, 10.82) * mm});
            skLineSegment(sketch, "E1412", {"start": v(-4.6, 10.82) * mm, "end": v(-3.9, 10.82) * mm});
            skLineSegment(sketch, "E1413", {"start": v(-3.9, 10.82) * mm, "end": v(-3.85, 10.82) * mm});
            skLineSegment(sketch, "E1414", {"start": v(-3.85, 10.82) * mm, "end": v(-3.85, 10.82) * mm});
            skLineSegment(sketch, "E1415", {"start": v(-3.85, 10.82) * mm, "end": v(-3.82, 10.83) * mm});
            skLineSegment(sketch, "E1416", {"start": v(-3.82, 10.83) * mm, "end": v(-3.75, 10.85) * mm});
            skLineSegment(sketch, "E1417", {"start": v(-3.75, 10.85) * mm, "end": v(-3.68, 10.89) * mm});
            skLineSegment(sketch, "E1418", {"start": v(-3.68, 10.89) * mm, "end": v(-3.62, 10.94) * mm});
            skLineSegment(sketch, "E1419", {"start": v(-3.62, 10.94) * mm, "end": v(-3.57, 11) * mm});
            skLineSegment(sketch, "E1420", {"start": v(-3.57, 11) * mm, "end": v(-3.53, 11.06) * mm});
            skLineSegment(sketch, "E1421", {"start": v(-3.53, 11.06) * mm, "end": v(-3.51, 11.14) * mm});
            skLineSegment(sketch, "E1422", {"start": v(-3.51, 11.14) * mm, "end": v(-3.5, 11.17) * mm});
            skLineSegment(sketch, "E1423", {"start": v(-3.5, 11.17) * mm, "end": v(-3.5, 11.17) * mm});
            skLineSegment(sketch, "E1424", {"start": v(-3.5, 11.17) * mm, "end": v(-3.5, 11.22) * mm});
            skLineSegment(sketch, "E1425", {"start": v(-3.5, 11.22) * mm, "end": v(-3.5, 11.91) * mm});
            skLineSegment(sketch, "E1426", {"start": v(-3.5, 11.91) * mm, "end": v(-3.5, 11.96) * mm});
            skLineSegment(sketch, "E1427", {"start": v(-3.5, 11.96) * mm, "end": v(-3.5, 11.96) * mm});
            skLineSegment(sketch, "E1428", {"start": v(-3.5, 11.96) * mm, "end": v(-3.51, 11.99) * mm});
            skLineSegment(sketch, "E1429", {"start": v(-3.51, 11.99) * mm, "end": v(-3.53, 12.06) * mm});
            skLineSegment(sketch, "E1430", {"start": v(-3.53, 12.06) * mm, "end": v(-3.57, 12.13) * mm});
            skLineSegment(sketch, "E1431", {"start": v(-3.57, 12.13) * mm, "end": v(-3.62, 12.2) * mm});
            skLineSegment(sketch, "E1432", {"start": v(-3.62, 12.2) * mm, "end": v(-3.68, 12.24) * mm});
            skLineSegment(sketch, "E1433", {"start": v(-3.68, 12.24) * mm, "end": v(-3.75, 12.28) * mm});
            skLineSegment(sketch, "E1434", {"start": v(-3.75, 12.28) * mm, "end": v(-3.82, 12.3) * mm});
            skLineSegment(sketch, "E1435", {"start": v(-3.82, 12.3) * mm, "end": v(-3.85, 12.3) * mm});
            skLineSegment(sketch, "E1436", {"start": v(-3.85, 12.3) * mm, "end": v(-3.85, 12.3) * mm});
            skLineSegment(sketch, "E1437", {"start": v(-3.85, 12.3) * mm, "end": v(-3.9, 12.3) * mm});
            skLineSegment(sketch, "E1438", {"start": v(-3.9, 12.3) * mm, "end": v(-4.6, 12.3) * mm});
            skLineSegment(sketch, "E1439", {"start": v(-4.6, 12.3) * mm, "end": v(-4.64, 12.3) * mm});
            skLineSegment(sketch, "E1440", {"start": v(-4.64, 12.3) * mm, "end": v(-4.64, 12.3) * mm});
            skLineSegment(sketch, "E1441", {"start": v(-4.64, 12.3) * mm, "end": v(-4.67, 12.3) * mm});
            skLineSegment(sketch, "E1442", {"start": v(-4.67, 12.3) * mm, "end": v(-4.75, 12.28) * mm});
            skLineSegment(sketch, "E1443", {"start": v(-4.75, 12.28) * mm, "end": v(-4.82, 12.24) * mm});
            skLineSegment(sketch, "E1444", {"start": v(-4.82, 12.24) * mm, "end": v(-4.88, 12.2) * mm});
            skLineSegment(sketch, "E1445", {"start": v(-4.88, 12.2) * mm, "end": v(-4.92, 12.13) * mm});
            skLineSegment(sketch, "E1446", {"start": v(-4.92, 12.13) * mm, "end": v(-4.96, 12.06) * mm});
            skLineSegment(sketch, "E1447", {"start": v(-4.96, 12.06) * mm, "end": v(-4.98, 11.99) * mm});
            skLineSegment(sketch, "E1448", {"start": v(-4.98, 11.99) * mm, "end": v(-4.99, 11.96) * mm});
            skLineSegment(sketch, "E1449", {"start": v(-4.99, 11.96) * mm, "end": v(-5, 11.96) * mm});
            skLineSegment(sketch, "E1450", {"start": v(-5, 11.96) * mm, "end": v(-5, 11.91) * mm});
            skLineSegment(sketch, "E1451", {"start": v(-5, 11.91) * mm, "end": v(-5, 11.37) * mm});
            skLineSegment(sketch, "E1452", {"start": v(-5, 11.37) * mm, "end": v(-6.25, 10.1) * mm});
            skLineSegment(sketch, "E1453", {"start": v(-6.25, 10.1) * mm, "end": v(-6.42, 10.28) * mm});
            skLineSegment(sketch, "E1454", {"start": v(-6.42, 10.28) * mm, "end": v(-6.4, 10.33) * mm});
            skLineSegment(sketch, "E1455", {"start": v(-6.4, 10.33) * mm, "end": v(-6.35, 10.47) * mm});
            skLineSegment(sketch, "E1456", {"start": v(-6.35, 10.47) * mm, "end": v(-6.34, 10.62) * mm});
            skLineSegment(sketch, "E1457", {"start": v(-6.34, 10.62) * mm, "end": v(-6.35, 10.76) * mm});
            skLineSegment(sketch, "E1458", {"start": v(-6.35, 10.76) * mm, "end": v(-6.4, 10.9) * mm});
            skLineSegment(sketch, "E1459", {"start": v(-6.4, 10.9) * mm, "end": v(-6.46, 11.03) * mm});
            skLineSegment(sketch, "E1460", {"start": v(-6.46, 11.03) * mm, "end": v(-6.55, 11.14) * mm});
            skLineSegment(sketch, "E1461", {"start": v(-6.55, 11.14) * mm, "end": v(-6.67, 11.24) * mm});
            skLineSegment(sketch, "E1462", {"start": v(-6.67, 11.24) * mm, "end": v(-6.8, 11.3) * mm});
            skLineSegment(sketch, "E1463", {"start": v(-6.8, 11.3) * mm, "end": v(-6.93, 11.35) * mm});
            skLineSegment(sketch, "E1464", {"start": v(-6.93, 11.35) * mm, "end": v(-7.08, 11.36) * mm});
            skLineSegment(sketch, "E1465", {"start": v(-7.08, 11.36) * mm, "end": v(-7.22, 11.35) * mm});
            skLineSegment(sketch, "E1466", {"start": v(-7.22, 11.35) * mm, "end": v(-7.36, 11.3) * mm});
            skLineSegment(sketch, "E1467", {"start": v(-7.36, 11.3) * mm, "end": v(-7.5, 11.24) * mm});
            skLineSegment(sketch, "E1468", {"start": v(-7.5, 11.24) * mm, "end": v(-7.6, 11.14) * mm});
            skLineSegment(sketch, "E1469", {"start": v(-7.6, 11.14) * mm, "end": v(-7.7, 11.03) * mm});
            skLineSegment(sketch, "E1470", {"start": v(-7.7, 11.03) * mm, "end": v(-7.77, 10.9) * mm});
            skLineSegment(sketch, "E1471", {"start": v(-7.77, 10.9) * mm, "end": v(-7.8, 10.76) * mm});
            skLineSegment(sketch, "E1472", {"start": v(-7.8, 10.76) * mm, "end": v(-7.82, 10.62) * mm});
            skLineSegment(sketch, "E1473", {"start": v(-7.82, 10.62) * mm, "end": v(-7.8, 10.47) * mm});
            skLineSegment(sketch, "E1474", {"start": v(-7.8, 10.47) * mm, "end": v(-7.77, 10.33) * mm});
            skLineSegment(sketch, "E1475", {"start": v(-7.77, 10.33) * mm, "end": v(-7.7, 10.2) * mm});
            skLineSegment(sketch, "E1476", {"start": v(-7.7, 10.2) * mm, "end": v(-7.6, 10.1) * mm});
            skLineSegment(sketch, "E1477", {"start": v(-7.6, 10.1) * mm, "end": v(-7.5, 10) * mm});
            skLineSegment(sketch, "E1478", {"start": v(-7.5, 10) * mm, "end": v(-7.36, 9.93) * mm});
            skLineSegment(sketch, "E1479", {"start": v(-7.36, 9.93) * mm, "end": v(-7.22, 9.9) * mm});
            skLineSegment(sketch, "E1480", {"start": v(-7.22, 9.9) * mm, "end": v(-7.08, 9.88) * mm});
            skLineSegment(sketch, "E1481", {"start": v(-7.08, 9.88) * mm, "end": v(-6.93, 9.9) * mm});
            skLineSegment(sketch, "E1482", {"start": v(-6.93, 9.9) * mm, "end": v(-6.8, 9.93) * mm});
            skLineSegment(sketch, "E1483", {"start": v(-6.8, 9.93) * mm, "end": v(-6.74, 9.96) * mm});
            skLineSegment(sketch, "E1484", {"start": v(-6.74, 9.96) * mm, "end": v(-6.57, 9.8) * mm});
            skLineSegment(sketch, "E1485", {"start": v(-6.57, 9.8) * mm, "end": v(-12.4, 3.96) * mm});
            skLineSegment(sketch, "E1486", {"start": v(-12.4, 3.96) * mm, "end": v(-12.46, 4) * mm});
            skLineSegment(sketch, "E1487", {"start": v(-12.46, 4) * mm, "end": v(-12.6, 4.03) * mm});
            skLineSegment(sketch, "E1488", {"start": v(-12.6, 4.03) * mm, "end": v(-12.74, 4.05) * mm});
            skLineSegment(sketch, "E1489", {"start": v(-12.74, 4.05) * mm, "end": v(-12.89, 4.03) * mm});
            skLineSegment(sketch, "E1490", {"start": v(-12.89, 4.03) * mm, "end": v(-13.03, 4) * mm});
            skLineSegment(sketch, "E1491", {"start": v(-13.03, 4) * mm, "end": v(-13.16, 3.92) * mm});
            skLineSegment(sketch, "E1492", {"start": v(-13.16, 3.92) * mm, "end": v(-13.27, 3.83) * mm});
            skLineSegment(sketch, "E1493", {"start": v(-13.27, 3.83) * mm, "end": v(-13.36, 3.72) * mm});
            skLineSegment(sketch, "E1494", {"start": v(-13.36, 3.72) * mm, "end": v(-13.43, 3.59) * mm});
            skLineSegment(sketch, "E1495", {"start": v(-13.43, 3.59) * mm, "end": v(-13.47, 3.45) * mm});
            skLineSegment(sketch, "E1496", {"start": v(-13.47, 3.45) * mm, "end": v(-13.48, 3.35) * mm});
            skLineSegment(sketch, "E1497", {"start": v(-13.48, 3.35) * mm, "end": v(-14.32, 2.52) * mm});
            skLineSegment(sketch, "E1498", {"start": v(-14.32, 2.52) * mm, "end": v(-14.34, 2.48) * mm});
            skLineSegment(sketch, "E1499", {"start": v(-14.34, 2.48) * mm, "end": v(-14.37, 2.45) * mm});
            skLineSegment(sketch, "E1500", {"start": v(-14.37, 2.45) * mm, "end": v(-14.38, 2.4) * mm});
            skLineSegment(sketch, "E1501", {"start": v(-14.38, 2.4) * mm, "end": v(-14.38, 2.36) * mm});
            skLineSegment(sketch, "E1502", {"start": v(-14.38, 2.36) * mm, "end": v(-14.38, -1.89) * mm});
            skLineSegment(sketch, "E1503", {"start": v(-14.38, -1.89) * mm, "end": v(-14.38, -1.93) * mm});
            skLineSegment(sketch, "E1504", {"start": v(-14.38, -1.93) * mm, "end": v(-14.37, -1.97) * mm});
            skLineSegment(sketch, "E1505", {"start": v(-14.37, -1.97) * mm, "end": v(-14.34, -2.01) * mm});
            skLineSegment(sketch, "E1506", {"start": v(-14.34, -2.01) * mm, "end": v(-14.32, -2.05) * mm});
            skLineSegment(sketch, "E1507", {"start": v(-14.32, -2.05) * mm, "end": v(-13.6, -2.75) * mm});
            skLineSegment(sketch, "E1508", {"start": v(-13.6, -2.75) * mm, "end": v(-13.57, -2.78) * mm});
            skLineSegment(sketch, "E1509", {"start": v(-13.57, -2.78) * mm, "end": v(-13.54, -2.8) * mm});
            skLineSegment(sketch, "E1510", {"start": v(-13.54, -2.8) * mm, "end": v(-13.5, -2.81) * mm});
            skLineSegment(sketch, "E1511", {"start": v(-13.5, -2.81) * mm, "end": v(-13.45, -2.82) * mm});
            skLineSegment(sketch, "E1512", {"start": v(-13.45, -2.82) * mm, "end": v(-10.62, -2.82) * mm});
            skLineSegment(sketch, "E1513", {"start": v(-10.62, -2.82) * mm, "end": v(-10.6, -2.88) * mm});
            skLineSegment(sketch, "E1514", {"start": v(-10.6, -2.88) * mm, "end": v(-10.53, -3) * mm});
            skLineSegment(sketch, "E1515", {"start": v(-10.53, -3) * mm, "end": v(-10.44, -3.12) * mm});
            skLineSegment(sketch, "E1516", {"start": v(-10.44, -3.12) * mm, "end": v(-10.32, -3.21) * mm});
            skLineSegment(sketch, "E1517", {"start": v(-10.32, -3.21) * mm, "end": v(-10.2, -3.28) * mm});
            skLineSegment(sketch, "E1518", {"start": v(-10.2, -3.28) * mm, "end": v(-10.06, -3.32) * mm});
            skLineSegment(sketch, "E1519", {"start": v(-10.06, -3.32) * mm, "end": v(-9.91, -3.34) * mm});
            skLineSegment(sketch, "E1520", {"start": v(-9.91, -3.34) * mm, "end": v(-9.77, -3.32) * mm});
            skLineSegment(sketch, "E1521", {"start": v(-9.77, -3.32) * mm, "end": v(-9.63, -3.28) * mm});
            skLineSegment(sketch, "E1522", {"start": v(-9.63, -3.28) * mm, "end": v(-9.57, -3.25) * mm});
            skLineSegment(sketch, "E1523", {"start": v(-9.57, -3.25) * mm, "end": v(-7.54, -5.28) * mm});
            skLineSegment(sketch, "E1524", {"start": v(-7.54, -5.28) * mm, "end": v(-7.54, -5.43) * mm});
            skLineSegment(sketch, "E1525", {"start": v(-7.54, -5.43) * mm, "end": v(-7.54, -5.9) * mm});
            skLineSegment(sketch, "E1526", {"start": v(-7.54, -5.9) * mm, "end": v(-7.6, -5.92) * mm});
            skLineSegment(sketch, "E1527", {"start": v(-7.6, -5.92) * mm, "end": v(-7.73, -5.99) * mm});
            skLineSegment(sketch, "E1528", {"start": v(-7.73, -5.99) * mm, "end": v(-7.84, -6.08) * mm});
            skLineSegment(sketch, "E1529", {"start": v(-7.84, -6.08) * mm, "end": v(-7.93, -6.2) * mm});
            skLineSegment(sketch, "E1530", {"start": v(-7.93, -6.2) * mm, "end": v(-8, -6.32) * mm});
            skLineSegment(sketch, "E1531", {"start": v(-8, -6.32) * mm, "end": v(-8.04, -6.46) * mm});
            skLineSegment(sketch, "E1532", {"start": v(-8.04, -6.46) * mm, "end": v(-8.06, -6.6) * mm});
            skLineSegment(sketch, "E1533", {"start": v(-8.06, -6.6) * mm, "end": v(-8.04, -6.75) * mm});
            skLineSegment(sketch, "E1534", {"start": v(-8.04, -6.75) * mm, "end": v(-8, -6.9) * mm});
            skLineSegment(sketch, "E1535", {"start": v(-8, -6.9) * mm, "end": v(-7.93, -7.02) * mm});
            skLineSegment(sketch, "E1536", {"start": v(-7.93, -7.02) * mm, "end": v(-7.84, -7.13) * mm});
            skLineSegment(sketch, "E1537", {"start": v(-7.84, -7.13) * mm, "end": v(-7.73, -7.23) * mm});
            skLineSegment(sketch, "E1538", {"start": v(-7.73, -7.23) * mm, "end": v(-7.6, -7.3) * mm});
            skLineSegment(sketch, "E1539", {"start": v(-7.6, -7.3) * mm, "end": v(-7.46, -7.34) * mm});
            skLineSegment(sketch, "E1540", {"start": v(-7.46, -7.34) * mm, "end": v(-7.32, -7.35) * mm});
            skLineSegment(sketch, "E1541", {"start": v(-7.32, -7.35) * mm, "end": v(-7.17, -7.34) * mm});
            skLineSegment(sketch, "E1542", {"start": v(-7.17, -7.34) * mm, "end": v(-7.03, -7.3) * mm});
            skLineSegment(sketch, "E1543", {"start": v(-7.03, -7.3) * mm, "end": v(-6.9, -7.23) * mm});
            skLineSegment(sketch, "E1544", {"start": v(-6.9, -7.23) * mm, "end": v(-6.79, -7.13) * mm});
            skLineSegment(sketch, "E1545", {"start": v(-6.79, -7.13) * mm, "end": v(-6.7, -7.02) * mm});
            skLineSegment(sketch, "E1546", {"start": v(-6.7, -7.02) * mm, "end": v(-6.63, -6.9) * mm});
            skLineSegment(sketch, "E1547", {"start": v(-6.63, -6.9) * mm, "end": v(-6.59, -6.75) * mm});
            skLineSegment(sketch, "E1548", {"start": v(-6.59, -6.75) * mm, "end": v(-6.57, -6.6) * mm});
            skLineSegment(sketch, "E1549", {"start": v(-6.57, -6.6) * mm, "end": v(-6.59, -6.46) * mm});
            skLineSegment(sketch, "E1550", {"start": v(-6.59, -6.46) * mm, "end": v(-6.63, -6.32) * mm});
            skLineSegment(sketch, "E1551", {"start": v(-6.63, -6.32) * mm, "end": v(-6.7, -6.2) * mm});
            skLineSegment(sketch, "E1552", {"start": v(-6.7, -6.2) * mm, "end": v(-6.79, -6.08) * mm});
            skLineSegment(sketch, "E1553", {"start": v(-6.79, -6.08) * mm, "end": v(-6.9, -5.99) * mm});
            skLineSegment(sketch, "E1554", {"start": v(-6.9, -5.99) * mm, "end": v(-7.03, -5.92) * mm});
            skLineSegment(sketch, "E1555", {"start": v(-7.03, -5.92) * mm, "end": v(-7.1, -5.9) * mm});
            skLineSegment(sketch, "E1556", {"start": v(-7.1, -5.9) * mm, "end": v(-7.1, -5.65) * mm});
            skLineSegment(sketch, "E1557", {"start": v(-7.1, -5.65) * mm, "end": v(-5, -5.65) * mm});
            skLineSegment(sketch, "E1558", {"start": v(-5, -5.65) * mm, "end": v(-5, -5.77) * mm});
            skLineSegment(sketch, "E1559", {"start": v(-5, -5.77) * mm, "end": v(-5, -5.82) * mm});
            skLineSegment(sketch, "E1560", {"start": v(-5, -5.82) * mm, "end": v(-4.99, -5.82) * mm});
            skLineSegment(sketch, "E1561", {"start": v(-4.99, -5.82) * mm, "end": v(-4.98, -5.85) * mm});
            skLineSegment(sketch, "E1562", {"start": v(-4.98, -5.85) * mm, "end": v(-4.96, -5.93) * mm});
            skLineSegment(sketch, "E1563", {"start": v(-4.96, -5.93) * mm, "end": v(-4.92, -6) * mm});
            skLineSegment(sketch, "E1564", {"start": v(-4.92, -6) * mm, "end": v(-4.88, -6.06) * mm});
            skLineSegment(sketch, "E1565", {"start": v(-4.88, -6.06) * mm, "end": v(-4.82, -6.1) * mm});
            skLineSegment(sketch, "E1566", {"start": v(-4.82, -6.1) * mm, "end": v(-4.75, -6.14) * mm});
            skLineSegment(sketch, "E1567", {"start": v(-4.75, -6.14) * mm, "end": v(-4.67, -6.16) * mm});
            skLineSegment(sketch, "E1568", {"start": v(-4.67, -6.16) * mm, "end": v(-4.64, -6.17) * mm});
            skLineSegment(sketch, "E1569", {"start": v(-4.64, -6.17) * mm, "end": v(-4.64, -6.17) * mm});
            skLineSegment(sketch, "E1570", {"start": v(-4.64, -6.17) * mm, "end": v(-4.6, -6.17) * mm});
            skLineSegment(sketch, "E1571", {"start": v(-4.6, -6.17) * mm, "end": v(-3.9, -6.17) * mm});
            skLineSegment(sketch, "E1572", {"start": v(-3.9, -6.17) * mm, "end": v(-3.85, -6.17) * mm});
            skLineSegment(sketch, "E1573", {"start": v(-3.85, -6.17) * mm, "end": v(-3.85, -6.17) * mm});
            skLineSegment(sketch, "E1574", {"start": v(-3.85, -6.17) * mm, "end": v(-3.82, -6.16) * mm});
            skLineSegment(sketch, "E1575", {"start": v(-3.82, -6.16) * mm, "end": v(-3.75, -6.14) * mm});
            skLineSegment(sketch, "E1576", {"start": v(-3.75, -6.14) * mm, "end": v(-3.68, -6.1) * mm});
            skLineSegment(sketch, "E1577", {"start": v(-3.68, -6.1) * mm, "end": v(-3.62, -6.06) * mm});
            skLineSegment(sketch, "E1578", {"start": v(-3.62, -6.06) * mm, "end": v(-3.57, -6) * mm});
            skLineSegment(sketch, "E1579", {"start": v(-3.57, -6) * mm, "end": v(-3.53, -5.93) * mm});
            skLineSegment(sketch, "E1580", {"start": v(-3.47, -5.08) * mm, "end": v(-3.47, -5) * mm});
            skLineSegment(sketch, "E1581", {"start": v(-3.47, -5) * mm, "end": v(-3.48, -5) * mm});
            skLineSegment(sketch, "E1582", {"start": v(-3.48, -5) * mm, "end": v(-3.47, -5.08) * mm});
            skLineSegment(sketch, "E1583", {"start": v(3.57, 6.12) * mm, "end": v(3.55, 6.2) * mm});
            skLineSegment(sketch, "E1584", {"start": v(3.55, 6.2) * mm, "end": v(3.48, 6.33) * mm});
            skLineSegment(sketch, "E1585", {"start": v(3.48, 6.33) * mm, "end": v(3.38, 6.45) * mm});
            skLineSegment(sketch, "E1586", {"start": v(3.38, 6.45) * mm, "end": v(3.26, 6.54) * mm});
            skLineSegment(sketch, "E1587", {"start": v(3.26, 6.54) * mm, "end": v(3.13, 6.62) * mm});
            skLineSegment(sketch, "E1588", {"start": v(3.13, 6.62) * mm, "end": v(2.98, 6.66) * mm});
            skLineSegment(sketch, "E1589", {"start": v(2.98, 6.66) * mm, "end": v(2.83, 6.67) * mm});
            skLineSegment(sketch, "E1590", {"start": v(2.83, 6.67) * mm, "end": v(2.68, 6.66) * mm});
            skLineSegment(sketch, "E1591", {"start": v(2.68, 6.66) * mm, "end": v(2.54, 6.62) * mm});
            skLineSegment(sketch, "E1592", {"start": v(2.54, 6.62) * mm, "end": v(2.4, 6.54) * mm});
            skLineSegment(sketch, "E1593", {"start": v(2.4, 6.54) * mm, "end": v(2.28, 6.45) * mm});
            skLineSegment(sketch, "E1594", {"start": v(2.28, 6.45) * mm, "end": v(2.19, 6.33) * mm});
            skLineSegment(sketch, "E1595", {"start": v(2.19, 6.33) * mm, "end": v(2.12, 6.2) * mm});
            skLineSegment(sketch, "E1596", {"start": v(2.12, 6.2) * mm, "end": v(2.07, 6.05) * mm});
            skLineSegment(sketch, "E1597", {"start": v(2.07, 6.05) * mm, "end": v(2.06, 5.9) * mm});
            skLineSegment(sketch, "E1598", {"start": v(2.06, 5.9) * mm, "end": v(2.07, 5.75) * mm});
            skLineSegment(sketch, "E1599", {"start": v(2.07, 5.75) * mm, "end": v(2.12, 5.6) * mm});
            skLineSegment(sketch, "E1600", {"start": v(2.12, 5.6) * mm, "end": v(2.19, 5.47) * mm});
            skLineSegment(sketch, "E1601", {"start": v(2.19, 5.47) * mm, "end": v(2.28, 5.35) * mm});
            skLineSegment(sketch, "E1602", {"start": v(2.28, 5.35) * mm, "end": v(2.4, 5.26) * mm});
            skLineSegment(sketch, "E1603", {"start": v(2.4, 5.26) * mm, "end": v(2.54, 5.18) * mm});
            skLineSegment(sketch, "E1604", {"start": v(2.54, 5.18) * mm, "end": v(2.68, 5.14) * mm});
            skLineSegment(sketch, "E1605", {"start": v(2.68, 5.14) * mm, "end": v(2.83, 5.13) * mm});
            skLineSegment(sketch, "E1606", {"start": v(2.83, 5.13) * mm, "end": v(2.98, 5.14) * mm});
            skLineSegment(sketch, "E1607", {"start": v(2.98, 5.14) * mm, "end": v(3.13, 5.18) * mm});
            skLineSegment(sketch, "E1608", {"start": v(3.13, 5.18) * mm, "end": v(3.26, 5.26) * mm});
            skLineSegment(sketch, "E1609", {"start": v(3.26, 5.26) * mm, "end": v(3.38, 5.35) * mm});
            skLineSegment(sketch, "E1610", {"start": v(3.38, 5.35) * mm, "end": v(3.48, 5.47) * mm});
            skLineSegment(sketch, "E1611", {"start": v(3.48, 5.47) * mm, "end": v(3.55, 5.6) * mm});
            skLineSegment(sketch, "E1612", {"start": v(3.55, 5.6) * mm, "end": v(3.57, 5.68) * mm});
            skLineSegment(sketch, "E1613", {"start": v(8.64, 9.16) * mm, "end": v(8.64, 9.17) * mm});
            skLineSegment(sketch, "E1614", {"start": v(8.64, 9.17) * mm, "end": v(8.56, 9.17) * mm});
            skLineSegment(sketch, "E1615", {"start": v(8.56, 9.17) * mm, "end": v(8.64, 9.16) * mm});
            skLineSegment(sketch, "E1616", {"start": v(8.55, 9.17) * mm, "end": v(7.5, 9.17) * mm});
            skLineSegment(sketch, "E1617", {"start": v(7.48, 9.17) * mm, "end": v(7.41, 9.17) * mm});
            skLineSegment(sketch, "E1618", {"start": v(7.41, 9.17) * mm, "end": v(7.41, 9.16) * mm});
            skLineSegment(sketch, "E1619", {"start": v(7.41, 9.16) * mm, "end": v(7.48, 9.17) * mm});
            skLineSegment(sketch, "E1620", {"start": v(-3.51, -2.37) * mm, "end": v(-3.53, -2.3) * mm});
            skLineSegment(sketch, "E1621", {"start": v(-3.53, -2.3) * mm, "end": v(-3.6, -2.17) * mm});
            skLineSegment(sketch, "E1622", {"start": v(-3.6, -2.17) * mm, "end": v(-3.7, -2.05) * mm});
            skLineSegment(sketch, "E1623", {"start": v(-3.7, -2.05) * mm, "end": v(-3.82, -1.95) * mm});
            skLineSegment(sketch, "E1624", {"start": v(-3.82, -1.95) * mm, "end": v(-3.95, -1.88) * mm});
            skLineSegment(sketch, "E1625", {"start": v(-3.95, -1.88) * mm, "end": v(-4.1, -1.84) * mm});
            skLineSegment(sketch, "E1626", {"start": v(-4.1, -1.84) * mm, "end": v(-4.25, -1.82) * mm});
            skLineSegment(sketch, "E1627", {"start": v(-4.25, -1.82) * mm, "end": v(-4.4, -1.84) * mm});
            skLineSegment(sketch, "E1628", {"start": v(-4.4, -1.84) * mm, "end": v(-4.54, -1.88) * mm});
            skLineSegment(sketch, "E1629", {"start": v(-4.54, -1.88) * mm, "end": v(-4.68, -1.95) * mm});
            skLineSegment(sketch, "E1630", {"start": v(-4.68, -1.95) * mm, "end": v(-4.8, -2.05) * mm});
            skLineSegment(sketch, "E1631", {"start": v(-4.8, -2.05) * mm, "end": v(-4.9, -2.17) * mm});
            skLineSegment(sketch, "E1632", {"start": v(-4.9, -2.17) * mm, "end": v(-4.96, -2.3) * mm});
            skLineSegment(sketch, "E1633", {"start": v(-4.96, -2.3) * mm, "end": v(-5, -2.44) * mm});
            skLineSegment(sketch, "E1634", {"start": v(-5, -2.44) * mm, "end": v(-5.02, -2.6) * mm});
            skLineSegment(sketch, "E1635", {"start": v(-5.02, -2.6) * mm, "end": v(-5, -2.75) * mm});
            skLineSegment(sketch, "E1636", {"start": v(-5, -2.75) * mm, "end": v(-4.96, -2.9) * mm});
            skLineSegment(sketch, "E1637", {"start": v(-4.96, -2.9) * mm, "end": v(-4.9, -3.03) * mm});
            skLineSegment(sketch, "E1638", {"start": v(-4.9, -3.03) * mm, "end": v(-4.8, -3.14) * mm});
            skLineSegment(sketch, "E1639", {"start": v(-4.8, -3.14) * mm, "end": v(-4.68, -3.24) * mm});
            skLineSegment(sketch, "E1640", {"start": v(-4.68, -3.24) * mm, "end": v(-4.54, -3.31) * mm});
            skLineSegment(sketch, "E1641", {"start": v(-4.54, -3.31) * mm, "end": v(-4.4, -3.36) * mm});
            skLineSegment(sketch, "E1642", {"start": v(-4.4, -3.36) * mm, "end": v(-4.25, -3.37) * mm});
            skLineSegment(sketch, "E1643", {"start": v(-4.25, -3.37) * mm, "end": v(-4.1, -3.36) * mm});
            skLineSegment(sketch, "E1644", {"start": v(-4.1, -3.36) * mm, "end": v(-3.95, -3.31) * mm});
            skLineSegment(sketch, "E1645", {"start": v(-3.95, -3.31) * mm, "end": v(-3.82, -3.24) * mm});
            skLineSegment(sketch, "E1646", {"start": v(-3.82, -3.24) * mm, "end": v(-3.7, -3.14) * mm});
            skLineSegment(sketch, "E1647", {"start": v(-3.7, -3.14) * mm, "end": v(-3.6, -3.03) * mm});
            skLineSegment(sketch, "E1648", {"start": v(-3.6, -3.03) * mm, "end": v(-3.53, -2.9) * mm});
            skLineSegment(sketch, "E1649", {"start": v(-3.53, -2.9) * mm, "end": v(-3.51, -2.82) * mm});
            skLineSegment(sketch, "E1650", {"start": v(-5.01, -5.85) * mm, "end": v(-5.02, -5.77) * mm});
            skLineSegment(sketch, "E1651", {"start": v(-5.02, -5.77) * mm, "end": v(-5.02, -5.85) * mm});
            skLineSegment(sketch, "E1652", {"start": v(-5.02, -5.85) * mm, "end": v(-5.01, -5.85) * mm});
            skLineSegment(sketch, "E1653", {"start": v(-5.02, -5.65) * mm, "end": v(-5.02, -5.77) * mm});
            skLineSegment(sketch, "E1654", {"start": v(-5.02, -5.08) * mm, "end": v(-5.01, -5) * mm});
            skLineSegment(sketch, "E1655", {"start": v(-5.01, -5) * mm, "end": v(-5.02, -5) * mm});
            skLineSegment(sketch, "E1656", {"start": v(-5.02, -5) * mm, "end": v(-5.02, -5.08) * mm});
            skLineSegment(sketch, "E1657", {"start": v(-5.02, -5.08) * mm, "end": v(-5.02, -5.2) * mm});
            skLineSegment(sketch, "E1658", {"start": v(2.67, 9.03) * mm, "end": v(2.06, 9.03) * mm});
            skLineSegment(sketch, "E1659", {"start": v(2.06, 9.03) * mm, "end": v(2.06, 7.48) * mm});
            skLineSegment(sketch, "E1660", {"start": v(2.06, 7.48) * mm, "end": v(3.6, 7.48) * mm});
            skLineSegment(sketch, "E1661", {"start": v(3.6, 7.48) * mm, "end": v(3.6, 9.03) * mm});
            skLineSegment(sketch, "E1662", {"start": v(3.6, 9.03) * mm, "end": v(3, 9.03) * mm});
            skLineSegment(sketch, "E1663", {"start": v(3.58, 7.52) * mm, "end": v(3.58, 9) * mm});
            skLineSegment(sketch, "E1664", {"start": v(3.58, 9) * mm, "end": v(3, 9) * mm});
            skLineSegment(sketch, "E1665", {"start": v(3, 9) * mm, "end": v(3, 10.84) * mm});
            skLineSegment(sketch, "E1666", {"start": v(3, 10.84) * mm, "end": v(3.12, 10.88) * mm});
            skLineSegment(sketch, "E1667", {"start": v(3.12, 10.88) * mm, "end": v(3.24, 10.95) * mm});
            skLineSegment(sketch, "E1668", {"start": v(3.24, 10.95) * mm, "end": v(3.36, 11.04) * mm});
            skLineSegment(sketch, "E1669", {"start": v(3.36, 11.04) * mm, "end": v(3.45, 11.15) * mm});
            skLineSegment(sketch, "E1670", {"start": v(3.45, 11.15) * mm, "end": v(3.52, 11.28) * mm});
            skLineSegment(sketch, "E1671", {"start": v(3.52, 11.28) * mm, "end": v(3.56, 11.42) * mm});
            skLineSegment(sketch, "E1672", {"start": v(3.56, 11.42) * mm, "end": v(3.58, 11.56) * mm});
            skLineSegment(sketch, "E1673", {"start": v(3.58, 11.56) * mm, "end": v(3.56, 11.7) * mm});
            skLineSegment(sketch, "E1674", {"start": v(3.56, 11.7) * mm, "end": v(3.52, 11.85) * mm});
            skLineSegment(sketch, "E1675", {"start": v(3.52, 11.85) * mm, "end": v(3.45, 11.98) * mm});
            skLineSegment(sketch, "E1676", {"start": v(3.45, 11.98) * mm, "end": v(3.36, 12.09) * mm});
            skLineSegment(sketch, "E1677", {"start": v(3.36, 12.09) * mm, "end": v(3.24, 12.18) * mm});
            skLineSegment(sketch, "E1678", {"start": v(3.24, 12.18) * mm, "end": v(3.12, 12.25) * mm});
            skLineSegment(sketch, "E1679", {"start": v(3.12, 12.25) * mm, "end": v(2.98, 12.3) * mm});
            skLineSegment(sketch, "E1680", {"start": v(2.98, 12.3) * mm, "end": v(2.83, 12.3) * mm});
            skLineSegment(sketch, "E1681", {"start": v(2.83, 12.3) * mm, "end": v(2.69, 12.3) * mm});
            skLineSegment(sketch, "E1682", {"start": v(2.69, 12.3) * mm, "end": v(2.55, 12.25) * mm});
            skLineSegment(sketch, "E1683", {"start": v(2.55, 12.25) * mm, "end": v(2.42, 12.18) * mm});
            skLineSegment(sketch, "E1684", {"start": v(2.42, 12.18) * mm, "end": v(2.3, 12.09) * mm});
            skLineSegment(sketch, "E1685", {"start": v(2.3, 12.09) * mm, "end": v(2.21, 11.98) * mm});
            skLineSegment(sketch, "E1686", {"start": v(2.21, 11.98) * mm, "end": v(2.15, 11.85) * mm});
            skLineSegment(sketch, "E1687", {"start": v(2.15, 11.85) * mm, "end": v(2.1, 11.7) * mm});
            skLineSegment(sketch, "E1688", {"start": v(2.1, 11.7) * mm, "end": v(2.09, 11.56) * mm});
            skLineSegment(sketch, "E1689", {"start": v(2.09, 11.56) * mm, "end": v(2.1, 11.42) * mm});
            skLineSegment(sketch, "E1690", {"start": v(2.1, 11.42) * mm, "end": v(2.15, 11.28) * mm});
            skLineSegment(sketch, "E1691", {"start": v(2.15, 11.28) * mm, "end": v(2.21, 11.15) * mm});
            skLineSegment(sketch, "E1692", {"start": v(2.21, 11.15) * mm, "end": v(2.3, 11.04) * mm});
            skLineSegment(sketch, "E1693", {"start": v(2.3, 11.04) * mm, "end": v(2.42, 10.95) * mm});
            skLineSegment(sketch, "E1694", {"start": v(2.42, 10.95) * mm, "end": v(2.55, 10.88) * mm});
            skLineSegment(sketch, "E1695", {"start": v(2.55, 10.88) * mm, "end": v(2.67, 10.84) * mm});
            skLineSegment(sketch, "E1696", {"start": v(2.67, 10.84) * mm, "end": v(2.67, 9) * mm});
            skLineSegment(sketch, "E1697", {"start": v(2.67, 9) * mm, "end": v(2.09, 9) * mm});
            skLineSegment(sketch, "E1698", {"start": v(2.09, 9) * mm, "end": v(2.09, 7.52) * mm});
            skLineSegment(sketch, "E1699", {"start": v(2.09, 7.52) * mm, "end": v(3.58, 7.52) * mm});
            skLineSegment(sketch, "E1700", {"start": v(-4.93, 0.13) * mm, "end": v(-4.96, 0.06) * mm});
            skLineSegment(sketch, "E1701", {"start": v(-4.96, 0.06) * mm, "end": v(-5, -0.08) * mm});
            skLineSegment(sketch, "E1702", {"start": v(-5, -0.08) * mm, "end": v(-5.02, -0.24) * mm});
            skLineSegment(sketch, "E1703", {"start": v(-5.02, -0.24) * mm, "end": v(-5, -0.39) * mm});
            skLineSegment(sketch, "E1704", {"start": v(-5, -0.39) * mm, "end": v(-4.96, -0.53) * mm});
            skLineSegment(sketch, "E1705", {"start": v(-4.96, -0.53) * mm, "end": v(-4.9, -0.67) * mm});
            skLineSegment(sketch, "E1706", {"start": v(-4.9, -0.67) * mm, "end": v(-4.8, -0.78) * mm});
            skLineSegment(sketch, "E1707", {"start": v(-4.8, -0.78) * mm, "end": v(-4.68, -0.88) * mm});
            skLineSegment(sketch, "E1708", {"start": v(-4.68, -0.88) * mm, "end": v(-4.54, -0.95) * mm});
            skLineSegment(sketch, "E1709", {"start": v(-4.54, -0.95) * mm, "end": v(-4.4, -1) * mm});
            skLineSegment(sketch, "E1710", {"start": v(-4.4, -1) * mm, "end": v(-4.25, -1.01) * mm});
            skLineSegment(sketch, "E1711", {"start": v(-4.25, -1.01) * mm, "end": v(-4.1, -1) * mm});
            skLineSegment(sketch, "E1712", {"start": v(-4.1, -1) * mm, "end": v(-3.95, -0.95) * mm});
            skLineSegment(sketch, "E1713", {"start": v(-3.95, -0.95) * mm, "end": v(-3.82, -0.88) * mm});
            skLineSegment(sketch, "E1714", {"start": v(-3.82, -0.88) * mm, "end": v(-3.7, -0.78) * mm});
            skLineSegment(sketch, "E1715", {"start": v(-3.7, -0.78) * mm, "end": v(-3.6, -0.67) * mm});
            skLineSegment(sketch, "E1716", {"start": v(-3.6, -0.67) * mm, "end": v(-3.53, -0.53) * mm});
            skLineSegment(sketch, "E1717", {"start": v(-3.53, -0.53) * mm, "end": v(-3.49, -0.39) * mm});
            skLineSegment(sketch, "E1718", {"start": v(-3.49, -0.39) * mm, "end": v(-3.47, -0.24) * mm});
            skLineSegment(sketch, "E1719", {"start": v(-3.47, -0.24) * mm, "end": v(-3.49, -0.08) * mm});
            skLineSegment(sketch, "E1720", {"start": v(-3.49, -0.08) * mm, "end": v(-3.53, 0.06) * mm});
            skLineSegment(sketch, "E1721", {"start": v(-3.53, 0.06) * mm, "end": v(-3.6, 0.2) * mm});
            skLineSegment(sketch, "E1722", {"start": v(-3.6, 0.2) * mm, "end": v(-3.7, 0.31) * mm});
            skLineSegment(sketch, "E1723", {"start": v(-3.7, 0.31) * mm, "end": v(-3.82, 0.4) * mm});
            skLineSegment(sketch, "E1724", {"start": v(-3.82, 0.4) * mm, "end": v(-3.95, 0.48) * mm});
            skLineSegment(sketch, "E1725", {"start": v(-3.95, 0.48) * mm, "end": v(-4.1, 0.52) * mm});
            skLineSegment(sketch, "E1726", {"start": v(-4.1, 0.52) * mm, "end": v(-4.25, 0.54) * mm});
            skLineSegment(sketch, "E1727", {"start": v(-4.25, 0.54) * mm, "end": v(-4.4, 0.52) * mm});
            skLineSegment(sketch, "E1728", {"start": v(-4.4, 0.52) * mm, "end": v(-4.54, 0.48) * mm});
            skLineSegment(sketch, "E1729", {"start": v(-4.54, 0.48) * mm, "end": v(-4.61, 0.44) * mm});
            skLineSegment(sketch, "E1730", {"start": v(-3.63, -0.65) * mm, "end": v(-3.56, -0.52) * mm});
            skLineSegment(sketch, "E1731", {"start": v(-3.56, -0.52) * mm, "end": v(-3.52, -0.38) * mm});
            skLineSegment(sketch, "E1732", {"start": v(-3.52, -0.38) * mm, "end": v(-3.5, -0.24) * mm});
            skLineSegment(sketch, "E1733", {"start": v(-3.5, -0.24) * mm, "end": v(-3.52, -0.1) * mm});
            skLineSegment(sketch, "E1734", {"start": v(-3.52, -0.1) * mm, "end": v(-3.56, 0.05) * mm});
            skLineSegment(sketch, "E1735", {"start": v(-3.56, 0.05) * mm, "end": v(-3.63, 0.18) * mm});
            skLineSegment(sketch, "E1736", {"start": v(-3.63, 0.18) * mm, "end": v(-3.72, 0.29) * mm});
            skLineSegment(sketch, "E1737", {"start": v(-3.72, 0.29) * mm, "end": v(-3.83, 0.38) * mm});
            skLineSegment(sketch, "E1738", {"start": v(-3.83, 0.38) * mm, "end": v(-3.96, 0.45) * mm});
            skLineSegment(sketch, "E1739", {"start": v(-3.96, 0.45) * mm, "end": v(-4.1, 0.5) * mm});
            skLineSegment(sketch, "E1740", {"start": v(-4.1, 0.5) * mm, "end": v(-4.25, 0.5) * mm});
            skLineSegment(sketch, "E1741", {"start": v(-4.25, 0.5) * mm, "end": v(-4.4, 0.5) * mm});
            skLineSegment(sketch, "E1742", {"start": v(-4.4, 0.5) * mm, "end": v(-4.53, 0.45) * mm});
            skLineSegment(sketch, "E1743", {"start": v(-4.53, 0.45) * mm, "end": v(-4.59, 0.42) * mm});
            skLineSegment(sketch, "E1744", {"start": v(-4.59, 0.42) * mm, "end": v(-4.8, 0.63) * mm});
            skLineSegment(sketch, "E1745", {"start": v(-4.8, 0.63) * mm, "end": v(-4.83, 0.66) * mm});
            skLineSegment(sketch, "E1746", {"start": v(-4.83, 0.66) * mm, "end": v(-4.87, 0.68) * mm});
            skLineSegment(sketch, "E1747", {"start": v(-4.87, 0.68) * mm, "end": v(-4.91, 0.7) * mm});
            skLineSegment(sketch, "E1748", {"start": v(-4.91, 0.7) * mm, "end": v(-4.96, 0.7) * mm});
            skLineSegment(sketch, "E1749", {"start": v(-4.96, 0.7) * mm, "end": v(-6.57, 0.7) * mm});
            skLineSegment(sketch, "E1750", {"start": v(-6.57, 0.7) * mm, "end": v(-6.57, 0.82) * mm});
            skLineSegment(sketch, "E1751", {"start": v(-6.57, 0.82) * mm, "end": v(-6.57, 0.87) * mm});
            skLineSegment(sketch, "E1752", {"start": v(-6.57, 0.87) * mm, "end": v(-6.58, 0.87) * mm});
            skLineSegment(sketch, "E1753", {"start": v(-6.58, 0.87) * mm, "end": v(-6.58, 0.9) * mm});
            skLineSegment(sketch, "E1754", {"start": v(-6.58, 0.9) * mm, "end": v(-6.6, 0.97) * mm});
            skLineSegment(sketch, "E1755", {"start": v(-6.6, 0.97) * mm, "end": v(-6.64, 1.04) * mm});
            skLineSegment(sketch, "E1756", {"start": v(-6.64, 1.04) * mm, "end": v(-6.69, 1.1) * mm});
            skLineSegment(sketch, "E1757", {"start": v(-6.69, 1.1) * mm, "end": v(-6.75, 1.15) * mm});
            skLineSegment(sketch, "E1758", {"start": v(-6.75, 1.15) * mm, "end": v(-6.82, 1.19) * mm});
            skLineSegment(sketch, "E1759", {"start": v(-6.82, 1.19) * mm, "end": v(-6.89, 1.2) * mm});
            skLineSegment(sketch, "E1760", {"start": v(-6.89, 1.2) * mm, "end": v(-6.92, 1.21) * mm});
            skLineSegment(sketch, "E1761", {"start": v(-6.92, 1.21) * mm, "end": v(-6.92, 1.22) * mm});
            skLineSegment(sketch, "E1762", {"start": v(-6.92, 1.22) * mm, "end": v(-6.97, 1.22) * mm});
            skLineSegment(sketch, "E1763", {"start": v(-6.97, 1.22) * mm, "end": v(-7.66, 1.22) * mm});
            skLineSegment(sketch, "E1764", {"start": v(-7.66, 1.22) * mm, "end": v(-7.71, 1.22) * mm});
            skLineSegment(sketch, "E1765", {"start": v(-7.71, 1.22) * mm, "end": v(-7.71, 1.21) * mm});
            skLineSegment(sketch, "E1766", {"start": v(-7.71, 1.21) * mm, "end": v(-7.74, 1.2) * mm});
            skLineSegment(sketch, "E1767", {"start": v(-7.74, 1.2) * mm, "end": v(-7.81, 1.19) * mm});
            skLineSegment(sketch, "E1768", {"start": v(-7.81, 1.19) * mm, "end": v(-7.88, 1.15) * mm});
            skLineSegment(sketch, "E1769", {"start": v(-7.88, 1.15) * mm, "end": v(-7.94, 1.1) * mm});
            skLineSegment(sketch, "E1770", {"start": v(-7.94, 1.1) * mm, "end": v(-8, 1.04) * mm});
            skLineSegment(sketch, "E1771", {"start": v(-8, 1.04) * mm, "end": v(-8.03, 0.97) * mm});
            skLineSegment(sketch, "E1772", {"start": v(-8.03, 0.97) * mm, "end": v(-8.05, 0.9) * mm});
            skLineSegment(sketch, "E1773", {"start": v(-8.05, 0.9) * mm, "end": v(-8.05, 0.87) * mm});
            skLineSegment(sketch, "E1774", {"start": v(-8.05, 0.87) * mm, "end": v(-8.06, 0.87) * mm});
            skLineSegment(sketch, "E1775", {"start": v(-8.06, 0.87) * mm, "end": v(-8.06, 0.82) * mm});
            skLineSegment(sketch, "E1776", {"start": v(-8.06, 0.82) * mm, "end": v(-8.06, 0.7) * mm});
            skLineSegment(sketch, "E1777", {"start": v(-8.06, 0.7) * mm, "end": v(-9.91, 0.7) * mm});
            skLineSegment(sketch, "E1778", {"start": v(-9.91, 0.7) * mm, "end": v(-9.95, 0.7) * mm});
            skLineSegment(sketch, "E1779", {"start": v(-9.95, 0.7) * mm, "end": v(-10, 0.68) * mm});
            skLineSegment(sketch, "E1780", {"start": v(-10, 0.68) * mm, "end": v(-10.04, 0.66) * mm});
            skLineSegment(sketch, "E1781", {"start": v(-10.04, 0.66) * mm, "end": v(-10.07, 0.63) * mm});
            skLineSegment(sketch, "E1782", {"start": v(-10.07, 0.63) * mm, "end": v(-11.9, -1.2) * mm});
            skLineSegment(sketch, "E1783", {"start": v(-11.9, -1.2) * mm, "end": v(-12.04, -1.2) * mm});
            skLineSegment(sketch, "E1784", {"start": v(-12.04, -1.2) * mm, "end": v(-12.06, -1.13) * mm});
            skLineSegment(sketch, "E1785", {"start": v(-12.06, -1.13) * mm, "end": v(-12.12, -1) * mm});
            skLineSegment(sketch, "E1786", {"start": v(-12.12, -1) * mm, "end": v(-12.22, -0.9) * mm});
            skLineSegment(sketch, "E1787", {"start": v(-12.22, -0.9) * mm, "end": v(-12.33, -0.8) * mm});
            skLineSegment(sketch, "E1788", {"start": v(-12.33, -0.8) * mm, "end": v(-12.46, -0.73) * mm});
            skLineSegment(sketch, "E1789", {"start": v(-12.46, -0.73) * mm, "end": v(-12.6, -0.69) * mm});
            skLineSegment(sketch, "E1790", {"start": v(-12.6, -0.69) * mm, "end": v(-12.74, -0.67) * mm});
            skLineSegment(sketch, "E1791", {"start": v(-12.74, -0.67) * mm, "end": v(-12.89, -0.69) * mm});
            skLineSegment(sketch, "E1792", {"start": v(-12.89, -0.69) * mm, "end": v(-13.03, -0.73) * mm});
            skLineSegment(sketch, "E1793", {"start": v(-13.03, -0.73) * mm, "end": v(-13.16, -0.8) * mm});
            skLineSegment(sketch, "E1794", {"start": v(-13.16, -0.8) * mm, "end": v(-13.27, -0.9) * mm});
            skLineSegment(sketch, "E1795", {"start": v(-13.27, -0.9) * mm, "end": v(-13.36, -1) * mm});
            skLineSegment(sketch, "E1796", {"start": v(-13.36, -1) * mm, "end": v(-13.43, -1.13) * mm});
            skLineSegment(sketch, "E1797", {"start": v(-13.43, -1.13) * mm, "end": v(-13.47, -1.27) * mm});
            skLineSegment(sketch, "E1798", {"start": v(-13.47, -1.27) * mm, "end": v(-13.49, -1.42) * mm});
            skLineSegment(sketch, "E1799", {"start": v(-13.49, -1.42) * mm, "end": v(-13.47, -1.56) * mm});
            skLineSegment(sketch, "E1800", {"start": v(-13.47, -1.56) * mm, "end": v(-13.43, -1.7) * mm});
            skLineSegment(sketch, "E1801", {"start": v(-13.43, -1.7) * mm, "end": v(-13.36, -1.83) * mm});
            skLineSegment(sketch, "E1802", {"start": v(-13.36, -1.83) * mm, "end": v(-13.27, -1.94) * mm});
            skLineSegment(sketch, "E1803", {"start": v(-13.27, -1.94) * mm, "end": v(-13.16, -2.03) * mm});
            skLineSegment(sketch, "E1804", {"start": v(-13.16, -2.03) * mm, "end": v(-13.03, -2.1) * mm});
            skLineSegment(sketch, "E1805", {"start": v(-13.03, -2.1) * mm, "end": v(-12.89, -2.14) * mm});
            skLineSegment(sketch, "E1806", {"start": v(-12.89, -2.14) * mm, "end": v(-12.74, -2.16) * mm});
            skLineSegment(sketch, "E1807", {"start": v(-12.74, -2.16) * mm, "end": v(-12.6, -2.14) * mm});
            skLineSegment(sketch, "E1808", {"start": v(-12.6, -2.14) * mm, "end": v(-12.46, -2.1) * mm});
            skLineSegment(sketch, "E1809", {"start": v(-12.46, -2.1) * mm, "end": v(-12.33, -2.03) * mm});
            skLineSegment(sketch, "E1810", {"start": v(-12.33, -2.03) * mm, "end": v(-12.22, -1.94) * mm});
            skLineSegment(sketch, "E1811", {"start": v(-12.22, -1.94) * mm, "end": v(-12.12, -1.83) * mm});
            skLineSegment(sketch, "E1812", {"start": v(-12.12, -1.83) * mm, "end": v(-12.06, -1.7) * mm});
            skLineSegment(sketch, "E1813", {"start": v(-12.06, -1.7) * mm, "end": v(-12.04, -1.64) * mm});
            skLineSegment(sketch, "E1814", {"start": v(-12.04, -1.64) * mm, "end": v(-11.8, -1.64) * mm});
            skLineSegment(sketch, "E1815", {"start": v(-11.8, -1.64) * mm, "end": v(-11.76, -1.63) * mm});
            skLineSegment(sketch, "E1816", {"start": v(-11.76, -1.63) * mm, "end": v(-11.71, -1.62) * mm});
            skLineSegment(sketch, "E1817", {"start": v(-11.71, -1.62) * mm, "end": v(-11.67, -1.6) * mm});
            skLineSegment(sketch, "E1818", {"start": v(-11.67, -1.6) * mm, "end": v(-11.64, -1.57) * mm});
            skLineSegment(sketch, "E1819", {"start": v(-11.64, -1.57) * mm, "end": v(-9.82, 0.25) * mm});
            skLineSegment(sketch, "E1820", {"start": v(-9.82, 0.25) * mm, "end": v(-8.06, 0.25) * mm});
            skLineSegment(sketch, "E1821", {"start": v(-8.06, 0.25) * mm, "end": v(-8.06, 0.12) * mm});
            skLineSegment(sketch, "E1822", {"start": v(-8.06, 0.12) * mm, "end": v(-8.06, 0.08) * mm});
            skLineSegment(sketch, "E1823", {"start": v(-8.06, 0.08) * mm, "end": v(-8.05, 0.08) * mm});
            skLineSegment(sketch, "E1824", {"start": v(-8.05, 0.08) * mm, "end": v(-8.05, 0.05) * mm});
            skLineSegment(sketch, "E1825", {"start": v(-8.05, 0.05) * mm, "end": v(-8.03, -0.03) * mm});
            skLineSegment(sketch, "E1826", {"start": v(-8.03, -0.03) * mm, "end": v(-8, -0.1) * mm});
            skLineSegment(sketch, "E1827", {"start": v(-8, -0.1) * mm, "end": v(-7.94, -0.16) * mm});
            skLineSegment(sketch, "E1828", {"start": v(-7.94, -0.16) * mm, "end": v(-7.88, -0.2) * mm});
            skLineSegment(sketch, "E1829", {"start": v(-7.88, -0.2) * mm, "end": v(-7.81, -0.24) * mm});
            skLineSegment(sketch, "E1830", {"start": v(-7.81, -0.24) * mm, "end": v(-7.74, -0.26) * mm});
            skLineSegment(sketch, "E1831", {"start": v(-7.74, -0.26) * mm, "end": v(-7.71, -0.27) * mm});
            skLineSegment(sketch, "E1832", {"start": v(-7.71, -0.27) * mm, "end": v(-7.71, -0.27) * mm});
            skLineSegment(sketch, "E1833", {"start": v(-7.71, -0.27) * mm, "end": v(-7.66, -0.27) * mm});
            skLineSegment(sketch, "E1834", {"start": v(-7.66, -0.27) * mm, "end": v(-6.97, -0.27) * mm});
            skLineSegment(sketch, "E1835", {"start": v(-6.97, -0.27) * mm, "end": v(-6.92, -0.27) * mm});
            skLineSegment(sketch, "E1836", {"start": v(-6.92, -0.27) * mm, "end": v(-6.92, -0.27) * mm});
            skLineSegment(sketch, "E1837", {"start": v(-6.92, -0.27) * mm, "end": v(-6.89, -0.26) * mm});
            skLineSegment(sketch, "E1838", {"start": v(-6.89, -0.26) * mm, "end": v(-6.82, -0.24) * mm});
            skLineSegment(sketch, "E1839", {"start": v(-6.82, -0.24) * mm, "end": v(-6.75, -0.2) * mm});
            skLineSegment(sketch, "E1840", {"start": v(-6.75, -0.2) * mm, "end": v(-6.69, -0.16) * mm});
            skLineSegment(sketch, "E1841", {"start": v(-6.69, -0.16) * mm, "end": v(-6.64, -0.1) * mm});
            skLineSegment(sketch, "E1842", {"start": v(-6.64, -0.1) * mm, "end": v(-6.6, -0.03) * mm});
            skLineSegment(sketch, "E1843", {"start": v(-6.6, -0.03) * mm, "end": v(-6.58, 0.05) * mm});
            skLineSegment(sketch, "E1844", {"start": v(-6.58, 0.05) * mm, "end": v(-6.58, 0.08) * mm});
            skLineSegment(sketch, "E1845", {"start": v(-6.58, 0.08) * mm, "end": v(-6.57, 0.08) * mm});
            skLineSegment(sketch, "E1846", {"start": v(-6.57, 0.08) * mm, "end": v(-6.57, 0.12) * mm});
            skLineSegment(sketch, "E1847", {"start": v(-6.57, 0.12) * mm, "end": v(-6.57, 0.25) * mm});
            skLineSegment(sketch, "E1848", {"start": v(-6.57, 0.25) * mm, "end": v(-5.05, 0.25) * mm});
            skLineSegment(sketch, "E1849", {"start": v(-5.05, 0.25) * mm, "end": v(-4.9, 0.1) * mm});
            skLineSegment(sketch, "E1850", {"start": v(-4.9, 0.1) * mm, "end": v(-4.93, 0.05) * mm});
            skLineSegment(sketch, "E1851", {"start": v(-4.93, 0.05) * mm, "end": v(-4.98, -0.1) * mm});
            skLineSegment(sketch, "E1852", {"start": v(-4.98, -0.1) * mm, "end": v(-5, -0.24) * mm});
            skLineSegment(sketch, "E1853", {"start": v(-5, -0.24) * mm, "end": v(-4.98, -0.38) * mm});
            skLineSegment(sketch, "E1854", {"start": v(-4.98, -0.38) * mm, "end": v(-4.93, -0.52) * mm});
            skLineSegment(sketch, "E1855", {"start": v(-4.93, -0.52) * mm, "end": v(-4.87, -0.65) * mm});
            skLineSegment(sketch, "E1856", {"start": v(-4.87, -0.65) * mm, "end": v(-4.77, -0.76) * mm});
            skLineSegment(sketch, "E1857", {"start": v(-4.77, -0.76) * mm, "end": v(-4.66, -0.85) * mm});
            skLineSegment(sketch, "E1858", {"start": v(-4.66, -0.85) * mm, "end": v(-4.53, -0.92) * mm});
            skLineSegment(sketch, "E1859", {"start": v(-4.53, -0.92) * mm, "end": v(-4.4, -0.96) * mm});
            skLineSegment(sketch, "E1860", {"start": v(-4.4, -0.96) * mm, "end": v(-4.25, -0.98) * mm});
            skLineSegment(sketch, "E1861", {"start": v(-4.25, -0.98) * mm, "end": v(-4.1, -0.96) * mm});
            skLineSegment(sketch, "E1862", {"start": v(-4.1, -0.96) * mm, "end": v(-3.96, -0.92) * mm});
            skLineSegment(sketch, "E1863", {"start": v(-3.96, -0.92) * mm, "end": v(-3.83, -0.85) * mm});
            skLineSegment(sketch, "E1864", {"start": v(-3.83, -0.85) * mm, "end": v(-3.72, -0.76) * mm});
            skLineSegment(sketch, "E1865", {"start": v(-3.72, -0.76) * mm, "end": v(-3.63, -0.65) * mm});
            skLineSegment(sketch, "E1866", {"start": v(-7.54, -5.87) * mm, "end": v(-7.61, -5.9) * mm});
            skLineSegment(sketch, "E1867", {"start": v(-7.61, -5.9) * mm, "end": v(-7.75, -5.96) * mm});
            skLineSegment(sketch, "E1868", {"start": v(-7.75, -5.96) * mm, "end": v(-7.86, -6.06) * mm});
            skLineSegment(sketch, "E1869", {"start": v(-7.86, -6.06) * mm, "end": v(-7.96, -6.18) * mm});
            skLineSegment(sketch, "E1870", {"start": v(-7.96, -6.18) * mm, "end": v(-8.03, -6.31) * mm});
            skLineSegment(sketch, "E1871", {"start": v(-8.03, -6.31) * mm, "end": v(-8.07, -6.46) * mm});
            skLineSegment(sketch, "E1872", {"start": v(-8.07, -6.46) * mm, "end": v(-8.09, -6.6) * mm});
            skLineSegment(sketch, "E1873", {"start": v(-8.09, -6.6) * mm, "end": v(-8.07, -6.76) * mm});
            skLineSegment(sketch, "E1874", {"start": v(-8.07, -6.76) * mm, "end": v(-8.03, -6.9) * mm});
            skLineSegment(sketch, "E1875", {"start": v(-8.03, -6.9) * mm, "end": v(-7.96, -7.04) * mm});
            skLineSegment(sketch, "E1876", {"start": v(-7.96, -7.04) * mm, "end": v(-7.86, -7.15) * mm});
            skLineSegment(sketch, "E1877", {"start": v(-7.86, -7.15) * mm, "end": v(-7.75, -7.25) * mm});
            skLineSegment(sketch, "E1878", {"start": v(-7.75, -7.25) * mm, "end": v(-7.61, -7.32) * mm});
            skLineSegment(sketch, "E1879", {"start": v(-7.61, -7.32) * mm, "end": v(-7.47, -7.37) * mm});
            skLineSegment(sketch, "E1880", {"start": v(-7.47, -7.37) * mm, "end": v(-7.32, -7.38) * mm});
            skLineSegment(sketch, "E1881", {"start": v(-7.32, -7.38) * mm, "end": v(-7.16, -7.37) * mm});
            skLineSegment(sketch, "E1882", {"start": v(-7.16, -7.37) * mm, "end": v(-7.02, -7.32) * mm});
            skLineSegment(sketch, "E1883", {"start": v(-7.02, -7.32) * mm, "end": v(-6.89, -7.25) * mm});
            skLineSegment(sketch, "E1884", {"start": v(-6.89, -7.25) * mm, "end": v(-6.77, -7.15) * mm});
            skLineSegment(sketch, "E1885", {"start": v(-6.77, -7.15) * mm, "end": v(-6.67, -7.04) * mm});
            skLineSegment(sketch, "E1886", {"start": v(-6.67, -7.04) * mm, "end": v(-6.6, -6.9) * mm});
            skLineSegment(sketch, "E1887", {"start": v(-6.6, -6.9) * mm, "end": v(-6.56, -6.76) * mm});
            skLineSegment(sketch, "E1888", {"start": v(-6.56, -6.76) * mm, "end": v(-6.54, -6.6) * mm});
            skLineSegment(sketch, "E1889", {"start": v(-6.54, -6.6) * mm, "end": v(-6.56, -6.46) * mm});
            skLineSegment(sketch, "E1890", {"start": v(-6.56, -6.46) * mm, "end": v(-6.6, -6.31) * mm});
            skLineSegment(sketch, "E1891", {"start": v(-6.6, -6.31) * mm, "end": v(-6.67, -6.18) * mm});
            skLineSegment(sketch, "E1892", {"start": v(-6.67, -6.18) * mm, "end": v(-6.77, -6.06) * mm});
            skLineSegment(sketch, "E1893", {"start": v(-6.77, -6.06) * mm, "end": v(-6.89, -5.96) * mm});
            skLineSegment(sketch, "E1894", {"start": v(-6.89, -5.96) * mm, "end": v(-7.02, -5.9) * mm});
            skLineSegment(sketch, "E1895", {"start": v(-7.02, -5.9) * mm, "end": v(-7.1, -5.87) * mm});
            skLineSegment(sketch, "E1896", {"start": v(-3.47, 2.64) * mm, "end": v(-3.47, 2.72) * mm});
            skLineSegment(sketch, "E1897", {"start": v(-3.47, 2.72) * mm, "end": v(-3.48, 2.64) * mm});
            skLineSegment(sketch, "E1898", {"start": v(-3.48, 2.64) * mm, "end": v(-3.47, 2.64) * mm});
            skLineSegment(sketch, "E1899", {"start": v(-3.47, 2.72) * mm, "end": v(-3.47, 3.42) * mm});
            skLineSegment(sketch, "E1900", {"start": v(-3.47, 3.42) * mm, "end": v(-3.47, 3.5) * mm});
            skLineSegment(sketch, "E1901", {"start": v(-3.47, 3.5) * mm, "end": v(-3.48, 3.5) * mm});
            skLineSegment(sketch, "E1902", {"start": v(-3.48, 3.5) * mm, "end": v(-3.47, 3.42) * mm});
            skLineSegment(sketch, "E1903", {"start": v(3, 10.8) * mm, "end": v(3.13, 10.85) * mm});
            skLineSegment(sketch, "E1904", {"start": v(3.13, 10.85) * mm, "end": v(3.26, 10.92) * mm});
            skLineSegment(sketch, "E1905", {"start": v(3.26, 10.92) * mm, "end": v(3.38, 11.02) * mm});
            skLineSegment(sketch, "E1906", {"start": v(3.38, 11.02) * mm, "end": v(3.48, 11.13) * mm});
            skLineSegment(sketch, "E1907", {"start": v(3.48, 11.13) * mm, "end": v(3.55, 11.27) * mm});
            skLineSegment(sketch, "E1908", {"start": v(3.55, 11.27) * mm, "end": v(3.6, 11.41) * mm});
            skLineSegment(sketch, "E1909", {"start": v(3.6, 11.41) * mm, "end": v(3.6, 11.56) * mm});
            skLineSegment(sketch, "E1910", {"start": v(3.6, 11.56) * mm, "end": v(3.6, 11.71) * mm});
            skLineSegment(sketch, "E1911", {"start": v(3.6, 11.71) * mm, "end": v(3.55, 11.86) * mm});
            skLineSegment(sketch, "E1912", {"start": v(3.55, 11.86) * mm, "end": v(3.48, 12) * mm});
            skLineSegment(sketch, "E1913", {"start": v(3.48, 12) * mm, "end": v(3.38, 12.11) * mm});
            skLineSegment(sketch, "E1914", {"start": v(3.38, 12.11) * mm, "end": v(3.26, 12.2) * mm});
            skLineSegment(sketch, "E1915", {"start": v(3.26, 12.2) * mm, "end": v(3.13, 12.28) * mm});
            skLineSegment(sketch, "E1916", {"start": v(3.13, 12.28) * mm, "end": v(2.98, 12.32) * mm});
            skLineSegment(sketch, "E1917", {"start": v(2.98, 12.32) * mm, "end": v(2.83, 12.34) * mm});
            skLineSegment(sketch, "E1918", {"start": v(2.83, 12.34) * mm, "end": v(2.68, 12.32) * mm});
            skLineSegment(sketch, "E1919", {"start": v(2.68, 12.32) * mm, "end": v(2.54, 12.28) * mm});
            skLineSegment(sketch, "E1920", {"start": v(2.54, 12.28) * mm, "end": v(2.4, 12.2) * mm});
            skLineSegment(sketch, "E1921", {"start": v(2.4, 12.2) * mm, "end": v(2.28, 12.11) * mm});
            skLineSegment(sketch, "E1922", {"start": v(2.28, 12.11) * mm, "end": v(2.19, 12) * mm});
            skLineSegment(sketch, "E1923", {"start": v(2.19, 12) * mm, "end": v(2.12, 11.86) * mm});
            skLineSegment(sketch, "E1924", {"start": v(2.12, 11.86) * mm, "end": v(2.07, 11.71) * mm});
            skLineSegment(sketch, "E1925", {"start": v(2.07, 11.71) * mm, "end": v(2.06, 11.56) * mm});
            skLineSegment(sketch, "E1926", {"start": v(2.06, 11.56) * mm, "end": v(2.07, 11.41) * mm});
            skLineSegment(sketch, "E1927", {"start": v(2.07, 11.41) * mm, "end": v(2.12, 11.27) * mm});
            skLineSegment(sketch, "E1928", {"start": v(2.12, 11.27) * mm, "end": v(2.19, 11.13) * mm});
            skLineSegment(sketch, "E1929", {"start": v(2.19, 11.13) * mm, "end": v(2.28, 11.02) * mm});
            skLineSegment(sketch, "E1930", {"start": v(2.28, 11.02) * mm, "end": v(2.4, 10.92) * mm});
            skLineSegment(sketch, "E1931", {"start": v(2.4, 10.92) * mm, "end": v(2.54, 10.85) * mm});
            skLineSegment(sketch, "E1932", {"start": v(2.54, 10.85) * mm, "end": v(2.67, 10.8) * mm});
            skLineSegment(sketch, "E1933", {"start": v(-9.49, -10.45) * mm, "end": v(-9.49, -10.44) * mm});
            skLineSegment(sketch, "E1934", {"start": v(-9.49, -10.44) * mm, "end": v(-9.57, -10.45) * mm});
            skLineSegment(sketch, "E1935", {"start": v(-9.57, -10.45) * mm, "end": v(-9.49, -10.45) * mm});
            skLineSegment(sketch, "E1936", {"start": v(-5.01, 2.64) * mm, "end": v(-5.02, 2.72) * mm});
            skLineSegment(sketch, "E1937", {"start": v(-5.02, 2.72) * mm, "end": v(-5.02, 2.64) * mm});
            skLineSegment(sketch, "E1938", {"start": v(-5.02, 2.64) * mm, "end": v(-5.01, 2.64) * mm});
            skLineSegment(sketch, "E1939", {"start": v(-9.49, -8.9) * mm, "end": v(-9.49, -8.9) * mm});
            skLineSegment(sketch, "E1940", {"start": v(-9.49, -8.9) * mm, "end": v(-9.56, -8.9) * mm});
            skLineSegment(sketch, "E1941", {"start": v(-9.56, -8.9) * mm, "end": v(-9.49, -8.9) * mm});
            skLineSegment(sketch, "E1942", {"start": v(-9.56, -8.9) * mm, "end": v(-9.69, -8.9) * mm});
            skLineSegment(sketch, "E1943", {"start": v(-6.89, -0.3) * mm, "end": v(-6.89, -0.3) * mm});
            skLineSegment(sketch, "E1944", {"start": v(-6.89, -0.3) * mm, "end": v(-6.97, -0.3) * mm});
            skLineSegment(sketch, "E1945", {"start": v(-6.97, -0.3) * mm, "end": v(-6.89, -0.3) * mm});
            skLineSegment(sketch, "E1946", {"start": v(-5.02, 3.42) * mm, "end": v(-5.01, 3.5) * mm});
            skLineSegment(sketch, "E1947", {"start": v(-5.01, 3.5) * mm, "end": v(-5.02, 3.5) * mm});
            skLineSegment(sketch, "E1948", {"start": v(-5.02, 3.5) * mm, "end": v(-5.02, 3.42) * mm});
            skLineSegment(sketch, "E1949", {"start": v(-5.02, 3.42) * mm, "end": v(-5.02, 2.72) * mm});
            skLineSegment(sketch, "E1950", {"start": v(-3.51, 6.12) * mm, "end": v(-3.53, 6.2) * mm});
            skLineSegment(sketch, "E1951", {"start": v(-3.53, 6.2) * mm, "end": v(-3.6, 6.33) * mm});
            skLineSegment(sketch, "E1952", {"start": v(-3.6, 6.33) * mm, "end": v(-3.7, 6.45) * mm});
            skLineSegment(sketch, "E1953", {"start": v(-3.7, 6.45) * mm, "end": v(-3.82, 6.54) * mm});
            skLineSegment(sketch, "E1954", {"start": v(-3.82, 6.54) * mm, "end": v(-3.95, 6.62) * mm});
            skLineSegment(sketch, "E1955", {"start": v(-3.95, 6.62) * mm, "end": v(-4.1, 6.66) * mm});
            skLineSegment(sketch, "E1956", {"start": v(-4.1, 6.66) * mm, "end": v(-4.25, 6.67) * mm});
            skLineSegment(sketch, "E1957", {"start": v(-4.25, 6.67) * mm, "end": v(-4.4, 6.66) * mm});
            skLineSegment(sketch, "E1958", {"start": v(-4.4, 6.66) * mm, "end": v(-4.54, 6.62) * mm});
            skLineSegment(sketch, "E1959", {"start": v(-4.54, 6.62) * mm, "end": v(-4.68, 6.54) * mm});
            skLineSegment(sketch, "E1960", {"start": v(-4.68, 6.54) * mm, "end": v(-4.8, 6.45) * mm});
            skLineSegment(sketch, "E1961", {"start": v(-4.8, 6.45) * mm, "end": v(-4.9, 6.33) * mm});
            skLineSegment(sketch, "E1962", {"start": v(-4.9, 6.33) * mm, "end": v(-4.96, 6.2) * mm});
            skLineSegment(sketch, "E1963", {"start": v(-4.96, 6.2) * mm, "end": v(-5, 6.05) * mm});
            skLineSegment(sketch, "E1964", {"start": v(-5, 6.05) * mm, "end": v(-5.02, 5.9) * mm});
            skLineSegment(sketch, "E1965", {"start": v(-5.02, 5.9) * mm, "end": v(-5, 5.75) * mm});
            skLineSegment(sketch, "E1966", {"start": v(-5, 5.75) * mm, "end": v(-4.96, 5.6) * mm});
            skLineSegment(sketch, "E1967", {"start": v(-4.96, 5.6) * mm, "end": v(-4.9, 5.47) * mm});
            skLineSegment(sketch, "E1968", {"start": v(-4.9, 5.47) * mm, "end": v(-4.8, 5.35) * mm});
            skLineSegment(sketch, "E1969", {"start": v(-4.8, 5.35) * mm, "end": v(-4.68, 5.26) * mm});
            skLineSegment(sketch, "E1970", {"start": v(-4.68, 5.26) * mm, "end": v(-4.54, 5.18) * mm});
            skLineSegment(sketch, "E1971", {"start": v(-4.54, 5.18) * mm, "end": v(-4.4, 5.14) * mm});
            skLineSegment(sketch, "E1972", {"start": v(-4.4, 5.14) * mm, "end": v(-4.25, 5.13) * mm});
            skLineSegment(sketch, "E1973", {"start": v(-4.25, 5.13) * mm, "end": v(-4.1, 5.14) * mm});
            skLineSegment(sketch, "E1974", {"start": v(-4.1, 5.14) * mm, "end": v(-3.95, 5.18) * mm});
            skLineSegment(sketch, "E1975", {"start": v(-3.95, 5.18) * mm, "end": v(-3.82, 5.26) * mm});
            skLineSegment(sketch, "E1976", {"start": v(-3.82, 5.26) * mm, "end": v(-3.7, 5.35) * mm});
            skLineSegment(sketch, "E1977", {"start": v(-3.7, 5.35) * mm, "end": v(-3.6, 5.47) * mm});
            skLineSegment(sketch, "E1978", {"start": v(-3.6, 5.47) * mm, "end": v(-3.53, 5.6) * mm});
            skLineSegment(sketch, "E1979", {"start": v(-3.53, 5.6) * mm, "end": v(-3.51, 5.68) * mm});
            skLineSegment(sketch, "E1980", {"start": v(-10.26, -10.45) * mm, "end": v(-10.34, -10.44) * mm});
            skLineSegment(sketch, "E1981", {"start": v(-10.34, -10.44) * mm, "end": v(-10.34, -10.45) * mm});
            skLineSegment(sketch, "E1982", {"start": v(-10.34, -10.45) * mm, "end": v(-10.26, -10.45) * mm});
            skLineSegment(sketch, "E1983", {"start": v(-10.26, -10.45) * mm, "end": v(-9.57, -10.45) * mm});
            skLineSegment(sketch, "E1984", {"start": v(-10.13, -8.9) * mm, "end": v(-10.26, -8.9) * mm});
            skLineSegment(sketch, "E1985", {"start": v(-10.26, -8.9) * mm, "end": v(-10.34, -8.9) * mm});
            skLineSegment(sketch, "E1986", {"start": v(-10.34, -8.9) * mm, "end": v(-10.34, -8.9) * mm});
            skLineSegment(sketch, "E1987", {"start": v(-10.34, -8.9) * mm, "end": v(-10.26, -8.9) * mm});
            skLineSegment(sketch, "E1988", {"start": v(-7.67, -0.3) * mm, "end": v(-7.74, -0.3) * mm});
            skLineSegment(sketch, "E1989", {"start": v(-7.74, -0.3) * mm, "end": v(-7.74, -0.3) * mm});
            skLineSegment(sketch, "E1990", {"start": v(-7.74, -0.3) * mm, "end": v(-7.67, -0.3) * mm});
            skLineSegment(sketch, "E1991", {"start": v(-7.67, -0.3) * mm, "end": v(-6.97, -0.3) * mm});
            skLineSegment(sketch, "E1992", {"start": v(-6.89, 1.24) * mm, "end": v(-6.89, 1.25) * mm});
            skLineSegment(sketch, "E1993", {"start": v(-6.89, 1.25) * mm, "end": v(-6.96, 1.25) * mm});
            skLineSegment(sketch, "E1994", {"start": v(-6.96, 1.25) * mm, "end": v(-6.89, 1.24) * mm});
            skLineSegment(sketch, "E1995", {"start": v(-6.96, 1.25) * mm, "end": v(-7.66, 1.25) * mm});
            skLineSegment(sketch, "E1996", {"start": v(-9.23, -2.96) * mm, "end": v(-9.2, -2.9) * mm});
            skLineSegment(sketch, "E1997", {"start": v(-9.2, -2.9) * mm, "end": v(-9.15, -2.75) * mm});
            skLineSegment(sketch, "E1998", {"start": v(-9.15, -2.75) * mm, "end": v(-9.14, -2.6) * mm});
            skLineSegment(sketch, "E1999", {"start": v(-9.14, -2.6) * mm, "end": v(-9.15, -2.44) * mm});
            skLineSegment(sketch, "E2000", {"start": v(-9.15, -2.44) * mm, "end": v(-9.2, -2.3) * mm});
            skLineSegment(sketch, "E2001", {"start": v(-9.2, -2.3) * mm, "end": v(-9.27, -2.17) * mm});
            skLineSegment(sketch, "E2002", {"start": v(-9.27, -2.17) * mm, "end": v(-9.36, -2.05) * mm});
            skLineSegment(sketch, "E2003", {"start": v(-9.36, -2.05) * mm, "end": v(-9.48, -1.95) * mm});
            skLineSegment(sketch, "E2004", {"start": v(-9.48, -1.95) * mm, "end": v(-9.61, -1.88) * mm});
            skLineSegment(sketch, "E2005", {"start": v(-9.61, -1.88) * mm, "end": v(-9.76, -1.84) * mm});
            skLineSegment(sketch, "E2006", {"start": v(-9.76, -1.84) * mm, "end": v(-9.91, -1.82) * mm});
            skLineSegment(sketch, "E2007", {"start": v(-9.91, -1.82) * mm, "end": v(-10.06, -1.84) * mm});
            skLineSegment(sketch, "E2008", {"start": v(-10.06, -1.84) * mm, "end": v(-10.2, -1.88) * mm});
            skLineSegment(sketch, "E2009", {"start": v(-10.2, -1.88) * mm, "end": v(-10.34, -1.95) * mm});
            skLineSegment(sketch, "E2010", {"start": v(-10.34, -1.95) * mm, "end": v(-10.46, -2.05) * mm});
            skLineSegment(sketch, "E2011", {"start": v(-10.46, -2.05) * mm, "end": v(-10.56, -2.17) * mm});
            skLineSegment(sketch, "E2012", {"start": v(-10.56, -2.17) * mm, "end": v(-10.63, -2.3) * mm});
            skLineSegment(sketch, "E2013", {"start": v(-10.63, -2.3) * mm, "end": v(-10.65, -2.37) * mm});
            skLineSegment(sketch, "E2014", {"start": v(-6.4, 2.97) * mm, "end": v(-6.37, 3.04) * mm});
            skLineSegment(sketch, "E2015", {"start": v(-6.37, 3.04) * mm, "end": v(-6.34, 3.11) * mm});
            skLineSegment(sketch, "E2016", {"start": v(-6.34, 3.11) * mm, "end": v(-6.34, 3.15) * mm});
            skLineSegment(sketch, "E2017", {"start": v(-6.34, 3.15) * mm, "end": v(-6.34, 3.15) * mm});
            skLineSegment(sketch, "E2018", {"start": v(-6.34, 3.15) * mm, "end": v(-6.34, 3.2) * mm});
            skLineSegment(sketch, "E2019", {"start": v(-6.34, 3.2) * mm, "end": v(-6.34, 3.89) * mm});
            skLineSegment(sketch, "E2020", {"start": v(-6.34, 3.89) * mm, "end": v(-6.34, 3.93) * mm});
            skLineSegment(sketch, "E2021", {"start": v(-6.34, 3.93) * mm, "end": v(-6.34, 3.93) * mm});
            skLineSegment(sketch, "E2022", {"start": v(-6.34, 3.93) * mm, "end": v(-6.34, 3.97) * mm});
            skLineSegment(sketch, "E2023", {"start": v(-6.34, 3.97) * mm, "end": v(-6.37, 4.04) * mm});
            skLineSegment(sketch, "E2024", {"start": v(-6.37, 4.04) * mm, "end": v(-6.4, 4.1) * mm});
            skLineSegment(sketch, "E2025", {"start": v(-6.4, 4.1) * mm, "end": v(-6.45, 4.17) * mm});
            skLineSegment(sketch, "E2026", {"start": v(-6.45, 4.17) * mm, "end": v(-6.51, 4.22) * mm});
            skLineSegment(sketch, "E2027", {"start": v(-6.51, 4.22) * mm, "end": v(-6.58, 4.25) * mm});
            skLineSegment(sketch, "E2028", {"start": v(-6.58, 4.25) * mm, "end": v(-6.65, 4.28) * mm});
            skLineSegment(sketch, "E2029", {"start": v(-6.65, 4.28) * mm, "end": v(-6.68, 4.28) * mm});
            skLineSegment(sketch, "E2030", {"start": v(-6.68, 4.28) * mm, "end": v(-6.68, 4.28) * mm});
            skLineSegment(sketch, "E2031", {"start": v(-6.68, 4.28) * mm, "end": v(-6.73, 4.28) * mm});
            skLineSegment(sketch, "E2032", {"start": v(-6.73, 4.28) * mm, "end": v(-6.86, 4.28) * mm});
            skLineSegment(sketch, "E2033", {"start": v(-6.86, 4.28) * mm, "end": v(-6.86, 5.34) * mm});
            skLineSegment(sketch, "E2034", {"start": v(-6.86, 5.34) * mm, "end": v(-4.59, 7.6) * mm});
            skLineSegment(sketch, "E2035", {"start": v(-4.59, 7.6) * mm, "end": v(-4.53, 7.57) * mm});
            skLineSegment(sketch, "E2036", {"start": v(-4.53, 7.57) * mm, "end": v(-4.4, 7.53) * mm});
            skLineSegment(sketch, "E2037", {"start": v(-4.4, 7.53) * mm, "end": v(-4.25, 7.52) * mm});
            skLineSegment(sketch, "E2038", {"start": v(-4.25, 7.52) * mm, "end": v(-4.1, 7.53) * mm});
            skLineSegment(sketch, "E2039", {"start": v(-4.1, 7.53) * mm, "end": v(-3.96, 7.57) * mm});
            skLineSegment(sketch, "E2040", {"start": v(-3.96, 7.57) * mm, "end": v(-3.83, 7.64) * mm});
            skLineSegment(sketch, "E2041", {"start": v(-3.83, 7.64) * mm, "end": v(-3.72, 7.73) * mm});
            skLineSegment(sketch, "E2042", {"start": v(-3.72, 7.73) * mm, "end": v(-3.63, 7.85) * mm});
            skLineSegment(sketch, "E2043", {"start": v(-3.63, 7.85) * mm, "end": v(-3.56, 7.97) * mm});
            skLineSegment(sketch, "E2044", {"start": v(-3.56, 7.97) * mm, "end": v(-3.52, 8.11) * mm});
            skLineSegment(sketch, "E2045", {"start": v(-3.52, 8.11) * mm, "end": v(-3.5, 8.26) * mm});
            skLineSegment(sketch, "E2046", {"start": v(-3.5, 8.26) * mm, "end": v(-3.52, 8.4) * mm});
            skLineSegment(sketch, "E2047", {"start": v(-3.52, 8.4) * mm, "end": v(-3.56, 8.54) * mm});
            skLineSegment(sketch, "E2048", {"start": v(-3.56, 8.54) * mm, "end": v(-3.63, 8.67) * mm});
            skLineSegment(sketch, "E2049", {"start": v(-3.63, 8.67) * mm, "end": v(-3.72, 8.78) * mm});
            skLineSegment(sketch, "E2050", {"start": v(-3.72, 8.78) * mm, "end": v(-3.83, 8.88) * mm});
            skLineSegment(sketch, "E2051", {"start": v(-3.83, 8.88) * mm, "end": v(-3.96, 8.95) * mm});
            skLineSegment(sketch, "E2052", {"start": v(-3.96, 8.95) * mm, "end": v(-4.1, 8.99) * mm});
            skLineSegment(sketch, "E2053", {"start": v(-4.1, 8.99) * mm, "end": v(-4.25, 9) * mm});
            skLineSegment(sketch, "E2054", {"start": v(-4.25, 9) * mm, "end": v(-4.4, 8.99) * mm});
            skLineSegment(sketch, "E2055", {"start": v(-4.4, 8.99) * mm, "end": v(-4.53, 8.95) * mm});
            skLineSegment(sketch, "E2056", {"start": v(-4.53, 8.95) * mm, "end": v(-4.66, 8.88) * mm});
            skLineSegment(sketch, "E2057", {"start": v(-4.66, 8.88) * mm, "end": v(-4.77, 8.78) * mm});
            skLineSegment(sketch, "E2058", {"start": v(-4.77, 8.78) * mm, "end": v(-4.87, 8.67) * mm});
            skLineSegment(sketch, "E2059", {"start": v(-4.87, 8.67) * mm, "end": v(-4.93, 8.54) * mm});
            skLineSegment(sketch, "E2060", {"start": v(-4.93, 8.54) * mm, "end": v(-4.98, 8.4) * mm});
            skLineSegment(sketch, "E2061", {"start": v(-4.98, 8.4) * mm, "end": v(-5, 8.26) * mm});
            skLineSegment(sketch, "E2062", {"start": v(-5, 8.26) * mm, "end": v(-4.98, 8.11) * mm});
            skLineSegment(sketch, "E2063", {"start": v(-4.98, 8.11) * mm, "end": v(-4.93, 7.97) * mm});
            skLineSegment(sketch, "E2064", {"start": v(-4.93, 7.97) * mm, "end": v(-4.9, 7.92) * mm});
            skLineSegment(sketch, "E2065", {"start": v(-4.9, 7.92) * mm, "end": v(-7.24, 5.59) * mm});
            skLineSegment(sketch, "E2066", {"start": v(-7.24, 5.59) * mm, "end": v(-7.27, 5.55) * mm});
            skLineSegment(sketch, "E2067", {"start": v(-7.27, 5.55) * mm, "end": v(-7.29, 5.51) * mm});
            skLineSegment(sketch, "E2068", {"start": v(-7.29, 5.51) * mm, "end": v(-7.3, 5.47) * mm});
            skLineSegment(sketch, "E2069", {"start": v(-7.3, 5.47) * mm, "end": v(-7.3, 5.43) * mm});
            skLineSegment(sketch, "E2070", {"start": v(-7.3, 5.43) * mm, "end": v(-7.3, 4.28) * mm});
            skLineSegment(sketch, "E2071", {"start": v(-7.3, 4.28) * mm, "end": v(-7.43, 4.28) * mm});
            skLineSegment(sketch, "E2072", {"start": v(-7.43, 4.28) * mm, "end": v(-7.47, 4.28) * mm});
            skLineSegment(sketch, "E2073", {"start": v(-7.47, 4.28) * mm, "end": v(-7.47, 4.28) * mm});
            skLineSegment(sketch, "E2074", {"start": v(-7.47, 4.28) * mm, "end": v(-7.5, 4.28) * mm});
            skLineSegment(sketch, "E2075", {"start": v(-7.5, 4.28) * mm, "end": v(-7.58, 4.25) * mm});
            skLineSegment(sketch, "E2076", {"start": v(-7.58, 4.25) * mm, "end": v(-7.65, 4.22) * mm});
            skLineSegment(sketch, "E2077", {"start": v(-7.65, 4.22) * mm, "end": v(-7.7, 4.17) * mm});
            skLineSegment(sketch, "E2078", {"start": v(-7.7, 4.17) * mm, "end": v(-7.76, 4.1) * mm});
            skLineSegment(sketch, "E2079", {"start": v(-7.76, 4.1) * mm, "end": v(-7.8, 4.04) * mm});
            skLineSegment(sketch, "E2080", {"start": v(-7.8, 4.04) * mm, "end": v(-7.82, 3.97) * mm});
            skLineSegment(sketch, "E2081", {"start": v(-7.82, 3.97) * mm, "end": v(-7.82, 3.93) * mm});
            skLineSegment(sketch, "E2082", {"start": v(-7.82, 3.93) * mm, "end": v(-7.82, 3.93) * mm});
            skLineSegment(sketch, "E2083", {"start": v(-7.82, 3.93) * mm, "end": v(-7.82, 3.89) * mm});
            skLineSegment(sketch, "E2084", {"start": v(-7.82, 3.89) * mm, "end": v(-7.82, 3.76) * mm});
            skLineSegment(sketch, "E2085", {"start": v(-7.82, 3.76) * mm, "end": v(-10.15, 3.76) * mm});
            skLineSegment(sketch, "E2086", {"start": v(-10.15, 3.76) * mm, "end": v(-10.2, 3.76) * mm});
            skLineSegment(sketch, "E2087", {"start": v(-10.2, 3.76) * mm, "end": v(-10.23, 3.75) * mm});
            skLineSegment(sketch, "E2088", {"start": v(-10.23, 3.75) * mm, "end": v(-10.27, 3.73) * mm});
            skLineSegment(sketch, "E2089", {"start": v(-10.27, 3.73) * mm, "end": v(-10.3, 3.7) * mm});
            skLineSegment(sketch, "E2090", {"start": v(-10.3, 3.7) * mm, "end": v(-12.4, 1.6) * mm});
            skLineSegment(sketch, "E2091", {"start": v(-12.4, 1.6) * mm, "end": v(-12.46, 1.63) * mm});
            skLineSegment(sketch, "E2092", {"start": v(-12.46, 1.63) * mm, "end": v(-12.6, 1.67) * mm});
            skLineSegment(sketch, "E2093", {"start": v(-12.6, 1.67) * mm, "end": v(-12.74, 1.69) * mm});
            skLineSegment(sketch, "E2094", {"start": v(-12.74, 1.69) * mm, "end": v(-12.89, 1.67) * mm});
            skLineSegment(sketch, "E2095", {"start": v(-12.89, 1.67) * mm, "end": v(-13.03, 1.63) * mm});
            skLineSegment(sketch, "E2096", {"start": v(-13.03, 1.63) * mm, "end": v(-13.16, 1.56) * mm});
            skLineSegment(sketch, "E2097", {"start": v(-13.16, 1.56) * mm, "end": v(-13.27, 1.47) * mm});
            skLineSegment(sketch, "E2098", {"start": v(-13.27, 1.47) * mm, "end": v(-13.36, 1.36) * mm});
            skLineSegment(sketch, "E2099", {"start": v(-13.36, 1.36) * mm, "end": v(-13.43, 1.23) * mm});
            skLineSegment(sketch, "E2100", {"start": v(-13.43, 1.23) * mm, "end": v(-13.47, 1.09) * mm});
            skLineSegment(sketch, "E2101", {"start": v(-13.47, 1.09) * mm, "end": v(-13.49, 0.94) * mm});
            skLineSegment(sketch, "E2102", {"start": v(-13.49, 0.94) * mm, "end": v(-13.47, 0.8) * mm});
            skLineSegment(sketch, "E2103", {"start": v(-13.47, 0.8) * mm, "end": v(-13.43, 0.66) * mm});
            skLineSegment(sketch, "E2104", {"start": v(-13.43, 0.66) * mm, "end": v(-13.36, 0.53) * mm});
            skLineSegment(sketch, "E2105", {"start": v(-13.36, 0.53) * mm, "end": v(-13.27, 0.42) * mm});
            skLineSegment(sketch, "E2106", {"start": v(-13.27, 0.42) * mm, "end": v(-13.16, 0.33) * mm});
            skLineSegment(sketch, "E2107", {"start": v(-13.16, 0.33) * mm, "end": v(-13.03, 0.26) * mm});
            skLineSegment(sketch, "E2108", {"start": v(-13.03, 0.26) * mm, "end": v(-12.89, 0.21) * mm});
            skLineSegment(sketch, "E2109", {"start": v(-12.89, 0.21) * mm, "end": v(-12.74, 0.2) * mm});
            skLineSegment(sketch, "E2110", {"start": v(-12.74, 0.2) * mm, "end": v(-12.6, 0.21) * mm});
            skLineSegment(sketch, "E2111", {"start": v(-12.6, 0.21) * mm, "end": v(-12.46, 0.26) * mm});
            skLineSegment(sketch, "E2112", {"start": v(-12.46, 0.26) * mm, "end": v(-12.33, 0.33) * mm});
            skLineSegment(sketch, "E2113", {"start": v(-12.33, 0.33) * mm, "end": v(-12.22, 0.42) * mm});
            skLineSegment(sketch, "E2114", {"start": v(-12.22, 0.42) * mm, "end": v(-12.12, 0.53) * mm});
            skLineSegment(sketch, "E2115", {"start": v(-12.12, 0.53) * mm, "end": v(-12.06, 0.66) * mm});
            skLineSegment(sketch, "E2116", {"start": v(-12.06, 0.66) * mm, "end": v(-12.01, 0.8) * mm});
            skLineSegment(sketch, "E2117", {"start": v(-12.01, 0.8) * mm, "end": v(-12, 0.94) * mm});
            skLineSegment(sketch, "E2118", {"start": v(-12, 0.94) * mm, "end": v(-12.01, 1.09) * mm});
            skLineSegment(sketch, "E2119", {"start": v(-12.01, 1.09) * mm, "end": v(-12.06, 1.23) * mm});
            skLineSegment(sketch, "E2120", {"start": v(-12.06, 1.23) * mm, "end": v(-12.09, 1.28) * mm});
            skLineSegment(sketch, "E2121", {"start": v(-12.09, 1.28) * mm, "end": v(-10.05, 3.32) * mm});
            skLineSegment(sketch, "E2122", {"start": v(-10.05, 3.32) * mm, "end": v(-7.82, 3.32) * mm});
            skLineSegment(sketch, "E2123", {"start": v(-7.82, 3.32) * mm, "end": v(-7.82, 3.2) * mm});
            skLineSegment(sketch, "E2124", {"start": v(-7.82, 3.2) * mm, "end": v(-7.82, 3.15) * mm});
            skLineSegment(sketch, "E2125", {"start": v(-7.82, 3.15) * mm, "end": v(-7.82, 3.15) * mm});
            skLineSegment(sketch, "E2126", {"start": v(-7.82, 3.15) * mm, "end": v(-7.82, 3.11) * mm});
            skLineSegment(sketch, "E2127", {"start": v(-7.82, 3.11) * mm, "end": v(-7.8, 3.04) * mm});
            skLineSegment(sketch, "E2128", {"start": v(-7.8, 3.04) * mm, "end": v(-7.76, 2.97) * mm});
            skLineSegment(sketch, "E2129", {"start": v(-7.76, 2.97) * mm, "end": v(-7.7, 2.91) * mm});
            skLineSegment(sketch, "E2130", {"start": v(-7.7, 2.91) * mm, "end": v(-7.65, 2.86) * mm});
            skLineSegment(sketch, "E2131", {"start": v(-7.65, 2.86) * mm, "end": v(-7.58, 2.83) * mm});
            skLineSegment(sketch, "E2132", {"start": v(-7.58, 2.83) * mm, "end": v(-7.5, 2.8) * mm});
            skLineSegment(sketch, "E2133", {"start": v(-7.5, 2.8) * mm, "end": v(-7.47, 2.8) * mm});
            skLineSegment(sketch, "E2134", {"start": v(-7.47, 2.8) * mm, "end": v(-7.47, 2.8) * mm});
            skLineSegment(sketch, "E2135", {"start": v(-7.47, 2.8) * mm, "end": v(-7.43, 2.8) * mm});
            skLineSegment(sketch, "E2136", {"start": v(-7.43, 2.8) * mm, "end": v(-6.73, 2.8) * mm});
            skLineSegment(sketch, "E2137", {"start": v(-6.73, 2.8) * mm, "end": v(-6.68, 2.8) * mm});
            skLineSegment(sketch, "E2138", {"start": v(-6.68, 2.8) * mm, "end": v(-6.68, 2.8) * mm});
            skLineSegment(sketch, "E2139", {"start": v(-6.68, 2.8) * mm, "end": v(-6.65, 2.8) * mm});
            skLineSegment(sketch, "E2140", {"start": v(-6.65, 2.8) * mm, "end": v(-6.58, 2.83) * mm});
            skLineSegment(sketch, "E2141", {"start": v(-6.58, 2.83) * mm, "end": v(-6.51, 2.86) * mm});
            skLineSegment(sketch, "E2142", {"start": v(-6.51, 2.86) * mm, "end": v(-6.45, 2.91) * mm});
            skLineSegment(sketch, "E2143", {"start": v(-6.45, 2.91) * mm, "end": v(-6.4, 2.97) * mm});
            skLineSegment(sketch, "E2144", {"start": v(-6.65, 2.77) * mm, "end": v(-6.65, 2.77) * mm});
            skLineSegment(sketch, "E2145", {"start": v(-6.65, 2.77) * mm, "end": v(-6.73, 2.77) * mm});
            skLineSegment(sketch, "E2146", {"start": v(-6.73, 2.77) * mm, "end": v(-6.65, 2.77) * mm});
            skLineSegment(sketch, "E2147", {"start": v(-10.65, -2.82) * mm, "end": v(-10.63, -2.9) * mm});
            skLineSegment(sketch, "E2148", {"start": v(-10.63, -2.9) * mm, "end": v(-10.56, -3.03) * mm});
            skLineSegment(sketch, "E2149", {"start": v(-10.56, -3.03) * mm, "end": v(-10.46, -3.14) * mm});
            skLineSegment(sketch, "E2150", {"start": v(-10.46, -3.14) * mm, "end": v(-10.34, -3.24) * mm});
            skLineSegment(sketch, "E2151", {"start": v(-10.34, -3.24) * mm, "end": v(-10.2, -3.31) * mm});
            skLineSegment(sketch, "E2152", {"start": v(-10.2, -3.31) * mm, "end": v(-10.06, -3.36) * mm});
            skLineSegment(sketch, "E2153", {"start": v(-10.06, -3.36) * mm, "end": v(-9.91, -3.37) * mm});
            skLineSegment(sketch, "E2154", {"start": v(-9.91, -3.37) * mm, "end": v(-9.76, -3.36) * mm});
            skLineSegment(sketch, "E2155", {"start": v(-9.76, -3.36) * mm, "end": v(-9.61, -3.31) * mm});
            skLineSegment(sketch, "E2156", {"start": v(-9.61, -3.31) * mm, "end": v(-9.55, -3.28) * mm});
            skLineSegment(sketch, "E2157", {"start": v(-7.66, 1.25) * mm, "end": v(-7.74, 1.25) * mm});
            skLineSegment(sketch, "E2158", {"start": v(-7.74, 1.25) * mm, "end": v(-7.74, 1.24) * mm});
            skLineSegment(sketch, "E2159", {"start": v(-7.74, 1.24) * mm, "end": v(-7.66, 1.25) * mm});
            skLineSegment(sketch, "E2160", {"start": v(-4.61, 7.58) * mm, "end": v(-4.54, 7.54) * mm});
            skLineSegment(sketch, "E2161", {"start": v(-4.54, 7.54) * mm, "end": v(-4.4, 7.5) * mm});
            skLineSegment(sketch, "E2162", {"start": v(-4.4, 7.5) * mm, "end": v(-4.25, 7.48) * mm});
            skLineSegment(sketch, "E2163", {"start": v(-4.25, 7.48) * mm, "end": v(-4.1, 7.5) * mm});
            skLineSegment(sketch, "E2164", {"start": v(-4.1, 7.5) * mm, "end": v(-3.95, 7.54) * mm});
            skLineSegment(sketch, "E2165", {"start": v(-3.95, 7.54) * mm, "end": v(-3.82, 7.62) * mm});
            skLineSegment(sketch, "E2166", {"start": v(-3.82, 7.62) * mm, "end": v(-3.7, 7.71) * mm});
            skLineSegment(sketch, "E2167", {"start": v(-3.7, 7.71) * mm, "end": v(-3.6, 7.83) * mm});
            skLineSegment(sketch, "E2168", {"start": v(-3.6, 7.83) * mm, "end": v(-3.53, 7.96) * mm});
            skLineSegment(sketch, "E2169", {"start": v(-3.53, 7.96) * mm, "end": v(-3.49, 8.1) * mm});
            skLineSegment(sketch, "E2170", {"start": v(-3.49, 8.1) * mm, "end": v(-3.47, 8.26) * mm});
            skLineSegment(sketch, "E2171", {"start": v(-3.47, 8.26) * mm, "end": v(-3.49, 8.41) * mm});
            skLineSegment(sketch, "E2172", {"start": v(-3.49, 8.41) * mm, "end": v(-3.53, 8.56) * mm});
            skLineSegment(sketch, "E2173", {"start": v(-3.53, 8.56) * mm, "end": v(-3.6, 8.69) * mm});
            skLineSegment(sketch, "E2174", {"start": v(-3.6, 8.69) * mm, "end": v(-3.7, 8.8) * mm});
            skLineSegment(sketch, "E2175", {"start": v(-3.7, 8.8) * mm, "end": v(-3.82, 8.9) * mm});
            skLineSegment(sketch, "E2176", {"start": v(-3.82, 8.9) * mm, "end": v(-3.95, 8.97) * mm});
            skLineSegment(sketch, "E2177", {"start": v(-3.95, 8.97) * mm, "end": v(-4.1, 9.02) * mm});
            skLineSegment(sketch, "E2178", {"start": v(-4.1, 9.02) * mm, "end": v(-4.25, 9.03) * mm});
            skLineSegment(sketch, "E2179", {"start": v(-4.25, 9.03) * mm, "end": v(-4.4, 9.02) * mm});
            skLineSegment(sketch, "E2180", {"start": v(-4.4, 9.02) * mm, "end": v(-4.54, 8.97) * mm});
            skLineSegment(sketch, "E2181", {"start": v(-4.54, 8.97) * mm, "end": v(-4.68, 8.9) * mm});
            skLineSegment(sketch, "E2182", {"start": v(-4.68, 8.9) * mm, "end": v(-4.8, 8.8) * mm});
            skLineSegment(sketch, "E2183", {"start": v(-4.8, 8.8) * mm, "end": v(-4.9, 8.69) * mm});
            skLineSegment(sketch, "E2184", {"start": v(-4.9, 8.69) * mm, "end": v(-4.96, 8.56) * mm});
            skLineSegment(sketch, "E2185", {"start": v(-4.96, 8.56) * mm, "end": v(-5, 8.41) * mm});
            skLineSegment(sketch, "E2186", {"start": v(-5, 8.41) * mm, "end": v(-5.02, 8.26) * mm});
            skLineSegment(sketch, "E2187", {"start": v(-5.02, 8.26) * mm, "end": v(-5, 8.1) * mm});
            skLineSegment(sketch, "E2188", {"start": v(-5, 8.1) * mm, "end": v(-4.96, 7.96) * mm});
            skLineSegment(sketch, "E2189", {"start": v(-4.96, 7.96) * mm, "end": v(-4.93, 7.9) * mm});
            skLineSegment(sketch, "E2190", {"start": v(-7.43, 2.77) * mm, "end": v(-7.5, 2.77) * mm});
            skLineSegment(sketch, "E2191", {"start": v(-7.5, 2.77) * mm, "end": v(-7.5, 2.77) * mm});
            skLineSegment(sketch, "E2192", {"start": v(-7.5, 2.77) * mm, "end": v(-7.43, 2.77) * mm});
            skLineSegment(sketch, "E2193", {"start": v(-7.43, 2.77) * mm, "end": v(-6.73, 2.77) * mm});
            skLineSegment(sketch, "E2194", {"start": v(-6.65, 4.3) * mm, "end": v(-6.65, 4.31) * mm});
            skLineSegment(sketch, "E2195", {"start": v(-6.65, 4.31) * mm, "end": v(-6.73, 4.31) * mm});
            skLineSegment(sketch, "E2196", {"start": v(-6.73, 4.31) * mm, "end": v(-6.65, 4.3) * mm});
            skLineSegment(sketch, "E2197", {"start": v(-6.73, 4.31) * mm, "end": v(-6.86, 4.31) * mm});
            skLineSegment(sketch, "E2198", {"start": v(-7.3, 4.31) * mm, "end": v(-7.43, 4.31) * mm});
            skLineSegment(sketch, "E2199", {"start": v(-7.43, 4.31) * mm, "end": v(-7.5, 4.31) * mm});
            skLineSegment(sketch, "E2200", {"start": v(-7.5, 4.31) * mm, "end": v(-7.5, 4.3) * mm});
            skLineSegment(sketch, "E2201", {"start": v(-7.5, 4.3) * mm, "end": v(-7.43, 4.31) * mm});
            skLineSegment(sketch, "E2202", {"start": v(-12.32, -4.55) * mm, "end": v(-12.32, -4.54) * mm});
            skLineSegment(sketch, "E2203", {"start": v(-12.32, -4.54) * mm, "end": v(-12.4, -4.55) * mm});
            skLineSegment(sketch, "E2204", {"start": v(-12.4, -4.55) * mm, "end": v(-12.32, -4.55) * mm});
            skLineSegment(sketch, "E2205", {"start": v(-13.59, -11.8) * mm, "end": v(-13.61, -11.5) * mm});
            skLineSegment(sketch, "E2206", {"start": v(-13.61, -11.5) * mm, "end": v(-13.7, -11.22) * mm});
            skLineSegment(sketch, "E2207", {"start": v(-13.7, -11.22) * mm, "end": v(-13.84, -10.96) * mm});
            skLineSegment(sketch, "E2208", {"start": v(-13.84, -10.96) * mm, "end": v(-14.03, -10.73) * mm});
            skLineSegment(sketch, "E2209", {"start": v(-14.03, -10.73) * mm, "end": v(-14.26, -10.54) * mm});
            skLineSegment(sketch, "E2210", {"start": v(-14.26, -10.54) * mm, "end": v(-14.52, -10.4) * mm});
            skLineSegment(sketch, "E2211", {"start": v(-14.52, -10.4) * mm, "end": v(-14.8, -10.31) * mm});
            skLineSegment(sketch, "E2212", {"start": v(-14.8, -10.31) * mm, "end": v(-15.1, -10.28) * mm});
            skLineSegment(sketch, "E2213", {"start": v(-15.1, -10.28) * mm, "end": v(-15.4, -10.31) * mm});
            skLineSegment(sketch, "E2214", {"start": v(-15.4, -10.31) * mm, "end": v(-15.68, -10.4) * mm});
            skLineSegment(sketch, "E2215", {"start": v(-15.68, -10.4) * mm, "end": v(-15.95, -10.54) * mm});
            skLineSegment(sketch, "E2216", {"start": v(-15.95, -10.54) * mm, "end": v(-16.18, -10.73) * mm});
            skLineSegment(sketch, "E2217", {"start": v(-16.18, -10.73) * mm, "end": v(-16.36, -10.96) * mm});
            skLineSegment(sketch, "E2218", {"start": v(-16.36, -10.96) * mm, "end": v(-16.5, -11.22) * mm});
            skLineSegment(sketch, "E2219", {"start": v(-16.5, -11.22) * mm, "end": v(-16.6, -11.5) * mm});
            skLineSegment(sketch, "E2220", {"start": v(-16.6, -11.5) * mm, "end": v(-16.62, -11.8) * mm});
            skLineSegment(sketch, "E2221", {"start": v(-16.62, -11.8) * mm, "end": v(-16.6, -12.1) * mm});
            skLineSegment(sketch, "E2222", {"start": v(-16.6, -12.1) * mm, "end": v(-16.5, -12.38) * mm});
            skLineSegment(sketch, "E2223", {"start": v(-16.5, -12.38) * mm, "end": v(-16.36, -12.64) * mm});
            skLineSegment(sketch, "E2224", {"start": v(-16.36, -12.64) * mm, "end": v(-16.18, -12.87) * mm});
            skLineSegment(sketch, "E2225", {"start": v(-16.18, -12.87) * mm, "end": v(-15.95, -13.06) * mm});
            skLineSegment(sketch, "E2226", {"start": v(-15.95, -13.06) * mm, "end": v(-15.68, -13.2) * mm});
            skLineSegment(sketch, "E2227", {"start": v(-15.68, -13.2) * mm, "end": v(-15.4, -13.29) * mm});
            skLineSegment(sketch, "E2228", {"start": v(-15.4, -13.29) * mm, "end": v(-15.1, -13.32) * mm});
            skLineSegment(sketch, "E2229", {"start": v(-15.1, -13.32) * mm, "end": v(-14.8, -13.29) * mm});
            skLineSegment(sketch, "E2230", {"start": v(-14.8, -13.29) * mm, "end": v(-14.52, -13.2) * mm});
            skLineSegment(sketch, "E2231", {"start": v(-14.52, -13.2) * mm, "end": v(-14.26, -13.06) * mm});
            skLineSegment(sketch, "E2232", {"start": v(-14.26, -13.06) * mm, "end": v(-14.03, -12.87) * mm});
            skLineSegment(sketch, "E2233", {"start": v(-14.03, -12.87) * mm, "end": v(-13.84, -12.64) * mm});
            skLineSegment(sketch, "E2234", {"start": v(-13.84, -12.64) * mm, "end": v(-13.7, -12.38) * mm});
            skLineSegment(sketch, "E2235", {"start": v(-13.7, -12.38) * mm, "end": v(-13.61, -12.1) * mm});
            skLineSegment(sketch, "E2236", {"start": v(-13.61, -12.1) * mm, "end": v(-13.59, -11.8) * mm});
            skLineSegment(sketch, "E2237", {"start": v(-13.62, -11.8) * mm, "end": v(-13.64, -11.5) * mm});
            skLineSegment(sketch, "E2238", {"start": v(-13.64, -11.5) * mm, "end": v(-13.73, -11.23) * mm});
            skLineSegment(sketch, "E2239", {"start": v(-13.73, -11.23) * mm, "end": v(-13.87, -10.97) * mm});
            skLineSegment(sketch, "E2240", {"start": v(-13.87, -10.97) * mm, "end": v(-14.05, -10.75) * mm});
            skLineSegment(sketch, "E2241", {"start": v(-14.05, -10.75) * mm, "end": v(-14.28, -10.56) * mm});
            skLineSegment(sketch, "E2242", {"start": v(-14.28, -10.56) * mm, "end": v(-14.53, -10.43) * mm});
            skLineSegment(sketch, "E2243", {"start": v(-14.53, -10.43) * mm, "end": v(-14.81, -10.34) * mm});
            skLineSegment(sketch, "E2244", {"start": v(-14.81, -10.34) * mm, "end": v(-15.1, -10.31) * mm});
            skLineSegment(sketch, "E2245", {"start": v(-15.1, -10.31) * mm, "end": v(-15.4, -10.34) * mm});
            skLineSegment(sketch, "E2246", {"start": v(-15.4, -10.34) * mm, "end": v(-15.67, -10.43) * mm});
            skLineSegment(sketch, "E2247", {"start": v(-15.67, -10.43) * mm, "end": v(-15.93, -10.56) * mm});
            skLineSegment(sketch, "E2248", {"start": v(-15.93, -10.56) * mm, "end": v(-16.15, -10.75) * mm});
            skLineSegment(sketch, "E2249", {"start": v(-16.15, -10.75) * mm, "end": v(-16.34, -10.97) * mm});
            skLineSegment(sketch, "E2250", {"start": v(-16.34, -10.97) * mm, "end": v(-16.48, -11.23) * mm});
            skLineSegment(sketch, "E2251", {"start": v(-16.48, -11.23) * mm, "end": v(-16.56, -11.5) * mm});
            skLineSegment(sketch, "E2252", {"start": v(-16.56, -11.5) * mm, "end": v(-16.59, -11.8) * mm});
            skLineSegment(sketch, "E2253", {"start": v(-16.59, -11.8) * mm, "end": v(-16.56, -12.09) * mm});
            skLineSegment(sketch, "E2254", {"start": v(-16.56, -12.09) * mm, "end": v(-16.48, -12.37) * mm});
            skLineSegment(sketch, "E2255", {"start": v(-16.48, -12.37) * mm, "end": v(-16.34, -12.62) * mm});
            skLineSegment(sketch, "E2256", {"start": v(-16.34, -12.62) * mm, "end": v(-16.15, -12.85) * mm});
            skLineSegment(sketch, "E2257", {"start": v(-16.15, -12.85) * mm, "end": v(-15.93, -13.03) * mm});
            skLineSegment(sketch, "E2258", {"start": v(-15.93, -13.03) * mm, "end": v(-15.67, -13.17) * mm});
            skLineSegment(sketch, "E2259", {"start": v(-15.67, -13.17) * mm, "end": v(-15.4, -13.26) * mm});
            skLineSegment(sketch, "E2260", {"start": v(-15.4, -13.26) * mm, "end": v(-15.1, -13.29) * mm});
            skLineSegment(sketch, "E2261", {"start": v(-15.1, -13.29) * mm, "end": v(-14.81, -13.26) * mm});
            skLineSegment(sketch, "E2262", {"start": v(-14.81, -13.26) * mm, "end": v(-14.53, -13.17) * mm});
            skLineSegment(sketch, "E2263", {"start": v(-14.53, -13.17) * mm, "end": v(-14.28, -13.03) * mm});
            skLineSegment(sketch, "E2264", {"start": v(-14.28, -13.03) * mm, "end": v(-14.05, -12.85) * mm});
            skLineSegment(sketch, "E2265", {"start": v(-14.05, -12.85) * mm, "end": v(-13.87, -12.62) * mm});
            skLineSegment(sketch, "E2266", {"start": v(-13.87, -12.62) * mm, "end": v(-13.73, -12.37) * mm});
            skLineSegment(sketch, "E2267", {"start": v(-13.73, -12.37) * mm, "end": v(-13.64, -12.09) * mm});
            skLineSegment(sketch, "E2268", {"start": v(-13.64, -12.09) * mm, "end": v(-13.62, -11.8) * mm});
            skLineSegment(sketch, "E2269", {"start": v(-3.47, 11.14) * mm, "end": v(-3.47, 11.22) * mm});
            skLineSegment(sketch, "E2270", {"start": v(-3.47, 11.22) * mm, "end": v(-3.48, 11.14) * mm});
            skLineSegment(sketch, "E2271", {"start": v(-3.48, 11.14) * mm, "end": v(-3.47, 11.14) * mm});
            skLineSegment(sketch, "E2272", {"start": v(-3.47, 11.22) * mm, "end": v(-3.47, 11.91) * mm});
            skLineSegment(sketch, "E2273", {"start": v(-12.32, -3) * mm, "end": v(-12.32, -3) * mm});
            skLineSegment(sketch, "E2274", {"start": v(-12.32, -3) * mm, "end": v(-12.4, -3) * mm});
            skLineSegment(sketch, "E2275", {"start": v(-12.4, -3) * mm, "end": v(-12.32, -3) * mm});
            skLineSegment(sketch, "E2276", {"start": v(-12.4, -3) * mm, "end": v(-13.09, -3) * mm});
            skLineSegment(sketch, "E2277", {"start": v(-12, -1.2) * mm, "end": v(-12.03, -1.12) * mm});
            skLineSegment(sketch, "E2278", {"start": v(-12.03, -1.12) * mm, "end": v(-12.1, -0.99) * mm});
            skLineSegment(sketch, "E2279", {"start": v(-12.1, -0.99) * mm, "end": v(-12.2, -0.87) * mm});
            skLineSegment(sketch, "E2280", {"start": v(-12.2, -0.87) * mm, "end": v(-12.31, -0.77) * mm});
            skLineSegment(sketch, "E2281", {"start": v(-12.31, -0.77) * mm, "end": v(-12.45, -0.7) * mm});
            skLineSegment(sketch, "E2282", {"start": v(-12.45, -0.7) * mm, "end": v(-12.6, -0.66) * mm});
            skLineSegment(sketch, "E2283", {"start": v(-12.6, -0.66) * mm, "end": v(-12.74, -0.64) * mm});
            skLineSegment(sketch, "E2284", {"start": v(-12.74, -0.64) * mm, "end": v(-12.9, -0.66) * mm});
            skLineSegment(sketch, "E2285", {"start": v(-12.9, -0.66) * mm, "end": v(-13.04, -0.7) * mm});
            skLineSegment(sketch, "E2286", {"start": v(-13.04, -0.7) * mm, "end": v(-13.17, -0.77) * mm});
            skLineSegment(sketch, "E2287", {"start": v(-13.17, -0.77) * mm, "end": v(-13.3, -0.87) * mm});
            skLineSegment(sketch, "E2288", {"start": v(-13.3, -0.87) * mm, "end": v(-13.39, -0.99) * mm});
            skLineSegment(sketch, "E2289", {"start": v(-13.39, -0.99) * mm, "end": v(-13.46, -1.12) * mm});
            skLineSegment(sketch, "E2290", {"start": v(-13.46, -1.12) * mm, "end": v(-13.5, -1.26) * mm});
            skLineSegment(sketch, "E2291", {"start": v(-13.5, -1.26) * mm, "end": v(-13.52, -1.42) * mm});
            skLineSegment(sketch, "E2292", {"start": v(-13.52, -1.42) * mm, "end": v(-13.5, -1.57) * mm});
            skLineSegment(sketch, "E2293", {"start": v(-13.5, -1.57) * mm, "end": v(-13.46, -1.71) * mm});
            skLineSegment(sketch, "E2294", {"start": v(-13.46, -1.71) * mm, "end": v(-13.39, -1.85) * mm});
            skLineSegment(sketch, "E2295", {"start": v(-13.39, -1.85) * mm, "end": v(-13.3, -1.96) * mm});
            skLineSegment(sketch, "E2296", {"start": v(-13.3, -1.96) * mm, "end": v(-13.17, -2.06) * mm});
            skLineSegment(sketch, "E2297", {"start": v(-13.17, -2.06) * mm, "end": v(-13.04, -2.13) * mm});
            skLineSegment(sketch, "E2298", {"start": v(-13.04, -2.13) * mm, "end": v(-12.9, -2.18) * mm});
            skLineSegment(sketch, "E2299", {"start": v(-12.9, -2.18) * mm, "end": v(-12.74, -2.2) * mm});
            skLineSegment(sketch, "E2300", {"start": v(-12.74, -2.2) * mm, "end": v(-12.6, -2.18) * mm});
            skLineSegment(sketch, "E2301", {"start": v(-12.6, -2.18) * mm, "end": v(-12.45, -2.13) * mm});
            skLineSegment(sketch, "E2302", {"start": v(-12.45, -2.13) * mm, "end": v(-12.31, -2.06) * mm});
            skLineSegment(sketch, "E2303", {"start": v(-12.31, -2.06) * mm, "end": v(-12.2, -1.96) * mm});
            skLineSegment(sketch, "E2304", {"start": v(-12.2, -1.96) * mm, "end": v(-12.1, -1.85) * mm});
            skLineSegment(sketch, "E2305", {"start": v(-12.1, -1.85) * mm, "end": v(-12.03, -1.71) * mm});
            skLineSegment(sketch, "E2306", {"start": v(-12.03, -1.71) * mm, "end": v(-12, -1.64) * mm});
            skLineSegment(sketch, "E2307", {"start": v(-13.1, -4.55) * mm, "end": v(-13.17, -4.54) * mm});
            skLineSegment(sketch, "E2308", {"start": v(-13.17, -4.54) * mm, "end": v(-13.17, -4.55) * mm});
            skLineSegment(sketch, "E2309", {"start": v(-13.17, -4.55) * mm, "end": v(-13.1, -4.55) * mm});
            skLineSegment(sketch, "E2310", {"start": v(-13.1, -4.55) * mm, "end": v(-12.4, -4.55) * mm});
            skLineSegment(sketch, "E2311", {"start": v(-3.47, 11.91) * mm, "end": v(-3.47, 11.99) * mm});
            skLineSegment(sketch, "E2312", {"start": v(-3.47, 11.99) * mm, "end": v(-3.48, 11.99) * mm});
            skLineSegment(sketch, "E2313", {"start": v(-3.48, 11.99) * mm, "end": v(-3.47, 11.91) * mm});
            skLineSegment(sketch, "E2314", {"start": v(-13.09, -3) * mm, "end": v(-13.17, -3) * mm});
            skLineSegment(sketch, "E2315", {"start": v(-13.17, -3) * mm, "end": v(-13.17, -3) * mm});
            skLineSegment(sketch, "E2316", {"start": v(-13.17, -3) * mm, "end": v(-13.09, -3) * mm});
            skLineSegment(sketch, "E2317", {"start": v(-12.38, 1.62) * mm, "end": v(-12.45, 1.66) * mm});
            skLineSegment(sketch, "E2318", {"start": v(-12.45, 1.66) * mm, "end": v(-12.6, 1.7) * mm});
            skLineSegment(sketch, "E2319", {"start": v(-12.6, 1.7) * mm, "end": v(-12.74, 1.72) * mm});
            skLineSegment(sketch, "E2320", {"start": v(-12.74, 1.72) * mm, "end": v(-12.9, 1.7) * mm});
            skLineSegment(sketch, "E2321", {"start": v(-12.9, 1.7) * mm, "end": v(-13.04, 1.66) * mm});
            skLineSegment(sketch, "E2322", {"start": v(-13.04, 1.66) * mm, "end": v(-13.17, 1.59) * mm});
            skLineSegment(sketch, "E2323", {"start": v(-13.17, 1.59) * mm, "end": v(-13.3, 1.5) * mm});
            skLineSegment(sketch, "E2324", {"start": v(-13.3, 1.5) * mm, "end": v(-13.39, 1.37) * mm});
            skLineSegment(sketch, "E2325", {"start": v(-13.39, 1.37) * mm, "end": v(-13.46, 1.24) * mm});
            skLineSegment(sketch, "E2326", {"start": v(-13.46, 1.24) * mm, "end": v(-13.5, 1.1) * mm});
            skLineSegment(sketch, "E2327", {"start": v(-13.5, 1.1) * mm, "end": v(-13.52, 0.94) * mm});
            skLineSegment(sketch, "E2328", {"start": v(-13.52, 0.94) * mm, "end": v(-13.5, 0.8) * mm});
            skLineSegment(sketch, "E2329", {"start": v(-13.5, 0.8) * mm, "end": v(-13.46, 0.65) * mm});
            skLineSegment(sketch, "E2330", {"start": v(-13.46, 0.65) * mm, "end": v(-13.39, 0.51) * mm});
            skLineSegment(sketch, "E2331", {"start": v(-13.39, 0.51) * mm, "end": v(-13.3, 0.4) * mm});
            skLineSegment(sketch, "E2332", {"start": v(-13.3, 0.4) * mm, "end": v(-13.17, 0.3) * mm});
            skLineSegment(sketch, "E2333", {"start": v(-13.17, 0.3) * mm, "end": v(-13.04, 0.23) * mm});
            skLineSegment(sketch, "E2334", {"start": v(-13.04, 0.23) * mm, "end": v(-12.9, 0.18) * mm});
            skLineSegment(sketch, "E2335", {"start": v(-12.9, 0.18) * mm, "end": v(-12.74, 0.17) * mm});
            skLineSegment(sketch, "E2336", {"start": v(-12.74, 0.17) * mm, "end": v(-12.6, 0.18) * mm});
            skLineSegment(sketch, "E2337", {"start": v(-12.6, 0.18) * mm, "end": v(-12.45, 0.23) * mm});
            skLineSegment(sketch, "E2338", {"start": v(-12.45, 0.23) * mm, "end": v(-12.31, 0.3) * mm});
            skLineSegment(sketch, "E2339", {"start": v(-12.31, 0.3) * mm, "end": v(-12.2, 0.4) * mm});
            skLineSegment(sketch, "E2340", {"start": v(-12.2, 0.4) * mm, "end": v(-12.1, 0.51) * mm});
            skLineSegment(sketch, "E2341", {"start": v(-12.1, 0.51) * mm, "end": v(-12.03, 0.65) * mm});
            skLineSegment(sketch, "E2342", {"start": v(-12.03, 0.65) * mm, "end": v(-11.98, 0.8) * mm});
            skLineSegment(sketch, "E2343", {"start": v(-11.98, 0.8) * mm, "end": v(-11.97, 0.94) * mm});
            skLineSegment(sketch, "E2344", {"start": v(-11.97, 0.94) * mm, "end": v(-11.98, 1.1) * mm});
            skLineSegment(sketch, "E2345", {"start": v(-11.98, 1.1) * mm, "end": v(-12.03, 1.24) * mm});
            skLineSegment(sketch, "E2346", {"start": v(-12.03, 1.24) * mm, "end": v(-12.06, 1.3) * mm});
            skLineSegment(sketch, "E2347", {"start": v(-6.4, 10.26) * mm, "end": v(-6.36, 10.32) * mm});
            skLineSegment(sketch, "E2348", {"start": v(-6.36, 10.32) * mm, "end": v(-6.32, 10.47) * mm});
            skLineSegment(sketch, "E2349", {"start": v(-6.32, 10.47) * mm, "end": v(-6.3, 10.62) * mm});
            skLineSegment(sketch, "E2350", {"start": v(-6.3, 10.62) * mm, "end": v(-6.32, 10.77) * mm});
            skLineSegment(sketch, "E2351", {"start": v(-6.32, 10.77) * mm, "end": v(-6.36, 10.92) * mm});
            skLineSegment(sketch, "E2352", {"start": v(-6.36, 10.92) * mm, "end": v(-6.44, 11.05) * mm});
            skLineSegment(sketch, "E2353", {"start": v(-6.44, 11.05) * mm, "end": v(-6.53, 11.17) * mm});
            skLineSegment(sketch, "E2354", {"start": v(-6.53, 11.17) * mm, "end": v(-6.65, 11.26) * mm});
            skLineSegment(sketch, "E2355", {"start": v(-6.65, 11.26) * mm, "end": v(-6.78, 11.33) * mm});
            skLineSegment(sketch, "E2356", {"start": v(-6.78, 11.33) * mm, "end": v(-6.93, 11.38) * mm});
            skLineSegment(sketch, "E2357", {"start": v(-6.93, 11.38) * mm, "end": v(-7.08, 11.4) * mm});
            skLineSegment(sketch, "E2358", {"start": v(-7.08, 11.4) * mm, "end": v(-7.23, 11.38) * mm});
            skLineSegment(sketch, "E2359", {"start": v(-7.23, 11.38) * mm, "end": v(-7.38, 11.33) * mm});
            skLineSegment(sketch, "E2360", {"start": v(-7.38, 11.33) * mm, "end": v(-7.5, 11.26) * mm});
            skLineSegment(sketch, "E2361", {"start": v(-7.5, 11.26) * mm, "end": v(-7.63, 11.17) * mm});
            skLineSegment(sketch, "E2362", {"start": v(-7.63, 11.17) * mm, "end": v(-7.72, 11.05) * mm});
            skLineSegment(sketch, "E2363", {"start": v(-7.72, 11.05) * mm, "end": v(-7.8, 10.92) * mm});
            skLineSegment(sketch, "E2364", {"start": v(-7.8, 10.92) * mm, "end": v(-7.84, 10.77) * mm});
            skLineSegment(sketch, "E2365", {"start": v(-7.84, 10.77) * mm, "end": v(-7.85, 10.62) * mm});
            skLineSegment(sketch, "E2366", {"start": v(-7.85, 10.62) * mm, "end": v(-7.84, 10.47) * mm});
            skLineSegment(sketch, "E2367", {"start": v(-7.84, 10.47) * mm, "end": v(-7.8, 10.32) * mm});
            skLineSegment(sketch, "E2368", {"start": v(-7.8, 10.32) * mm, "end": v(-7.72, 10.19) * mm});
            skLineSegment(sketch, "E2369", {"start": v(-7.72, 10.19) * mm, "end": v(-7.63, 10.07) * mm});
            skLineSegment(sketch, "E2370", {"start": v(-7.63, 10.07) * mm, "end": v(-7.5, 9.98) * mm});
            skLineSegment(sketch, "E2371", {"start": v(-7.5, 9.98) * mm, "end": v(-7.38, 9.9) * mm});
            skLineSegment(sketch, "E2372", {"start": v(-7.38, 9.9) * mm, "end": v(-7.23, 9.86) * mm});
            skLineSegment(sketch, "E2373", {"start": v(-7.23, 9.86) * mm, "end": v(-7.08, 9.84) * mm});
            skLineSegment(sketch, "E2374", {"start": v(-7.08, 9.84) * mm, "end": v(-6.93, 9.86) * mm});
            skLineSegment(sketch, "E2375", {"start": v(-6.93, 9.86) * mm, "end": v(-6.78, 9.9) * mm});
            skLineSegment(sketch, "E2376", {"start": v(-6.78, 9.9) * mm, "end": v(-6.72, 9.94) * mm});
            skLineSegment(sketch, "E2377", {"start": v(-5.02, 11.91) * mm, "end": v(-5.01, 11.99) * mm});
            skLineSegment(sketch, "E2378", {"start": v(-5.01, 11.99) * mm, "end": v(-5.02, 11.99) * mm});
            skLineSegment(sketch, "E2379", {"start": v(-5.02, 11.99) * mm, "end": v(-5.02, 11.91) * mm});
            skLineSegment(sketch, "E2380", {"start": v(-5.02, 11.91) * mm, "end": v(-5.02, 11.34) * mm});
            skLineSegment(sketch, "E2381", {"start": v(-13.36, 2.84) * mm, "end": v(-13.3, 2.76) * mm});
            skLineSegment(sketch, "E2382", {"start": v(-13.3, 2.76) * mm, "end": v(-13.17, 2.66) * mm});
            skLineSegment(sketch, "E2383", {"start": v(-13.17, 2.66) * mm, "end": v(-13.04, 2.59) * mm});
            skLineSegment(sketch, "E2384", {"start": v(-13.04, 2.59) * mm, "end": v(-12.9, 2.54) * mm});
            skLineSegment(sketch, "E2385", {"start": v(-12.9, 2.54) * mm, "end": v(-12.74, 2.53) * mm});
            skLineSegment(sketch, "E2386", {"start": v(-12.74, 2.53) * mm, "end": v(-12.6, 2.54) * mm});
            skLineSegment(sketch, "E2387", {"start": v(-12.6, 2.54) * mm, "end": v(-12.45, 2.59) * mm});
            skLineSegment(sketch, "E2388", {"start": v(-12.45, 2.59) * mm, "end": v(-12.31, 2.66) * mm});
            skLineSegment(sketch, "E2389", {"start": v(-12.31, 2.66) * mm, "end": v(-12.2, 2.76) * mm});
            skLineSegment(sketch, "E2390", {"start": v(-12.2, 2.76) * mm, "end": v(-12.1, 2.87) * mm});
            skLineSegment(sketch, "E2391", {"start": v(-12.1, 2.87) * mm, "end": v(-12.03, 3) * mm});
            skLineSegment(sketch, "E2392", {"start": v(-12.03, 3) * mm, "end": v(-11.98, 3.15) * mm});
            skLineSegment(sketch, "E2393", {"start": v(-11.98, 3.15) * mm, "end": v(-11.97, 3.3) * mm});
            skLineSegment(sketch, "E2394", {"start": v(-11.97, 3.3) * mm, "end": v(-11.98, 3.46) * mm});
            skLineSegment(sketch, "E2395", {"start": v(-11.98, 3.46) * mm, "end": v(-12.03, 3.6) * mm});
            skLineSegment(sketch, "E2396", {"start": v(-12.03, 3.6) * mm, "end": v(-12.06, 3.67) * mm});
            skLineSegment(sketch, "E2397", {"start": v(-12.38, 3.98) * mm, "end": v(-12.45, 4.02) * mm});
            skLineSegment(sketch, "E2398", {"start": v(-12.45, 4.02) * mm, "end": v(-12.6, 4.06) * mm});
            skLineSegment(sketch, "E2399", {"start": v(-12.6, 4.06) * mm, "end": v(-12.74, 4.08) * mm});
            skLineSegment(sketch, "E2400", {"start": v(-12.74, 4.08) * mm, "end": v(-12.9, 4.06) * mm});
            skLineSegment(sketch, "E2401", {"start": v(-12.9, 4.06) * mm, "end": v(-13.04, 4.02) * mm});
            skLineSegment(sketch, "E2402", {"start": v(-13.04, 4.02) * mm, "end": v(-13.17, 3.95) * mm});
            skLineSegment(sketch, "E2403", {"start": v(-13.17, 3.95) * mm, "end": v(-13.3, 3.85) * mm});
            skLineSegment(sketch, "E2404", {"start": v(-13.3, 3.85) * mm, "end": v(-13.39, 3.73) * mm});
            skLineSegment(sketch, "E2405", {"start": v(-13.39, 3.73) * mm, "end": v(-13.46, 3.6) * mm});
            skLineSegment(sketch, "E2406", {"start": v(-13.46, 3.6) * mm, "end": v(-13.5, 3.46) * mm});
            skLineSegment(sketch, "E2407", {"start": v(-13.5, 3.46) * mm, "end": v(-13.52, 3.32) * mm});
            skLineSegment(sketch, "E2408", {"start": v(-12.97, 6.4) * mm, "end": v(-13.04, 6.38) * mm});
            skLineSegment(sketch, "E2409", {"start": v(-13.04, 6.38) * mm, "end": v(-13.17, 6.3) * mm});
            skLineSegment(sketch, "E2410", {"start": v(-13.17, 6.3) * mm, "end": v(-13.3, 6.21) * mm});
            skLineSegment(sketch, "E2411", {"start": v(-13.3, 6.21) * mm, "end": v(-13.39, 6.1) * mm});
            skLineSegment(sketch, "E2412", {"start": v(-13.39, 6.1) * mm, "end": v(-13.46, 5.96) * mm});
            skLineSegment(sketch, "E2413", {"start": v(-13.46, 5.96) * mm, "end": v(-13.5, 5.81) * mm});
            skLineSegment(sketch, "E2414", {"start": v(-13.5, 5.81) * mm, "end": v(-13.52, 5.66) * mm});
            skLineSegment(sketch, "E2415", {"start": v(-13.52, 5.66) * mm, "end": v(-13.5, 5.51) * mm});
            skLineSegment(sketch, "E2416", {"start": v(-13.5, 5.51) * mm, "end": v(-13.46, 5.37) * mm});
            skLineSegment(sketch, "E2417", {"start": v(-13.46, 5.37) * mm, "end": v(-13.39, 5.23) * mm});
            skLineSegment(sketch, "E2418", {"start": v(-13.39, 5.23) * mm, "end": v(-13.3, 5.12) * mm});
            skLineSegment(sketch, "E2419", {"start": v(-13.3, 5.12) * mm, "end": v(-13.17, 5.02) * mm});
            skLineSegment(sketch, "E2420", {"start": v(-13.17, 5.02) * mm, "end": v(-13.04, 4.95) * mm});
            skLineSegment(sketch, "E2421", {"start": v(-13.04, 4.95) * mm, "end": v(-12.9, 4.9) * mm});
            skLineSegment(sketch, "E2422", {"start": v(-12.9, 4.9) * mm, "end": v(-12.74, 4.89) * mm});
            skLineSegment(sketch, "E2423", {"start": v(-12.74, 4.89) * mm, "end": v(-12.6, 4.9) * mm});
            skLineSegment(sketch, "E2424", {"start": v(-12.6, 4.9) * mm, "end": v(-12.45, 4.95) * mm});
            skLineSegment(sketch, "E2425", {"start": v(-12.45, 4.95) * mm, "end": v(-12.31, 5.02) * mm});
            skLineSegment(sketch, "E2426", {"start": v(-12.31, 5.02) * mm, "end": v(-12.2, 5.12) * mm});
            skLineSegment(sketch, "E2427", {"start": v(-12.2, 5.12) * mm, "end": v(-12.1, 5.23) * mm});
            skLineSegment(sketch, "E2428", {"start": v(-12.1, 5.23) * mm, "end": v(-12.03, 5.37) * mm});
            skLineSegment(sketch, "E2429", {"start": v(-12.03, 5.37) * mm, "end": v(-11.98, 5.51) * mm});
            skLineSegment(sketch, "E2430", {"start": v(-11.98, 5.51) * mm, "end": v(-11.97, 5.66) * mm});
            skLineSegment(sketch, "E2431", {"start": v(-11.97, 5.66) * mm, "end": v(-11.98, 5.81) * mm});
            skLineSegment(sketch, "E2432", {"start": v(-11.98, 5.81) * mm, "end": v(-12.03, 5.96) * mm});
            skLineSegment(sketch, "E2433", {"start": v(-12.03, 5.96) * mm, "end": v(-12.1, 6.1) * mm});
            skLineSegment(sketch, "E2434", {"start": v(-12.1, 6.1) * mm, "end": v(-12.2, 6.21) * mm});
            skLineSegment(sketch, "E2435", {"start": v(-12.2, 6.21) * mm, "end": v(-12.31, 6.3) * mm});
            skLineSegment(sketch, "E2436", {"start": v(-12.31, 6.3) * mm, "end": v(-12.45, 6.38) * mm});
            skLineSegment(sketch, "E2437", {"start": v(-12.45, 6.38) * mm, "end": v(-12.52, 6.4) * mm});
            skLineSegment(sketch, "E2438", {"start": v(-13.84, 10.96) * mm, "end": v(-13.7, 11.22) * mm});
            skLineSegment(sketch, "E2439", {"start": v(-13.7, 11.22) * mm, "end": v(-13.61, 11.5) * mm});
            skLineSegment(sketch, "E2440", {"start": v(-13.61, 11.5) * mm, "end": v(-13.59, 11.8) * mm});
            skLineSegment(sketch, "E2441", {"start": v(-13.59, 11.8) * mm, "end": v(-13.61, 12.1) * mm});
            skLineSegment(sketch, "E2442", {"start": v(-13.61, 12.1) * mm, "end": v(-13.7, 12.38) * mm});
            skLineSegment(sketch, "E2443", {"start": v(-13.7, 12.38) * mm, "end": v(-13.84, 12.64) * mm});
            skLineSegment(sketch, "E2444", {"start": v(-13.84, 12.64) * mm, "end": v(-14.03, 12.87) * mm});
            skLineSegment(sketch, "E2445", {"start": v(-14.03, 12.87) * mm, "end": v(-14.26, 13.06) * mm});
            skLineSegment(sketch, "E2446", {"start": v(-14.26, 13.06) * mm, "end": v(-14.52, 13.2) * mm});
            skLineSegment(sketch, "E2447", {"start": v(-14.52, 13.2) * mm, "end": v(-14.8, 13.29) * mm});
            skLineSegment(sketch, "E2448", {"start": v(-14.8, 13.29) * mm, "end": v(-15.1, 13.32) * mm});
            skLineSegment(sketch, "E2449", {"start": v(-15.1, 13.32) * mm, "end": v(-15.4, 13.29) * mm});
            skLineSegment(sketch, "E2450", {"start": v(-15.4, 13.29) * mm, "end": v(-15.68, 13.2) * mm});
            skLineSegment(sketch, "E2451", {"start": v(-15.68, 13.2) * mm, "end": v(-15.95, 13.06) * mm});
            skLineSegment(sketch, "E2452", {"start": v(-15.95, 13.06) * mm, "end": v(-16.18, 12.87) * mm});
            skLineSegment(sketch, "E2453", {"start": v(-16.18, 12.87) * mm, "end": v(-16.36, 12.64) * mm});
            skLineSegment(sketch, "E2454", {"start": v(-16.36, 12.64) * mm, "end": v(-16.5, 12.38) * mm});
            skLineSegment(sketch, "E2455", {"start": v(-16.5, 12.38) * mm, "end": v(-16.6, 12.1) * mm});
            skLineSegment(sketch, "E2456", {"start": v(-16.6, 12.1) * mm, "end": v(-16.62, 11.8) * mm});
            skLineSegment(sketch, "E2457", {"start": v(-16.62, 11.8) * mm, "end": v(-16.6, 11.5) * mm});
            skLineSegment(sketch, "E2458", {"start": v(-16.6, 11.5) * mm, "end": v(-16.5, 11.22) * mm});
            skLineSegment(sketch, "E2459", {"start": v(-16.5, 11.22) * mm, "end": v(-16.36, 10.96) * mm});
            skLineSegment(sketch, "E2460", {"start": v(-16.36, 10.96) * mm, "end": v(-16.18, 10.73) * mm});
            skLineSegment(sketch, "E2461", {"start": v(-16.18, 10.73) * mm, "end": v(-15.95, 10.54) * mm});
            skLineSegment(sketch, "E2462", {"start": v(-15.95, 10.54) * mm, "end": v(-15.68, 10.4) * mm});
            skLineSegment(sketch, "E2463", {"start": v(-15.68, 10.4) * mm, "end": v(-15.4, 10.31) * mm});
            skLineSegment(sketch, "E2464", {"start": v(-15.4, 10.31) * mm, "end": v(-15.1, 10.28) * mm});
            skLineSegment(sketch, "E2465", {"start": v(-15.1, 10.28) * mm, "end": v(-14.8, 10.31) * mm});
            skLineSegment(sketch, "E2466", {"start": v(-14.8, 10.31) * mm, "end": v(-14.52, 10.4) * mm});
            skLineSegment(sketch, "E2467", {"start": v(-14.52, 10.4) * mm, "end": v(-14.26, 10.54) * mm});
            skLineSegment(sketch, "E2468", {"start": v(-14.26, 10.54) * mm, "end": v(-14.03, 10.73) * mm});
            skLineSegment(sketch, "E2469", {"start": v(-14.03, 10.73) * mm, "end": v(-13.84, 10.96) * mm});
            skLineSegment(sketch, "E2470", {"start": v(-13.87, 10.97) * mm, "end": v(-13.73, 11.23) * mm});
            skLineSegment(sketch, "E2471", {"start": v(-13.73, 11.23) * mm, "end": v(-13.64, 11.5) * mm});
            skLineSegment(sketch, "E2472", {"start": v(-13.64, 11.5) * mm, "end": v(-13.62, 11.8) * mm});
            skLineSegment(sketch, "E2473", {"start": v(-13.62, 11.8) * mm, "end": v(-13.64, 12.09) * mm});
            skLineSegment(sketch, "E2474", {"start": v(-13.64, 12.09) * mm, "end": v(-13.73, 12.37) * mm});
            skLineSegment(sketch, "E2475", {"start": v(-13.73, 12.37) * mm, "end": v(-13.87, 12.63) * mm});
            skLineSegment(sketch, "E2476", {"start": v(-13.87, 12.63) * mm, "end": v(-14.05, 12.85) * mm});
            skLineSegment(sketch, "E2477", {"start": v(-14.05, 12.85) * mm, "end": v(-14.28, 13.04) * mm});
            skLineSegment(sketch, "E2478", {"start": v(-14.28, 13.04) * mm, "end": v(-14.53, 13.17) * mm});
            skLineSegment(sketch, "E2479", {"start": v(-14.53, 13.17) * mm, "end": v(-14.81, 13.26) * mm});
            skLineSegment(sketch, "E2480", {"start": v(-14.81, 13.26) * mm, "end": v(-15.1, 13.29) * mm});
            skLineSegment(sketch, "E2481", {"start": v(-15.1, 13.29) * mm, "end": v(-15.4, 13.26) * mm});
            skLineSegment(sketch, "E2482", {"start": v(-15.4, 13.26) * mm, "end": v(-15.67, 13.17) * mm});
            skLineSegment(sketch, "E2483", {"start": v(-15.67, 13.17) * mm, "end": v(-15.93, 13.04) * mm});
            skLineSegment(sketch, "E2484", {"start": v(-15.93, 13.04) * mm, "end": v(-16.15, 12.85) * mm});
            skLineSegment(sketch, "E2485", {"start": v(-16.15, 12.85) * mm, "end": v(-16.34, 12.63) * mm});
            skLineSegment(sketch, "E2486", {"start": v(-16.34, 12.63) * mm, "end": v(-16.48, 12.37) * mm});
            skLineSegment(sketch, "E2487", {"start": v(-16.48, 12.37) * mm, "end": v(-16.56, 12.09) * mm});
            skLineSegment(sketch, "E2488", {"start": v(-16.56, 12.09) * mm, "end": v(-16.59, 11.8) * mm});
            skLineSegment(sketch, "E2489", {"start": v(-16.59, 11.8) * mm, "end": v(-16.56, 11.5) * mm});
            skLineSegment(sketch, "E2490", {"start": v(-16.56, 11.5) * mm, "end": v(-16.48, 11.23) * mm});
            skLineSegment(sketch, "E2491", {"start": v(-16.48, 11.23) * mm, "end": v(-16.34, 10.97) * mm});
            skLineSegment(sketch, "E2492", {"start": v(-16.34, 10.97) * mm, "end": v(-16.15, 10.75) * mm});
            skLineSegment(sketch, "E2493", {"start": v(-16.15, 10.75) * mm, "end": v(-15.93, 10.56) * mm});
            skLineSegment(sketch, "E2494", {"start": v(-15.93, 10.56) * mm, "end": v(-15.67, 10.43) * mm});
            skLineSegment(sketch, "E2495", {"start": v(-15.67, 10.43) * mm, "end": v(-15.4, 10.34) * mm});
            skLineSegment(sketch, "E2496", {"start": v(-15.4, 10.34) * mm, "end": v(-15.1, 10.31) * mm});
            skLineSegment(sketch, "E2497", {"start": v(-15.1, 10.31) * mm, "end": v(-14.81, 10.34) * mm});
            skLineSegment(sketch, "E2498", {"start": v(-14.81, 10.34) * mm, "end": v(-14.53, 10.43) * mm});
            skLineSegment(sketch, "E2499", {"start": v(-14.53, 10.43) * mm, "end": v(-14.28, 10.56) * mm});
            skLineSegment(sketch, "E2500", {"start": v(-14.28, 10.56) * mm, "end": v(-14.05, 10.75) * mm});
            skLineSegment(sketch, "E2501", {"start": v(-14.05, 10.75) * mm, "end": v(-13.87, 10.97) * mm});
            skLineSegment(sketch, "E2502", {"start": v(-19.8, -16.02) * mm, "end": v(19.8, -16.02) * mm});
            skLineSegment(sketch, "E2503", {"start": v(19.8, -16.02) * mm, "end": v(19.8, 16.02) * mm});
            skLineSegment(sketch, "E2504", {"start": v(19.8, 16.02) * mm, "end": v(-19.8, 16.02) * mm});
            skLineSegment(sketch, "E2505", {"start": v(-19.8, 16.02) * mm, "end": v(-19.8, -16.02) * mm});
            skSolve(sketch);
        }
        {
            var Q0;
            Q0=makeQuery(id+"F0.imprint","IMPRINT",FACE,{"disambiguationData":[TD([[makeQuery(id+"F0.imprint","IMPRINT",EDGE,{"derivedFrom":sQuery(id+"F0.wireOp",EDGE,"E810")}),1.0]])]});
            var Q1;
            Q1=makeQuery(id+"F0.imprint","IMPRINT",FACE,{"disambiguationData":[TD([[makeQuery(id+"F0.imprint","IMPRINT",EDGE,{"derivedFrom":sQuery(id+"F0.wireOp",EDGE,"E575")}),1.0]])]});
            var Q2;
            Q2=makeQuery(id+"F0.imprint","IMPRINT",FACE,{"disambiguationData":[TD([[makeQuery(id+"F0.imprint","IMPRINT",EDGE,{"derivedFrom":sQuery(id+"F0.wireOp",EDGE,"E7")}),1.0]])]});
            var Q3;
            Q3=makeQuery(id+"F0.imprint","IMPRINT",FACE,{"disambiguationData":[TD([[makeQuery(id+"F0.imprint","IMPRINT",EDGE,{"derivedFrom":sQuery(id+"F0.wireOp",EDGE,"E3")}),1.0]])]});
            var Q4;
            Q4=makeQuery(id+"F0.imprint","IMPRINT",FACE,{"disambiguationData":[TD([[makeQuery(id+"F0.imprint","IMPRINT",EDGE,{"derivedFrom":sQuery(id+"F0.wireOp",EDGE,"E13")}),1.0]])]});
            var Q5;
            Q5=makeQuery(id+"F0.imprint","IMPRINT",FACE,{"disambiguationData":[TD([[makeQuery(id+"F0.imprint","IMPRINT",EDGE,{"derivedFrom":sQuery(id+"F0.wireOp",EDGE,"E1")}),1.0]])]});
            var Q6;
            Q6=makeQuery(id+"F0.imprint","IMPRINT",FACE,{"disambiguationData":[TD([[makeQuery(id+"F0.imprint","IMPRINT",EDGE,{"derivedFrom":sQuery(id+"F0.wireOp",EDGE,"E2014")}),1.0]])]});
            var Q7;
            Q7=makeQuery(id+"F0.imprint","IMPRINT",FACE,{"disambiguationData":[TD([[makeQuery(id+"F0.imprint","IMPRINT",EDGE,{"derivedFrom":sQuery(id+"F0.wireOp",EDGE,"E1730")}),1.0]])]});
            var Q8;
            Q8=makeQuery(id+"F0.imprint","IMPRINT",FACE,{"disambiguationData":[TD([[makeQuery(id+"F0.imprint","IMPRINT",EDGE,{"derivedFrom":sQuery(id+"F0.wireOp",EDGE,"E1663")}),1.0]])]});
            var Q9;
            Q9=makeQuery(id+"F0.imprint","IMPRINT",FACE,{"disambiguationData":[TD([[makeQuery(id+"F0.imprint","IMPRINT",EDGE,{"derivedFrom":sQuery(id+"F0.wireOp",EDGE,"E11")}),1.0]])]});
            var Q10;
            Q10=makeQuery(id+"F0.imprint","IMPRINT",FACE,{"disambiguationData":[TD([[makeQuery(id+"F0.imprint","IMPRINT",EDGE,{"derivedFrom":sQuery(id+"F0.wireOp",EDGE,"E1105")}),1.0]])]});
            var Q11;
            Q11=makeQuery(id+"F0.imprint","IMPRINT",FACE,{"disambiguationData":[TD([[makeQuery(id+"F0.imprint","IMPRINT",EDGE,{"derivedFrom":sQuery(id+"F0.wireOp",EDGE,"E19")}),1.0]])]});
            var Q12;
            Q12=makeQuery(id+"F0.imprint","IMPRINT",FACE,{"disambiguationData":[TD([[makeQuery(id+"F0.imprint","IMPRINT",EDGE,{"derivedFrom":sQuery(id+"F0.wireOp",EDGE,"E15")}),1.0]])]});
            var Q13;
            {var subQ2=sQuery(id+"F0.wireOp",EDGE,"E805");Q13=makeQuery(id+"F0.imprint","IMPRINT",FACE,{"disambiguationData":[TD([[makeQuery(id+"F0.imprint","IMPRINT",EDGE,{"derivedFrom":subQ2}),1.0]])]});}
            var Q14;
            Q14=makeQuery(id+"F0.imprint","IMPRINT",FACE,{"disambiguationData":[TD([[makeQuery(id+"F0.imprint","IMPRINT",EDGE,{"derivedFrom":sQuery(id+"F0.wireOp",EDGE,"E1261")}),1.0]])]});
            var Q15;
            {var subQ2=sQuery(id+"F0.wireOp",EDGE,"E1658");Q15=makeQuery(id+"F0.imprint","IMPRINT",FACE,{"disambiguationData":[TD([[makeQuery(id+"F0.imprint","IMPRINT",EDGE,{"derivedFrom":subQ2}),1.0]])]});}
            var Q16;
            {var subQ2=sQuery(id+"F0.wireOp",EDGE,"E570");Q16=makeQuery(id+"F0.imprint","IMPRINT",FACE,{"disambiguationData":[TD([[makeQuery(id+"F0.imprint","IMPRINT",EDGE,{"derivedFrom":subQ2}),1.0]])]});}
            var Q17;
            Q17=makeQuery(id+"F0.imprint","IMPRINT",FACE,{"disambiguationData":[TD([[makeQuery(id+"F0.imprint","IMPRINT",EDGE,{"derivedFrom":sQuery(id+"F0.wireOp",EDGE,"E11")}),-1.0]])]});
            var Q18;
            Q18=makeQuery(id+"F0.imprint","IMPRINT",FACE,{"disambiguationData":[TD([[makeQuery(id+"F0.imprint","IMPRINT",EDGE,{"derivedFrom":sQuery(id+"F0.wireOp",EDGE,"E9")}),-1.0]])]});
            var Q19;
            Q19=makeQuery(id+"F0.imprint","IMPRINT",FACE,{"disambiguationData":[TD([[makeQuery(id+"F0.imprint","IMPRINT",EDGE,{"derivedFrom":sQuery(id+"F0.wireOp",EDGE,"E7")}),-1.0]])]});
            var Q20;
            Q20=makeQuery(id+"F0.imprint","IMPRINT",FACE,{"disambiguationData":[TD([[makeQuery(id+"F0.imprint","IMPRINT",EDGE,{"derivedFrom":sQuery(id+"F0.wireOp",EDGE,"E19")}),-1.0]])]});
            var Q21;
            Q21=makeQuery(id+"F0.imprint","IMPRINT",FACE,{"disambiguationData":[TD([[makeQuery(id+"F0.imprint","IMPRINT",EDGE,{"derivedFrom":sQuery(id+"F0.wireOp",EDGE,"E5")}),-1.0]])]});
            var Q22;
            Q22=makeQuery(id+"F0.imprint","IMPRINT",FACE,{"disambiguationData":[TD([[makeQuery(id+"F0.imprint","IMPRINT",EDGE,{"derivedFrom":sQuery(id+"F0.wireOp",EDGE,"E3")}),-1.0]])]});
            var Q23;
            Q23=makeQuery(id+"F0.imprint","IMPRINT",FACE,{"disambiguationData":[TD([[makeQuery(id+"F0.imprint","IMPRINT",EDGE,{"derivedFrom":sQuery(id+"F0.wireOp",EDGE,"E1")}),-1.0]])]});
            var Q24;
            {var subQ4=sQuery(id+"F0.wireOp",EDGE,"E332");Q24=makeQuery(id+"F0.imprint","IMPRINT",FACE,{"disambiguationData":[TD([[makeQuery(id+"F0.imprint","IMPRINT",EDGE,{"derivedFrom":subQ4}),-1.0]])]});}
            var Q25;
            Q25=makeQuery(id+"F0.imprint","IMPRINT",FACE,{"disambiguationData":[TD([[makeQuery(id+"F0.imprint","IMPRINT",EDGE,{"derivedFrom":sQuery(id+"F0.wireOp",EDGE,"E20")}),1.0]])]});
            var Q26;
            Q26=makeQuery(id+"F0.imprint","IMPRINT",FACE,{"disambiguationData":[TD([[makeQuery(id+"F0.imprint","IMPRINT",EDGE,{"derivedFrom":sQuery(id+"F0.wireOp",EDGE,"E15")}),-1.0]])]});
            var Q27;
            Q27=makeQuery(id+"F0.imprint","IMPRINT",FACE,{"disambiguationData":[TD([[makeQuery(id+"F0.imprint","IMPRINT",EDGE,{"derivedFrom":sQuery(id+"F0.wireOp",EDGE,"E13")}),-1.0]])]});
            var Q28;
            Q28=makeQuery(id+"F0.imprint","IMPRINT",FACE,{"disambiguationData":[TD([[makeQuery(id+"F0.imprint","IMPRINT",EDGE,{"derivedFrom":sQuery(id+"F0.wireOp",EDGE,"E1011")}),1.0]])]});
            var Q29;
            Q29=makeQuery(id+"F0.imprint","IMPRINT",FACE,{"disambiguationData":[TD([[makeQuery(id+"F0.imprint","IMPRINT",EDGE,{"derivedFrom":sQuery(id+"F0.wireOp",EDGE,"E2438")}),1.0]])]});
            var Q30;
            {var subQ4=sQuery(id+"F0.wireOp",EDGE,"E264");Q30=makeQuery(id+"F0.imprint","IMPRINT",FACE,{"disambiguationData":[TD([[makeQuery(id+"F0.imprint","IMPRINT",EDGE,{"derivedFrom":subQ4}),-1.0]])]});}
            var Q31;
            {var subQ4=sQuery(id+"F0.wireOp",EDGE,"E2035");Q31=makeQuery(id+"F0.imprint","IMPRINT",FACE,{"disambiguationData":[TD([[makeQuery(id+"F0.imprint","IMPRINT",EDGE,{"derivedFrom":subQ4}),-1.0]])]});}
            var Q32;
            {var subQ4=sQuery(id+"F0.wireOp",EDGE,"E298");Q32=makeQuery(id+"F0.imprint","IMPRINT",FACE,{"disambiguationData":[TD([[makeQuery(id+"F0.imprint","IMPRINT",EDGE,{"derivedFrom":subQ4}),-1.0]])]});}
            var Q33;
            {var subQ2=sQuery(id+"F0.wireOp",EDGE,"E1075");Q33=makeQuery(id+"F0.imprint","IMPRINT",FACE,{"disambiguationData":[TD([[makeQuery(id+"F0.imprint","IMPRINT",EDGE,{"derivedFrom":subQ2}),1.0]])]});}
            var Q34;
            {var subQ4=sQuery(id+"F0.wireOp",EDGE,"E918");Q34=makeQuery(id+"F0.imprint","IMPRINT",FACE,{"disambiguationData":[TD([[makeQuery(id+"F0.imprint","IMPRINT",EDGE,{"derivedFrom":subQ4}),-1.0]])]});}
            var Q35;
            {var subQ4=sQuery(id+"F0.wireOp",EDGE,"E2091");Q35=makeQuery(id+"F0.imprint","IMPRINT",FACE,{"disambiguationData":[TD([[makeQuery(id+"F0.imprint","IMPRINT",EDGE,{"derivedFrom":subQ4}),-1.0]])]});}
            var Q36;
            {var subQ4=sQuery(id+"F0.wireOp",EDGE,"E652");Q36=makeQuery(id+"F0.imprint","IMPRINT",FACE,{"disambiguationData":[TD([[makeQuery(id+"F0.imprint","IMPRINT",EDGE,{"derivedFrom":subQ4}),-1.0]])]});}
            var Q37;
            {var subQ4=sQuery(id+"F0.wireOp",EDGE,"E1486");Q37=makeQuery(id+"F0.imprint","IMPRINT",FACE,{"disambiguationData":[TD([[makeQuery(id+"F0.imprint","IMPRINT",EDGE,{"derivedFrom":subQ4}),-1.0]])]});}
            var Q38;
            {var subQ4=sQuery(id+"F0.wireOp",EDGE,"E1454");Q38=makeQuery(id+"F0.imprint","IMPRINT",FACE,{"disambiguationData":[TD([[makeQuery(id+"F0.imprint","IMPRINT",EDGE,{"derivedFrom":subQ4}),-1.0]])]});}
            var Q39;
            {var subQ4=sQuery(id+"F0.wireOp",EDGE,"E1388");Q39=makeQuery(id+"F0.imprint","IMPRINT",FACE,{"disambiguationData":[TD([[makeQuery(id+"F0.imprint","IMPRINT",EDGE,{"derivedFrom":subQ4}),-1.0]])]});}
            var Q40;
            {var subQ3=sQuery(id+"F0.wireOp",EDGE,"E182");Q40=makeQuery(id+"F0.imprint","IMPRINT",FACE,{"disambiguationData":[TD([[makeQuery(id+"F0.imprint","IMPRINT",EDGE,{"derivedFrom":subQ3}),-1.0]])]});}
            var Q41;
            {var subQ4=sQuery(id+"F0.wireOp",EDGE,"E1299");Q41=makeQuery(id+"F0.imprint","IMPRINT",FACE,{"disambiguationData":[TD([[makeQuery(id+"F0.imprint","IMPRINT",EDGE,{"derivedFrom":subQ4}),-1.0]])]});}
            var Q42;
            {var subQ4=sQuery(id+"F0.wireOp",EDGE,"E147");Q42=makeQuery(id+"F0.imprint","IMPRINT",FACE,{"disambiguationData":[TD([[makeQuery(id+"F0.imprint","IMPRINT",EDGE,{"derivedFrom":subQ4}),-1.0]])]});}
            var Q43;
            {var subQ4=sQuery(id+"F0.wireOp",EDGE,"E111");Q43=makeQuery(id+"F0.imprint","IMPRINT",FACE,{"disambiguationData":[TD([[makeQuery(id+"F0.imprint","IMPRINT",EDGE,{"derivedFrom":subQ4}),-1.0]])]});}
            var Q44;
            {var subQ4=sQuery(id+"F0.wireOp",EDGE,"E1666");Q44=makeQuery(id+"F0.imprint","IMPRINT",FACE,{"disambiguationData":[TD([[makeQuery(id+"F0.imprint","IMPRINT",EDGE,{"derivedFrom":subQ4}),-1.0]])]});}
            var Q45;
            {var subQ3=sQuery(id+"F0.wireOp",EDGE,"E443");Q45=makeQuery(id+"F0.imprint","IMPRINT",FACE,{"disambiguationData":[TD([[makeQuery(id+"F0.imprint","IMPRINT",EDGE,{"derivedFrom":subQ3}),-1.0]])]});}
            var Q46;
            {var subQ3=sQuery(id+"F0.wireOp",EDGE,"E1700");Q46=makeQuery(id+"F0.imprint","IMPRINT",FACE,{"disambiguationData":[TD([[makeQuery(id+"F0.imprint","IMPRINT",EDGE,{"derivedFrom":subQ3}),1.0]])]});}
            var Q47;
            {var subQ3=sQuery(id+"F0.wireOp",EDGE,"E1526");Q47=makeQuery(id+"F0.imprint","IMPRINT",FACE,{"disambiguationData":[TD([[makeQuery(id+"F0.imprint","IMPRINT",EDGE,{"derivedFrom":subQ3}),-1.0]])]});}
            var Q48;
            {var subQ3=sQuery(id+"F0.wireOp",EDGE,"E217");Q48=makeQuery(id+"F0.imprint","IMPRINT",FACE,{"disambiguationData":[TD([[makeQuery(id+"F0.imprint","IMPRINT",EDGE,{"derivedFrom":subQ3}),-1.0]])]});}
            var Q49;
            {var subQ4=sQuery(id+"F0.wireOp",EDGE,"E813");Q49=makeQuery(id+"F0.imprint","IMPRINT",FACE,{"disambiguationData":[TD([[makeQuery(id+"F0.imprint","IMPRINT",EDGE,{"derivedFrom":subQ4}),-1.0]])]});}
            var Q50;
            {var subQ4=sQuery(id+"F0.wireOp",EDGE,"E1784");Q50=makeQuery(id+"F0.imprint","IMPRINT",FACE,{"disambiguationData":[TD([[makeQuery(id+"F0.imprint","IMPRINT",EDGE,{"derivedFrom":subQ4}),-1.0]])]});}
            var Q51;
            {var subQ1=sQuery(id+"F0.wireOp",EDGE,"E1513");Q51=makeQuery(id+"F0.imprint","IMPRINT",FACE,{"disambiguationData":[TD([[makeQuery(id+"F0.imprint","IMPRINT",EDGE,{"derivedFrom":subQ1}),-1.0]])]});}
            var Q52;
            {var subQ4=sQuery(id+"F0.wireOp",EDGE,"E578");Q52=makeQuery(id+"F0.imprint","IMPRINT",FACE,{"disambiguationData":[TD([[makeQuery(id+"F0.imprint","IMPRINT",EDGE,{"derivedFrom":subQ4}),-1.0]])]});}
            var Q53;
            Q53=makeQuery(id+"F0.imprint","IMPRINT",FACE,{"disambiguationData":[TD([[makeQuery(id+"F0.imprint","IMPRINT",EDGE,{"derivedFrom":sQuery(id+"F0.wireOp",EDGE,"E1613")}),1.0]])]});
            var Q54;
            Q54=makeQuery(id+"F0.imprint","IMPRINT",FACE,{"disambiguationData":[TD([[makeQuery(id+"F0.imprint","IMPRINT",EDGE,{"derivedFrom":sQuery(id+"F0.wireOp",EDGE,"E1985")}),1.0]])]});
            var Q55;
            Q55=makeQuery(id+"F0.imprint","IMPRINT",FACE,{"disambiguationData":[TD([[makeQuery(id+"F0.imprint","IMPRINT",EDGE,{"derivedFrom":sQuery(id+"F0.wireOp",EDGE,"E2190")}),1.0]])]});
            var Q56;
            Q56=makeQuery(id+"F0.imprint","IMPRINT",FACE,{"disambiguationData":[TD([[makeQuery(id+"F0.imprint","IMPRINT",EDGE,{"derivedFrom":sQuery(id+"F0.wireOp",EDGE,"E767")}),1.0]])]});
            var Q57;
            Q57=makeQuery(id+"F0.imprint","IMPRINT",FACE,{"disambiguationData":[TD([[makeQuery(id+"F0.imprint","IMPRINT",EDGE,{"derivedFrom":sQuery(id+"F0.wireOp",EDGE,"E2199")}),1.0]])]});
            var Q58;
            Q58=makeQuery(id+"F0.imprint","IMPRINT",FACE,{"disambiguationData":[TD([[makeQuery(id+"F0.imprint","IMPRINT",EDGE,{"derivedFrom":sQuery(id+"F0.wireOp",EDGE,"E700")}),1.0]])]});
            var Q59;
            Q59=makeQuery(id+"F0.imprint","IMPRINT",FACE,{"disambiguationData":[TD([[makeQuery(id+"F0.imprint","IMPRINT",EDGE,{"derivedFrom":sQuery(id+"F0.wireOp",EDGE,"E734")}),1.0]])]});
            var Q60;
            Q60=makeQuery(id+"F0.imprint","IMPRINT",FACE,{"disambiguationData":[TD([[makeQuery(id+"F0.imprint","IMPRINT",EDGE,{"derivedFrom":sQuery(id+"F0.wireOp",EDGE,"E1008")}),1.0]])]});
            var Q61;
            Q61=makeQuery(id+"F0.imprint","IMPRINT",FACE,{"disambiguationData":[TD([[makeQuery(id+"F0.imprint","IMPRINT",EDGE,{"derivedFrom":sQuery(id+"F0.wireOp",EDGE,"E771")}),1.0]])]});
            var Q62;
            Q62=makeQuery(id+"F0.imprint","IMPRINT",FACE,{"disambiguationData":[TD([[makeQuery(id+"F0.imprint","IMPRINT",EDGE,{"derivedFrom":sQuery(id+"F0.wireOp",EDGE,"E2377")}),1.0]])]});
            var Q63;
            Q63=makeQuery(id+"F0.imprint","IMPRINT",FACE,{"disambiguationData":[TD([[makeQuery(id+"F0.imprint","IMPRINT",EDGE,{"derivedFrom":sQuery(id+"F0.wireOp",EDGE,"E1936")}),1.0]])]});
            var Q64;
            Q64=makeQuery(id+"F0.imprint","IMPRINT",FACE,{"disambiguationData":[TD([[makeQuery(id+"F0.imprint","IMPRINT",EDGE,{"derivedFrom":sQuery(id+"F0.wireOp",EDGE,"E1900")}),1.0]])]});
            var Q65;
            Q65=makeQuery(id+"F0.imprint","IMPRINT",FACE,{"disambiguationData":[TD([[makeQuery(id+"F0.imprint","IMPRINT",EDGE,{"derivedFrom":sQuery(id+"F0.wireOp",EDGE,"E2144")}),1.0]])]});
            var Q66;
            Q66=makeQuery(id+"F0.imprint","IMPRINT",FACE,{"disambiguationData":[TD([[makeQuery(id+"F0.imprint","IMPRINT",EDGE,{"derivedFrom":sQuery(id+"F0.wireOp",EDGE,"E497")}),1.0]])]});
            var Q67;
            Q67=makeQuery(id+"F0.imprint","IMPRINT",FACE,{"disambiguationData":[TD([[makeQuery(id+"F0.imprint","IMPRINT",EDGE,{"derivedFrom":sQuery(id+"F0.wireOp",EDGE,"E974")}),1.0]])]});
            var Q68;
            Q68=makeQuery(id+"F0.imprint","IMPRINT",FACE,{"disambiguationData":[TD([[makeQuery(id+"F0.imprint","IMPRINT",EDGE,{"derivedFrom":sQuery(id+"F0.wireOp",EDGE,"E1896")}),1.0]])]});
            var Q69;
            Q69=makeQuery(id+"F0.imprint","IMPRINT",FACE,{"disambiguationData":[TD([[makeQuery(id+"F0.imprint","IMPRINT",EDGE,{"derivedFrom":sQuery(id+"F0.wireOp",EDGE,"E504")}),1.0]])]});
            var Q70;
            Q70=makeQuery(id+"F0.imprint","IMPRINT",FACE,{"disambiguationData":[TD([[makeQuery(id+"F0.imprint","IMPRINT",EDGE,{"derivedFrom":sQuery(id+"F0.wireOp",EDGE,"E501")}),1.0]])]});
            var Q71;
            Q71=makeQuery(id+"F0.imprint","IMPRINT",FACE,{"disambiguationData":[TD([[makeQuery(id+"F0.imprint","IMPRINT",EDGE,{"derivedFrom":sQuery(id+"F0.wireOp",EDGE,"E538")}),1.0]])]});
            var Q72;
            Q72=makeQuery(id+"F0.imprint","IMPRINT",FACE,{"disambiguationData":[TD([[makeQuery(id+"F0.imprint","IMPRINT",EDGE,{"derivedFrom":sQuery(id+"F0.wireOp",EDGE,"E1980")}),1.0]])]});
            var Q73;
            Q73=makeQuery(id+"F0.imprint","IMPRINT",FACE,{"disambiguationData":[TD([[makeQuery(id+"F0.imprint","IMPRINT",EDGE,{"derivedFrom":sQuery(id+"F0.wireOp",EDGE,"E2311")}),1.0]])]});
            var Q74;
            Q74=makeQuery(id+"F0.imprint","IMPRINT",FACE,{"disambiguationData":[TD([[makeQuery(id+"F0.imprint","IMPRINT",EDGE,{"derivedFrom":sQuery(id+"F0.wireOp",EDGE,"E1943")}),1.0]])]});
            var Q75;
            Q75=makeQuery(id+"F0.imprint","IMPRINT",FACE,{"disambiguationData":[TD([[makeQuery(id+"F0.imprint","IMPRINT",EDGE,{"derivedFrom":sQuery(id+"F0.wireOp",EDGE,"E2273")}),1.0]])]});
            var Q76;
            Q76=makeQuery(id+"F0.imprint","IMPRINT",FACE,{"disambiguationData":[TD([[makeQuery(id+"F0.imprint","IMPRINT",EDGE,{"derivedFrom":sQuery(id+"F0.wireOp",EDGE,"E1650")}),1.0]])]});
            var Q77;
            Q77=makeQuery(id+"F0.imprint","IMPRINT",FACE,{"disambiguationData":[TD([[makeQuery(id+"F0.imprint","IMPRINT",EDGE,{"derivedFrom":sQuery(id+"F0.wireOp",EDGE,"E1617")}),1.0]])]});
            var Q78;
            Q78=makeQuery(id+"F0.imprint","IMPRINT",FACE,{"disambiguationData":[TD([[makeQuery(id+"F0.imprint","IMPRINT",EDGE,{"derivedFrom":sQuery(id+"F0.wireOp",EDGE,"E1580")}),1.0]])]});
            var Q79;
            Q79=makeQuery(id+"F0.imprint","IMPRINT",FACE,{"disambiguationData":[TD([[makeQuery(id+"F0.imprint","IMPRINT",EDGE,{"derivedFrom":sQuery(id+"F0.wireOp",EDGE,"E1992")}),1.0]])]});
            var Q80;
            Q80=makeQuery(id+"F0.imprint","IMPRINT",FACE,{"disambiguationData":[TD([[makeQuery(id+"F0.imprint","IMPRINT",EDGE,{"derivedFrom":sQuery(id+"F0.wireOp",EDGE,"E1257")}),1.0]])]});
            var Q81;
            Q81=makeQuery(id+"F0.imprint","IMPRINT",FACE,{"disambiguationData":[TD([[makeQuery(id+"F0.imprint","IMPRINT",EDGE,{"derivedFrom":sQuery(id+"F0.wireOp",EDGE,"E1939")}),1.0]])]});
            var Q82;
            Q82=makeQuery(id+"F0.imprint","IMPRINT",FACE,{"disambiguationData":[TD([[makeQuery(id+"F0.imprint","IMPRINT",EDGE,{"derivedFrom":sQuery(id+"F0.wireOp",EDGE,"E2307")}),1.0]])]});
            var Q83;
            Q83=makeQuery(id+"F0.imprint","IMPRINT",FACE,{"disambiguationData":[TD([[makeQuery(id+"F0.imprint","IMPRINT",EDGE,{"derivedFrom":sQuery(id+"F0.wireOp",EDGE,"E2202")}),1.0]])]});
            var Q84;
            Q84=makeQuery(id+"F0.imprint","IMPRINT",FACE,{"disambiguationData":[TD([[makeQuery(id+"F0.imprint","IMPRINT",EDGE,{"derivedFrom":sQuery(id+"F0.wireOp",EDGE,"E2194")}),1.0]])]});
            var Q85;
            Q85=makeQuery(id+"F0.imprint","IMPRINT",FACE,{"disambiguationData":[TD([[makeQuery(id+"F0.imprint","IMPRINT",EDGE,{"derivedFrom":sQuery(id+"F0.wireOp",EDGE,"E2157")}),1.0]])]});
            var Q86;
            Q86=makeQuery(id+"F0.imprint","IMPRINT",FACE,{"disambiguationData":[TD([[makeQuery(id+"F0.imprint","IMPRINT",EDGE,{"derivedFrom":sQuery(id+"F0.wireOp",EDGE,"E2314")}),1.0]])]});
            var Q87;
            Q87=makeQuery(id+"F0.imprint","IMPRINT",FACE,{"disambiguationData":[TD([[makeQuery(id+"F0.imprint","IMPRINT",EDGE,{"derivedFrom":sQuery(id+"F0.wireOp",EDGE,"E1933")}),1.0]])]});
            var Q88;
            Q88=makeQuery(id+"F0.imprint","IMPRINT",FACE,{"disambiguationData":[TD([[makeQuery(id+"F0.imprint","IMPRINT",EDGE,{"derivedFrom":sQuery(id+"F0.wireOp",EDGE,"E1654")}),1.0]])]});
            var Q89;
            Q89=makeQuery(id+"F0.imprint","IMPRINT",FACE,{"disambiguationData":[TD([[makeQuery(id+"F0.imprint","IMPRINT",EDGE,{"derivedFrom":sQuery(id+"F0.wireOp",EDGE,"E2269")}),1.0]])]});
            var Q90;
            Q90=makeQuery(id+"F0.imprint","IMPRINT",FACE,{"disambiguationData":[TD([[makeQuery(id+"F0.imprint","IMPRINT",EDGE,{"derivedFrom":sQuery(id+"F0.wireOp",EDGE,"E1988")}),1.0]])]});
            var Q91;
            Q91=makeQuery(id+"F0.imprint","IMPRINT",FACE,{"disambiguationData":[TD([[makeQuery(id+"F0.imprint","IMPRINT",EDGE,{"derivedFrom":sQuery(id+"F0.wireOp",EDGE,"E1946")}),1.0]])]});
            var Q92;
            Q92=makeQuery(id+"F0.imprint","IMPRINT",FACE,{"disambiguationData":[TD([[makeQuery(id+"F0.imprint","IMPRINT",EDGE,{"derivedFrom":sQuery(id+"F0.wireOp",EDGE,"E17")}),1.0]])]});
            var Q93;
            Q93=sQuery(id+"F0.wireOp",EDGE,"E1200");
            var Q94;
            Q94=sQuery(id+"F0.wireOp",EDGE,"E1199");
            var Q95;
            Q95=sQuery(id+"F0.wireOp",EDGE,"E1134");
            var Q96;
            Q96=sQuery(id+"F0.wireOp",EDGE,"E650");
            var Q97;
            Q97=sQuery(id+"F0.wireOp",EDGE,"E1404");
            var Q98;
            Q98=sQuery(id+"F0.wireOp",EDGE,"E329");
            var Q99;
            Q99=sQuery(id+"F0.wireOp",EDGE,"E105");
            var Q100;
            Q100=sQuery(id+"F0.wireOp",EDGE,"E89");
            var Q101;
            Q101=sQuery(id+"F0.wireOp",EDGE,"E953");
            var Q102;
            Q102=sQuery(id+"F0.wireOp",EDGE,"E296");
            var Q103;
            Q103=sQuery(id+"F0.wireOp",EDGE,"E88");
            var Q104;
            Q104=sQuery(id+"F0.wireOp",EDGE,"E1819");
            var Q105;
            Q105=sQuery(id+"F0.wireOp",EDGE,"E87");
            var Q106;
            Q106=sQuery(id+"F0.wireOp",EDGE,"E262");
            var Q107;
            Q107=sQuery(id+"F0.wireOp",EDGE,"E214");
            var Q108;
            Q108=sQuery(id+"F0.wireOp",EDGE,"E1485");
            var Q109;
            Q109=sQuery(id+"F0.wireOp",EDGE,"E261");
            var Q110;
            Q110=sQuery(id+"F0.wireOp",EDGE,"E181");
            var Q111;
            Q111=sQuery(id+"F0.wireOp",EDGE,"E1782");
            var Q112;
            Q112=sQuery(id+"F0.wireOp",EDGE,"E260");
            var Q113;
            Q113=sQuery(id+"F0.wireOp",EDGE,"E212");
            var Q114;
            Q114=sQuery(id+"F0.wireOp",EDGE,"E100");
            var Q115;
            Q115=sQuery(id+"F0.wireOp",EDGE,"E436");
            var Q116;
            Q116=sQuery(id+"F0.wireOp",EDGE,"E1139");
            var Q117;
            Q117=sQuery(id+"F0.wireOp",EDGE,"E1242");
            var Q118;
            Q118=sQuery(id+"F0.wireOp",EDGE,"E2122");
            var Q119;
            Q119=sQuery(id+"F0.wireOp",EDGE,"E1523");
            var Q120;
            Q120=sQuery(id+"F0.wireOp",EDGE,"E916");
            var Q121;
            Q121=sQuery(id+"F0.wireOp",EDGE,"E2121");
            var Q122;
            Q122=sQuery(id+"F0.wireOp",EDGE,"E259");
            var Q123;
            Q123=sQuery(id+"F0.wireOp",EDGE,"E179");
            var Q124;
            Q124=sQuery(id+"F0.wireOp",EDGE,"E2034");
            var Q125;
            Q125=sQuery(id+"F0.wireOp",EDGE,"E99");
            var Q126;
            Q126=sQuery(id+"F0.wireOp",EDGE,"E1298");
            var Q127;
            Q127=sQuery(id+"F0.wireOp",EDGE,"E1121");
            var Q128;
            Q128=sQuery(id+"F0.wireOp",EDGE,"E2065");
            var Q129;
            Q129=sQuery(id+"F0.wireOp",EDGE,"E146");
            var Q130;
            Q130=sQuery(id+"F0.wireOp",EDGE,"E2085");
            var Q131;
            Q131=sQuery(id+"F0.wireOp",EDGE,"E258");
            var Q132;
            Q132=sQuery(id+"F0.wireOp",EDGE,"E257");
            var Q133;
            Q133=sQuery(id+"F0.wireOp",EDGE,"E177");
            var Q134;
            Q134=sQuery(id+"F0.wireOp",EDGE,"E144");
            var Q135;
            Q135=sQuery(id+"F0.wireOp",EDGE,"E143");
            var Q136;
            Q136=sQuery(id+"F0.wireOp",EDGE,"E687");
            var Q137;
            Q137=sQuery(id+"F0.wireOp",EDGE,"E94");
            var Q138;
            Q138=sQuery(id+"F0.wireOp",EDGE,"E142");
            var Q139;
            Q139=sQuery(id+"F0.wireOp",EDGE,"E297");
            var Q140;
            Q140=sQuery(id+"F0.wireOp",EDGE,"E328");
            var Q141;
            Q141=sQuery(id+"F0.wireOp",EDGE,"E216");
            var Q142;
            Q142=sQuery(id+"F0.wireOp",EDGE,"E263");
            var Q143;
            Q143=sQuery(id+"F0.wireOp",EDGE,"E295");
            var Q144;
            Q144=sQuery(id+"F0.wireOp",EDGE,"E247");
            var Q145;
            Q145=sQuery(id+"F0.wireOp",EDGE,"E1325");
            var Q146;
            Q146=sQuery(id+"F0.wireOp",EDGE,"E1379");
            var Q147;
            Q147=sQuery(id+"F0.wireOp",EDGE,"E2090");
            var Q148;
            Q148=sQuery(id+"F0.wireOp",EDGE,"E483");
            var Q149;
            Q149=sQuery(id+"F0.wireOp",EDGE,"E1384");
            var Q150;
            Q150=sQuery(id+"F0.wireOp",EDGE,"E571");
            var Q151;
            Q151=sQuery(id+"F0.wireOp",EDGE,"E12");
            var Q152;
            Q152=sQuery(id+"F0.wireOp",EDGE,"E15");
            var Q153;
            Q153=sQuery(id+"F0.wireOp",EDGE,"E13");
            var Q154;
            Q154=sQuery(id+"F0.wireOp",EDGE,"E19");
            var Q155;
            Q155=sQuery(id+"F0.wireOp",EDGE,"E611");
            var Q156;
            Q156=sQuery(id+"F0.wireOp",EDGE,"E17");
            var Q157;
            Q157=sQuery(id+"F0.wireOp",EDGE,"E811");
            var Q158;
            Q158=sQuery(id+"F0.wireOp",EDGE,"E14");
            var Q159;
            Q159=sQuery(id+"F0.wireOp",EDGE,"E810");
            var Q160;
            Q160=sQuery(id+"F0.wireOp",EDGE,"E41");
            var Q161;
            Q161=sQuery(id+"F0.wireOp",EDGE,"E1663");
            var Q162;
            Q162=sQuery(id+"F0.wireOp",EDGE,"E72");
            var Q163;
            Q163=sQuery(id+"F0.wireOp",EDGE,"E104");
            var Q164;
            Q164=sQuery(id+"F0.wireOp",EDGE,"E71");
            var Q165;
            Q165=sQuery(id+"F0.wireOp",EDGE,"E38");
            var Q166;
            Q166=sQuery(id+"F0.wireOp",EDGE,"E54");
            var Q167;
            Q167=sQuery(id+"F0.wireOp",EDGE,"E70");
            var Q168;
            Q168=sQuery(id+"F0.wireOp",EDGE,"E806");
            var Q169;
            Q169=sQuery(id+"F0.wireOp",EDGE,"E213");
            var Q170;
            Q170=sQuery(id+"F0.wireOp",EDGE,"E37");
            var Q171;
            Q171=sQuery(id+"F0.wireOp",EDGE,"E53");
            var Q172;
            Q172=sQuery(id+"F0.wireOp",EDGE,"E69");
            var Q173;
            Q173=sQuery(id+"F0.wireOp",EDGE,"E180");
            var Q174;
            Q174=sQuery(id+"F0.wireOp",EDGE,"E1699");
            var Q175;
            Q175=sQuery(id+"F0.wireOp",EDGE,"E1658");
            var Q176;
            Q176=sQuery(id+"F0.wireOp",EDGE,"E1698");
            var Q177;
            Q177=sQuery(id+"F0.wireOp",EDGE,"E1665");
            var Q178;
            Q178=sQuery(id+"F0.wireOp",EDGE,"E1502");
            var Q179;
            Q179=sQuery(id+"F0.wireOp",EDGE,"E178");
            var Q180;
            Q180=sQuery(id+"F0.wireOp",EDGE,"E18");
            var Q181;
            Q181=sQuery(id+"F0.wireOp",EDGE,"E1664");
            var Q182;
            Q182=sQuery(id+"F0.wireOp",EDGE,"E1696");
            var Q183;
            Q183=sQuery(id+"F0.wireOp",EDGE,"E610");
            var Q184;
            Q184=sQuery(id+"F0.wireOp",EDGE,"E145");
            var Q185;
            Q185=sQuery(id+"F0.wireOp",EDGE,"E16");
            var Q186;
            Q186=sQuery(id+"F0.wireOp",EDGE,"E575");
            var Q187;
            Q187=sQuery(id+"F0.wireOp",EDGE,"E1022");
            var Q188;
            Q188=sQuery(id+"F0.wireOp",EDGE,"E477");
            var Q189;
            Q189=sQuery(id+"F0.wireOp",EDGE,"E1326");
            var Q190;
            Q190=sQuery(id+"F0.wireOp",EDGE,"E812");
            var Q191;
            Q191=sQuery(id+"F0.wireOp",EDGE,"E844");
            var Q192;
            Q192=sQuery(id+"F0.wireOp",EDGE,"E1660");
            var Q193;
            Q193=sQuery(id+"F0.wireOp",EDGE,"E843");
            var Q194;
            Q194=sQuery(id+"F0.wireOp",EDGE,"E570");
            var Q195;
            Q195=sQuery(id+"F0.wireOp",EDGE,"E442");
            var Q196;
            Q196=sQuery(id+"F0.wireOp",EDGE,"E441");
            var Q197;
            Q197=sQuery(id+"F0.wireOp",EDGE,"E809");
            var Q198;
            Q198=sQuery(id+"F0.wireOp",EDGE,"E808");
            var Q199;
            Q199=sQuery(id+"F0.wireOp",EDGE,"E40");
            var Q200;
            Q200=sQuery(id+"F0.wireOp",EDGE,"E1661");
            var Q201;
            Q201=sQuery(id+"F0.wireOp",EDGE,"E103");
            var Q202;
            Q202=sQuery(id+"F0.wireOp",EDGE,"E39");
            var Q203;
            Q203=sQuery(id+"F0.wireOp",EDGE,"E22");
            var Q204;
            Q204=sQuery(id+"F0.wireOp",EDGE,"E21");
            var Q205;
            Q205=sQuery(id+"F0.wireOp",EDGE,"E36");
            var Q206;
            Q206=sQuery(id+"F0.wireOp",EDGE,"E1697");
            var Q207;
            Q207=sQuery(id+"F0.wireOp",EDGE,"E1659");
            var Q208;
            Q208=sQuery(id+"F0.wireOp",EDGE,"E482");
            var Q209;
            Q209=sQuery(id+"F0.wireOp",EDGE,"E577");
            var Q210;
            Q210=sQuery(id+"F0.wireOp",EDGE,"E481");
            var Q211;
            Q211=sQuery(id+"F0.wireOp",EDGE,"E608");
            var Q212;
            Q212=sQuery(id+"F0.wireOp",EDGE,"E573");
            var Q213;
            Q213=sQuery(id+"F0.wireOp",EDGE,"E1021");
            var Q214;
            Q214=sQuery(id+"F0.wireOp",EDGE,"E845");
            var Q215;
            Q215=sQuery(id+"F0.wireOp",EDGE,"E1662");
            var Q216;
            Q216=sQuery(id+"F0.wireOp",EDGE,"E1072");
            var Q217;
            Q217=sQuery(id+"F0.wireOp",EDGE,"E1024");
            var Q218;
            Q218=sQuery(id+"F0.wireOp",EDGE,"E2223");
            var Q219;
            Q219=sQuery(id+"F0.wireOp",EDGE,"E2222");
            var Q220;
            Q220=sQuery(id+"F0.wireOp",EDGE,"E1071");
            var Q221;
            Q221=sQuery(id+"F0.wireOp",EDGE,"E1055");
            var Q222;
            Q222=sQuery(id+"F0.wireOp",EDGE,"E1070");
            var Q223;
            Q223=sQuery(id+"F0.wireOp",EDGE,"E1020");
            var Q224;
            Q224=sQuery(id+"F0.wireOp",EDGE,"E2485");
            var Q225;
            Q225=sQuery(id+"F0.wireOp",EDGE,"E76");
            var Q226;
            Q226=sQuery(id+"F0.wireOp",EDGE,"E108");
            var Q227;
            Q227=sQuery(id+"F0.wireOp",EDGE,"E28");
            var Q228;
            Q228=sQuery(id+"F0.wireOp",EDGE,"E1054");
            var Q229;
            Q229=sQuery(id+"F0.wireOp",EDGE,"E75");
            var Q230;
            Q230=sQuery(id+"F0.wireOp",EDGE,"E27");
            var Q231;
            Q231=sQuery(id+"F0.wireOp",EDGE,"E59");
            var Q232;
            Q232=sQuery(id+"F0.wireOp",EDGE,"E74");
            var Q233;
            Q233=sQuery(id+"F0.wireOp",EDGE,"E42");
            var Q234;
            Q234=sQuery(id+"F0.wireOp",EDGE,"E73");
            var Q235;
            Q235=sQuery(id+"F0.wireOp",EDGE,"E25");
            var Q236;
            Q236=sQuery(id+"F0.wireOp",EDGE,"E24");
            var Q237;
            Q237=sQuery(id+"F0.wireOp",EDGE,"E56");
            var Q238;
            Q238=sQuery(id+"F0.wireOp",EDGE,"E807");
            var Q239;
            Q239=sQuery(id+"F0.wireOp",EDGE,"E23");
            var Q240;
            Q240=sQuery(id+"F0.wireOp",EDGE,"E102");
            var Q241;
            Q241=sQuery(id+"F0.wireOp",EDGE,"E2245");
            var Q242;
            Q242=sQuery(id+"F0.wireOp",EDGE,"E805");
            var Q243;
            Q243=sQuery(id+"F0.wireOp",EDGE,"E68");
            var Q244;
            Q244=sQuery(id+"F0.wireOp",EDGE,"E2244");
            var Q245;
            Q245=sQuery(id+"F0.wireOp",EDGE,"E1043");
            var Q246;
            Q246=sQuery(id+"F0.wireOp",EDGE,"E2467");
            var Q247;
            Q247=sQuery(id+"F0.wireOp",EDGE,"E1498");
            var Q248;
            Q248=sQuery(id+"F0.wireOp",EDGE,"E2220");
            var Q249;
            Q249=sQuery(id+"F0.wireOp",EDGE,"E2233");
            var Q250;
            Q250=sQuery(id+"F0.wireOp",EDGE,"E1074");
            var Q251;
            Q251=sQuery(id+"F0.wireOp",EDGE,"E2221");
            var Q252;
            Q252=sQuery(id+"F0.wireOp",EDGE,"E35");
            var Q253;
            Q253=sQuery(id+"F0.wireOp",EDGE,"E2466");
            var Q254;
            Q254=sQuery(id+"F0.wireOp",EDGE,"E1497");
            var Q255;
            Q255=sQuery(id+"F0.wireOp",EDGE,"E2498");
            var Q256;
            Q256=sQuery(id+"F0.wireOp",EDGE,"E915");
            var Q257;
            Q257=sQuery(id+"F0.wireOp",EDGE,"E1073");
            var Q258;
            Q258=sQuery(id+"F0.wireOp",EDGE,"E1025");
            var Q259;
            Q259=sQuery(id+"F0.wireOp",EDGE,"E2465");
            var Q260;
            Q260=sQuery(id+"F0.wireOp",EDGE,"E2488");
            var Q261;
            Q261=sQuery(id+"F0.wireOp",EDGE,"E2225");
            var Q262;
            Q262=sQuery(id+"F0.wireOp",EDGE,"E2232");
            var Q263;
            Q263=sQuery(id+"F0.wireOp",EDGE,"E1068");
            var Q264;
            Q264=sQuery(id+"F0.wireOp",EDGE,"E98");
            var Q265;
            Q265=sQuery(id+"F0.wireOp",EDGE,"E34");
            var Q266;
            Q266=sQuery(id+"F0.wireOp",EDGE,"E66");
            var Q267;
            Q267=sQuery(id+"F0.wireOp",EDGE,"E2464");
            var Q268;
            Q268=sQuery(id+"F0.wireOp",EDGE,"E609");
            var Q269;
            Q269=sQuery(id+"F0.wireOp",EDGE,"E1069");
            var Q270;
            Q270=sQuery(id+"F0.wireOp",EDGE,"E97");
            var Q271;
            Q271=sQuery(id+"F0.wireOp",EDGE,"E33");
            var Q272;
            Q272=sQuery(id+"F0.wireOp",EDGE,"E2487");
            var Q273;
            Q273=sQuery(id+"F0.wireOp",EDGE,"E65");
            var Q274;
            Q274=sQuery(id+"F0.wireOp",EDGE,"E2468");
            var Q275;
            Q275=sQuery(id+"F0.wireOp",EDGE,"E1053");
            var Q276;
            Q276=sQuery(id+"F0.wireOp",EDGE,"E576");
            var Q277;
            Q277=sQuery(id+"F0.wireOp",EDGE,"E32");
            var Q278;
            Q278=sQuery(id+"F0.wireOp",EDGE,"E480");
            var Q279;
            Q279=sQuery(id+"F0.wireOp",EDGE,"E31");
            var Q280;
            Q280=sQuery(id+"F0.wireOp",EDGE,"E2256");
            var Q281;
            Q281=sQuery(id+"F0.wireOp",EDGE,"E30");
            var Q282;
            Q282=sQuery(id+"F0.wireOp",EDGE,"E109");
            var Q283;
            Q283=sQuery(id+"F0.wireOp",EDGE,"E141");
            var Q284;
            Q284=sQuery(id+"F0.wireOp",EDGE,"E29");
            var Q285;
            Q285=sQuery(id+"F0.wireOp",EDGE,"E45");
            var Q286;
            Q286=sQuery(id+"F0.wireOp",EDGE,"E2215");
            var Q287;
            Q287=sQuery(id+"F0.wireOp",EDGE,"E2224");
            var Q288;
            Q288=sQuery(id+"F0.wireOp",EDGE,"E1056");
            var Q289;
            Q289=sQuery(id+"F0.wireOp",EDGE,"E1040");
            var Q290;
            Q290=sQuery(id+"F0.wireOp",EDGE,"E2255");
            var Q291;
            Q291=sQuery(id+"F0.wireOp",EDGE,"E2254");
            var Q292;
            Q292=sQuery(id+"F0.wireOp",EDGE,"E1039");
            var Q293;
            Q293=sQuery(id+"F0.wireOp",EDGE,"E44");
            var Q294;
            Q294=sQuery(id+"F0.wireOp",EDGE,"E60");
            var Q295;
            Q295=sQuery(id+"F0.wireOp",EDGE,"E1500");
            var Q296;
            Q296=sQuery(id+"F0.wireOp",EDGE,"E1038");
            var Q297;
            Q297=sQuery(id+"F0.wireOp",EDGE,"E1019");
            var Q298;
            Q298=sQuery(id+"F0.wireOp",EDGE,"E7");
            var Q299;
            Q299=sQuery(id+"F0.wireOp",EDGE,"E107");
            var Q300;
            Q300=sQuery(id+"F0.wireOp",EDGE,"E43");
            var Q301;
            Q301=sQuery(id+"F0.wireOp",EDGE,"E3");
            var Q302;
            Q302=sQuery(id+"F0.wireOp",EDGE,"E2492");
            var Q303;
            Q303=sQuery(id+"F0.wireOp",EDGE,"E2453");
            var Q304;
            Q304=sQuery(id+"F0.wireOp",EDGE,"E26");
            var Q305;
            Q305=sQuery(id+"F0.wireOp",EDGE,"E2491");
            var Q306;
            Q306=sQuery(id+"F0.wireOp",EDGE,"E57");
            var Q307;
            Q307=sQuery(id+"F0.wireOp",EDGE,"E55");
            var Q308;
            Q308=sQuery(id+"F0.wireOp",EDGE,"E2495");
            var Q309;
            Q309=sQuery(id+"F0.wireOp",EDGE,"E101");
            var Q310;
            Q310=sQuery(id+"F0.wireOp",EDGE,"E1292");
            var Q311;
            Q311=sQuery(id+"F0.wireOp",EDGE,"E2458");
            var Q312;
            Q312=sQuery(id+"F0.wireOp",EDGE,"E2218");
            var Q313;
            Q313=sQuery(id+"F0.wireOp",EDGE,"E2067");
            var Q314;
            Q314=sQuery(id+"F0.wireOp",EDGE,"E2499");
            var Q315;
            Q315=sQuery(id+"F0.wireOp",EDGE,"E1012");
            var Q316;
            Q316=sQuery(id+"F0.wireOp",EDGE,"E2219");
            var Q317;
            Q317=sQuery(id+"F0.wireOp",EDGE,"E2212");
            var Q318;
            Q318=sQuery(id+"F0.wireOp",EDGE,"E2213");
            var Q319;
            Q319=sQuery(id+"F0.wireOp",EDGE,"E2217");
            var Q320;
            Q320=sQuery(id+"F0.wireOp",EDGE,"E2265");
            var Q321;
            Q321=sQuery(id+"F0.wireOp",EDGE,"E1042");
            var Q322;
            Q322=sQuery(id+"F0.wireOp",EDGE,"E2066");
            var Q323;
            Q323=sQuery(id+"F0.wireOp",EDGE,"E67");
            var Q324;
            Q324=sQuery(id+"F0.wireOp",EDGE,"E2489");
            var Q325;
            Q325=sQuery(id+"F0.wireOp",EDGE,"E2253");
            var Q326;
            Q326=sQuery(id+"F0.wireOp",EDGE,"E1057");
            var Q327;
            Q327=sQuery(id+"F0.wireOp",EDGE,"E1041");
            var Q328;
            Q328=sQuery(id+"F0.wireOp",EDGE,"E2033");
            var Q329;
            Q329=sQuery(id+"F0.wireOp",EDGE,"E2497");
            var Q330;
            Q330=sQuery(id+"F0.wireOp",EDGE,"E2252");
            var Q331;
            Q331=sQuery(id+"F0.wireOp",EDGE,"E2456");
            var Q332;
            Q332=sQuery(id+"F0.wireOp",EDGE,"E1297");
            var Q333;
            Q333=sQuery(id+"F0.wireOp",EDGE,"E2257");
            var Q334;
            Q334=sQuery(id+"F0.wireOp",EDGE,"E2216");
            var Q335;
            Q335=sQuery(id+"F0.wireOp",EDGE,"E2264");
            var Q336;
            Q336=sQuery(id+"F0.wireOp",EDGE,"E2248");
            var Q337;
            Q337=sQuery(id+"F0.wireOp",EDGE,"E2496");
            var Q338;
            Q338=sQuery(id+"F0.wireOp",EDGE,"E2494");
            var Q339;
            Q339=sQuery(id+"F0.wireOp",EDGE,"E1052");
            var Q340;
            Q340=sQuery(id+"F0.wireOp",EDGE,"E1036");
            var Q341;
            Q341=sQuery(id+"F0.wireOp",EDGE,"E2455");
            var Q342;
            Q342=sQuery(id+"F0.wireOp",EDGE,"E1037");
            var Q343;
            Q343=sQuery(id+"F0.wireOp",EDGE,"E2500");
            var Q344;
            Q344=sQuery(id+"F0.wireOp",EDGE,"E64");
            var Q345;
            Q345=sQuery(id+"F0.wireOp",EDGE,"E96");
            var Q346;
            Q346=sQuery(id+"F0.wireOp",EDGE,"E63");
            var Q347;
            Q347=sQuery(id+"F0.wireOp",EDGE,"E479");
            var Q348;
            Q348=sQuery(id+"F0.wireOp",EDGE,"E1023");
            var Q349;
            Q349=sQuery(id+"F0.wireOp",EDGE,"E110");
            var Q350;
            Q350=sQuery(id+"F0.wireOp",EDGE,"E62");
            var Q351;
            Q351=sQuery(id+"F0.wireOp",EDGE,"E574");
            var Q352;
            Q352=sQuery(id+"F0.wireOp",EDGE,"E846");
            var Q353;
            Q353=sQuery(id+"F0.wireOp",EDGE,"E77");
            var Q354;
            Q354=sQuery(id+"F0.wireOp",EDGE,"E61");
            var Q355;
            Q355=sQuery(id+"F0.wireOp",EDGE,"E2246");
            var Q356;
            Q356=sQuery(id+"F0.wireOp",EDGE,"E2214");
            var Q357;
            Q357=sQuery(id+"F0.wireOp",EDGE,"E2231");
            var Q358;
            Q358=sQuery(id+"F0.wireOp",EDGE,"E2070");
            var Q359;
            Q359=sQuery(id+"F0.wireOp",EDGE,"E2247");
            var Q360;
            Q360=sQuery(id+"F0.wireOp",EDGE,"E2238");
            var Q361;
            Q361=sQuery(id+"F0.wireOp",EDGE,"E2239");
            var Q362;
            Q362=sQuery(id+"F0.wireOp",EDGE,"E2207");
            var Q363;
            Q363=sQuery(id+"F0.wireOp",EDGE,"E2486");
            var Q364;
            Q364=sQuery(id+"F0.wireOp",EDGE,"E572");
            var Q365;
            Q365=sQuery(id+"F0.wireOp",EDGE,"E396");
            var Q366;
            Q366=sQuery(id+"F0.wireOp",EDGE,"E348");
            var Q367;
            Q367=sQuery(id+"F0.wireOp",EDGE,"E252");
            var Q368;
            Q368=sQuery(id+"F0.wireOp",EDGE,"E92");
            var Q369;
            Q369=sQuery(id+"F0.wireOp",EDGE,"E2469");
            var Q370;
            Q370=sQuery(id+"F0.wireOp",EDGE,"E347");
            var Q371;
            Q371=sQuery(id+"F0.wireOp",EDGE,"E11");
            var Q372;
            Q372=sQuery(id+"F0.wireOp",EDGE,"E91");
            var Q373;
            Q373=sQuery(id+"F0.wireOp",EDGE,"E6");
            var Q374;
            Q374=sQuery(id+"F0.wireOp",EDGE,"E2476");
            var Q375;
            Q375=sQuery(id+"F0.wireOp",EDGE,"E2");
            var Q376;
            Q376=sQuery(id+"F0.wireOp",EDGE,"E394");
            var Q377;
            Q377=sQuery(id+"F0.wireOp",EDGE,"E90");
            var Q378;
            Q378=sQuery(id+"F0.wireOp",EDGE,"E106");
            var Q379;
            Q379=sQuery(id+"F0.wireOp",EDGE,"E58");
            var Q380;
            Q380=sQuery(id+"F0.wireOp",EDGE,"E393");
            var Q381;
            Q381=sQuery(id+"F0.wireOp",EDGE,"E2460");
            var Q382;
            Q382=sQuery(id+"F0.wireOp",EDGE,"E392");
            var Q383;
            Q383=sQuery(id+"F0.wireOp",EDGE,"E2452");
            var Q384;
            Q384=sQuery(id+"F0.wireOp",EDGE,"E248");
            var Q385;
            Q385=sQuery(id+"F0.wireOp",EDGE,"E1016");
            var Q386;
            Q386=sQuery(id+"F0.wireOp",EDGE,"E391");
            var Q387;
            Q387=sQuery(id+"F0.wireOp",EDGE,"E215");
            var Q388;
            Q388=sQuery(id+"F0.wireOp",EDGE,"E2459");
            var Q389;
            Q389=sQuery(id+"F0.wireOp",EDGE,"E390");
            var Q390;
            Q390=sQuery(id+"F0.wireOp",EDGE,"E1501");
            var Q391;
            Q391=sQuery(id+"F0.wireOp",EDGE,"E1014");
            var Q392;
            Q392=sQuery(id+"F0.wireOp",EDGE,"E2477");
            var Q393;
            Q393=sQuery(id+"F0.wireOp",EDGE,"E2229");
            var Q394;
            Q394=sQuery(id+"F0.wireOp",EDGE,"E2261");
            var Q395;
            Q395=sQuery(id+"F0.wireOp",EDGE,"E2463");
            var Q396;
            Q396=sQuery(id+"F0.wireOp",EDGE,"E2236");
            var Q397;
            Q397=sQuery(id+"F0.wireOp",EDGE,"E52");
            var Q398;
            Q398=sQuery(id+"F0.wireOp",EDGE,"E644");
            var Q399;
            Q399=sQuery(id+"F0.wireOp",EDGE,"E2243");
            var Q400;
            Q400=sQuery(id+"F0.wireOp",EDGE,"E388");
            var Q401;
            Q401=sQuery(id+"F0.wireOp",EDGE,"E2227");
            var Q402;
            Q402=sQuery(id+"F0.wireOp",EDGE,"E2234");
            var Q403;
            Q403=sQuery(id+"F0.wireOp",EDGE,"E2250");
            var Q404;
            Q404=sQuery(id+"F0.wireOp",EDGE,"E1027");
            var Q405;
            Q405=sQuery(id+"F0.wireOp",EDGE,"E1050");
            var Q406;
            Q406=sQuery(id+"F0.wireOp",EDGE,"E2228");
            var Q407;
            Q407=sQuery(id+"F0.wireOp",EDGE,"E2490");
            var Q408;
            Q408=sQuery(id+"F0.wireOp",EDGE,"E2242");
            var Q409;
            Q409=sQuery(id+"F0.wireOp",EDGE,"E2226");
            var Q410;
            Q410=sQuery(id+"F0.wireOp",EDGE,"E1138");
            var Q411;
            Q411=sQuery(id+"F0.wireOp",EDGE,"E2249");
            var Q412;
            Q412=sQuery(id+"F0.wireOp",EDGE,"E2237");
            var Q413;
            Q413=sQuery(id+"F0.wireOp",EDGE,"E1026");
            var Q414;
            Q414=sQuery(id+"F0.wireOp",EDGE,"E1049");
            var Q415;
            Q415=sQuery(id+"F0.wireOp",EDGE,"E2251");
            var Q416;
            Q416=sQuery(id+"F0.wireOp",EDGE,"E51");
            var Q417;
            Q417=sQuery(id+"F0.wireOp",EDGE,"E2457");
            var Q418;
            Q418=sQuery(id+"F0.wireOp",EDGE,"E1048");
            var Q419;
            Q419=sQuery(id+"F0.wireOp",EDGE,"E1011");
            var Q420;
            Q420=sQuery(id+"F0.wireOp",EDGE,"E1029");
            var Q421;
            Q421=sQuery(id+"F0.wireOp",EDGE,"E2241");
            var Q422;
            Q422=sQuery(id+"F0.wireOp",EDGE,"E50");
            var Q423;
            Q423=sQuery(id+"F0.wireOp",EDGE,"E82");
            var Q424;
            Q424=sQuery(id+"F0.wireOp",EDGE,"E914");
            var Q425;
            Q425=sQuery(id+"F0.wireOp",EDGE,"E1047");
            var Q426;
            Q426=sQuery(id+"F0.wireOp",EDGE,"E386");
            var Q427;
            Q427=sQuery(id+"F0.wireOp",EDGE,"E2462");
            var Q428;
            Q428=sQuery(id+"F0.wireOp",EDGE,"E49");
            var Q429;
            Q429=sQuery(id+"F0.wireOp",EDGE,"E1044");
            var Q430;
            Q430=sQuery(id+"F0.wireOp",EDGE,"E48");
            var Q431;
            Q431=sQuery(id+"F0.wireOp",EDGE,"E95");
            var Q432;
            Q432=sQuery(id+"F0.wireOp",EDGE,"E47");
            var Q433;
            Q433=sQuery(id+"F0.wireOp",EDGE,"E2240");
            var Q434;
            Q434=sQuery(id+"F0.wireOp",EDGE,"E911");
            var Q435;
            Q435=sQuery(id+"F0.wireOp",EDGE,"E46");
            var Q436;
            Q436=sQuery(id+"F0.wireOp",EDGE,"E78");
            var Q437;
            Q437=sQuery(id+"F0.wireOp",EDGE,"E478");
            var Q438;
            Q438=sQuery(id+"F0.wireOp",EDGE,"E1051");
            var Q439;
            Q439=sQuery(id+"F0.wireOp",EDGE,"E2230");
            var Q440;
            Q440=sQuery(id+"F0.wireOp",EDGE,"E1046");
            var Q441;
            Q441=sQuery(id+"F0.wireOp",EDGE,"E2208");
            var Q442;
            Q442=sQuery(id+"F0.wireOp",EDGE,"E2263");
            var Q443;
            Q443=sQuery(id+"F0.wireOp",EDGE,"E268");
            var Q444;
            Q444=sQuery(id+"F0.wireOp",EDGE,"E2206");
            var Q445;
            Q445=sQuery(id+"F0.wireOp",EDGE,"E395");
            var Q446;
            Q446=sQuery(id+"F0.wireOp",EDGE,"E2454");
            var Q447;
            Q447=sQuery(id+"F0.wireOp",EDGE,"E2501");
            var Q448;
            Q448=sQuery(id+"F0.wireOp",EDGE,"E955");
            var Q449;
            Q449=sQuery(id+"F0.wireOp",EDGE,"E875");
            var Q450;
            Q450=sQuery(id+"F0.wireOp",EDGE,"E267");
            var Q451;
            Q451=sQuery(id+"F0.wireOp",EDGE,"E251");
            var Q452;
            Q452=sQuery(id+"F0.wireOp",EDGE,"E10");
            var Q453;
            Q453=sQuery(id+"F0.wireOp",EDGE,"E618");
            var Q454;
            Q454=sQuery(id+"F0.wireOp",EDGE,"E522");
            var Q455;
            Q455=sQuery(id+"F0.wireOp",EDGE,"E346");
            var Q456;
            Q456=sQuery(id+"F0.wireOp",EDGE,"E362");
            var Q457;
            Q457=sQuery(id+"F0.wireOp",EDGE,"E1018");
            var Q458;
            Q458=sQuery(id+"F0.wireOp",EDGE,"E266");
            var Q459;
            Q459=sQuery(id+"F0.wireOp",EDGE,"E954");
            var Q460;
            Q460=sQuery(id+"F0.wireOp",EDGE,"E537");
            var Q461;
            Q461=sQuery(id+"F0.wireOp",EDGE,"E265");
            var Q462;
            Q462=sQuery(id+"F0.wireOp",EDGE,"E1017");
            var Q463;
            Q463=sQuery(id+"F0.wireOp",EDGE,"E2445");
            var Q464;
            Q464=sQuery(id+"F0.wireOp",EDGE,"E360");
            var Q465;
            Q465=sQuery(id+"F0.wireOp",EDGE,"E2444");
            var Q466;
            Q466=sQuery(id+"F0.wireOp",EDGE,"E359");
            var Q467;
            Q467=sQuery(id+"F0.wireOp",EDGE,"E1015");
            var Q468;
            Q468=sQuery(id+"F0.wireOp",EDGE,"E2479");
            var Q469;
            Q469=sQuery(id+"F0.wireOp",EDGE,"E357");
            var Q470;
            Q470=sQuery(id+"F0.wireOp",EDGE,"E389");
            var Q471;
            Q471=sQuery(id+"F0.wireOp",EDGE,"E2493");
            var Q472;
            Q472=sQuery(id+"F0.wireOp",EDGE,"E1013");
            var Q473;
            Q473=sQuery(id+"F0.wireOp",EDGE,"E20");
            var Q474;
            Q474=sQuery(id+"F0.wireOp",EDGE,"E356");
            var Q475;
            Q475=sQuery(id+"F0.wireOp",EDGE,"E2259");
            var Q476;
            Q476=sQuery(id+"F0.wireOp",EDGE,"E2266");
            var Q477;
            Q477=sQuery(id+"F0.wireOp",EDGE,"E2211");
            var Q478;
            Q478=sQuery(id+"F0.wireOp",EDGE,"E1059");
            var Q479;
            Q479=sQuery(id+"F0.wireOp",EDGE,"E2483");
            var Q480;
            Q480=sQuery(id+"F0.wireOp",EDGE,"E2451");
            var Q481;
            Q481=sQuery(id+"F0.wireOp",EDGE,"E2260");
            var Q482;
            Q482=sQuery(id+"F0.wireOp",EDGE,"E1914");
            var Q483;
            Q483=sQuery(id+"F0.wireOp",EDGE,"E2258");
            var Q484;
            Q484=sQuery(id+"F0.wireOp",EDGE,"E2210");
            var Q485;
            Q485=sQuery(id+"F0.wireOp",EDGE,"E1058");
            var Q486;
            Q486=sQuery(id+"F0.wireOp",EDGE,"E2268");
            var Q487;
            Q487=sQuery(id+"F0.wireOp",EDGE,"E1913");
            var Q488;
            Q488=sQuery(id+"F0.wireOp",EDGE,"E1721");
            var Q489;
            Q489=sQuery(id+"F0.wireOp",EDGE,"E83");
            var Q490;
            Q490=sQuery(id+"F0.wireOp",EDGE,"E2482");
            var Q491;
            Q491=sQuery(id+"F0.wireOp",EDGE,"E355");
            var Q492;
            Q492=sQuery(id+"F0.wireOp",EDGE,"E387");
            var Q493;
            Q493=sQuery(id+"F0.wireOp",EDGE,"E2481");
            var Q494;
            Q494=sQuery(id+"F0.wireOp",EDGE,"E2205");
            var Q495;
            Q495=sQuery(id+"F0.wireOp",EDGE,"E1137");
            var Q496;
            Q496=sQuery(id+"F0.wireOp",EDGE,"E2209");
            var Q497;
            Q497=sQuery(id+"F0.wireOp",EDGE,"E2478");
            var Q498;
            Q498=sQuery(id+"F0.wireOp",EDGE,"E2480");
            var Q499;
            Q499=sQuery(id+"F0.wireOp",EDGE,"E1061");
            var Q500;
            Q500=sQuery(id+"F0.wireOp",EDGE,"E2069");
            var Q501;
            Q501=sQuery(id+"F0.wireOp",EDGE,"E354");
            var Q502;
            Q502=sQuery(id+"F0.wireOp",EDGE,"E81");
            var Q503;
            Q503=sQuery(id+"F0.wireOp",EDGE,"E913");
            var Q504;
            Q504=sQuery(id+"F0.wireOp",EDGE,"E2484");
            var Q505;
            Q505=sQuery(id+"F0.wireOp",EDGE,"E1499");
            var Q506;
            Q506=sQuery(id+"F0.wireOp",EDGE,"E385");
            var Q507;
            Q507=sQuery(id+"F0.wireOp",EDGE,"E80");
            var Q508;
            Q508=sQuery(id+"F0.wireOp",EDGE,"E256");
            var Q509;
            Q509=sQuery(id+"F0.wireOp",EDGE,"E79");
            var Q510;
            Q510=sQuery(id+"F0.wireOp",EDGE,"E910");
            var Q511;
            Q511=sQuery(id+"F0.wireOp",EDGE,"E93");
            var Q512;
            Q512=sQuery(id+"F0.wireOp",EDGE,"E349");
            var Q513;
            Q513=sQuery(id+"F0.wireOp",EDGE,"E1678");
            var Q514;
            Q514=sQuery(id+"F0.wireOp",EDGE,"E2262");
            var Q515;
            Q515=sQuery(id+"F0.wireOp",EDGE,"E1136");
            var Q516;
            Q516=sQuery(id+"F0.wireOp",EDGE,"E1062");
            var Q517;
            Q517=sQuery(id+"F0.wireOp",EDGE,"E2470");
            var Q518;
            Q518=sQuery(id+"F0.wireOp",EDGE,"E508");
            var Q519;
            Q519=sQuery(id+"F0.wireOp",EDGE,"E524");
            var Q520;
            Q520=sQuery(id+"F0.wireOp",EDGE,"E2438");
            var Q521;
            Q521=sQuery(id+"F0.wireOp",EDGE,"E876");
            var Q522;
            Q522=sQuery(id+"F0.wireOp",EDGE,"E364");
            var Q523;
            Q523=sQuery(id+"F0.wireOp",EDGE,"E300");
            var Q524;
            Q524=sQuery(id+"F0.wireOp",EDGE,"E1908");
            var Q525;
            Q525=sQuery(id+"F0.wireOp",EDGE,"E1676");
            var Q526;
            Q526=sQuery(id+"F0.wireOp",EDGE,"E779");
            var Q527;
            Q527=sQuery(id+"F0.wireOp",EDGE,"E523");
            var Q528;
            Q528=sQuery(id+"F0.wireOp",EDGE,"E331");
            var Q529;
            Q529=sQuery(id+"F0.wireOp",EDGE,"E5");
            var Q530;
            Q530=sQuery(id+"F0.wireOp",EDGE,"E1903");
            var Q531;
            Q531=sQuery(id+"F0.wireOp",EDGE,"E1");
            var Q532;
            Q532=sQuery(id+"F0.wireOp",EDGE,"E330");
            var Q533;
            Q533=sQuery(id+"F0.wireOp",EDGE,"E2461");
            var Q534;
            Q534=sQuery(id+"F0.wireOp",EDGE,"E874");
            var Q535;
            Q535=sQuery(id+"F0.wireOp",EDGE,"E250");
            var Q536;
            Q536=sQuery(id+"F0.wireOp",EDGE,"E2475");
            var Q537;
            Q537=sQuery(id+"F0.wireOp",EDGE,"E1915");
            var Q538;
            Q538=sQuery(id+"F0.wireOp",EDGE,"E361");
            var Q539;
            Q539=sQuery(id+"F0.wireOp",EDGE,"E313");
            var Q540;
            Q540=sQuery(id+"F0.wireOp",EDGE,"E777");
            var Q541;
            Q541=sQuery(id+"F0.wireOp",EDGE,"E1381");
            var Q542;
            Q542=sQuery(id+"F0.wireOp",EDGE,"E873");
            var Q543;
            Q543=sQuery(id+"F0.wireOp",EDGE,"E1679");
            var Q544;
            Q544=sQuery(id+"F0.wireOp",EDGE,"E440");
            var Q545;
            Q545=sQuery(id+"F0.wireOp",EDGE,"E264");
            var Q546;
            Q546=sQuery(id+"F0.wireOp",EDGE,"E776");
            var Q547;
            Q547=sQuery(id+"F0.wireOp",EDGE,"E952");
            var Q548;
            Q548=sQuery(id+"F0.wireOp",EDGE,"E327");
            var Q549;
            Q549=sQuery(id+"F0.wireOp",EDGE,"E1780");
            var Q550;
            Q550=sQuery(id+"F0.wireOp",EDGE,"E775");
            var Q551;
            Q551=sQuery(id+"F0.wireOp",EDGE,"E358");
            var Q552;
            Q552=sQuery(id+"F0.wireOp",EDGE,"E86");
            var Q553;
            Q553=sQuery(id+"F0.wireOp",EDGE,"E85");
            var Q554;
            Q554=sQuery(id+"F0.wireOp",EDGE,"E917");
            var Q555;
            Q555=sQuery(id+"F0.wireOp",EDGE,"E2447");
            var Q556;
            Q556=sQuery(id+"F0.wireOp",EDGE,"E2442");
            var Q557;
            Q557=sQuery(id+"F0.wireOp",EDGE,"E948");
            var Q558;
            Q558=sQuery(id+"F0.wireOp",EDGE,"E404");
            var Q559;
            Q559=sQuery(id+"F0.wireOp",EDGE,"E1066");
            var Q560;
            Q560=sQuery(id+"F0.wireOp",EDGE,"E1034");
            var Q561;
            Q561=sQuery(id+"F0.wireOp",EDGE,"E1779");
            var Q562;
            Q562=sQuery(id+"F0.wireOp",EDGE,"E1715");
            var Q563;
            Q563=sQuery(id+"F0.wireOp",EDGE,"E1731");
            var Q564;
            Q564=sQuery(id+"F0.wireOp",EDGE,"E1667");
            var Q565;
            Q565=sQuery(id+"F0.wireOp",EDGE,"E1674");
            var Q566;
            Q566=sQuery(id+"F0.wireOp",EDGE,"E1507");
            var Q567;
            Q567=sQuery(id+"F0.wireOp",EDGE,"E884");
            var Q568;
            Q568=sQuery(id+"F0.wireOp",EDGE,"E1907");
            var Q569;
            Q569=sQuery(id+"F0.wireOp",EDGE,"E2235");
            var Q570;
            Q570=sQuery(id+"F0.wireOp",EDGE,"E2089");
            var Q571;
            Q571=sQuery(id+"F0.wireOp",EDGE,"E1065");
            var Q572;
            Q572=sQuery(id+"F0.wireOp",EDGE,"E1033");
            var Q573;
            Q573=sQuery(id+"F0.wireOp",EDGE,"E1906");
            var Q574;
            Q574=sQuery(id+"F0.wireOp",EDGE,"E2473");
            var Q575;
            Q575=sQuery(id+"F0.wireOp",EDGE,"E2450");
            var Q576;
            Q576=sQuery(id+"F0.wireOp",EDGE,"E2370");
            var Q577;
            Q577=sQuery(id+"F0.wireOp",EDGE,"E1777");
            var Q578;
            Q578=sQuery(id+"F0.wireOp",EDGE,"E1720");
            var Q579;
            Q579=sQuery(id+"F0.wireOp",EDGE,"E1064");
            var Q580;
            Q580=sQuery(id+"F0.wireOp",EDGE,"E1028");
            var Q581;
            Q581=sQuery(id+"F0.wireOp",EDGE,"E1067");
            var Q582;
            Q582=sQuery(id+"F0.wireOp",EDGE,"E1505");
            var Q583;
            Q583=sQuery(id+"F0.wireOp",EDGE,"E2472");
            var Q584;
            Q584=sQuery(id+"F0.wireOp",EDGE,"E2449");
            var Q585;
            Q585=sQuery(id+"F0.wireOp",EDGE,"E850");
            var Q586;
            Q586=sQuery(id+"F0.wireOp",EDGE,"E1031");
            var Q587;
            Q587=sQuery(id+"F0.wireOp",EDGE,"E2068");
            var Q588;
            Q588=sQuery(id+"F0.wireOp",EDGE,"E1045");
            var Q589;
            Q589=sQuery(id+"F0.wireOp",EDGE,"E2471");
            var Q590;
            Q590=sQuery(id+"F0.wireOp",EDGE,"E2448");
            var Q591;
            Q591=sQuery(id+"F0.wireOp",EDGE,"E2446");
            var Q592;
            Q592=sQuery(id+"F0.wireOp",EDGE,"E353");
            var Q593;
            Q593=sQuery(id+"F0.wireOp",EDGE,"E1383");
            var Q594;
            Q594=sQuery(id+"F0.wireOp",EDGE,"E912");
            var Q595;
            Q595=sQuery(id+"F0.wireOp",EDGE,"E848");
            var Q596;
            Q596=sQuery(id+"F0.wireOp",EDGE,"E384");
            var Q597;
            Q597=sQuery(id+"F0.wireOp",EDGE,"E351");
            var Q598;
            Q598=sQuery(id+"F0.wireOp",EDGE,"E367");
            var Q599;
            Q599=sQuery(id+"F0.wireOp",EDGE,"E255");
            var Q600;
            Q600=sQuery(id+"F0.wireOp",EDGE,"E1820");
            var Q601;
            Q601=sQuery(id+"F0.wireOp",EDGE,"E847");
            var Q602;
            Q602=sQuery(id+"F0.wireOp",EDGE,"E350");
            var Q603;
            Q603=sQuery(id+"F0.wireOp",EDGE,"E1694");
            var Q604;
            Q604=sQuery(id+"F0.wireOp",EDGE,"E1932");
            var Q605;
            Q605=sQuery(id+"F0.wireOp",EDGE,"E397");
            var Q606;
            Q606=sQuery(id+"F0.wireOp",EDGE,"E1030");
            var Q607;
            Q607=sQuery(id+"F0.wireOp",EDGE,"E1063");
            var Q608;
            Q608=sQuery(id+"F0.wireOp",EDGE,"E1695");
            var Q609;
            Q609=sQuery(id+"F0.wireOp",EDGE,"E1686");
            var Q610;
            Q610=sQuery(id+"F0.wireOp",EDGE,"E1692");
            var Q611;
            Q611=sQuery(id+"F0.wireOp",EDGE,"E1670");
            var Q612;
            Q612=sQuery(id+"F0.wireOp",EDGE,"E1135");
            var Q613;
            Q613=sQuery(id+"F0.wireOp",EDGE,"E1405");
            var Q614;
            Q614=sQuery(id+"F0.wireOp",EDGE,"E1669");
            var Q615;
            Q615=sQuery(id+"F0.wireOp",EDGE,"E1525");
            var Q616;
            Q616=sQuery(id+"F0.wireOp",EDGE,"E892");
            var Q617;
            Q617=sQuery(id+"F0.wireOp",EDGE,"E908");
            var Q618;
            Q618=sQuery(id+"F0.wireOp",EDGE,"E332");
            var Q619;
            Q619=sQuery(id+"F0.wireOp",EDGE,"E316");
            var Q620;
            Q620=sQuery(id+"F0.wireOp",EDGE,"E891");
            var Q621;
            Q621=sQuery(id+"F0.wireOp",EDGE,"E363");
            var Q622;
            Q622=sQuery(id+"F0.wireOp",EDGE,"E299");
            var Q623;
            Q623=sQuery(id+"F0.wireOp",EDGE,"E315");
            var Q624;
            Q624=sQuery(id+"F0.wireOp",EDGE,"E4");
            var Q625;
            Q625=sQuery(id+"F0.wireOp",EDGE,"E1382");
            var Q626;
            Q626=sQuery(id+"F0.wireOp",EDGE,"E0");
            var Q627;
            Q627=sQuery(id+"F0.wireOp",EDGE,"E778");
            var Q628;
            Q628=sQuery(id+"F0.wireOp",EDGE,"E906");
            var Q629;
            Q629=sQuery(id+"F0.wireOp",EDGE,"E842");
            var Q630;
            Q630=sQuery(id+"F0.wireOp",EDGE,"E298");
            var Q631;
            Q631=sQuery(id+"F0.wireOp",EDGE,"E314");
            var Q632;
            Q632=sQuery(id+"F0.wireOp",EDGE,"E841");
            var Q633;
            Q633=sQuery(id+"F0.wireOp",EDGE,"E249");
            var Q634;
            Q634=sQuery(id+"F0.wireOp",EDGE,"E888");
            var Q635;
            Q635=sQuery(id+"F0.wireOp",EDGE,"E904");
            var Q636;
            Q636=sQuery(id+"F0.wireOp",EDGE,"E439");
            var Q637;
            Q637=sQuery(id+"F0.wireOp",EDGE,"E1677");
            var Q638;
            Q638=sQuery(id+"F0.wireOp",EDGE,"E1380");
            var Q639;
            Q639=sQuery(id+"F0.wireOp",EDGE,"E951");
            var Q640;
            Q640=sQuery(id+"F0.wireOp",EDGE,"E903");
            var Q641;
            Q641=sQuery(id+"F0.wireOp",EDGE,"E839");
            var Q642;
            Q642=sQuery(id+"F0.wireOp",EDGE,"E1471");
            var Q643;
            Q643=sQuery(id+"F0.wireOp",EDGE,"E2443");
            var Q644;
            Q644=sQuery(id+"F0.wireOp",EDGE,"E774");
            var Q645;
            Q645=sQuery(id+"F0.wireOp",EDGE,"E373");
            var Q646;
            Q646=sQuery(id+"F0.wireOp",EDGE,"E84");
            var Q647;
            Q647=sQuery(id+"F0.wireOp",EDGE,"E2362");
            var Q648;
            Q648=sQuery(id+"F0.wireOp",EDGE,"E580");
            var Q649;
            Q649=sQuery(id+"F0.wireOp",EDGE,"E1299");
            var Q650;
            Q650=sQuery(id+"F0.wireOp",EDGE,"E1690");
            var Q651;
            Q651=sQuery(id+"F0.wireOp",EDGE,"E1683");
            var Q652;
            Q652=sQuery(id+"F0.wireOp",EDGE,"E1619");
            var Q653;
            Q653=sQuery(id+"F0.wireOp",EDGE,"E1475");
            var Q654;
            Q654=sQuery(id+"F0.wireOp",EDGE,"E2474");
            var Q655;
            Q655=sQuery(id+"F0.wireOp",EDGE,"E1466");
            var Q656;
            Q656=sQuery(id+"F0.wireOp",EDGE,"E1778");
            var Q657;
            Q657=sQuery(id+"F0.wireOp",EDGE,"E1730");
            var Q658;
            Q658=sQuery(id+"F0.wireOp",EDGE,"E1923");
            var Q659;
            Q659=sQuery(id+"F0.wireOp",EDGE,"E1930");
            var Q660;
            Q660=sQuery(id+"F0.wireOp",EDGE,"E2267");
            var Q661;
            Q661=sQuery(id+"F0.wireOp",EDGE,"E1922");
            var Q662;
            Q662=sQuery(id+"F0.wireOp",EDGE,"E1929");
            var Q663;
            Q663=sQuery(id+"F0.wireOp",EDGE,"E1689");
            var Q664;
            Q664=sQuery(id+"F0.wireOp",EDGE,"E1666");
            var Q665;
            Q665=sQuery(id+"F0.wireOp",EDGE,"E1673");
            var Q666;
            Q666=sQuery(id+"F0.wireOp",EDGE,"E1506");
            var Q667;
            Q667=sQuery(id+"F0.wireOp",EDGE,"E1474");
            var Q668;
            Q668=sQuery(id+"F0.wireOp",EDGE,"E1931");
            var Q669;
            Q669=sQuery(id+"F0.wireOp",EDGE,"E2441");
            var Q670;
            Q670=sQuery(id+"F0.wireOp",EDGE,"E1681");
            var Q671;
            Q671=sQuery(id+"F0.wireOp",EDGE,"E1672");
            var Q672;
            Q672=sQuery(id+"F0.wireOp",EDGE,"E371");
            var Q673;
            Q673=sQuery(id+"F0.wireOp",EDGE,"E2088");
            var Q674;
            Q674=sQuery(id+"F0.wireOp",EDGE,"E1032");
            var Q675;
            Q675=sQuery(id+"F0.wireOp",EDGE,"E1912");
            var Q676;
            Q676=sQuery(id+"F0.wireOp",EDGE,"E1473");
            var Q677;
            Q677=sQuery(id+"F0.wireOp",EDGE,"E2440");
            var Q678;
            Q678=sQuery(id+"F0.wireOp",EDGE,"E2369");
            var Q679;
            Q679=sQuery(id+"F0.wireOp",EDGE,"E1060");
            var Q680;
            Q680=sQuery(id+"F0.wireOp",EDGE,"E1719");
            var Q681;
            Q681=sQuery(id+"F0.wireOp",EDGE,"E1680");
            var Q682;
            Q682=sQuery(id+"F0.wireOp",EDGE,"E1616");
            var Q683;
            Q683=sQuery(id+"F0.wireOp",EDGE,"E1504");
            var Q684;
            Q684=sQuery(id+"F0.wireOp",EDGE,"E1472");
            var Q685;
            Q685=sQuery(id+"F0.wireOp",EDGE,"E546");
            var Q686;
            Q686=sQuery(id+"F0.wireOp",EDGE,"E1920");
            var Q687;
            Q687=sQuery(id+"F0.wireOp",EDGE,"E370");
            var Q688;
            Q688=sQuery(id+"F0.wireOp",EDGE,"E1904");
            var Q689;
            Q689=sQuery(id+"F0.wireOp",EDGE,"E2439");
            var Q690;
            Q690=sQuery(id+"F0.wireOp",EDGE,"E849");
            var Q691;
            Q691=sQuery(id+"F0.wireOp",EDGE,"E1781");
            var Q692;
            Q692=sQuery(id+"F0.wireOp",EDGE,"E545");
            var Q693;
            Q693=sQuery(id+"F0.wireOp",EDGE,"E816");
            var Q694;
            Q694=sQuery(id+"F0.wireOp",EDGE,"E352");
            var Q695;
            Q695=sQuery(id+"F0.wireOp",EDGE,"E383");
            var Q696;
            Q696=sQuery(id+"F0.wireOp",EDGE,"E527");
            var Q697;
            Q697=sQuery(id+"F0.wireOp",EDGE,"E366");
            var Q698;
            Q698=sQuery(id+"F0.wireOp",EDGE,"E398");
            var Q699;
            Q699=sQuery(id+"F0.wireOp",EDGE,"E254");
            var Q700;
            Q700=sQuery(id+"F0.wireOp",EDGE,"E510");
            var Q701;
            Q701=sQuery(id+"F0.wireOp",EDGE,"E542");
            var Q702;
            Q702=sQuery(id+"F0.wireOp",EDGE,"E430");
            var Q703;
            Q703=sQuery(id+"F0.wireOp",EDGE,"E813");
            var Q704;
            Q704=sQuery(id+"F0.wireOp",EDGE,"E1035");
            var Q705;
            Q705=sQuery(id+"F0.wireOp",EDGE,"E1717");
            var Q706;
            Q706=sQuery(id+"F0.wireOp",EDGE,"E2087");
            var Q707;
            Q707=sQuery(id+"F0.wireOp",EDGE,"E1095");
            var Q708;
            Q708=sQuery(id+"F0.wireOp",EDGE,"E1590");
            var Q709;
            Q709=sQuery(id+"F0.wireOp",EDGE,"E1685");
            var Q710;
            Q710=sQuery(id+"F0.wireOp",EDGE,"E1606");
            var Q711;
            Q711=sQuery(id+"F0.wireOp",EDGE,"E1119");
            var Q712;
            Q712=sQuery(id+"F0.wireOp",EDGE,"E796");
            var Q713;
            Q713=sQuery(id+"F0.wireOp",EDGE,"E716");
            var Q714;
            Q714=sQuery(id+"F0.wireOp",EDGE,"E732");
            var Q715;
            Q715=sQuery(id+"F0.wireOp",EDGE,"E588");
            var Q716;
            Q716=sQuery(id+"F0.wireOp",EDGE,"E604");
            var Q717;
            Q717=sQuery(id+"F0.wireOp",EDGE,"E924");
            var Q718;
            Q718=sQuery(id+"F0.wireOp",EDGE,"E1118");
            var Q719;
            Q719=sQuery(id+"F0.wireOp",EDGE,"E284");
            var Q720;
            Q720=sQuery(id+"F0.wireOp",EDGE,"E731");
            var Q721;
            Q721=sQuery(id+"F0.wireOp",EDGE,"E587");
            var Q722;
            Q722=sQuery(id+"F0.wireOp",EDGE,"E603");
            var Q723;
            Q723=sQuery(id+"F0.wireOp",EDGE,"E1999");
            var Q724;
            Q724=sQuery(id+"F0.wireOp",EDGE,"E939");
            var Q725;
            Q725=sQuery(id+"F0.wireOp",EDGE,"E1452");
            var Q726;
            Q726=sQuery(id+"F0.wireOp",EDGE,"E907");
            var Q727;
            Q727=sQuery(id+"F0.wireOp",EDGE,"E2358");
            var Q728;
            Q728=sQuery(id+"F0.wireOp",EDGE,"E283");
            var Q729;
            Q729=sQuery(id+"F0.wireOp",EDGE,"E602");
            var Q730;
            Q730=sQuery(id+"F0.wireOp",EDGE,"E890");
            var Q731;
            Q731=sQuery(id+"F0.wireOp",EDGE,"E1998");
            var Q732;
            Q732=sQuery(id+"F0.wireOp",EDGE,"E282");
            var Q733;
            Q733=sQuery(id+"F0.wireOp",EDGE,"E1918");
            var Q734;
            Q734=sQuery(id+"F0.wireOp",EDGE,"E585");
            var Q735;
            Q735=sQuery(id+"F0.wireOp",EDGE,"E521");
            var Q736;
            Q736=sQuery(id+"F0.wireOp",EDGE,"E281");
            var Q737;
            Q737=sQuery(id+"F0.wireOp",EDGE,"E729");
            var Q738;
            Q738=sQuery(id+"F0.wireOp",EDGE,"E1693");
            var Q739;
            Q739=sQuery(id+"F0.wireOp",EDGE,"E905");
            var Q740;
            Q740=sQuery(id+"F0.wireOp",EDGE,"E584");
            var Q741;
            Q741=sQuery(id+"F0.wireOp",EDGE,"E600");
            var Q742;
            Q742=sQuery(id+"F0.wireOp",EDGE,"E520");
            var Q743;
            Q743=sQuery(id+"F0.wireOp",EDGE,"E536");
            var Q744;
            Q744=sQuery(id+"F0.wireOp",EDGE,"E312");
            var Q745;
            Q745=sQuery(id+"F0.wireOp",EDGE,"E1917");
            var Q746;
            Q746=sQuery(id+"F0.wireOp",EDGE,"E872");
            var Q747;
            Q747=sQuery(id+"F0.wireOp",EDGE,"E840");
            var Q748;
            Q748=sQuery(id+"F0.wireOp",EDGE,"E519");
            var Q749;
            Q749=sQuery(id+"F0.wireOp",EDGE,"E535");
            var Q750;
            Q750=sQuery(id+"F0.wireOp",EDGE,"E1615");
            var Q751;
            Q751=sQuery(id+"F0.wireOp",EDGE,"E2364");
            var Q752;
            Q752=sQuery(id+"F0.wireOp",EDGE,"E2365");
            var Q753;
            Q753=sQuery(id+"F0.wireOp",EDGE,"E1599");
            var Q754;
            Q754=sQuery(id+"F0.wireOp",EDGE,"E583");
            var Q755;
            Q755=sQuery(id+"F0.wireOp",EDGE,"E599");
            var Q756;
            Q756=sQuery(id+"F0.wireOp",EDGE,"E1503");
            var Q757;
            Q757=sQuery(id+"F0.wireOp",EDGE,"E919");
            var Q758;
            Q758=sQuery(id+"F0.wireOp",EDGE,"E871");
            var Q759;
            Q759=sQuery(id+"F0.wireOp",EDGE,"E887");
            var Q760;
            Q760=sQuery(id+"F0.wireOp",EDGE,"E326");
            var Q761;
            Q761=sQuery(id+"F0.wireOp",EDGE,"E790");
            var Q762;
            Q762=sQuery(id+"F0.wireOp",EDGE,"E742");
            var Q763;
            Q763=sQuery(id+"F0.wireOp",EDGE,"E598");
            var Q764;
            Q764=sQuery(id+"F0.wireOp",EDGE,"E518");
            var Q765;
            Q765=sQuery(id+"F0.wireOp",EDGE,"E534");
            var Q766;
            Q766=sQuery(id+"F0.wireOp",EDGE,"E438");
            var Q767;
            Q767=sQuery(id+"F0.wireOp",EDGE,"E950");
            var Q768;
            Q768=sQuery(id+"F0.wireOp",EDGE,"E902");
            var Q769;
            Q769=sQuery(id+"F0.wireOp",EDGE,"E838");
            var Q770;
            Q770=sQuery(id+"F0.wireOp",EDGE,"E870");
            var Q771;
            Q771=sQuery(id+"F0.wireOp",EDGE,"E1407");
            var Q772;
            Q772=sQuery(id+"F0.wireOp",EDGE,"E581");
            var Q773;
            Q773=sQuery(id+"F0.wireOp",EDGE,"E533");
            var Q774;
            Q774=sQuery(id+"F0.wireOp",EDGE,"E869");
            var Q775;
            Q775=sQuery(id+"F0.wireOp",EDGE,"E2371");
            var Q776;
            Q776=sQuery(id+"F0.wireOp",EDGE,"E308");
            var Q777;
            Q777=sQuery(id+"F0.wireOp",EDGE,"E1386");
            var Q778;
            Q778=sQuery(id+"F0.wireOp",EDGE,"E2367");
            var Q779;
            Q779=sQuery(id+"F0.wireOp",EDGE,"E516");
            var Q780;
            Q780=sQuery(id+"F0.wireOp",EDGE,"E532");
            var Q781;
            Q781=sQuery(id+"F0.wireOp",EDGE,"E372");
            var Q782;
            Q782=sQuery(id+"F0.wireOp",EDGE,"E1306");
            var Q783;
            Q783=sQuery(id+"F0.wireOp",EDGE,"E1235");
            var Q784;
            Q784=sQuery(id+"F0.wireOp",EDGE,"E2051");
            var Q785;
            Q785=sQuery(id+"F0.wireOp",EDGE,"E1114");
            var Q786;
            Q786=sQuery(id+"F0.wireOp",EDGE,"E2003");
            var Q787;
            Q787=sQuery(id+"F0.wireOp",EDGE,"E723");
            var Q788;
            Q788=sQuery(id+"F0.wireOp",EDGE,"E1587");
            var Q789;
            Q789=sQuery(id+"F0.wireOp",EDGE,"E1603");
            var Q790;
            Q790=sQuery(id+"F0.wireOp",EDGE,"E1610");
            var Q791;
            Q791=sQuery(id+"F0.wireOp",EDGE,"E1594");
            var Q792;
            Q792=sQuery(id+"F0.wireOp",EDGE,"E1539");
            var Q793;
            Q793=sQuery(id+"F0.wireOp",EDGE,"E1530");
            var Q794;
            Q794=sQuery(id+"F0.wireOp",EDGE,"E932");
            var Q795;
            Q795=sQuery(id+"F0.wireOp",EDGE,"E1411");
            var Q796;
            Q796=sQuery(id+"F0.wireOp",EDGE,"E1714");
            var Q797;
            Q797=sQuery(id+"F0.wireOp",EDGE,"E1875");
            var Q798;
            Q798=sQuery(id+"F0.wireOp",EDGE,"E1866");
            var Q799;
            Q799=sQuery(id+"F0.wireOp",EDGE,"E1234");
            var Q800;
            Q800=sQuery(id+"F0.wireOp",EDGE,"E1113");
            var Q801;
            Q801=sQuery(id+"F0.wireOp",EDGE,"E1691");
            var Q802;
            Q802=sQuery(id+"F0.wireOp",EDGE,"E1874");
            var Q803;
            Q803=sQuery(id+"F0.wireOp",EDGE,"E1682");
            var Q804;
            Q804=sQuery(id+"F0.wireOp",EDGE,"E1586");
            var Q805;
            Q805=sQuery(id+"F0.wireOp",EDGE,"E1618");
            var Q806;
            Q806=sQuery(id+"F0.wireOp",EDGE,"E1602");
            var Q807;
            Q807=sQuery(id+"F0.wireOp",EDGE,"E1522");
            var Q808;
            Q808=sQuery(id+"F0.wireOp",EDGE,"E1593");
            var Q809;
            Q809=sQuery(id+"F0.wireOp",EDGE,"E1609");
            var Q810;
            Q810=sQuery(id+"F0.wireOp",EDGE,"E1529");
            var Q811;
            Q811=sQuery(id+"F0.wireOp",EDGE,"E947");
            var Q812;
            Q812=sQuery(id+"F0.wireOp",EDGE,"E1718");
            var Q813;
            Q813=sQuery(id+"F0.wireOp",EDGE,"E931");
            var Q814;
            Q814=sQuery(id+"F0.wireOp",EDGE,"E2361");
            var Q815;
            Q815=sQuery(id+"F0.wireOp",EDGE,"E579");
            var Q816;
            Q816=sQuery(id+"F0.wireOp",EDGE,"E595");
            var Q817;
            Q817=sQuery(id+"F0.wireOp",EDGE,"E1688");
            var Q818;
            Q818=sQuery(id+"F0.wireOp",EDGE,"E1585");
            var Q819;
            Q819=sQuery(id+"F0.wireOp",EDGE,"E1601");
            var Q820;
            Q820=sQuery(id+"F0.wireOp",EDGE,"E515");
            var Q821;
            Q821=sQuery(id+"F0.wireOp",EDGE,"E2049");
            var Q822;
            Q822=sQuery(id+"F0.wireOp",EDGE,"E1921");
            var Q823;
            Q823=sQuery(id+"F0.wireOp",EDGE,"E1873");
            var Q824;
            Q824=sQuery(id+"F0.wireOp",EDGE,"E1928");
            var Q825;
            Q825=sQuery(id+"F0.wireOp",EDGE,"E1905");
            var Q826;
            Q826=sQuery(id+"F0.wireOp",EDGE,"E1880");
            var Q827;
            Q827=sQuery(id+"F0.wireOp",EDGE,"E1592");
            var Q828;
            Q828=sQuery(id+"F0.wireOp",EDGE,"E1537");
            var Q829;
            Q829=sQuery(id+"F0.wireOp",EDGE,"E1409");
            var Q830;
            Q830=sQuery(id+"F0.wireOp",EDGE,"E867");
            var Q831;
            Q831=sQuery(id+"F0.wireOp",EDGE,"E1304");
            var Q832;
            Q832=sQuery(id+"F0.wireOp",EDGE,"E1584");
            var Q833;
            Q833=sQuery(id+"F0.wireOp",EDGE,"E1735");
            var Q834;
            Q834=sQuery(id+"F0.wireOp",EDGE,"E1687");
            var Q835;
            Q835=sQuery(id+"F0.wireOp",EDGE,"E1671");
            var Q836;
            Q836=sQuery(id+"F0.wireOp",EDGE,"E1607");
            var Q837;
            Q837=sQuery(id+"F0.wireOp",EDGE,"E1116");
            var Q838;
            Q838=sQuery(id+"F0.wireOp",EDGE,"E866");
            var Q839;
            Q839=sQuery(id+"F0.wireOp",EDGE,"E578");
            var Q840;
            Q840=sQuery(id+"F0.wireOp",EDGE,"E594");
            var Q841;
            Q841=sQuery(id+"F0.wireOp",EDGE,"E530");
            var Q842;
            Q842=sQuery(id+"F0.wireOp",EDGE,"E1911");
            var Q843;
            Q843=sQuery(id+"F0.wireOp",EDGE,"E306");
            var Q844;
            Q844=sQuery(id+"F0.wireOp",EDGE,"E1524");
            var Q845;
            Q845=sQuery(id+"F0.wireOp",EDGE,"E1479");
            var Q846;
            Q846=sQuery(id+"F0.wireOp",EDGE,"E1463");
            var Q847;
            Q847=sQuery(id+"F0.wireOp",EDGE,"E897");
            var Q848;
            Q848=sQuery(id+"F0.wireOp",EDGE,"E1101");
            var Q849;
            Q849=sQuery(id+"F0.wireOp",EDGE,"E2368");
            var Q850;
            Q850=sQuery(id+"F0.wireOp",EDGE,"E833");
            var Q851;
            Q851=sQuery(id+"F0.wireOp",EDGE,"E529");
            var Q852;
            Q852=sQuery(id+"F0.wireOp",EDGE,"E513");
            var Q853;
            Q853=sQuery(id+"F0.wireOp",EDGE,"E1296");
            var Q854;
            Q854=sQuery(id+"F0.wireOp",EDGE,"E369");
            var Q855;
            Q855=sQuery(id+"F0.wireOp",EDGE,"E2359");
            var Q856;
            Q856=sQuery(id+"F0.wireOp",EDGE,"E512");
            var Q857;
            Q857=sQuery(id+"F0.wireOp",EDGE,"E528");
            var Q858;
            Q858=sQuery(id+"F0.wireOp",EDGE,"E544");
            var Q859;
            Q859=sQuery(id+"F0.wireOp",EDGE,"E864");
            var Q860;
            Q860=sQuery(id+"F0.wireOp",EDGE,"E448");
            var Q861;
            Q861=sQuery(id+"F0.wireOp",EDGE,"E368");
            var Q862;
            Q862=sQuery(id+"F0.wireOp",EDGE,"E336");
            var Q863;
            Q863=sQuery(id+"F0.wireOp",EDGE,"E1996");
            var Q864;
            Q864=sQuery(id+"F0.wireOp",EDGE,"E1916");
            var Q865;
            Q865=sQuery(id+"F0.wireOp",EDGE,"E815");
            var Q866;
            Q866=sQuery(id+"F0.wireOp",EDGE,"E511");
            var Q867;
            Q867=sQuery(id+"F0.wireOp",EDGE,"E334");
            var Q868;
            Q868=sQuery(id+"F0.wireOp",EDGE,"E526");
            var Q869;
            Q869=sQuery(id+"F0.wireOp",EDGE,"E942");
            var Q870;
            Q870=sQuery(id+"F0.wireOp",EDGE,"E317");
            var Q871;
            Q871=sQuery(id+"F0.wireOp",EDGE,"E253");
            var Q872;
            Q872=sQuery(id+"F0.wireOp",EDGE,"E269");
            var Q873;
            Q873=sQuery(id+"F0.wireOp",EDGE,"E525");
            var Q874;
            Q874=sQuery(id+"F0.wireOp",EDGE,"E509");
            var Q875;
            Q875=sQuery(id+"F0.wireOp",EDGE,"E1868");
            var Q876;
            Q876=sQuery(id+"F0.wireOp",EDGE,"E365");
            var Q877;
            Q877=sQuery(id+"F0.wireOp",EDGE,"E2086");
            var Q878;
            Q878=sQuery(id+"F0.wireOp",EDGE,"E1924");
            var Q879;
            Q879=sQuery(id+"F0.wireOp",EDGE,"E2176");
            var Q880;
            Q880=sQuery(id+"F0.wireOp",EDGE,"E1926");
            var Q881;
            Q881=sQuery(id+"F0.wireOp",EDGE,"E2151");
            var Q882;
            Q882=sQuery(id+"F0.wireOp",EDGE,"E1910");
            var Q883;
            Q883=sQuery(id+"F0.wireOp",EDGE,"E1120");
            var Q884;
            Q884=sQuery(id+"F0.wireOp",EDGE,"E2048");
            var Q885;
            Q885=sQuery(id+"F0.wireOp",EDGE,"E1733");
            var Q886;
            Q886=sQuery(id+"F0.wireOp",EDGE,"E1526");
            var Q887;
            Q887=sQuery(id+"F0.wireOp",EDGE,"E1103");
            var Q888;
            Q888=sQuery(id+"F0.wireOp",EDGE,"E1478");
            var Q889;
            Q889=sQuery(id+"F0.wireOp",EDGE,"E828");
            var Q890;
            Q890=sQuery(id+"F0.wireOp",EDGE,"E748");
            var Q891;
            Q891=sQuery(id+"F0.wireOp",EDGE,"E780");
            var Q892;
            Q892=sQuery(id+"F0.wireOp",EDGE,"E1894");
            var Q893;
            Q893=sQuery(id+"F0.wireOp",EDGE,"E668");
            var Q894;
            Q894=sQuery(id+"F0.wireOp",EDGE,"E556");
            var Q895;
            Q895=sQuery(id+"F0.wireOp",EDGE,"E460");
            var Q896;
            Q896=sQuery(id+"F0.wireOp",EDGE,"E2174");
            var Q897;
            Q897=sQuery(id+"F0.wireOp",EDGE,"E940");
            var Q898;
            Q898=sQuery(id+"F0.wireOp",EDGE,"E860");
            var Q899;
            Q899=sQuery(id+"F0.wireOp",EDGE,"E1612");
            var Q900;
            Q900=sQuery(id+"F0.wireOp",EDGE,"E1557");
            var Q901;
            Q901=sQuery(id+"F0.wireOp",EDGE,"E1102");
            var Q902;
            Q902=sQuery(id+"F0.wireOp",EDGE,"E380");
            var Q903;
            Q903=sQuery(id+"F0.wireOp",EDGE,"E140");
            var Q904;
            Q904=sQuery(id+"F0.wireOp",EDGE,"E1461");
            var Q905;
            Q905=sQuery(id+"F0.wireOp",EDGE,"E747");
            var Q906;
            Q906=sQuery(id+"F0.wireOp",EDGE,"E795");
            var Q907;
            Q907=sQuery(id+"F0.wireOp",EDGE,"E715");
            var Q908;
            Q908=sQuery(id+"F0.wireOp",EDGE,"E667");
            var Q909;
            Q909=sQuery(id+"F0.wireOp",EDGE,"E555");
            var Q910;
            Q910=sQuery(id+"F0.wireOp",EDGE,"E923");
            var Q911;
            Q911=sQuery(id+"F0.wireOp",EDGE,"E1477");
            var Q912;
            Q912=sQuery(id+"F0.wireOp",EDGE,"E859");
            var Q913;
            Q913=sQuery(id+"F0.wireOp",EDGE,"E1919");
            var Q914;
            Q914=sQuery(id+"F0.wireOp",EDGE,"E379");
            var Q915;
            Q915=sQuery(id+"F0.wireOp",EDGE,"E9");
            var Q916;
            Q916=sQuery(id+"F0.wireOp",EDGE,"E1484");
            var Q917;
            Q917=sQuery(id+"F0.wireOp",EDGE,"E730");
            var Q918;
            Q918=sQuery(id+"F0.wireOp",EDGE,"E1468");
            var Q919;
            Q919=sQuery(id+"F0.wireOp",EDGE,"E554");
            var Q920;
            Q920=sQuery(id+"F0.wireOp",EDGE,"E586");
            var Q921;
            Q921=sQuery(id+"F0.wireOp",EDGE,"E378");
            var Q922;
            Q922=sQuery(id+"F0.wireOp",EDGE,"E746");
            var Q923;
            Q923=sQuery(id+"F0.wireOp",EDGE,"E794");
            var Q924;
            Q924=sQuery(id+"F0.wireOp",EDGE,"E922");
            var Q925;
            Q925=sQuery(id+"F0.wireOp",EDGE,"E938");
            var Q926;
            Q926=sQuery(id+"F0.wireOp",EDGE,"E553");
            var Q927;
            Q927=sQuery(id+"F0.wireOp",EDGE,"E601");
            var Q928;
            Q928=sQuery(id+"F0.wireOp",EDGE,"E345");
            var Q929;
            Q929=sQuery(id+"F0.wireOp",EDGE,"E377");
            var Q930;
            Q930=sQuery(id+"F0.wireOp",EDGE,"E793");
            var Q931;
            Q931=sQuery(id+"F0.wireOp",EDGE,"E713");
            var Q932;
            Q932=sQuery(id+"F0.wireOp",EDGE,"E1302");
            var Q933;
            Q933=sQuery(id+"F0.wireOp",EDGE,"E937");
            var Q934;
            Q934=sQuery(id+"F0.wireOp",EDGE,"E857");
            var Q935;
            Q935=sQuery(id+"F0.wireOp",EDGE,"E889");
            var Q936;
            Q936=sQuery(id+"F0.wireOp",EDGE,"E376");
            var Q937;
            Q937=sQuery(id+"F0.wireOp",EDGE,"E280");
            var Q938;
            Q938=sQuery(id+"F0.wireOp",EDGE,"E744");
            var Q939;
            Q939=sQuery(id+"F0.wireOp",EDGE,"E712");
            var Q940;
            Q940=sQuery(id+"F0.wireOp",EDGE,"E792");
            var Q941;
            Q941=sQuery(id+"F0.wireOp",EDGE,"E728");
            var Q942;
            Q942=sQuery(id+"F0.wireOp",EDGE,"E1583");
            var Q943;
            Q943=sQuery(id+"F0.wireOp",EDGE,"E2372");
            var Q944;
            Q944=sQuery(id+"F0.wireOp",EDGE,"E920");
            var Q945;
            Q945=sQuery(id+"F0.wireOp",EDGE,"E856");
            var Q946;
            Q946=sQuery(id+"F0.wireOp",EDGE,"E2356");
            var Q947;
            Q947=sQuery(id+"F0.wireOp",EDGE,"E375");
            var Q948;
            Q948=sQuery(id+"F0.wireOp",EDGE,"E279");
            var Q949;
            Q949=sQuery(id+"F0.wireOp",EDGE,"E311");
            var Q950;
            Q950=sQuery(id+"F0.wireOp",EDGE,"E1387");
            var Q951;
            Q951=sQuery(id+"F0.wireOp",EDGE,"E743");
            var Q952;
            Q952=sQuery(id+"F0.wireOp",EDGE,"E2348");
            var Q953;
            Q953=sQuery(id+"F0.wireOp",EDGE,"E791");
            var Q954;
            Q954=sQuery(id+"F0.wireOp",EDGE,"E551");
            var Q955;
            Q955=sQuery(id+"F0.wireOp",EDGE,"E855");
            var Q956;
            Q956=sQuery(id+"F0.wireOp",EDGE,"E374");
            var Q957;
            Q957=sQuery(id+"F0.wireOp",EDGE,"E310");
            var Q958;
            Q958=sQuery(id+"F0.wireOp",EDGE,"E1301");
            var Q959;
            Q959=sQuery(id+"F0.wireOp",EDGE,"E1870");
            var Q960;
            Q960=sQuery(id+"F0.wireOp",EDGE,"E2381");
            var Q961;
            Q961=sQuery(id+"F0.wireOp",EDGE,"E1716");
            var Q962;
            Q962=sQuery(id+"F0.wireOp",EDGE,"E278");
            var Q963;
            Q963=sQuery(id+"F0.wireOp",EDGE,"E710");
            var Q964;
            Q964=sQuery(id+"F0.wireOp",EDGE,"E582");
            var Q965;
            Q965=sQuery(id+"F0.wireOp",EDGE,"E454");
            var Q966;
            Q966=sQuery(id+"F0.wireOp",EDGE,"E886");
            var Q967;
            Q967=sQuery(id+"F0.wireOp",EDGE,"E918");
            var Q968;
            Q968=sQuery(id+"F0.wireOp",EDGE,"E934");
            var Q969;
            Q969=sQuery(id+"F0.wireOp",EDGE,"E1533");
            var Q970;
            Q970=sQuery(id+"F0.wireOp",EDGE,"E854");
            var Q971;
            Q971=sQuery(id+"F0.wireOp",EDGE,"E1453");
            var Q972;
            Q972=sQuery(id+"F0.wireOp",EDGE,"E309");
            var Q973;
            Q973=sQuery(id+"F0.wireOp",EDGE,"E325");
            var Q974;
            Q974=sQuery(id+"F0.wireOp",EDGE,"E277");
            var Q975;
            Q975=sQuery(id+"F0.wireOp",EDGE,"E789");
            var Q976;
            Q976=sQuery(id+"F0.wireOp",EDGE,"E709");
            var Q977;
            Q977=sQuery(id+"F0.wireOp",EDGE,"E725");
            var Q978;
            Q978=sQuery(id+"F0.wireOp",EDGE,"E741");
            var Q979;
            Q979=sQuery(id+"F0.wireOp",EDGE,"E597");
            var Q980;
            Q980=sQuery(id+"F0.wireOp",EDGE,"E517");
            var Q981;
            Q981=sQuery(id+"F0.wireOp",EDGE,"E549");
            var Q982;
            Q982=sQuery(id+"F0.wireOp",EDGE,"E437");
            var Q983;
            Q983=sQuery(id+"F0.wireOp",EDGE,"E949");
            var Q984;
            Q984=sQuery(id+"F0.wireOp",EDGE,"E901");
            var Q985;
            Q985=sQuery(id+"F0.wireOp",EDGE,"E837");
            var Q986;
            Q986=sQuery(id+"F0.wireOp",EDGE,"E853");
            var Q987;
            Q987=sQuery(id+"F0.wireOp",EDGE,"E324");
            var Q988;
            Q988=sQuery(id+"F0.wireOp",EDGE,"E2410");
            var Q989;
            Q989=sQuery(id+"F0.wireOp",EDGE,"E2355");
            var Q990;
            Q990=sQuery(id+"F0.wireOp",EDGE,"E116");
            var Q991;
            Q991=sQuery(id+"F0.wireOp",EDGE,"E724");
            var Q992;
            Q992=sQuery(id+"F0.wireOp",EDGE,"E2346");
            var Q993;
            Q993=sQuery(id+"F0.wireOp",EDGE,"E2179");
            var Q994;
            Q994=sQuery(id+"F0.wireOp",EDGE,"E1075");
            var Q995;
            Q995=sQuery(id+"F0.wireOp",EDGE,"E2154");
            var Q996;
            Q996=sQuery(id+"F0.wireOp",EDGE,"E2186");
            var Q997;
            Q997=sQuery(id+"F0.wireOp",EDGE,"E1098");
            var Q998;
            Q998=sQuery(id+"F0.wireOp",EDGE,"E2058");
            var Q999;
            Q999=sQuery(id+"F0.wireOp",EDGE,"E755");
            var Q1000;
            Q1000=sQuery(id+"F0.wireOp",EDGE,"E1555");
            var Q1001;
            Q1001=sQuery(id+"F0.wireOp",EDGE,"E1459");
            var Q1002;
            Q1002=sQuery(id+"F0.wireOp",EDGE,"E1514");
            var Q1003;
            Q1003=sQuery(id+"F0.wireOp",EDGE,"E1546");
            var Q1004;
            Q1004=sQuery(id+"F0.wireOp",EDGE,"E1482");
            var Q1005;
            Q1005=sQuery(id+"F0.wireOp",EDGE,"E2435");
            var Q1006;
            Q1006=sQuery(id+"F0.wireOp",EDGE,"E1891");
            var Q1007;
            Q1007=sQuery(id+"F0.wireOp",EDGE,"E1882");
            var Q1008;
            Q1008=sQuery(id+"F0.wireOp",EDGE,"E836");
            var Q1009;
            Q1009=sQuery(id+"F0.wireOp",EDGE,"E852");
            var Q1010;
            Q1010=sQuery(id+"F0.wireOp",EDGE,"E868");
            var Q1011;
            Q1011=sQuery(id+"F0.wireOp",EDGE,"E1305");
            var Q1012;
            Q1012=sQuery(id+"F0.wireOp",EDGE,"E2178");
            var Q1013;
            Q1013=sQuery(id+"F0.wireOp",EDGE,"E2153");
            var Q1014;
            Q1014=sQuery(id+"F0.wireOp",EDGE,"E2185");
            var Q1015;
            Q1015=sQuery(id+"F0.wireOp",EDGE,"E2050");
            var Q1016;
            Q1016=sQuery(id+"F0.wireOp",EDGE,"E1097");
            var Q1017;
            Q1017=sQuery(id+"F0.wireOp",EDGE,"E275");
            var Q1018;
            Q1018=sQuery(id+"F0.wireOp",EDGE,"E1684");
            var Q1019;
            Q1019=sQuery(id+"F0.wireOp",EDGE,"E1890");
            var Q1020;
            Q1020=sQuery(id+"F0.wireOp",EDGE,"E1538");
            var Q1021;
            Q1021=sQuery(id+"F0.wireOp",EDGE,"E1458");
            var Q1022;
            Q1022=sQuery(id+"F0.wireOp",EDGE,"E1481");
            var Q1023;
            Q1023=sQuery(id+"F0.wireOp",EDGE,"E1465");
            var Q1024;
            Q1024=sQuery(id+"F0.wireOp",EDGE,"E1410");
            var Q1025;
            Q1025=sQuery(id+"F0.wireOp",EDGE,"E2434");
            var Q1026;
            Q1026=sQuery(id+"F0.wireOp",EDGE,"E1668");
            var Q1027;
            Q1027=sQuery(id+"F0.wireOp",EDGE,"E2354");
            var Q1028;
            Q1028=sQuery(id+"F0.wireOp",EDGE,"E1713");
            var Q1029;
            Q1029=sQuery(id+"F0.wireOp",EDGE,"E1617");
            var Q1030;
            Q1030=sQuery(id+"F0.wireOp",EDGE,"E1881");
            var Q1031;
            Q1031=sQuery(id+"F0.wireOp",EDGE,"E531");
            var Q1032;
            Q1032=sQuery(id+"F0.wireOp",EDGE,"E547");
            var Q1033;
            Q1033=sQuery(id+"F0.wireOp",EDGE,"E1865");
            var Q1034;
            Q1034=sQuery(id+"F0.wireOp",EDGE,"E307");
            var Q1035;
            Q1035=sQuery(id+"F0.wireOp",EDGE,"E323");
            var Q1036;
            Q1036=sQuery(id+"F0.wireOp",EDGE,"E2184");
            var Q1037;
            Q1037=sQuery(id+"F0.wireOp",EDGE,"E2056");
            var Q1038;
            Q1038=sQuery(id+"F0.wireOp",EDGE,"E706");
            var Q1039;
            Q1039=sQuery(id+"F0.wireOp",EDGE,"E722");
            var Q1040;
            Q1040=sQuery(id+"F0.wireOp",EDGE,"E1889");
            var Q1041;
            Q1041=sQuery(id+"F0.wireOp",EDGE,"E1295");
            var Q1042;
            Q1042=sQuery(id+"F0.wireOp",EDGE,"E1734");
            var Q1043;
            Q1043=sQuery(id+"F0.wireOp",EDGE,"E1521");
            var Q1044;
            Q1044=sQuery(id+"F0.wireOp",EDGE,"E1608");
            var Q1045;
            Q1045=sQuery(id+"F0.wireOp",EDGE,"E1512");
            var Q1046;
            Q1046=sQuery(id+"F0.wireOp",EDGE,"E1457");
            var Q1047;
            Q1047=sQuery(id+"F0.wireOp",EDGE,"E1544");
            var Q1048;
            Q1048=sQuery(id+"F0.wireOp",EDGE,"E1528");
            var Q1049;
            Q1049=sQuery(id+"F0.wireOp",EDGE,"E1480");
            var Q1050;
            Q1050=sQuery(id+"F0.wireOp",EDGE,"E2360");
            var Q1051;
            Q1051=sQuery(id+"F0.wireOp",EDGE,"E2408");
            var Q1052;
            Q1052=sQuery(id+"F0.wireOp",EDGE,"E162");
            var Q1053;
            Q1053=sQuery(id+"F0.wireOp",EDGE,"E1233");
            var Q1054;
            Q1054=sQuery(id+"F0.wireOp",EDGE,"E2177");
            var Q1055;
            Q1055=sQuery(id+"F0.wireOp",EDGE,"E1240");
            var Q1056;
            Q1056=sQuery(id+"F0.wireOp",EDGE,"E1600");
            var Q1057;
            Q1057=sQuery(id+"F0.wireOp",EDGE,"E1470");
            var Q1058;
            Q1058=sQuery(id+"F0.wireOp",EDGE,"E1591");
            var Q1059;
            Q1059=sQuery(id+"F0.wireOp",EDGE,"E1675");
            var Q1060;
            Q1060=sQuery(id+"F0.wireOp",EDGE,"E946");
            var Q1061;
            Q1061=sQuery(id+"F0.wireOp",EDGE,"E1536");
            var Q1062;
            Q1062=sQuery(id+"F0.wireOp",EDGE,"E1456");
            var Q1063;
            Q1063=sQuery(id+"F0.wireOp",EDGE,"E1543");
            var Q1064;
            Q1064=sQuery(id+"F0.wireOp",EDGE,"E1527");
            var Q1065;
            Q1065=sQuery(id+"F0.wireOp",EDGE,"E930");
            var Q1066;
            Q1066=sQuery(id+"F0.wireOp",EDGE,"E1406");
            var Q1067;
            Q1067=sQuery(id+"F0.wireOp",EDGE,"E514");
            var Q1068;
            Q1068=sQuery(id+"F0.wireOp",EDGE,"E2000");
            var Q1069;
            Q1069=sQuery(id+"F0.wireOp",EDGE,"E1872");
            var Q1070;
            Q1070=sQuery(id+"F0.wireOp",EDGE,"E1927");
            var Q1071;
            Q1071=sQuery(id+"F0.wireOp",EDGE,"E1888");
            var Q1072;
            Q1072=sQuery(id+"F0.wireOp",EDGE,"E1100");
            var Q1073;
            Q1073=sQuery(id+"F0.wireOp",EDGE,"E593");
            var Q1074;
            Q1074=sQuery(id+"F0.wireOp",EDGE,"E945");
            var Q1075;
            Q1075=sQuery(id+"F0.wireOp",EDGE,"E2384");
            var Q1076;
            Q1076=sQuery(id+"F0.wireOp",EDGE,"E865");
            var Q1077;
            Q1077=sQuery(id+"F0.wireOp",EDGE,"E1540");
            var Q1078;
            Q1078=sQuery(id+"F0.wireOp",EDGE,"E1595");
            var Q1079;
            Q1079=sQuery(id+"F0.wireOp",EDGE,"E2366");
            var Q1080;
            Q1080=sQuery(id+"F0.wireOp",EDGE,"E305");
            var Q1081;
            Q1081=sQuery(id+"F0.wireOp",EDGE,"E337");
            var Q1082;
            Q1082=sQuery(id+"F0.wireOp",EDGE,"E273");
            var Q1083;
            Q1083=sQuery(id+"F0.wireOp",EDGE,"E720");
            var Q1084;
            Q1084=sQuery(id+"F0.wireOp",EDGE,"E592");
            var Q1085;
            Q1085=sQuery(id+"F0.wireOp",EDGE,"E560");
            var Q1086;
            Q1086=sQuery(id+"F0.wireOp",EDGE,"E896");
            var Q1087;
            Q1087=sQuery(id+"F0.wireOp",EDGE,"E1909");
            var Q1088;
            Q1088=sQuery(id+"F0.wireOp",EDGE,"E832");
            var Q1089;
            Q1089=sQuery(id+"F0.wireOp",EDGE,"E320");
            var Q1090;
            Q1090=sQuery(id+"F0.wireOp",EDGE,"E112");
            var Q1091;
            Q1091=sQuery(id+"F0.wireOp",EDGE,"E303");
            var Q1092;
            Q1092=sQuery(id+"F0.wireOp",EDGE,"E319");
            var Q1093;
            Q1093=sQuery(id+"F0.wireOp",EDGE,"E335");
            var Q1094;
            Q1094=sQuery(id+"F0.wireOp",EDGE,"E703");
            var Q1095;
            Q1095=sQuery(id+"F0.wireOp",EDGE,"E719");
            var Q1096;
            Q1096=sQuery(id+"F0.wireOp",EDGE,"E607");
            var Q1097;
            Q1097=sQuery(id+"F0.wireOp",EDGE,"E543");
            var Q1098;
            Q1098=sQuery(id+"F0.wireOp",EDGE,"E830");
            var Q1099;
            Q1099=sQuery(id+"F0.wireOp",EDGE,"E927");
            var Q1100;
            Q1100=sQuery(id+"F0.wireOp",EDGE,"E382");
            var Q1101;
            Q1101=sQuery(id+"F0.wireOp",EDGE,"E1877");
            var Q1102;
            Q1102=sQuery(id+"F0.wireOp",EDGE,"E302");
            var Q1103;
            Q1103=sQuery(id+"F0.wireOp",EDGE,"E318");
            var Q1104;
            Q1104=sQuery(id+"F0.wireOp",EDGE,"E814");
            var Q1105;
            Q1105=sQuery(id+"F0.wireOp",EDGE,"E558");
            var Q1106;
            Q1106=sQuery(id+"F0.wireOp",EDGE,"E333");
            var Q1107;
            Q1107=sQuery(id+"F0.wireOp",EDGE,"E605");
            var Q1108;
            Q1108=sQuery(id+"F0.wireOp",EDGE,"E909");
            var Q1109;
            Q1109=sQuery(id+"F0.wireOp",EDGE,"E1094");
            var Q1110;
            Q1110=sQuery(id+"F0.wireOp",EDGE,"E1078");
            var Q1111;
            Q1111=sQuery(id+"F0.wireOp",EDGE,"E2350");
            var Q1112;
            Q1112=sQuery(id+"F0.wireOp",EDGE,"E1319");
            var Q1113;
            Q1113=sQuery(id+"F0.wireOp",EDGE,"E2150");
            var Q1114;
            Q1114=sQuery(id+"F0.wireOp",EDGE,"E1303");
            var Q1115;
            Q1115=sQuery(id+"F0.wireOp",EDGE,"E1239");
            var Q1116;
            Q1116=sQuery(id+"F0.wireOp",EDGE,"E2006");
            var Q1117;
            Q1117=sQuery(id+"F0.wireOp",EDGE,"E2183");
            var Q1118;
            Q1118=sQuery(id+"F0.wireOp",EDGE,"E1104");
            var Q1119;
            Q1119=sQuery(id+"F0.wireOp",EDGE,"E1749");
            var Q1120;
            Q1120=sQuery(id+"F0.wireOp",EDGE,"E2064");
            var Q1121;
            Q1121=sQuery(id+"F0.wireOp",EDGE,"E1294");
            var Q1122;
            Q1122=sQuery(id+"F0.wireOp",EDGE,"E1883");
            var Q1123;
            Q1123=sQuery(id+"F0.wireOp",EDGE,"E2175");
            var Q1124;
            Q1124=sQuery(id+"F0.wireOp",EDGE,"E1542");
            var Q1125;
            Q1125=sQuery(id+"F0.wireOp",EDGE,"E1724");
            var Q1126;
            Q1126=sQuery(id+"F0.wireOp",EDGE,"E2063");
            var Q1127;
            Q1127=sQuery(id+"F0.wireOp",EDGE,"E764");
            var Q1128;
            Q1128=sQuery(id+"F0.wireOp",EDGE,"E684");
            var Q1129;
            Q1129=sQuery(id+"F0.wireOp",EDGE,"E652");
            var Q1130;
            Q1130=sQuery(id+"F0.wireOp",EDGE,"E988");
            var Q1131;
            Q1131=sQuery(id+"F0.wireOp",EDGE,"E1589");
            var Q1132;
            Q1132=sQuery(id+"F0.wireOp",EDGE,"E1004");
            var Q1133;
            Q1133=sQuery(id+"F0.wireOp",EDGE,"E1596");
            var Q1134;
            Q1134=sQuery(id+"F0.wireOp",EDGE,"E236");
            var Q1135;
            Q1135=sQuery(id+"F0.wireOp",EDGE,"E1621");
            var Q1136;
            Q1136=sQuery(id+"F0.wireOp",EDGE,"E763");
            var Q1137;
            Q1137=sQuery(id+"F0.wireOp",EDGE,"E1867");
            var Q1138;
            Q1138=sQuery(id+"F0.wireOp",EDGE,"E651");
            var Q1139;
            Q1139=sQuery(id+"F0.wireOp",EDGE,"E459");
            var Q1140;
            Q1140=sQuery(id+"F0.wireOp",EDGE,"E1605");
            var Q1141;
            Q1141=sQuery(id+"F0.wireOp",EDGE,"E2062");
            var Q1142;
            Q1142=sQuery(id+"F0.wireOp",EDGE,"E827");
            var Q1143;
            Q1143=sQuery(id+"F0.wireOp",EDGE,"E2374");
            var Q1144;
            Q1144=sQuery(id+"F0.wireOp",EDGE,"E1532");
            var Q1145;
            Q1145=sQuery(id+"F0.wireOp",EDGE,"E235");
            var Q1146;
            Q1146=sQuery(id+"F0.wireOp",EDGE,"E139");
            var Q1147;
            Q1147=sQuery(id+"F0.wireOp",EDGE,"E8");
            var Q1148;
            Q1148=sQuery(id+"F0.wireOp",EDGE,"E682");
            var Q1149;
            Q1149=sQuery(id+"F0.wireOp",EDGE,"E714");
            var Q1150;
            Q1150=sQuery(id+"F0.wireOp",EDGE,"E666");
            var Q1151;
            Q1151=sQuery(id+"F0.wireOp",EDGE,"E826");
            var Q1152;
            Q1152=sQuery(id+"F0.wireOp",EDGE,"E2047");
            var Q1153;
            Q1153=sQuery(id+"F0.wireOp",EDGE,"E1002");
            var Q1154;
            Q1154=sQuery(id+"F0.wireOp",EDGE,"E234");
            var Q1155;
            Q1155=sQuery(id+"F0.wireOp",EDGE,"E138");
            var Q1156;
            Q1156=sQuery(id+"F0.wireOp",EDGE,"E2428");
            var Q1157;
            Q1157=sQuery(id+"F0.wireOp",EDGE,"E1887");
            var Q1158;
            Q1158=sQuery(id+"F0.wireOp",EDGE,"E665");
            var Q1159;
            Q1159=sQuery(id+"F0.wireOp",EDGE,"E489");
            var Q1160;
            Q1160=sQuery(id+"F0.wireOp",EDGE,"E457");
            var Q1161;
            Q1161=sQuery(id+"F0.wireOp",EDGE,"E1467");
            var Q1162;
            Q1162=sQuery(id+"F0.wireOp",EDGE,"E1388");
            var Q1163;
            Q1163=sQuery(id+"F0.wireOp",EDGE,"E1871");
            var Q1164;
            Q1164=sQuery(id+"F0.wireOp",EDGE,"E1965");
            var Q1165;
            Q1165=sQuery(id+"F0.wireOp",EDGE,"E825");
            var Q1166;
            Q1166=sQuery(id+"F0.wireOp",EDGE,"E761");
            var Q1167;
            Q1167=sQuery(id+"F0.wireOp",EDGE,"E745");
            var Q1168;
            Q1168=sQuery(id+"F0.wireOp",EDGE,"E681");
            var Q1169;
            Q1169=sQuery(id+"F0.wireOp",EDGE,"E1001");
            var Q1170;
            Q1170=sQuery(id+"F0.wireOp",EDGE,"E1631");
            var Q1171;
            Q1171=sQuery(id+"F0.wireOp",EDGE,"E169");
            var Q1172;
            Q1172=sQuery(id+"F0.wireOp",EDGE,"E921");
            var Q1173;
            Q1173=sQuery(id+"F0.wireOp",EDGE,"E552");
            var Q1174;
            Q1174=sQuery(id+"F0.wireOp",EDGE,"E456");
            var Q1175;
            Q1175=sQuery(id+"F0.wireOp",EDGE,"E344");
            var Q1176;
            Q1176=sQuery(id+"F0.wireOp",EDGE,"E232");
            var Q1177;
            Q1177=sQuery(id+"F0.wireOp",EDGE,"E1997");
            var Q1178;
            Q1178=sQuery(id+"F0.wireOp",EDGE,"E664");
            var Q1179;
            Q1179=sQuery(id+"F0.wireOp",EDGE,"E1000");
            var Q1180;
            Q1180=sQuery(id+"F0.wireOp",EDGE,"E936");
            var Q1181;
            Q1181=sQuery(id+"F0.wireOp",EDGE,"E343");
            var Q1182;
            Q1182=sQuery(id+"F0.wireOp",EDGE,"E231");
            var Q1183;
            Q1183=sQuery(id+"F0.wireOp",EDGE,"E183");
            var Q1184;
            Q1184=sQuery(id+"F0.wireOp",EDGE,"E823");
            var Q1185;
            Q1185=sQuery(id+"F0.wireOp",EDGE,"E759");
            var Q1186;
            Q1186=sQuery(id+"F0.wireOp",EDGE,"E727");
            var Q1187;
            Q1187=sQuery(id+"F0.wireOp",EDGE,"E711");
            var Q1188;
            Q1188=sQuery(id+"F0.wireOp",EDGE,"E2349");
            var Q1189;
            Q1189=sQuery(id+"F0.wireOp",EDGE,"E935");
            var Q1190;
            Q1190=sQuery(id+"F0.wireOp",EDGE,"E1317");
            var Q1191;
            Q1191=sQuery(id+"F0.wireOp",EDGE,"E999");
            var Q1192;
            Q1192=sQuery(id+"F0.wireOp",EDGE,"E1551");
            var Q1193;
            Q1193=sQuery(id+"F0.wireOp",EDGE,"E1535");
            var Q1194;
            Q1194=sQuery(id+"F0.wireOp",EDGE,"E1455");
            var Q1195;
            Q1195=sQuery(id+"F0.wireOp",EDGE,"E342");
            var Q1196;
            Q1196=sQuery(id+"F0.wireOp",EDGE,"E758");
            var Q1197;
            Q1197=sQuery(id+"F0.wireOp",EDGE,"E662");
            var Q1198;
            Q1198=sQuery(id+"F0.wireOp",EDGE,"E550");
            var Q1199;
            Q1199=sQuery(id+"F0.wireOp",EDGE,"E1700");
            var Q1200;
            Q1200=sQuery(id+"F0.wireOp",EDGE,"E1517");
            var Q1201;
            Q1201=sQuery(id+"F0.wireOp",EDGE,"E998");
            var Q1202;
            Q1202=sQuery(id+"F0.wireOp",EDGE,"E1732");
            var Q1203;
            Q1203=sQuery(id+"F0.wireOp",EDGE,"E1469");
            var Q1204;
            Q1204=sQuery(id+"F0.wireOp",EDGE,"E133");
            var Q1205;
            Q1205=sQuery(id+"F0.wireOp",EDGE,"E1308");
            var Q1206;
            Q1206=sQuery(id+"F0.wireOp",EDGE,"E757");
            var Q1207;
            Q1207=sQuery(id+"F0.wireOp",EDGE,"E453");
            var Q1208;
            Q1208=sQuery(id+"F0.wireOp",EDGE,"E485");
            var Q1209;
            Q1209=sQuery(id+"F0.wireOp",EDGE,"E820");
            var Q1210;
            Q1210=sQuery(id+"F0.wireOp",EDGE,"E788");
            var Q1211;
            Q1211=sQuery(id+"F0.wireOp",EDGE,"E885");
            var Q1212;
            Q1212=sQuery(id+"F0.wireOp",EDGE,"E933");
            var Q1213;
            Q1213=sQuery(id+"F0.wireOp",EDGE,"E340");
            var Q1214;
            Q1214=sQuery(id+"F0.wireOp",EDGE,"E2156");
            var Q1215;
            Q1215=sQuery(id+"F0.wireOp",EDGE,"E228");
            var Q1216;
            Q1216=sQuery(id+"F0.wireOp",EDGE,"E2181");
            var Q1217;
            Q1217=sQuery(id+"F0.wireOp",EDGE,"E276");
            var Q1218;
            Q1218=sQuery(id+"F0.wireOp",EDGE,"E708");
            var Q1219;
            Q1219=sQuery(id+"F0.wireOp",EDGE,"E756");
            var Q1220;
            Q1220=sQuery(id+"F0.wireOp",EDGE,"E740");
            var Q1221;
            Q1221=sQuery(id+"F0.wireOp",EDGE,"E596");
            var Q1222;
            Q1222=sQuery(id+"F0.wireOp",EDGE,"E548");
            var Q1223;
            Q1223=sQuery(id+"F0.wireOp",EDGE,"E500");
            var Q1224;
            Q1224=sQuery(id+"F0.wireOp",EDGE,"E1315");
            var Q1225;
            Q1225=sQuery(id+"F0.wireOp",EDGE,"E2351");
            var Q1226;
            Q1226=sQuery(id+"F0.wireOp",EDGE,"E2163");
            var Q1227;
            Q1227=sQuery(id+"F0.wireOp",EDGE,"E1869");
            var Q1228;
            Q1228=sQuery(id+"F0.wireOp",EDGE,"E2170");
            var Q1229;
            Q1229=sQuery(id+"F0.wireOp",EDGE,"E2147");
            var Q1230;
            Q1230=sQuery(id+"F0.wireOp",EDGE,"E787");
            var Q1231;
            Q1231=sQuery(id+"F0.wireOp",EDGE,"E819");
            var Q1232;
            Q1232=sQuery(id+"F0.wireOp",EDGE,"E739");
            var Q1233;
            Q1233=sQuery(id+"F0.wireOp",EDGE,"E1850");
            var Q1234;
            Q1234=sQuery(id+"F0.wireOp",EDGE,"E1747");
            var Q1235;
            Q1235=sQuery(id+"F0.wireOp",EDGE,"E1706");
            var Q1236;
            Q1236=sQuery(id+"F0.wireOp",EDGE,"E1738");
            var Q1237;
            Q1237=sQuery(id+"F0.wireOp",EDGE,"E1626");
            var Q1238;
            Q1238=sQuery(id+"F0.wireOp",EDGE,"E900");
            var Q1239;
            Q1239=sQuery(id+"F0.wireOp",EDGE,"E1849");
            var Q1240;
            Q1240=sQuery(id+"F0.wireOp",EDGE,"E1978");
            var Q1241;
            Q1241=sQuery(id+"F0.wireOp",EDGE,"E1971");
            var Q1242;
            Q1242=sQuery(id+"F0.wireOp",EDGE,"E2010");
            var Q1243;
            Q1243=sQuery(id+"F0.wireOp",EDGE,"E1859");
            var Q1244;
            Q1244=sQuery(id+"F0.wireOp",EDGE,"E2035");
            var Q1245;
            Q1245=sQuery(id+"F0.wireOp",EDGE,"E2042");
            var Q1246;
            Q1246=sQuery(id+"F0.wireOp",EDGE,"E1243");
            var Q1247;
            Q1247=sQuery(id+"F0.wireOp",EDGE,"E2169");
            var Q1248;
            Q1248=sQuery(id+"F0.wireOp",EDGE,"E2383");
            var Q1249;
            Q1249=sQuery(id+"F0.wireOp",EDGE,"E2057");
            var Q1250;
            Q1250=sQuery(id+"F0.wireOp",EDGE,"E2002");
            var Q1251;
            Q1251=sQuery(id+"F0.wireOp",EDGE,"E2009");
            var Q1252;
            Q1252=sQuery(id+"F0.wireOp",EDGE,"E1244");
            var Q1253;
            Q1253=sQuery(id+"F0.wireOp",EDGE,"E115");
            var Q1254;
            Q1254=sQuery(id+"F0.wireOp",EDGE,"E1625");
            var Q1255;
            Q1255=sQuery(id+"F0.wireOp",EDGE,"E1554");
            var Q1256;
            Q1256=sQuery(id+"F0.wireOp",EDGE,"E1513");
            var Q1257;
            Q1257=sQuery(id+"F0.wireOp",EDGE,"E1545");
            var Q1258;
            Q1258=sQuery(id+"F0.wireOp",EDGE,"E899");
            var Q1259;
            Q1259=sQuery(id+"F0.wireOp",EDGE,"E659");
            var Q1260;
            Q1260=sQuery(id+"F0.wireOp",EDGE,"E2345");
            var Q1261;
            Q1261=sQuery(id+"F0.wireOp",EDGE,"E2409");
            var Q1262;
            Q1262=sQuery(id+"F0.wireOp",EDGE,"E1385");
            var Q1263;
            Q1263=sQuery(id+"F0.wireOp",EDGE,"E1848");
            var Q1264;
            Q1264=sQuery(id+"F0.wireOp",EDGE,"E1729");
            var Q1265;
            Q1265=sQuery(id+"F0.wireOp",EDGE,"E2148");
            var Q1266;
            Q1266=sQuery(id+"F0.wireOp",EDGE,"E1649");
            var Q1267;
            Q1267=sQuery(id+"F0.wireOp",EDGE,"E1704");
            var Q1268;
            Q1268=sQuery(id+"F0.wireOp",EDGE,"E1633");
            var Q1269;
            Q1269=sQuery(id+"F0.wireOp",EDGE,"E1624");
            var Q1270;
            Q1270=sQuery(id+"F0.wireOp",EDGE,"E435");
            var Q1271;
            Q1271=sQuery(id+"F0.wireOp",EDGE,"E339");
            var Q1272;
            Q1272=sQuery(id+"F0.wireOp",EDGE,"E2152");
            var Q1273;
            Q1273=sQuery(id+"F0.wireOp",EDGE,"E2173");
            var Q1274;
            Q1274=sQuery(id+"F0.wireOp",EDGE,"E2052");
            var Q1275;
            Q1275=sQuery(id+"F0.wireOp",EDGE,"E1080");
            var Q1276;
            Q1276=sQuery(id+"F0.wireOp",EDGE,"E1112");
            var Q1277;
            Q1277=sQuery(id+"F0.wireOp",EDGE,"E818");
            var Q1278;
            Q1278=sQuery(id+"F0.wireOp",EDGE,"E1976");
            var Q1279;
            Q1279=sQuery(id+"F0.wireOp",EDGE,"E1969");
            var Q1280;
            Q1280=sQuery(id+"F0.wireOp",EDGE,"E754");
            var Q1281;
            Q1281=sQuery(id+"F0.wireOp",EDGE,"E1588");
            var Q1282;
            Q1282=sQuery(id+"F0.wireOp",EDGE,"E1864");
            var Q1283;
            Q1283=sQuery(id+"F0.wireOp",EDGE,"E835");
            var Q1284;
            Q1284=sQuery(id+"F0.wireOp",EDGE,"E1464");
            var Q1285;
            Q1285=sQuery(id+"F0.wireOp",EDGE,"E2433");
            var Q1286;
            Q1286=sQuery(id+"F0.wireOp",EDGE,"E2053");
            var Q1287;
            Q1287=sQuery(id+"F0.wireOp",EDGE,"E2376");
            var Q1288;
            Q1288=sQuery(id+"F0.wireOp",EDGE,"E2353");
            var Q1289;
            Q1289=sQuery(id+"F0.wireOp",EDGE,"E1627");
            var Q1290;
            Q1290=sQuery(id+"F0.wireOp",EDGE,"E1550");
            var Q1291;
            Q1291=sQuery(id+"F0.wireOp",EDGE,"E114");
            var Q1292;
            Q1292=sQuery(id+"F0.wireOp",EDGE,"E1728");
            var Q1293;
            Q1293=sQuery(id+"F0.wireOp",EDGE,"E1712");
            var Q1294;
            Q1294=sQuery(id+"F0.wireOp",EDGE,"E1744");
            var Q1295;
            Q1295=sQuery(id+"F0.wireOp",EDGE,"E1648");
            var Q1296;
            Q1296=sQuery(id+"F0.wireOp",EDGE,"E1703");
            var Q1297;
            Q1297=sQuery(id+"F0.wireOp",EDGE,"E1623");
            var Q1298;
            Q1298=sQuery(id+"F0.wireOp",EDGE,"E1520");
            var Q1299;
            Q1299=sQuery(id+"F0.wireOp",EDGE,"E1115");
            var Q1300;
            Q1300=sQuery(id+"F0.wireOp",EDGE,"E2055");
            var Q1301;
            Q1301=sQuery(id+"F0.wireOp",EDGE,"E1975");
            var Q1302;
            Q1302=sQuery(id+"F0.wireOp",EDGE,"E1968");
            var Q1303;
            Q1303=sQuery(id+"F0.wireOp",EDGE,"E434");
            var Q1304;
            Q1304=sQuery(id+"F0.wireOp",EDGE,"E2007");
            var Q1305;
            Q1305=sQuery(id+"F0.wireOp",EDGE,"E1863");
            var Q1306;
            Q1306=sQuery(id+"F0.wireOp",EDGE,"E1879");
            var Q1307;
            Q1307=sQuery(id+"F0.wireOp",EDGE,"E322");
            var Q1308;
            Q1308=sQuery(id+"F0.wireOp",EDGE,"E338");
            var Q1309;
            Q1309=sQuery(id+"F0.wireOp",EDGE,"E274");
            var Q1310;
            Q1310=sQuery(id+"F0.wireOp",EDGE,"E785");
            var Q1311;
            Q1311=sQuery(id+"F0.wireOp",EDGE,"E705");
            var Q1312;
            Q1312=sQuery(id+"F0.wireOp",EDGE,"E753");
            var Q1313;
            Q1313=sQuery(id+"F0.wireOp",EDGE,"E657");
            var Q1314;
            Q1314=sQuery(id+"F0.wireOp",EDGE,"E2060");
            var Q1315;
            Q1315=sQuery(id+"F0.wireOp",EDGE,"E2432");
            var Q1316;
            Q1316=sQuery(id+"F0.wireOp",EDGE,"E1408");
            var Q1317;
            Q1317=sQuery(id+"F0.wireOp",EDGE,"E1117");
            var Q1318;
            Q1318=sQuery(id+"F0.wireOp",EDGE,"E929");
            var Q1319;
            Q1319=sQuery(id+"F0.wireOp",EDGE,"E1611");
            var Q1320;
            Q1320=sQuery(id+"F0.wireOp",EDGE,"E1556");
            var Q1321;
            Q1321=sQuery(id+"F0.wireOp",EDGE,"E449");
            var Q1322;
            Q1322=sQuery(id+"F0.wireOp",EDGE,"E2375");
            var Q1323;
            Q1323=sQuery(id+"F0.wireOp",EDGE,"E1476");
            var Q1324;
            Q1324=sQuery(id+"F0.wireOp",EDGE,"E1925");
            var Q1325;
            Q1325=sQuery(id+"F0.wireOp",EDGE,"E944");
            var Q1326;
            Q1326=sQuery(id+"F0.wireOp",EDGE,"E304");
            var Q1327;
            Q1327=sQuery(id+"F0.wireOp",EDGE,"E272");
            var Q1328;
            Q1328=sQuery(id+"F0.wireOp",EDGE,"E192");
            var Q1329;
            Q1329=sQuery(id+"F0.wireOp",EDGE,"E2012");
            var Q1330;
            Q1330=sQuery(id+"F0.wireOp",EDGE,"E111");
            var Q1331;
            Q1331=sQuery(id+"F0.wireOp",EDGE,"E831");
            var Q1332;
            Q1332=sQuery(id+"F0.wireOp",EDGE,"E1232");
            var Q1333;
            Q1333=sQuery(id+"F0.wireOp",EDGE,"E591");
            var Q1334;
            Q1334=sQuery(id+"F0.wireOp",EDGE,"E447");
            var Q1335;
            Q1335=sQuery(id+"F0.wireOp",EDGE,"E895");
            var Q1336;
            Q1336=sQuery(id+"F0.wireOp",EDGE,"E1893");
            var Q1337;
            Q1337=sQuery(id+"F0.wireOp",EDGE,"E863");
            var Q1338;
            Q1338=sQuery(id+"F0.wireOp",EDGE,"E286");
            var Q1339;
            Q1339=sQuery(id+"F0.wireOp",EDGE,"E270");
            var Q1340;
            Q1340=sQuery(id+"F0.wireOp",EDGE,"E190");
            var Q1341;
            Q1341=sQuery(id+"F0.wireOp",EDGE,"E1710");
            var Q1342;
            Q1342=sQuery(id+"F0.wireOp",EDGE,"E718");
            var Q1343;
            Q1343=sQuery(id+"F0.wireOp",EDGE,"E750");
            var Q1344;
            Q1344=sQuery(id+"F0.wireOp",EDGE,"E686");
            var Q1345;
            Q1345=sQuery(id+"F0.wireOp",EDGE,"E606");
            var Q1346;
            Q1346=sQuery(id+"F0.wireOp",EDGE,"E462");
            var Q1347;
            Q1347=sQuery(id+"F0.wireOp",EDGE,"E926");
            var Q1348;
            Q1348=sQuery(id+"F0.wireOp",EDGE,"E285");
            var Q1349;
            Q1349=sQuery(id+"F0.wireOp",EDGE,"E301");
            var Q1350;
            Q1350=sQuery(id+"F0.wireOp",EDGE,"E1884");
            var Q1351;
            Q1351=sQuery(id+"F0.wireOp",EDGE,"E941");
            var Q1352;
            Q1352=sQuery(id+"F0.wireOp",EDGE,"E557");
            var Q1353;
            Q1353=sQuery(id+"F0.wireOp",EDGE,"E381");
            var Q1354;
            Q1354=sQuery(id+"F0.wireOp",EDGE,"E925");
            var Q1355;
            Q1355=sQuery(id+"F0.wireOp",EDGE,"E1614");
            var Q1356;
            Q1356=sQuery(id+"F0.wireOp",EDGE,"E1598");
            var Q1357;
            Q1357=sQuery(id+"F0.wireOp",EDGE,"E2102");
            var Q1358;
            Q1358=sQuery(id+"F0.wireOp",EDGE,"E2343");
            var Q1359;
            Q1359=sQuery(id+"F0.wireOp",EDGE,"E1248");
            var Q1360;
            Q1360=sQuery(id+"F0.wireOp",EDGE,"E2054");
            var Q1361;
            Q1361=sQuery(id+"F0.wireOp",EDGE,"E1184");
            var Q1362;
            Q1362=sQuery(id+"F0.wireOp",EDGE,"E2167");
            var Q1363;
            Q1363=sQuery(id+"F0.wireOp",EDGE,"E2096");
            var Q1364;
            Q1364=sQuery(id+"F0.wireOp",EDGE,"E1310");
            var Q1365;
            Q1365=sQuery(id+"F0.wireOp",EDGE,"E1711");
            var Q1366;
            Q1366=sQuery(id+"F0.wireOp",EDGE,"E1743");
            var Q1367;
            Q1367=sQuery(id+"F0.wireOp",EDGE,"E1727");
            var Q1368;
            Q1368=sQuery(id+"F0.wireOp",EDGE,"E1099");
            var Q1369;
            Q1369=sQuery(id+"F0.wireOp",EDGE,"E1231");
            var Q1370;
            Q1370=sQuery(id+"F0.wireOp",EDGE,"E1622");
            var Q1371;
            Q1371=sQuery(id+"F0.wireOp",EDGE,"E1246");
            var Q1372;
            Q1372=sQuery(id+"F0.wireOp",EDGE,"E1862");
            var Q1373;
            Q1373=sQuery(id+"F0.wireOp",EDGE,"E1462");
            var Q1374;
            Q1374=sQuery(id+"F0.wireOp",EDGE,"E620");
            var Q1375;
            Q1375=sQuery(id+"F0.wireOp",EDGE,"E1878");
            var Q1376;
            Q1376=sQuery(id+"F0.wireOp",EDGE,"E972");
            var Q1377;
            Q1377=sQuery(id+"F0.wireOp",EDGE,"E1983");
            var Q1378;
            Q1378=sQuery(id+"F0.wireOp",EDGE,"E1398");
            var Q1379;
            Q1379=sQuery(id+"F0.wireOp",EDGE,"E1541");
            var Q1380;
            Q1380=sQuery(id+"F0.wireOp",EDGE,"E220");
            var Q1381;
            Q1381=sQuery(id+"F0.wireOp",EDGE,"E172");
            var Q1382;
            Q1382=sQuery(id+"F0.wireOp",EDGE,"E188");
            var Q1383;
            Q1383=sQuery(id+"F0.wireOp",EDGE,"E1967");
            var Q1384;
            Q1384=sQuery(id+"F0.wireOp",EDGE,"E1516");
            var Q1385;
            Q1385=sQuery(id+"F0.wireOp",EDGE,"E683");
            var Q1386;
            Q1386=sQuery(id+"F0.wireOp",EDGE,"E1548");
            var Q1387;
            Q1387=sQuery(id+"F0.wireOp",EDGE,"E1003");
            var Q1388;
            Q1388=sQuery(id+"F0.wireOp",EDGE,"E155");
            var Q1389;
            Q1389=sQuery(id+"F0.wireOp",EDGE,"E187");
            var Q1390;
            Q1390=sQuery(id+"F0.wireOp",EDGE,"E987");
            var Q1391;
            Q1391=sQuery(id+"F0.wireOp",EDGE,"E1853");
            var Q1392;
            Q1392=sQuery(id+"F0.wireOp",EDGE,"E458");
            var Q1393;
            Q1393=sQuery(id+"F0.wireOp",EDGE,"E1951");
            var Q1394;
            Q1394=sQuery(id+"F0.wireOp",EDGE,"E2437");
            var Q1395;
            Q1395=sQuery(id+"F0.wireOp",EDGE,"E1935");
            var Q1396;
            Q1396=sQuery(id+"F0.wireOp",EDGE,"E762");
            var Q1397;
            Q1397=sQuery(id+"F0.wireOp",EDGE,"E858");
            var Q1398;
            Q1398=sQuery(id+"F0.wireOp",EDGE,"E1773");
            var Q1399;
            Q1399=sQuery(id+"F0.wireOp",EDGE,"E1860");
            var Q1400;
            Q1400=sQuery(id+"F0.wireOp",EDGE,"E2373");
            var Q1401;
            Q1401=sQuery(id+"F0.wireOp",EDGE,"E218");
            var Q1402;
            Q1402=sQuery(id+"F0.wireOp",EDGE,"E170");
            var Q1403;
            Q1403=sQuery(id+"F0.wireOp",EDGE,"E186");
            var Q1404;
            Q1404=sQuery(id+"F0.wireOp",EDGE,"E1318");
            var Q1405;
            Q1405=sQuery(id+"F0.wireOp",EDGE,"E1483");
            var Q1406;
            Q1406=sQuery(id+"F0.wireOp",EDGE,"E2357");
            var Q1407;
            Q1407=sQuery(id+"F0.wireOp",EDGE,"E2436");
            var Q1408;
            Q1408=sQuery(id+"F0.wireOp",EDGE,"E1412");
            var Q1409;
            Q1409=sQuery(id+"F0.wireOp",EDGE,"E2412");
            var Q1410;
            Q1410=sQuery(id+"F0.wireOp",EDGE,"E233");
            var Q1411;
            Q1411=sQuery(id+"F0.wireOp",EDGE,"E217");
            var Q1412;
            Q1412=sQuery(id+"F0.wireOp",EDGE,"E137");
            var Q1413;
            Q1413=sQuery(id+"F0.wireOp",EDGE,"E985");
            var Q1414;
            Q1414=sQuery(id+"F0.wireOp",EDGE,"E1725");
            var Q1415;
            Q1415=sQuery(id+"F0.wireOp",EDGE,"E969");
            var Q1416;
            Q1416=sQuery(id+"F0.wireOp",EDGE,"E2013");
            var Q1417;
            Q1417=sQuery(id+"F0.wireOp",EDGE,"E488");
            var Q1418;
            Q1418=sQuery(id+"F0.wireOp",EDGE,"E760");
            var Q1419;
            Q1419=sQuery(id+"F0.wireOp",EDGE,"E680");
            var Q1420;
            Q1420=sQuery(id+"F0.wireOp",EDGE,"E136");
            var Q1421;
            Q1421=sQuery(id+"F0.wireOp",EDGE,"E168");
            var Q1422;
            Q1422=sQuery(id+"F0.wireOp",EDGE,"E2427");
            var Q1423;
            Q1423=sQuery(id+"F0.wireOp",EDGE,"E984");
            var Q1424;
            Q1424=sQuery(id+"F0.wireOp",EDGE,"E968");
            var Q1425;
            Q1425=sQuery(id+"F0.wireOp",EDGE,"E455");
            var Q1426;
            Q1426=sQuery(id+"F0.wireOp",EDGE,"E2046");
            var Q1427;
            Q1427=sQuery(id+"F0.wireOp",EDGE,"E135");
            var Q1428;
            Q1428=sQuery(id+"F0.wireOp",EDGE,"E679");
            var Q1429;
            Q1429=sQuery(id+"F0.wireOp",EDGE,"E631");
            var Q1430;
            Q1430=sQuery(id+"F0.wireOp",EDGE,"E663");
            var Q1431;
            Q1431=sQuery(id+"F0.wireOp",EDGE,"E1519");
            var Q1432;
            Q1432=sQuery(id+"F0.wireOp",EDGE,"E983");
            var Q1433;
            Q1433=sQuery(id+"F0.wireOp",EDGE,"E1886");
            var Q1434;
            Q1434=sQuery(id+"F0.wireOp",EDGE,"E230");
            var Q1435;
            Q1435=sQuery(id+"F0.wireOp",EDGE,"E246");
            var Q1436;
            Q1436=sQuery(id+"F0.wireOp",EDGE,"E2380");
            var Q1437;
            Q1437=sQuery(id+"F0.wireOp",EDGE,"E166");
            var Q1438;
            Q1438=sQuery(id+"F0.wireOp",EDGE,"E182");
            var Q1439;
            Q1439=sQuery(id+"F0.wireOp",EDGE,"E726");
            var Q1440;
            Q1440=sQuery(id+"F0.wireOp",EDGE,"E822");
            var Q1441;
            Q1441=sQuery(id+"F0.wireOp",EDGE,"E630");
            var Q1442;
            Q1442=sQuery(id+"F0.wireOp",EDGE,"E1597");
            var Q1443;
            Q1443=sQuery(id+"F0.wireOp",EDGE,"E1549");
            var Q1444;
            Q1444=sQuery(id+"F0.wireOp",EDGE,"E1309");
            var Q1445;
            Q1445=sQuery(id+"F0.wireOp",EDGE,"E341");
            var Q1446;
            Q1446=sQuery(id+"F0.wireOp",EDGE,"E2363");
            var Q1447;
            Q1447=sQuery(id+"F0.wireOp",EDGE,"E1293");
            var Q1448;
            Q1448=sQuery(id+"F0.wireOp",EDGE,"E661");
            var Q1449;
            Q1449=sQuery(id+"F0.wireOp",EDGE,"E2045");
            var Q1450;
            Q1450=sQuery(id+"F0.wireOp",EDGE,"E997");
            var Q1451;
            Q1451=sQuery(id+"F0.wireOp",EDGE,"E1077");
            var Q1452;
            Q1452=sQuery(id+"F0.wireOp",EDGE,"E1395");
            var Q1453;
            Q1453=sQuery(id+"F0.wireOp",EDGE,"E132");
            var Q1454;
            Q1454=sQuery(id+"F0.wireOp",EDGE,"E2387");
            var Q1455;
            Q1455=sQuery(id+"F0.wireOp",EDGE,"E2307");
            var Q1456;
            Q1456=sQuery(id+"F0.wireOp",EDGE,"E1316");
            var Q1457;
            Q1457=sQuery(id+"F0.wireOp",EDGE,"E452");
            var Q1458;
            Q1458=sQuery(id+"F0.wireOp",EDGE,"E2394");
            var Q1459;
            Q1459=sQuery(id+"F0.wireOp",EDGE,"E484");
            var Q1460;
            Q1460=sQuery(id+"F0.wireOp",EDGE,"E2339");
            var Q1461;
            Q1461=sQuery(id+"F0.wireOp",EDGE,"E2378");
            var Q1462;
            Q1462=sQuery(id+"F0.wireOp",EDGE,"E2323");
            var Q1463;
            Q1463=sQuery(id+"F0.wireOp",EDGE,"E1219");
            var Q1464;
            Q1464=sQuery(id+"F0.wireOp",EDGE,"E2330");
            var Q1465;
            Q1465=sQuery(id+"F0.wireOp",EDGE,"E1194");
            var Q1466;
            Q1466=sQuery(id+"F0.wireOp",EDGE,"E1300");
            var Q1467;
            Q1467=sQuery(id+"F0.wireOp",EDGE,"E1187");
            var Q1468;
            Q1468=sQuery(id+"F0.wireOp",EDGE,"E1226");
            var Q1469;
            Q1469=sQuery(id+"F0.wireOp",EDGE,"E1171");
            var Q1470;
            Q1470=sQuery(id+"F0.wireOp",EDGE,"E2115");
            var Q1471;
            Q1471=sQuery(id+"F0.wireOp",EDGE,"E2099");
            var Q1472;
            Q1472=sQuery(id+"F0.wireOp",EDGE,"E1178");
            var Q1473;
            Q1473=sQuery(id+"F0.wireOp",EDGE,"E2106");
            var Q1474;
            Q1474=sQuery(id+"F0.wireOp",EDGE,"E1220");
            var Q1475;
            Q1475=sQuery(id+"F0.wireOp",EDGE,"E707");
            var Q1476;
            Q1476=sQuery(id+"F0.wireOp",EDGE,"E1770");
            var Q1477;
            Q1477=sQuery(id+"F0.wireOp",EDGE,"E1722");
            var Q1478;
            Q1478=sQuery(id+"F0.wireOp",EDGE,"E1443");
            var Q1479;
            Q1479=sQuery(id+"F0.wireOp",EDGE,"E1746");
            var Q1480;
            Q1480=sQuery(id+"F0.wireOp",EDGE,"E1962");
            var Q1481;
            Q1481=sQuery(id+"F0.wireOp",EDGE,"E1955");
            var Q1482;
            Q1482=sQuery(id+"F0.wireOp",EDGE,"E2329");
            var Q1483;
            Q1483=sQuery(id+"F0.wireOp",EDGE,"E2162");
            var Q1484;
            Q1484=sQuery(id+"F0.wireOp",EDGE,"E2114");
            var Q1485;
            Q1485=sQuery(id+"F0.wireOp",EDGE,"E2105");
            var Q1486;
            Q1486=sQuery(id+"F0.wireOp",EDGE,"E227");
            var Q1487;
            Q1487=sQuery(id+"F0.wireOp",EDGE,"E1977");
            var Q1488;
            Q1488=sQuery(id+"F0.wireOp",EDGE,"E1970");
            var Q1489;
            Q1489=sQuery(id+"F0.wireOp",EDGE,"E163");
            var Q1490;
            Q1490=sQuery(id+"F0.wireOp",EDGE,"E1954");
            var Q1491;
            Q1491=sQuery(id+"F0.wireOp",EDGE,"E1858");
            var Q1492;
            Q1492=sQuery(id+"F0.wireOp",EDGE,"E1961");
            var Q1493;
            Q1493=sQuery(id+"F0.wireOp",EDGE,"E211");
            var Q1494;
            Q1494=sQuery(id+"F0.wireOp",EDGE,"E1705");
            var Q1495;
            Q1495=sQuery(id+"F0.wireOp",EDGE,"E2188");
            var Q1496;
            Q1496=sQuery(id+"F0.wireOp",EDGE,"E979");
            var Q1497;
            Q1497=sQuery(id+"F0.wireOp",EDGE,"E883");
            var Q1498;
            Q1498=sQuery(id+"F0.wireOp",EDGE,"E2386");
            var Q1499;
            Q1499=sQuery(id+"F0.wireOp",EDGE,"E2155");
            var Q1500;
            Q1500=sQuery(id+"F0.wireOp",EDGE,"E2338");
            var Q1501;
            Q1501=sQuery(id+"F0.wireOp",EDGE,"E1314");
            var Q1502;
            Q1502=sQuery(id+"F0.wireOp",EDGE,"E2393");
            var Q1503;
            Q1503=sQuery(id+"F0.wireOp",EDGE,"E2322");
            var Q1504;
            Q1504=sQuery(id+"F0.wireOp",EDGE,"E1745");
            var Q1505;
            Q1505=sQuery(id+"F0.wireOp",EDGE,"E2041");
            var Q1506;
            Q1506=sQuery(id+"F0.wireOp",EDGE,"E451");
            var Q1507;
            Q1507=sQuery(id+"F0.wireOp",EDGE,"E2187");
            var Q1508;
            Q1508=sQuery(id+"F0.wireOp",EDGE,"E1702");
            var Q1509;
            Q1509=sQuery(id+"F0.wireOp",EDGE,"E2168");
            var Q1510;
            Q1510=sQuery(id+"F0.wireOp",EDGE,"E786");
            var Q1511;
            Q1511=sQuery(id+"F0.wireOp",EDGE,"E2120");
            var Q1512;
            Q1512=sQuery(id+"F0.wireOp",EDGE,"E1096");
            var Q1513;
            Q1513=sQuery(id+"F0.wireOp",EDGE,"E2001");
            var Q1514;
            Q1514=sQuery(id+"F0.wireOp",EDGE,"E1953");
            var Q1515;
            Q1515=sQuery(id+"F0.wireOp",EDGE,"E738");
            var Q1516;
            Q1516=sQuery(id+"F0.wireOp",EDGE,"E2008");
            var Q1517;
            Q1517=sQuery(id+"F0.wireOp",EDGE,"E1857");
            var Q1518;
            Q1518=sQuery(id+"F0.wireOp",EDGE,"E658");
            var Q1519;
            Q1519=sQuery(id+"F0.wireOp",EDGE,"E674");
            var Q1520;
            Q1520=sQuery(id+"F0.wireOp",EDGE,"E1960");
            var Q1521;
            Q1521=sQuery(id+"F0.wireOp",EDGE,"E2091");
            var Q1522;
            Q1522=sQuery(id+"F0.wireOp",EDGE,"E2040");
            var Q1523;
            Q1523=sQuery(id+"F0.wireOp",EDGE,"E1553");
            var Q1524;
            Q1524=sQuery(id+"F0.wireOp",EDGE,"E1441");
            var Q1525;
            Q1525=sQuery(id+"F0.wireOp",EDGE,"E2319");
            var Q1526;
            Q1526=sQuery(id+"F0.wireOp",EDGE,"E851");
            var Q1527;
            Q1527=sQuery(id+"F0.wireOp",EDGE,"E995");
            var Q1528;
            Q1528=sQuery(id+"F0.wireOp",EDGE,"E2321");
            var Q1529;
            Q1529=sQuery(id+"F0.wireOp",EDGE,"E1313");
            var Q1530;
            Q1530=sQuery(id+"F0.wireOp",EDGE,"E2344");
            var Q1531;
            Q1531=sQuery(id+"F0.wireOp",EDGE,"E2328");
            var Q1532;
            Q1532=sQuery(id+"F0.wireOp",EDGE,"E210");
            var Q1533;
            Q1533=sQuery(id+"F0.wireOp",EDGE,"E2092");
            var Q1534;
            Q1534=sQuery(id+"F0.wireOp",EDGE,"E1534");
            var Q1535;
            Q1535=sQuery(id+"F0.wireOp",EDGE,"E2161");
            var Q1536;
            Q1536=sQuery(id+"F0.wireOp",EDGE,"E1454");
            var Q1537;
            Q1537=sQuery(id+"F0.wireOp",EDGE,"E1620");
            var Q1538;
            Q1538=sQuery(id+"F0.wireOp",EDGE,"E1632");
            var Q1539;
            Q1539=sQuery(id+"F0.wireOp",EDGE,"E898");
            var Q1540;
            Q1540=sQuery(id+"F0.wireOp",EDGE,"E1604");
            var Q1541;
            Q1541=sQuery(id+"F0.wireOp",EDGE,"E834");
            var Q1542;
            Q1542=sQuery(id+"F0.wireOp",EDGE,"E626");
            var Q1543;
            Q1543=sQuery(id+"F0.wireOp",EDGE,"E1390");
            var Q1544;
            Q1544=sQuery(id+"F0.wireOp",EDGE,"E1895");
            var Q1545;
            Q1545=sQuery(id+"F0.wireOp",EDGE,"E242");
            var Q1546;
            Q1546=sQuery(id+"F0.wireOp",EDGE,"E721");
            var Q1547;
            Q1547=sQuery(id+"F0.wireOp",EDGE,"E737");
            var Q1548;
            Q1548=sQuery(id+"F0.wireOp",EDGE,"E673");
            var Q1549;
            Q1549=sQuery(id+"F0.wireOp",EDGE,"E625");
            var Q1550;
            Q1550=sQuery(id+"F0.wireOp",EDGE,"E994");
            var Q1551;
            Q1551=sQuery(id+"F0.wireOp",EDGE,"E113");
            var Q1552;
            Q1552=sQuery(id+"F0.wireOp",EDGE,"E1460");
            var Q1553;
            Q1553=sQuery(id+"F0.wireOp",EDGE,"E1392");
            var Q1554;
            Q1554=sQuery(id+"F0.wireOp",EDGE,"E433");
            var Q1555;
            Q1555=sQuery(id+"F0.wireOp",EDGE,"E1547");
            var Q1556;
            Q1556=sQuery(id+"F0.wireOp",EDGE,"E2061");
            var Q1557;
            Q1557=sQuery(id+"F0.wireOp",EDGE,"E1531");
            var Q1558;
            Q1558=sQuery(id+"F0.wireOp",EDGE,"E321");
            var Q1559;
            Q1559=sQuery(id+"F0.wireOp",EDGE,"E2352");
            var Q1560;
            Q1560=sQuery(id+"F0.wireOp",EDGE,"E2005");
            var Q1561;
            Q1561=sQuery(id+"F0.wireOp",EDGE,"E241");
            var Q1562;
            Q1562=sQuery(id+"F0.wireOp",EDGE,"E193");
            var Q1563;
            Q1563=sQuery(id+"F0.wireOp",EDGE,"E784");
            var Q1564;
            Q1564=sQuery(id+"F0.wireOp",EDGE,"E704");
            var Q1565;
            Q1565=sQuery(id+"F0.wireOp",EDGE,"E1312");
            var Q1566;
            Q1566=sQuery(id+"F0.wireOp",EDGE,"E2336");
            var Q1567;
            Q1567=sQuery(id+"F0.wireOp",EDGE,"E752");
            var Q1568;
            Q1568=sQuery(id+"F0.wireOp",EDGE,"E656");
            var Q1569;
            Q1569=sQuery(id+"F0.wireOp",EDGE,"E672");
            var Q1570;
            Q1570=sQuery(id+"F0.wireOp",EDGE,"E880");
            var Q1571;
            Q1571=sQuery(id+"F0.wireOp",EDGE,"E928");
            var Q1572;
            Q1572=sQuery(id+"F0.wireOp",EDGE,"E432");
            var Q1573;
            Q1573=sQuery(id+"F0.wireOp",EDGE,"E240");
            var Q1574;
            Q1574=sQuery(id+"F0.wireOp",EDGE,"E160");
            var Q1575;
            Q1575=sQuery(id+"F0.wireOp",EDGE,"E176");
            var Q1576;
            Q1576=sQuery(id+"F0.wireOp",EDGE,"E239");
            var Q1577;
            Q1577=sQuery(id+"F0.wireOp",EDGE,"E271");
            var Q1578;
            Q1578=sQuery(id+"F0.wireOp",EDGE,"E191");
            var Q1579;
            Q1579=sQuery(id+"F0.wireOp",EDGE,"E783");
            var Q1580;
            Q1580=sQuery(id+"F0.wireOp",EDGE,"E2391");
            var Q1581;
            Q1581=sQuery(id+"F0.wireOp",EDGE,"E655");
            var Q1582;
            Q1582=sQuery(id+"F0.wireOp",EDGE,"E623");
            var Q1583;
            Q1583=sQuery(id+"F0.wireOp",EDGE,"E559");
            var Q1584;
            Q1584=sQuery(id+"F0.wireOp",EDGE,"E943");
            var Q1585;
            Q1585=sQuery(id+"F0.wireOp",EDGE,"E991");
            var Q1586;
            Q1586=sQuery(id+"F0.wireOp",EDGE,"E590");
            var Q1587;
            Q1587=sQuery(id+"F0.wireOp",EDGE,"E446");
            var Q1588;
            Q1588=sQuery(id+"F0.wireOp",EDGE,"E829");
            var Q1589;
            Q1589=sQuery(id+"F0.wireOp",EDGE,"E878");
            var Q1590;
            Q1590=sQuery(id+"F0.wireOp",EDGE,"E894");
            var Q1591;
            Q1591=sQuery(id+"F0.wireOp",EDGE,"E862");
            var Q1592;
            Q1592=sQuery(id+"F0.wireOp",EDGE,"E1726");
            var Q1593;
            Q1593=sQuery(id+"F0.wireOp",EDGE,"E221");
            var Q1594;
            Q1594=sQuery(id+"F0.wireOp",EDGE,"E189");
            var Q1595;
            Q1595=sQuery(id+"F0.wireOp",EDGE,"E749");
            var Q1596;
            Q1596=sQuery(id+"F0.wireOp",EDGE,"E717");
            var Q1597;
            Q1597=sQuery(id+"F0.wireOp",EDGE,"E669");
            var Q1598;
            Q1598=sQuery(id+"F0.wireOp",EDGE,"E685");
            var Q1599;
            Q1599=sQuery(id+"F0.wireOp",EDGE,"E861");
            var Q1600;
            Q1600=sQuery(id+"F0.wireOp",EDGE,"E2059");
            var Q1601;
            Q1601=sQuery(id+"F0.wireOp",EDGE,"E1238");
            var Q1602;
            Q1602=sQuery(id+"F0.wireOp",EDGE,"E2182");
            var Q1603;
            Q1603=sQuery(id+"F0.wireOp",EDGE,"E1190");
            var Q1604;
            Q1604=sQuery(id+"F0.wireOp",EDGE,"E1972");
            var Q1605;
            Q1605=sQuery(id+"F0.wireOp",EDGE,"E1126");
            var Q1606;
            Q1606=sQuery(id+"F0.wireOp",EDGE,"E1979");
            var Q1607;
            Q1607=sQuery(id+"F0.wireOp",EDGE,"E2327");
            var Q1608;
            Q1608=sQuery(id+"F0.wireOp",EDGE,"E1152");
            var Q1609;
            Q1609=sQuery(id+"F0.wireOp",EDGE,"E2160");
            var Q1610;
            Q1610=sQuery(id+"F0.wireOp",EDGE,"E2279");
            var Q1611;
            Q1611=sQuery(id+"F0.wireOp",EDGE,"E1852");
            var Q1612;
            Q1612=sQuery(id+"F0.wireOp",EDGE,"E1255");
            var Q1613;
            Q1613=sQuery(id+"F0.wireOp",EDGE,"E2382");
            var Q1614;
            Q1614=sQuery(id+"F0.wireOp",EDGE,"E1088");
            var Q1615;
            Q1615=sQuery(id+"F0.wireOp",EDGE,"E1079");
            var Q1616;
            Q1616=sQuery(id+"F0.wireOp",EDGE,"E1111");
            var Q1617;
            Q1617=sQuery(id+"F0.wireOp",EDGE,"E2119");
            var Q1618;
            Q1618=sQuery(id+"F0.wireOp",EDGE,"E2318");
            var Q1619;
            Q1619=sQuery(id+"F0.wireOp",EDGE,"E1708");
            var Q1620;
            Q1620=sQuery(id+"F0.wireOp",EDGE,"E1638");
            var Q1621;
            Q1621=sQuery(id+"F0.wireOp",EDGE,"E1183");
            var Q1622;
            Q1622=sQuery(id+"F0.wireOp",EDGE,"E1740");
            var Q1623;
            Q1623=sQuery(id+"F0.wireOp",EDGE,"E2095");
            var Q1624;
            Q1624=sQuery(id+"F0.wireOp",EDGE,"E2038");
            var Q1625;
            Q1625=sQuery(id+"F0.wireOp",EDGE,"E700");
            var Q1626;
            Q1626=sQuery(id+"F0.wireOp",EDGE,"E2110");
            var Q1627;
            Q1627=sQuery(id+"F0.wireOp",EDGE,"E412");
            var Q1628;
            Q1628=sQuery(id+"F0.wireOp",EDGE,"E1628");
            var Q1629;
            Q1629=sQuery(id+"F0.wireOp",EDGE,"E156");
            var Q1630;
            Q1630=sQuery(id+"F0.wireOp",EDGE,"E124");
            var Q1631;
            Q1631=sQuery(id+"F0.wireOp",EDGE,"E699");
            var Q1632;
            Q1632=sQuery(id+"F0.wireOp",EDGE,"E619");
            var Q1633;
            Q1633=sQuery(id+"F0.wireOp",EDGE,"E507");
            var Q1634;
            Q1634=sQuery(id+"F0.wireOp",EDGE,"E411");
            var Q1635;
            Q1635=sQuery(id+"F0.wireOp",EDGE,"E1493");
            var Q1636;
            Q1636=sQuery(id+"F0.wireOp",EDGE,"E2011");
            var Q1637;
            Q1637=sQuery(id+"F0.wireOp",EDGE,"E971");
            var Q1638;
            Q1638=sQuery(id+"F0.wireOp",EDGE,"E219");
            var Q1639;
            Q1639=sQuery(id+"F0.wireOp",EDGE,"E171");
            var Q1640;
            Q1640=sQuery(id+"F0.wireOp",EDGE,"E2390");
            var Q1641;
            Q1641=sQuery(id+"F0.wireOp",EDGE,"E1982");
            var Q1642;
            Q1642=sQuery(id+"F0.wireOp",EDGE,"E2421");
            var Q1643;
            Q1643=sQuery(id+"F0.wireOp",EDGE,"E1397");
            var Q1644;
            Q1644=sQuery(id+"F0.wireOp",EDGE,"E2310");
            var Q1645;
            Q1645=sQuery(id+"F0.wireOp",EDGE,"E154");
            var Q1646;
            Q1646=sQuery(id+"F0.wireOp",EDGE,"E986");
            var Q1647;
            Q1647=sQuery(id+"F0.wireOp",EDGE,"E1451");
            var Q1648;
            Q1648=sQuery(id+"F0.wireOp",EDGE,"E617");
            var Q1649;
            Q1649=sQuery(id+"F0.wireOp",EDGE,"E409");
            var Q1650;
            Q1650=sQuery(id+"F0.wireOp",EDGE,"E2342");
            var Q1651;
            Q1651=sQuery(id+"F0.wireOp",EDGE,"E1805");
            var Q1652;
            Q1652=sQuery(id+"F0.wireOp",EDGE,"E1647");
            var Q1653;
            Q1653=sQuery(id+"F0.wireOp",EDGE,"E1709");
            var Q1654;
            Q1654=sQuery(id+"F0.wireOp",EDGE,"E153");
            var Q1655;
            Q1655=sQuery(id+"F0.wireOp",EDGE,"E185");
            var Q1656;
            Q1656=sQuery(id+"F0.wireOp",EDGE,"E824");
            var Q1657;
            Q1657=sQuery(id+"F0.wireOp",EDGE,"E1934");
            var Q1658;
            Q1658=sQuery(id+"F0.wireOp",EDGE,"E152");
            var Q1659;
            Q1659=sQuery(id+"F0.wireOp",EDGE,"E487");
            var Q1660;
            Q1660=sQuery(id+"F0.wireOp",EDGE,"E2411");
            var Q1661;
            Q1661=sQuery(id+"F0.wireOp",EDGE,"E199");
            var Q1662;
            Q1662=sQuery(id+"F0.wireOp",EDGE,"E151");
            var Q1663;
            Q1663=sQuery(id+"F0.wireOp",EDGE,"E167");
            var Q1664;
            Q1664=sQuery(id+"F0.wireOp",EDGE,"E615");
            var Q1665;
            Q1665=sQuery(id+"F0.wireOp",EDGE,"E1324");
            var Q1666;
            Q1666=sQuery(id+"F0.wireOp",EDGE,"E2397");
            var Q1667;
            Q1667=sQuery(id+"F0.wireOp",EDGE,"E294");
            var Q1668;
            Q1668=sQuery(id+"F0.wireOp",EDGE,"E2388");
            var Q1669;
            Q1669=sQuery(id+"F0.wireOp",EDGE,"E2325");
            var Q1670;
            Q1670=sQuery(id+"F0.wireOp",EDGE,"E134");
            var Q1671;
            Q1671=sQuery(id+"F0.wireOp",EDGE,"E118");
            var Q1672;
            Q1672=sQuery(id+"F0.wireOp",EDGE,"E678");
            var Q1673;
            Q1673=sQuery(id+"F0.wireOp",EDGE,"E694");
            var Q1674;
            Q1674=sQuery(id+"F0.wireOp",EDGE,"E502");
            var Q1675;
            Q1675=sQuery(id+"F0.wireOp",EDGE,"E982");
            var Q1676;
            Q1676=sQuery(id+"F0.wireOp",EDGE,"E1748");
            var Q1677;
            Q1677=sQuery(id+"F0.wireOp",EDGE,"E2333");
            var Q1678;
            Q1678=sQuery(id+"F0.wireOp",EDGE,"E405");
            var Q1679;
            Q1679=sQuery(id+"F0.wireOp",EDGE,"E229");
            var Q1680;
            Q1680=sQuery(id+"F0.wireOp",EDGE,"E245");
            var Q1681;
            Q1681=sQuery(id+"F0.wireOp",EDGE,"E165");
            var Q1682;
            Q1682=sQuery(id+"F0.wireOp",EDGE,"E117");
            var Q1683;
            Q1683=sQuery(id+"F0.wireOp",EDGE,"E1253");
            var Q1684;
            Q1684=sQuery(id+"F0.wireOp",EDGE,"E2332");
            var Q1685;
            Q1685=sQuery(id+"F0.wireOp",EDGE,"E2317");
            var Q1686;
            Q1686=sQuery(id+"F0.wireOp",EDGE,"E821");
            var Q1687;
            Q1687=sQuery(id+"F0.wireOp",EDGE,"E2117");
            var Q1688;
            Q1688=sQuery(id+"F0.wireOp",EDGE,"E677");
            var Q1689;
            Q1689=sQuery(id+"F0.wireOp",EDGE,"E693");
            var Q1690;
            Q1690=sQuery(id+"F0.wireOp",EDGE,"E2172");
            var Q1691;
            Q1691=sQuery(id+"F0.wireOp",EDGE,"E629");
            var Q1692;
            Q1692=sQuery(id+"F0.wireOp",EDGE,"E613");
            var Q1693;
            Q1693=sQuery(id+"F0.wireOp",EDGE,"E1391");
            var Q1694;
            Q1694=sQuery(id+"F0.wireOp",EDGE,"E981");
            var Q1695;
            Q1695=sQuery(id+"F0.wireOp",EDGE,"E1237");
            var Q1696;
            Q1696=sQuery(id+"F0.wireOp",EDGE,"E2292");
            var Q1697;
            Q1697=sQuery(id+"F0.wireOp",EDGE,"E2426");
            var Q1698;
            Q1698=sQuery(id+"F0.wireOp",EDGE,"E2347");
            var Q1699;
            Q1699=sQuery(id+"F0.wireOp",EDGE,"E1402");
            var Q1700;
            Q1700=sQuery(id+"F0.wireOp",EDGE,"E292");
            var Q1701;
            Q1701=sQuery(id+"F0.wireOp",EDGE,"E2419");
            var Q1702;
            Q1702=sQuery(id+"F0.wireOp",EDGE,"E2403");
            var Q1703;
            Q1703=sQuery(id+"F0.wireOp",EDGE,"E148");
            var Q1704;
            Q1704=sQuery(id+"F0.wireOp",EDGE,"E2149");
            var Q1705;
            Q1705=sQuery(id+"F0.wireOp",EDGE,"E2340");
            var Q1706;
            Q1706=sQuery(id+"F0.wireOp",EDGE,"E660");
            var Q1707;
            Q1707=sQuery(id+"F0.wireOp",EDGE,"E1322");
            var Q1708;
            Q1708=sQuery(id+"F0.wireOp",EDGE,"E676");
            var Q1709;
            Q1709=sQuery(id+"F0.wireOp",EDGE,"E2291");
            var Q1710;
            Q1710=sQuery(id+"F0.wireOp",EDGE,"E1885");
            var Q1711;
            Q1711=sQuery(id+"F0.wireOp",EDGE,"E2282");
            var Q1712;
            Q1712=sQuery(id+"F0.wireOp",EDGE,"E1251");
            var Q1713;
            Q1713=sQuery(id+"F0.wireOp",EDGE,"E1091");
            var Q1714;
            Q1714=sQuery(id+"F0.wireOp",EDGE,"E1146");
            var Q1715;
            Q1715=sQuery(id+"F0.wireOp",EDGE,"E2202");
            var Q1716;
            Q1716=sQuery(id+"F0.wireOp",EDGE,"E1123");
            var Q1717;
            Q1717=sQuery(id+"F0.wireOp",EDGE,"E1082");
            var Q1718;
            Q1718=sQuery(id+"F0.wireOp",EDGE,"E1795");
            var Q1719;
            Q1719=sQuery(id+"F0.wireOp",EDGE,"E1818");
            var Q1720;
            Q1720=sQuery(id+"F0.wireOp",EDGE,"E1811");
            var Q1721;
            Q1721=sQuery(id+"F0.wireOp",EDGE,"E1802");
            var Q1722;
            Q1722=sQuery(id+"F0.wireOp",EDGE,"E1786");
            var Q1723;
            Q1723=sQuery(id+"F0.wireOp",EDGE,"E1635");
            var Q1724;
            Q1724=sQuery(id+"F0.wireOp",EDGE,"E1642");
            var Q1725;
            Q1725=sQuery(id+"F0.wireOp",EDGE,"E1491");
            var Q1726;
            Q1726=sQuery(id+"F0.wireOp",EDGE,"E1450");
            var Q1727;
            Q1727=sQuery(id+"F0.wireOp",EDGE,"E2331");
            var Q1728;
            Q1728=sQuery(id+"F0.wireOp",EDGE,"E1307");
            var Q1729;
            Q1729=sQuery(id+"F0.wireOp",EDGE,"E1196");
            var Q1730;
            Q1730=sQuery(id+"F0.wireOp",EDGE,"E1785");
            var Q1731;
            Q1731=sQuery(id+"F0.wireOp",EDGE,"E1769");
            var Q1732;
            Q1732=sQuery(id+"F0.wireOp",EDGE,"E2180");
            var Q1733;
            Q1733=sQuery(id+"F0.wireOp",EDGE,"E1218");
            var Q1734;
            Q1734=sQuery(id+"F0.wireOp",EDGE,"E2281");
            var Q1735;
            Q1735=sQuery(id+"F0.wireOp",EDGE,"E996");
            var Q1736;
            Q1736=sQuery(id+"F0.wireOp",EDGE,"E1193");
            var Q1737;
            Q1737=sQuery(id+"F0.wireOp",EDGE,"E1241");
            var Q1738;
            Q1738=sQuery(id+"F0.wireOp",EDGE,"E1225");
            var Q1739;
            Q1739=sQuery(id+"F0.wireOp",EDGE,"E1227");
            var Q1740;
            Q1740=sQuery(id+"F0.wireOp",EDGE,"E1145");
            var Q1741;
            Q1741=sQuery(id+"F0.wireOp",EDGE,"E1090");
            var Q1742;
            Q1742=sQuery(id+"F0.wireOp",EDGE,"E2098");
            var Q1743;
            Q1743=sQuery(id+"F0.wireOp",EDGE,"E1876");
            var Q1744;
            Q1744=sQuery(id+"F0.wireOp",EDGE,"E1122");
            var Q1745;
            Q1745=sQuery(id+"F0.wireOp",EDGE,"E1177");
            var Q1746;
            Q1746=sQuery(id+"F0.wireOp",EDGE,"E1081");
            var Q1747;
            Q1747=sQuery(id+"F0.wireOp",EDGE,"E1189");
            var Q1748;
            Q1748=sQuery(id+"F0.wireOp",EDGE,"E195");
            var Q1749;
            Q1749=sQuery(id+"F0.wireOp",EDGE,"E1739");
            var Q1750;
            Q1750=sQuery(id+"F0.wireOp",EDGE,"E1172");
            var Q1751;
            Q1751=sQuery(id+"F0.wireOp",EDGE,"E131");
            var Q1752;
            Q1752=sQuery(id+"F0.wireOp",EDGE,"E147");
            var Q1753;
            Q1753=sQuery(id+"F0.wireOp",EDGE,"E1634");
            var Q1754;
            Q1754=sQuery(id+"F0.wireOp",EDGE,"E1737");
            var Q1755;
            Q1755=sQuery(id+"F0.wireOp",EDGE,"E1641");
            var Q1756;
            Q1756=sQuery(id+"F0.wireOp",EDGE,"E1245");
            var Q1757;
            Q1757=sQuery(id+"F0.wireOp",EDGE,"E1442");
            var Q1758;
            Q1758=sQuery(id+"F0.wireOp",EDGE,"E1092");
            var Q1759;
            Q1759=sQuery(id+"F0.wireOp",EDGE,"E2425");
            var Q1760;
            Q1760=sQuery(id+"F0.wireOp",EDGE,"E1401");
            var Q1761;
            Q1761=sQuery(id+"F0.wireOp",EDGE,"E1394");
            var Q1762;
            Q1762=sQuery(id+"F0.wireOp",EDGE,"E2418");
            var Q1763;
            Q1763=sQuery(id+"F0.wireOp",EDGE,"E2402");
            var Q1764;
            Q1764=sQuery(id+"F0.wireOp",EDGE,"E2306");
            var Q1765;
            Q1765=sQuery(id+"F0.wireOp",EDGE,"E1076");
            var Q1766;
            Q1766=sQuery(id+"F0.wireOp",EDGE,"E2290");
            var Q1767;
            Q1767=sQuery(id+"F0.wireOp",EDGE,"E2287");
            var Q1768;
            Q1768=sQuery(id+"F0.wireOp",EDGE,"E1793");
            var Q1769;
            Q1769=sQuery(id+"F0.wireOp",EDGE,"E1809");
            var Q1770;
            Q1770=sQuery(id+"F0.wireOp",EDGE,"E1816");
            var Q1771;
            Q1771=sQuery(id+"F0.wireOp",EDGE,"E1800");
            var Q1772;
            Q1772=sQuery(id+"F0.wireOp",EDGE,"E1179");
            var Q1773;
            Q1773=sQuery(id+"F0.wireOp",EDGE,"E2335");
            var Q1774;
            Q1774=sQuery(id+"F0.wireOp",EDGE,"E1144");
            var Q1775;
            Q1775=sQuery(id+"F0.wireOp",EDGE,"E2113");
            var Q1776;
            Q1776=sQuery(id+"F0.wireOp",EDGE,"E1128");
            var Q1777;
            Q1777=sQuery(id+"F0.wireOp",EDGE,"E2104");
            var Q1778;
            Q1778=sQuery(id+"F0.wireOp",EDGE,"E770");
            var Q1779;
            Q1779=sQuery(id+"F0.wireOp",EDGE,"E1311");
            var Q1780;
            Q1780=sQuery(id+"F0.wireOp",EDGE,"E1496");
            var Q1781;
            Q1781=sQuery(id+"F0.wireOp",EDGE,"E1489");
            var Q1782;
            Q1782=sQuery(id+"F0.wireOp",EDGE,"E2385");
            var Q1783;
            Q1783=sQuery(id+"F0.wireOp",EDGE,"E2424");
            var Q1784;
            Q1784=sQuery(id+"F0.wireOp",EDGE,"E1400");
            var Q1785;
            Q1785=sQuery(id+"F0.wireOp",EDGE,"E2417");
            var Q1786;
            Q1786=sQuery(id+"F0.wireOp",EDGE,"E1518");
            var Q1787;
            Q1787=sQuery(id+"F0.wireOp",EDGE,"E2337");
            var Q1788;
            Q1788=sQuery(id+"F0.wireOp",EDGE,"E1256");
            var Q1789;
            Q1789=sQuery(id+"F0.wireOp",EDGE,"E194");
            var Q1790;
            Q1790=sQuery(id+"F0.wireOp",EDGE,"E1320");
            var Q1791;
            Q1791=sQuery(id+"F0.wireOp",EDGE,"E1249");
            var Q1792;
            Q1792=sQuery(id+"F0.wireOp",EDGE,"E1792");
            var Q1793;
            Q1793=sQuery(id+"F0.wireOp",EDGE,"E1776");
            var Q1794;
            Q1794=sQuery(id+"F0.wireOp",EDGE,"E1486");
            var Q1795;
            Q1795=sQuery(id+"F0.wireOp",EDGE,"E1639");
            var Q1796;
            Q1796=sQuery(id+"F0.wireOp",EDGE,"E1552");
            var Q1797;
            Q1797=sQuery(id+"F0.wireOp",EDGE,"E1495");
            var Q1798;
            Q1798=sQuery(id+"F0.wireOp",EDGE,"E978");
            var Q1799;
            Q1799=sQuery(id+"F0.wireOp",EDGE,"E1488");
            var Q1800;
            Q1800=sQuery(id+"F0.wireOp",EDGE,"E2043");
            var Q1801;
            Q1801=sQuery(id+"F0.wireOp",EDGE,"E882");
            var Q1802;
            Q1802=sQuery(id+"F0.wireOp",EDGE,"E450");
            var Q1803;
            Q1803=sQuery(id+"F0.wireOp",EDGE,"E1952");
            var Q1804;
            Q1804=sQuery(id+"F0.wireOp",EDGE,"E1856");
            var Q1805;
            Q1805=sQuery(id+"F0.wireOp",EDGE,"E1959");
            var Q1806;
            Q1806=sQuery(id+"F0.wireOp",EDGE,"E2039");
            var Q1807;
            Q1807=sQuery(id+"F0.wireOp",EDGE,"E290");
            var Q1808;
            Q1808=sQuery(id+"F0.wireOp",EDGE,"E2189");
            var Q1809;
            Q1809=sQuery(id+"F0.wireOp",EDGE,"E2414");
            var Q1810;
            Q1810=sQuery(id+"F0.wireOp",EDGE,"E817");
            var Q1811;
            Q1811=sQuery(id+"F0.wireOp",EDGE,"E1447");
            var Q1812;
            Q1812=sQuery(id+"F0.wireOp",EDGE,"E977");
            var Q1813;
            Q1813=sQuery(id+"F0.wireOp",EDGE,"E1973");
            var Q1814;
            Q1814=sQuery(id+"F0.wireOp",EDGE,"E2423");
            var Q1815;
            Q1815=sQuery(id+"F0.wireOp",EDGE,"E993");
            var Q1816;
            Q1816=sQuery(id+"F0.wireOp",EDGE,"E2320");
            var Q1817;
            Q1817=sQuery(id+"F0.wireOp",EDGE,"E289");
            var Q1818;
            Q1818=sQuery(id+"F0.wireOp",EDGE,"E225");
            var Q1819;
            Q1819=sQuery(id+"F0.wireOp",EDGE,"E161");
            var Q1820;
            Q1820=sQuery(id+"F0.wireOp",EDGE,"E624");
            var Q1821;
            Q1821=sQuery(id+"F0.wireOp",EDGE,"E976");
            var Q1822;
            Q1822=sQuery(id+"F0.wireOp",EDGE,"E992");
            var Q1823;
            Q1823=sQuery(id+"F0.wireOp",EDGE,"E288");
            var Q1824;
            Q1824=sQuery(id+"F0.wireOp",EDGE,"E224");
            var Q1825;
            Q1825=sQuery(id+"F0.wireOp",EDGE,"E1854");
            var Q1826;
            Q1826=sQuery(id+"F0.wireOp",EDGE,"E287");
            var Q1827;
            Q1827=sQuery(id+"F0.wireOp",EDGE,"E159");
            var Q1828;
            Q1828=sQuery(id+"F0.wireOp",EDGE,"E175");
            var Q1829;
            Q1829=sQuery(id+"F0.wireOp",EDGE,"E207");
            var Q1830;
            Q1830=sQuery(id+"F0.wireOp",EDGE,"E1861");
            var Q1831;
            Q1831=sQuery(id+"F0.wireOp",EDGE,"E2037");
            var Q1832;
            Q1832=sQuery(id+"F0.wireOp",EDGE,"E751");
            var Q1833;
            Q1833=sQuery(id+"F0.wireOp",EDGE,"E671");
            var Q1834;
            Q1834=sQuery(id+"F0.wireOp",EDGE,"E431");
            var Q1835;
            Q1835=sQuery(id+"F0.wireOp",EDGE,"E1007");
            var Q1836;
            Q1836=sQuery(id+"F0.wireOp",EDGE,"E238");
            var Q1837;
            Q1837=sQuery(id+"F0.wireOp",EDGE,"E766");
            var Q1838;
            Q1838=sQuery(id+"F0.wireOp",EDGE,"E782");
            var Q1839;
            Q1839=sQuery(id+"F0.wireOp",EDGE,"E654");
            var Q1840;
            Q1840=sQuery(id+"F0.wireOp",EDGE,"E1742");
            var Q1841;
            Q1841=sQuery(id+"F0.wireOp",EDGE,"E765");
            var Q1842;
            Q1842=sQuery(id+"F0.wireOp",EDGE,"E2044");
            var Q1843;
            Q1843=sQuery(id+"F0.wireOp",EDGE,"E1646");
            var Q1844;
            Q1844=sQuery(id+"F0.wireOp",EDGE,"E173");
            var Q1845;
            Q1845=sQuery(id+"F0.wireOp",EDGE,"E1630");
            var Q1846;
            Q1846=sQuery(id+"F0.wireOp",EDGE,"E653");
            var Q1847;
            Q1847=sQuery(id+"F0.wireOp",EDGE,"E589");
            var Q1848;
            Q1848=sQuery(id+"F0.wireOp",EDGE,"E445");
            var Q1849;
            Q1849=sQuery(id+"F0.wireOp",EDGE,"E461");
            var Q1850;
            Q1850=sQuery(id+"F0.wireOp",EDGE,"E413");
            var Q1851;
            Q1851=sQuery(id+"F0.wireOp",EDGE,"E877");
            var Q1852;
            Q1852=sQuery(id+"F0.wireOp",EDGE,"E893");
            var Q1853;
            Q1853=sQuery(id+"F0.wireOp",EDGE,"E1142");
            var Q1854;
            Q1854=sQuery(id+"F0.wireOp",EDGE,"E2166");
            var Q1855;
            Q1855=sQuery(id+"F0.wireOp",EDGE,"E2004");
            var Q1856;
            Q1856=sQuery(id+"F0.wireOp",EDGE,"E1110");
            var Q1857;
            Q1857=sQuery(id+"F0.wireOp",EDGE,"E1974");
            var Q1858;
            Q1858=sQuery(id+"F0.wireOp",EDGE,"E1143");
            var Q1859;
            Q1859=sQuery(id+"F0.wireOp",EDGE,"E2112");
            var Q1860;
            Q1860=sQuery(id+"F0.wireOp",EDGE,"E1127");
            var Q1861;
            Q1861=sQuery(id+"F0.wireOp",EDGE,"E1701");
            var Q1862;
            Q1862=sQuery(id+"F0.wireOp",EDGE,"E2103");
            var Q1863;
            Q1863=sQuery(id+"F0.wireOp",EDGE,"E2286");
            var Q1864;
            Q1864=sQuery(id+"F0.wireOp",EDGE,"E2334");
            var Q1865;
            Q1865=sQuery(id+"F0.wireOp",EDGE,"E1958");
            var Q1866;
            Q1866=sQuery(id+"F0.wireOp",EDGE,"E1775");
            var Q1867;
            Q1867=sQuery(id+"F0.wireOp",EDGE,"E1855");
            var Q1868;
            Q1868=sQuery(id+"F0.wireOp",EDGE,"E1214");
            var Q1869;
            Q1869=sQuery(id+"F0.wireOp",EDGE,"E1791");
            var Q1870;
            Q1870=sQuery(id+"F0.wireOp",EDGE,"E1198");
            var Q1871;
            Q1871=sQuery(id+"F0.wireOp",EDGE,"E1942");
            var Q1872;
            Q1872=sQuery(id+"F0.wireOp",EDGE,"E1247");
            var Q1873;
            Q1873=sQuery(id+"F0.wireOp",EDGE,"E1151");
            var Q1874;
            Q1874=sQuery(id+"F0.wireOp",EDGE,"E1087");
            var Q1875;
            Q1875=sQuery(id+"F0.wireOp",EDGE,"E2079");
            var Q1876;
            Q1876=sQuery(id+"F0.wireOp",EDGE,"E2429");
            var Q1877;
            Q1877=sQuery(id+"F0.wireOp",EDGE,"E1446");
            var Q1878;
            Q1878=sQuery(id+"F0.wireOp",EDGE,"E1494");
            var Q1879;
            Q1879=sQuery(id+"F0.wireOp",EDGE,"E1150");
            var Q1880;
            Q1880=sQuery(id+"F0.wireOp",EDGE,"E636");
            var Q1881;
            Q1881=sQuery(id+"F0.wireOp",EDGE,"E492");
            var Q1882;
            Q1882=sQuery(id+"F0.wireOp",EDGE,"E540");
            var Q1883;
            Q1883=sQuery(id+"F0.wireOp",EDGE,"E428");
            var Q1884;
            Q1884=sQuery(id+"F0.wireOp",EDGE,"E956");
            var Q1885;
            Q1885=sQuery(id+"F0.wireOp",EDGE,"E2094");
            var Q1886;
            Q1886=sQuery(id+"F0.wireOp",EDGE,"E2422");
            var Q1887;
            Q1887=sQuery(id+"F0.wireOp",EDGE,"E204");
            var Q1888;
            Q1888=sQuery(id+"F0.wireOp",EDGE,"E1389");
            var Q1889;
            Q1889=sQuery(id+"F0.wireOp",EDGE,"E635");
            var Q1890;
            Q1890=sQuery(id+"F0.wireOp",EDGE,"E1956");
            var Q1891;
            Q1891=sQuery(id+"F0.wireOp",EDGE,"E2413");
            var Q1892;
            Q1892=sQuery(id+"F0.wireOp",EDGE,"E123");
            var Q1893;
            Q1893=sQuery(id+"F0.wireOp",EDGE,"E698");
            var Q1894;
            Q1894=sQuery(id+"F0.wireOp",EDGE,"E506");
            var Q1895;
            Q1895=sQuery(id+"F0.wireOp",EDGE,"E490");
            var Q1896;
            Q1896=sQuery(id+"F0.wireOp",EDGE,"E410");
            var Q1897;
            Q1897=sQuery(id+"F0.wireOp",EDGE,"E1366");
            var Q1898;
            Q1898=sQuery(id+"F0.wireOp",EDGE,"E1966");
            var Q1899;
            Q1899=sQuery(id+"F0.wireOp",EDGE,"E202");
            var Q1900;
            Q1900=sQuery(id+"F0.wireOp",EDGE,"E970");
            var Q1901;
            Q1901=sQuery(id+"F0.wireOp",EDGE,"E425");
            var Q1902;
            Q1902=sQuery(id+"F0.wireOp",EDGE,"E2420");
            var Q1903;
            Q1903=sQuery(id+"F0.wireOp",EDGE,"E1789");
            var Q1904;
            Q1904=sQuery(id+"F0.wireOp",EDGE,"E697");
            var Q1905;
            Q1905=sQuery(id+"F0.wireOp",EDGE,"E2326");
            var Q1906;
            Q1906=sQuery(id+"F0.wireOp",EDGE,"E1950");
            var Q1907;
            Q1907=sQuery(id+"F0.wireOp",EDGE,"E1741");
            var Q1908;
            Q1908=sQuery(id+"F0.wireOp",EDGE,"E121");
            var Q1909;
            Q1909=sQuery(id+"F0.wireOp",EDGE,"E424");
            var Q1910;
            Q1910=sQuery(id+"F0.wireOp",EDGE,"E408");
            var Q1911;
            Q1911=sQuery(id+"F0.wireOp",EDGE,"E1645");
            var Q1912;
            Q1912=sQuery(id+"F0.wireOp",EDGE,"E2389");
            var Q1913;
            Q1913=sQuery(id+"F0.wireOp",EDGE,"E200");
            var Q1914;
            Q1914=sQuery(id+"F0.wireOp",EDGE,"E616");
            var Q1915;
            Q1915=sQuery(id+"F0.wireOp",EDGE,"E1629");
            var Q1916;
            Q1916=sQuery(id+"F0.wireOp",EDGE,"E184");
            var Q1917;
            Q1917=sQuery(id+"F0.wireOp",EDGE,"E2036");
            var Q1918;
            Q1918=sQuery(id+"F0.wireOp",EDGE,"E503");
            var Q1919;
            Q1919=sQuery(id+"F0.wireOp",EDGE,"E2309");
            var Q1920;
            Q1920=sQuery(id+"F0.wireOp",EDGE,"E2404");
            var Q1921;
            Q1921=sQuery(id+"F0.wireOp",EDGE,"E2341");
            var Q1922;
            Q1922=sQuery(id+"F0.wireOp",EDGE,"E2396");
            var Q1923;
            Q1923=sQuery(id+"F0.wireOp",EDGE,"E967");
            var Q1924;
            Q1924=sQuery(id+"F0.wireOp",EDGE,"E1487");
            var Q1925;
            Q1925=sQuery(id+"F0.wireOp",EDGE,"E198");
            var Q1926;
            Q1926=sQuery(id+"F0.wireOp",EDGE,"E1613");
            var Q1927;
            Q1927=sQuery(id+"F0.wireOp",EDGE,"E150");
            var Q1928;
            Q1928=sQuery(id+"F0.wireOp",EDGE,"E2285");
            var Q1929;
            Q1929=sQuery(id+"F0.wireOp",EDGE,"E293");
            var Q1930;
            Q1930=sQuery(id+"F0.wireOp",EDGE,"E197");
            var Q1931;
            Q1931=sQuery(id+"F0.wireOp",EDGE,"E2431");
            var Q1932;
            Q1932=sQuery(id+"F0.wireOp",EDGE,"E421");
            var Q1933;
            Q1933=sQuery(id+"F0.wireOp",EDGE,"E2415");
            var Q1934;
            Q1934=sQuery(id+"F0.wireOp",EDGE,"E1707");
            var Q1935;
            Q1935=sQuery(id+"F0.wireOp",EDGE,"E804");
            var Q1936;
            Q1936=sQuery(id+"F0.wireOp",EDGE,"E1892");
            var Q1937;
            Q1937=sQuery(id+"F0.wireOp",EDGE,"E244");
            var Q1938;
            Q1938=sQuery(id+"F0.wireOp",EDGE,"E164");
            var Q1939;
            Q1939=sQuery(id+"F0.wireOp",EDGE,"E196");
            var Q1940;
            Q1940=sQuery(id+"F0.wireOp",EDGE,"E1363");
            var Q1941;
            Q1941=sQuery(id+"F0.wireOp",EDGE,"E964");
            var Q1942;
            Q1942=sQuery(id+"F0.wireOp",EDGE,"E980");
            var Q1943;
            Q1943=sQuery(id+"F0.wireOp",EDGE,"E2395");
            var Q1944;
            Q1944=sQuery(id+"F0.wireOp",EDGE,"E612");
            var Q1945;
            Q1945=sQuery(id+"F0.wireOp",EDGE,"E628");
            var Q1946;
            Q1946=sQuery(id+"F0.wireOp",EDGE,"E1370");
            var Q1947;
            Q1947=sQuery(id+"F0.wireOp",EDGE,"E1203");
            var Q1948;
            Q1948=sQuery(id+"F0.wireOp",EDGE,"E1210");
            var Q1949;
            Q1949=sQuery(id+"F0.wireOp",EDGE,"E2324");
            var Q1950;
            Q1950=sQuery(id+"F0.wireOp",EDGE,"E2165");
            var Q1951;
            Q1951=sQuery(id+"F0.wireOp",EDGE,"E1814");
            var Q1952;
            Q1952=sQuery(id+"F0.wireOp",EDGE,"E2195");
            var Q1953;
            Q1953=sQuery(id+"F0.wireOp",EDGE,"E1130");
            var Q1954;
            Q1954=sQuery(id+"F0.wireOp",EDGE,"E1107");
            var Q1955;
            Q1955=sQuery(id+"F0.wireOp",EDGE,"E2083");
            var Q1956;
            Q1956=sQuery(id+"F0.wireOp",EDGE,"E2399");
            var Q1957;
            Q1957=sQuery(id+"F0.wireOp",EDGE,"E2074");
            var Q1958;
            Q1958=sQuery(id+"F0.wireOp",EDGE,"E1987");
            var Q1959;
            Q1959=sQuery(id+"F0.wireOp",EDGE,"E1571");
            var Q1960;
            Q1960=sQuery(id+"F0.wireOp",EDGE,"E1236");
            var Q1961;
            Q1961=sQuery(id+"F0.wireOp",EDGE,"E1842");
            var Q1962;
            Q1962=sQuery(id+"F0.wireOp",EDGE,"E1794");
            var Q1963;
            Q1963=sQuery(id+"F0.wireOp",EDGE,"E1810");
            var Q1964;
            Q1964=sQuery(id+"F0.wireOp",EDGE,"E1817");
            var Q1965;
            Q1965=sQuery(id+"F0.wireOp",EDGE,"E1801");
            var Q1966;
            Q1966=sQuery(id+"F0.wireOp",EDGE,"E2026");
            var Q1967;
            Q1967=sQuery(id+"F0.wireOp",EDGE,"E1125");
            var Q1968;
            Q1968=sQuery(id+"F0.wireOp",EDGE,"E1250");
            var Q1969;
            Q1969=sQuery(id+"F0.wireOp",EDGE,"E1209");
            var Q1970;
            Q1970=sQuery(id+"F0.wireOp",EDGE,"E1186");
            var Q1971;
            Q1971=sQuery(id+"F0.wireOp",EDGE,"E1106");
            var Q1972;
            Q1972=sQuery(id+"F0.wireOp",EDGE,"E1945");
            var Q1973;
            Q1973=sQuery(id+"F0.wireOp",EDGE,"E1490");
            var Q1974;
            Q1974=sQuery(id+"F0.wireOp",EDGE,"E1449");
            var Q1975;
            Q1975=sQuery(id+"F0.wireOp",EDGE,"E2171");
            var Q1976;
            Q1976=sQuery(id+"F0.wireOp",EDGE,"E643");
            var Q1977;
            Q1977=sQuery(id+"F0.wireOp",EDGE,"E675");
            var Q1978;
            Q1978=sQuery(id+"F0.wireOp",EDGE,"E1321");
            var Q1979;
            Q1979=sQuery(id+"F0.wireOp",EDGE,"E1841");
            var Q1980;
            Q1980=sQuery(id+"F0.wireOp",EDGE,"E1784");
            var Q1981;
            Q1981=sQuery(id+"F0.wireOp",EDGE,"E1768");
            var Q1982;
            Q1982=sQuery(id+"F0.wireOp",EDGE,"E1640");
            var Q1983;
            Q1983=sQuery(id+"F0.wireOp",EDGE,"E1736");
            var Q1984;
            Q1984=sQuery(id+"F0.wireOp",EDGE,"E1108");
            var Q1985;
            Q1985=sQuery(id+"F0.wireOp",EDGE,"E403");
            var Q1986;
            Q1986=sQuery(id+"F0.wireOp",EDGE,"E291");
            var Q1987;
            Q1987=sQuery(id+"F0.wireOp",EDGE,"E2097");
            var Q1988;
            Q1988=sQuery(id+"F0.wireOp",EDGE,"E1176");
            var Q1989;
            Q1989=sQuery(id+"F0.wireOp",EDGE,"E802");
            var Q1990;
            Q1990=sQuery(id+"F0.wireOp",EDGE,"E642");
            var Q1991;
            Q1991=sQuery(id+"F0.wireOp",EDGE,"E1393");
            var Q1992;
            Q1992=sQuery(id+"F0.wireOp",EDGE,"E2401");
            var Q1993;
            Q1993=sQuery(id+"F0.wireOp",EDGE,"E1228");
            var Q1994;
            Q1994=sQuery(id+"F0.wireOp",EDGE,"E2305");
            var Q1995;
            Q1995=sQuery(id+"F0.wireOp",EDGE,"E1084");
            var Q1996;
            Q1996=sQuery(id+"F0.wireOp",EDGE,"E2392");
            var Q1997;
            Q1997=sQuery(id+"F0.wireOp",EDGE,"E2296");
            var Q1998;
            Q1998=sQuery(id+"F0.wireOp",EDGE,"E1217");
            var Q1999;
            Q1999=sQuery(id+"F0.wireOp",EDGE,"E2280");
            var Q2000;
            Q2000=sQuery(id+"F0.wireOp",EDGE,"E1201");
            var Q2001;
            Q2001=sQuery(id+"F0.wireOp",EDGE,"E2289");
            var Q2002;
            Q2002=sQuery(id+"F0.wireOp",EDGE,"E1208");
            var Q2003;
            Q2003=sQuery(id+"F0.wireOp",EDGE,"E130");
            var Q2004;
            Q2004=sQuery(id+"F0.wireOp",EDGE,"E1192");
            var Q2005;
            Q2005=sQuery(id+"F0.wireOp",EDGE,"E1224");
            var Q2006;
            Q2006=sQuery(id+"F0.wireOp",EDGE,"E1847");
            var Q2007;
            Q2007=sQuery(id+"F0.wireOp",EDGE,"E1808");
            var Q2008;
            Q2008=sQuery(id+"F0.wireOp",EDGE,"E1799");
            var Q2009;
            Q2009=sQuery(id+"F0.wireOp",EDGE,"E1440");
            var Q2010;
            Q2010=sQuery(id+"F0.wireOp",EDGE,"E2430");
            var Q2011;
            Q2011=sQuery(id+"F0.wireOp",EDGE,"E2071");
            var Q2012;
            Q2012=sQuery(id+"F0.wireOp",EDGE,"E2032");
            var Q2013;
            Q2013=sQuery(id+"F0.wireOp",EDGE,"E226");
            var Q2014;
            Q2014=sQuery(id+"F0.wireOp",EDGE,"E769");
            var Q2015;
            Q2015=sQuery(id+"F0.wireOp",EDGE,"E641");
            var Q2016;
            Q2016=sQuery(id+"F0.wireOp",EDGE,"E2109");
            var Q2017;
            Q2017=sQuery(id+"F0.wireOp",EDGE,"E2093");
            var Q2018;
            Q2018=sQuery(id+"F0.wireOp",EDGE,"E961");
            var Q2019;
            Q2019=sQuery(id+"F0.wireOp",EDGE,"E881");
            var Q2020;
            Q2020=sQuery(id+"F0.wireOp",EDGE,"E1515");
            var Q2021;
            Q2021=sQuery(id+"F0.wireOp",EDGE,"E2416");
            var Q2022;
            Q2022=sQuery(id+"F0.wireOp",EDGE,"E2400");
            var Q2023;
            Q2023=sQuery(id+"F0.wireOp",EDGE,"E417");
            var Q2024;
            Q2024=sQuery(id+"F0.wireOp",EDGE,"E209");
            var Q2025;
            Q2025=sQuery(id+"F0.wireOp",EDGE,"E800");
            var Q2026;
            Q2026=sQuery(id+"F0.wireOp",EDGE,"E2407");
            var Q2027;
            Q2027=sQuery(id+"F0.wireOp",EDGE,"E640");
            var Q2028;
            Q2028=sQuery(id+"F0.wireOp",EDGE,"E1980");
            var Q2029;
            Q2029=sQuery(id+"F0.wireOp",EDGE,"E1964");
            var Q2030;
            Q2030=sQuery(id+"F0.wireOp",EDGE,"E496");
            var Q2031;
            Q2031=sQuery(id+"F0.wireOp",EDGE,"E128");
            var Q2032;
            Q2032=sQuery(id+"F0.wireOp",EDGE,"E223");
            var Q2033;
            Q2033=sQuery(id+"F0.wireOp",EDGE,"E127");
            var Q2034;
            Q2034=sQuery(id+"F0.wireOp",EDGE,"E799");
            var Q2035;
            Q2035=sQuery(id+"F0.wireOp",EDGE,"E495");
            var Q2036;
            Q2036=sQuery(id+"F0.wireOp",EDGE,"E975");
            var Q2037;
            Q2037=sQuery(id+"F0.wireOp",EDGE,"E1790");
            var Q2038;
            Q2038=sQuery(id+"F0.wireOp",EDGE,"E158");
            var Q2039;
            Q2039=sQuery(id+"F0.wireOp",EDGE,"E174");
            var Q2040;
            Q2040=sQuery(id+"F0.wireOp",EDGE,"E206");
            var Q2041;
            Q2041=sQuery(id+"F0.wireOp",EDGE,"E798");
            var Q2042;
            Q2042=sQuery(id+"F0.wireOp",EDGE,"E702");
            var Q2043;
            Q2043=sQuery(id+"F0.wireOp",EDGE,"E670");
            var Q2044;
            Q2044=sQuery(id+"F0.wireOp",EDGE,"E622");
            var Q2045;
            Q2045=sQuery(id+"F0.wireOp",EDGE,"E781");
            var Q2046;
            Q2046=sQuery(id+"F0.wireOp",EDGE,"E797");
            var Q2047;
            Q2047=sQuery(id+"F0.wireOp",EDGE,"E990");
            var Q2048;
            Q2048=sQuery(id+"F0.wireOp",EDGE,"E1006");
            var Q2049;
            Q2049=sQuery(id+"F0.wireOp",EDGE,"E237");
            var Q2050;
            Q2050=sQuery(id+"F0.wireOp",EDGE,"E733");
            var Q2051;
            Q2051=sQuery(id+"F0.wireOp",EDGE,"E429");
            var Q2052;
            Q2052=sQuery(id+"F0.wireOp",EDGE,"E1566");
            var Q2053;
            Q2053=sQuery(id+"F0.wireOp",EDGE,"E2278");
            var Q2054;
            Q2054=sQuery(id+"F0.wireOp",EDGE,"E2118");
            var Q2055;
            Q2055=sQuery(id+"F0.wireOp",EDGE,"E2295");
            var Q2056;
            Q2056=sQuery(id+"F0.wireOp",EDGE,"E2288");
            var Q2057;
            Q2057=sQuery(id+"F0.wireOp",EDGE,"E1813");
            var Q2058;
            Q2058=sQuery(id+"F0.wireOp",EDGE,"E1374");
            var Q2059;
            Q2059=sQuery(id+"F0.wireOp",EDGE,"E1207");
            var Q2060;
            Q2060=sQuery(id+"F0.wireOp",EDGE,"E1223");
            var Q2061;
            Q2061=sQuery(id+"F0.wireOp",EDGE,"E2398");
            var Q2062;
            Q2062=sQuery(id+"F0.wireOp",EDGE,"E1191");
            var Q2063;
            Q2063=sQuery(id+"F0.wireOp",EDGE,"E1797");
            var Q2064;
            Q2064=sQuery(id+"F0.wireOp",EDGE,"E1278");
            var Q2065;
            Q2065=sQuery(id+"F0.wireOp",EDGE,"E1175");
            var Q2066;
            Q2066=sQuery(id+"F0.wireOp",EDGE,"E1788");
            var Q2067;
            Q2067=sQuery(id+"F0.wireOp",EDGE,"E1807");
            var Q2068;
            Q2068=sQuery(id+"F0.wireOp",EDGE,"E1637");
            var Q2069;
            Q2069=sQuery(id+"F0.wireOp",EDGE,"E1167");
            var Q2070;
            Q2070=sQuery(id+"F0.wireOp",EDGE,"E2111");
            var Q2071;
            Q2071=sQuery(id+"F0.wireOp",EDGE,"E1230");
            var Q2072;
            Q2072=sQuery(id+"F0.wireOp",EDGE,"E1558");
            var Q2073;
            Q2073=sQuery(id+"F0.wireOp",EDGE,"E444");
            var Q2074;
            Q2074=sQuery(id+"F0.wireOp",EDGE,"E476");
            var Q2075;
            Q2075=sQuery(id+"F0.wireOp",EDGE,"E1564");
            var Q2076;
            Q2076=sQuery(id+"F0.wireOp",EDGE,"E1644");
            var Q2077;
            Q2077=sQuery(id+"F0.wireOp",EDGE,"E1182");
            var Q2078;
            Q2078=sQuery(id+"F0.wireOp",EDGE,"E1963");
            var Q2079;
            Q2079=sQuery(id+"F0.wireOp",EDGE,"E1445");
            var Q2080;
            Q2080=sQuery(id+"F0.wireOp",EDGE,"E1166");
            var Q2081;
            Q2081=sQuery(id+"F0.wireOp",EDGE,"E491");
            var Q2082;
            Q2082=sQuery(id+"F0.wireOp",EDGE,"E427");
            var Q2083;
            Q2083=sQuery(id+"F0.wireOp",EDGE,"E539");
            var Q2084;
            Q2084=sQuery(id+"F0.wireOp",EDGE,"E2078");
            var Q2085;
            Q2085=sQuery(id+"F0.wireOp",EDGE,"E203");
            var Q2086;
            Q2086=sQuery(id+"F0.wireOp",EDGE,"E2406");
            var Q2087;
            Q2087=sQuery(id+"F0.wireOp",EDGE,"E634");
            var Q2088;
            Q2088=sQuery(id+"F0.wireOp",EDGE,"E1821");
            var Q2089;
            Q2089=sQuery(id+"F0.wireOp",EDGE,"E122");
            var Q2090;
            Q2090=sQuery(id+"F0.wireOp",EDGE,"E505");
            var Q2091;
            Q2091=sQuery(id+"F0.wireOp",EDGE,"E1396");
            var Q2092;
            Q2092=sQuery(id+"F0.wireOp",EDGE,"E201");
            var Q2093;
            Q2093=sQuery(id+"F0.wireOp",EDGE,"E568");
            var Q2094;
            Q2094=sQuery(id+"F0.wireOp",EDGE,"E1365");
            var Q2095;
            Q2095=sQuery(id+"F0.wireOp",EDGE,"E696");
            var Q2096;
            Q2096=sQuery(id+"F0.wireOp",EDGE,"E120");
            var Q2097;
            Q2097=sQuery(id+"F0.wireOp",EDGE,"E1403");
            var Q2098;
            Q2098=sQuery(id+"F0.wireOp",EDGE,"E423");
            var Q2099;
            Q2099=sQuery(id+"F0.wireOp",EDGE,"E407");
            var Q2100;
            Q2100=sQuery(id+"F0.wireOp",EDGE,"E567");
            var Q2101;
            Q2101=sQuery(id+"F0.wireOp",EDGE,"E1851");
            var Q2102;
            Q2102=sQuery(id+"F0.wireOp",EDGE,"E614");
            var Q2103;
            Q2103=sQuery(id+"F0.wireOp",EDGE,"E486");
            var Q2104;
            Q2104=sQuery(id+"F0.wireOp",EDGE,"E2300");
            var Q2105;
            Q2105=sQuery(id+"F0.wireOp",EDGE,"E966");
            var Q2106;
            Q2106=sQuery(id+"F0.wireOp",EDGE,"E1846");
            var Q2107;
            Q2107=sQuery(id+"F0.wireOp",EDGE,"E2284");
            var Q2108;
            Q2108=sQuery(id+"F0.wireOp",EDGE,"E149");
            var Q2109;
            Q2109=sQuery(id+"F0.wireOp",EDGE,"E1284");
            var Q2110;
            Q2110=sQuery(id+"F0.wireOp",EDGE,"E2277");
            var Q2111;
            Q2111=sQuery(id+"F0.wireOp",EDGE,"E1093");
            var Q2112;
            Q2112=sQuery(id+"F0.wireOp",EDGE,"E565");
            var Q2113;
            Q2113=sQuery(id+"F0.wireOp",EDGE,"E1148");
            var Q2114;
            Q2114=sQuery(id+"F0.wireOp",EDGE,"E1439");
            var Q2115;
            Q2115=sQuery(id+"F0.wireOp",EDGE,"E2101");
            var Q2116;
            Q2116=sQuery(id+"F0.wireOp",EDGE,"E1323");
            var Q2117;
            Q2117=sQuery(id+"F0.wireOp",EDGE,"E1331");
            var Q2118;
            Q2118=sQuery(id+"F0.wireOp",EDGE,"E1212");
            var Q2119;
            Q2119=sQuery(id+"F0.wireOp",EDGE,"E1283");
            var Q2120;
            Q2120=sQuery(id+"F0.wireOp",EDGE,"E1267");
            var Q2121;
            Q2121=sQuery(id+"F0.wireOp",EDGE,"E564");
            var Q2122;
            Q2122=sQuery(id+"F0.wireOp",EDGE,"E2298");
            var Q2123;
            Q2123=sQuery(id+"F0.wireOp",EDGE,"E1274");
            var Q2124;
            Q2124=sQuery(id+"F0.wireOp",EDGE,"E1258");
            var Q2125;
            Q2125=sQuery(id+"F0.wireOp",EDGE,"E1327");
            var Q2126;
            Q2126=sQuery(id+"F0.wireOp",EDGE,"E2275");
            var Q2127;
            Q2127=sQuery(id+"F0.wireOp",EDGE,"E2314");
            var Q2128;
            Q2128=sQuery(id+"F0.wireOp",EDGE,"E1290");
            var Q2129;
            Q2129=sQuery(id+"F0.wireOp",EDGE,"E803");
            var Q2130;
            Q2130=sQuery(id+"F0.wireOp",EDGE,"E2299");
            var Q2131;
            Q2131=sQuery(id+"F0.wireOp",EDGE,"E1834");
            var Q2132;
            Q2132=sQuery(id+"F0.wireOp",EDGE,"E1827");
            var Q2133;
            Q2133=sQuery(id+"F0.wireOp",EDGE,"E1651");
            var Q2134;
            Q2134=sQuery(id+"F0.wireOp",EDGE,"E1578");
            var Q2135;
            Q2135=sQuery(id+"F0.wireOp",EDGE,"E1252");
            var Q2136;
            Q2136=sQuery(id+"F0.wireOp",EDGE,"E1141");
            var Q2137;
            Q2137=sQuery(id+"F0.wireOp",EDGE,"E1798");
            var Q2138;
            Q2138=sQuery(id+"F0.wireOp",EDGE,"E1833");
            var Q2139;
            Q2139=sQuery(id+"F0.wireOp",EDGE,"E1939");
            var Q2140;
            Q2140=sQuery(id+"F0.wireOp",EDGE,"E1946");
            var Q2141;
            Q2141=sQuery(id+"F0.wireOp",EDGE,"E2164");
            var Q2142;
            Q2142=sQuery(id+"F0.wireOp",EDGE,"E2019");
            var Q2143;
            Q2143=sQuery(id+"F0.wireOp",EDGE,"E1273");
            var Q2144;
            Q2144=sQuery(id+"F0.wireOp",EDGE,"E1202");
            var Q2145;
            Q2145=sQuery(id+"F0.wireOp",EDGE,"E1170");
            var Q2146;
            Q2146=sQuery(id+"F0.wireOp",EDGE,"E2194");
            var Q2147;
            Q2147=sQuery(id+"F0.wireOp",EDGE,"E1129");
            var Q2148;
            Q2148=sQuery(id+"F0.wireOp",EDGE,"E2201");
            var Q2149;
            Q2149=sQuery(id+"F0.wireOp",EDGE,"E1161");
            var Q2150;
            Q2150=sQuery(id+"F0.wireOp",EDGE,"E2082");
            var Q2151;
            Q2151=sQuery(id+"F0.wireOp",EDGE,"E243");
            var Q2152;
            Q2152=sQuery(id+"F0.wireOp",EDGE,"E1197");
            var Q2153;
            Q2153=sQuery(id+"F0.wireOp",EDGE,"E2303");
            var Q2154;
            Q2154=sQuery(id+"F0.wireOp",EDGE,"E1938");
            var Q2155;
            Q2155=sQuery(id+"F0.wireOp",EDGE,"E1570");
            var Q2156;
            Q2156=sQuery(id+"F0.wireOp",EDGE,"E2116");
            var Q2157;
            Q2157=sQuery(id+"F0.wireOp",EDGE,"E963");
            var Q2158;
            Q2158=sQuery(id+"F0.wireOp",EDGE,"E1362");
            var Q2159;
            Q2159=sQuery(id+"F0.wireOp",EDGE,"E1378");
            var Q2160;
            Q2160=sQuery(id+"F0.wireOp",EDGE,"E1266");
            var Q2161;
            Q2161=sQuery(id+"F0.wireOp",EDGE,"E1723");
            var Q2162;
            Q2162=sQuery(id+"F0.wireOp",EDGE,"E2377");
            var Q2163;
            Q2163=sQuery(id+"F0.wireOp",EDGE,"E627");
            var Q2164;
            Q2164=sQuery(id+"F0.wireOp",EDGE,"E1124");
            var Q2165;
            Q2165=sQuery(id+"F0.wireOp",EDGE,"E2197");
            var Q2166;
            Q2166=sQuery(id+"F0.wireOp",EDGE,"E2025");
            var Q2167;
            Q2167=sQuery(id+"F0.wireOp",EDGE,"E499");
            var Q2168;
            Q2168=sQuery(id+"F0.wireOp",EDGE,"E1089");
            var Q2169;
            Q2169=sQuery(id+"F0.wireOp",EDGE,"E2107");
            var Q2170;
            Q2170=sQuery(id+"F0.wireOp",EDGE,"E1944");
            var Q2171;
            Q2171=sQuery(id+"F0.wireOp",EDGE,"E2024");
            var Q2172;
            Q2172=sQuery(id+"F0.wireOp",EDGE,"E1133");
            var Q2173;
            Q2173=sQuery(id+"F0.wireOp",EDGE,"E2108");
            var Q2174;
            Q2174=sQuery(id+"F0.wireOp",EDGE,"E1265");
            var Q2175;
            Q2175=sQuery(id+"F0.wireOp",EDGE,"E1185");
            var Q2176;
            Q2176=sQuery(id+"F0.wireOp",EDGE,"E1840");
            var Q2177;
            Q2177=sQuery(id+"F0.wireOp",EDGE,"E1783");
            var Q2178;
            Q2178=sQuery(id+"F0.wireOp",EDGE,"E1815");
            var Q2179;
            Q2179=sQuery(id+"F0.wireOp",EDGE,"E1511");
            var Q2180;
            Q2180=sQuery(id+"F0.wireOp",EDGE,"E1984");
            var Q2181;
            Q2181=sQuery(id+"F0.wireOp",EDGE,"E562");
            var Q2182;
            Q2182=sQuery(id+"F0.wireOp",EDGE,"E1829");
            var Q2183;
            Q2183=sQuery(id+"F0.wireOp",EDGE,"E402");
            var Q2184;
            Q2184=sQuery(id+"F0.wireOp",EDGE,"E801");
            var Q2185;
            Q2185=sQuery(id+"F0.wireOp",EDGE,"E129");
            var Q2186;
            Q2186=sQuery(id+"F0.wireOp",EDGE,"E1399");
            var Q2187;
            Q2187=sQuery(id+"F0.wireOp",EDGE,"E561");
            var Q2188;
            Q2188=sQuery(id+"F0.wireOp",EDGE,"E1492");
            var Q2189;
            Q2189=sQuery(id+"F0.wireOp",EDGE,"E2304");
            var Q2190;
            Q2190=sQuery(id+"F0.wireOp",EDGE,"E768");
            var Q2191;
            Q2191=sQuery(id+"F0.wireOp",EDGE,"E960");
            var Q2192;
            Q2192=sQuery(id+"F0.wireOp",EDGE,"E400");
            var Q2193;
            Q2193=sQuery(id+"F0.wireOp",EDGE,"E208");
            var Q2194;
            Q2194=sQuery(id+"F0.wireOp",EDGE,"E1957");
            var Q2195;
            Q2195=sQuery(id+"F0.wireOp",EDGE,"E1774");
            var Q2196;
            Q2196=sQuery(id+"F0.wireOp",EDGE,"E639");
            var Q2197;
            Q2197=sQuery(id+"F0.wireOp",EDGE,"E1287");
            var Q2198;
            Q2198=sQuery(id+"F0.wireOp",EDGE,"E1216");
            var Q2199;
            Q2199=sQuery(id+"F0.wireOp",EDGE,"E879");
            var Q2200;
            Q2200=sQuery(id+"F0.wireOp",EDGE,"E222");
            var Q2201;
            Q2201=sQuery(id+"F0.wireOp",EDGE,"E126");
            var Q2202;
            Q2202=sQuery(id+"F0.wireOp",EDGE,"E638");
            var Q2203;
            Q2203=sQuery(id+"F0.wireOp",EDGE,"E494");
            var Q2204;
            Q2204=sQuery(id+"F0.wireOp",EDGE,"E974");
            var Q2205;
            Q2205=sQuery(id+"F0.wireOp",EDGE,"E157");
            var Q2206;
            Q2206=sQuery(id+"F0.wireOp",EDGE,"E205");
            var Q2207;
            Q2207=sQuery(id+"F0.wireOp",EDGE,"E957");
            var Q2208;
            Q2208=sQuery(id+"F0.wireOp",EDGE,"E989");
            var Q2209;
            Q2209=sQuery(id+"F0.wireOp",EDGE,"E701");
            var Q2210;
            Q2210=sQuery(id+"F0.wireOp",EDGE,"E621");
            var Q2211;
            Q2211=sQuery(id+"F0.wireOp",EDGE,"E1005");
            var Q2212;
            Q2212=sQuery(id+"F0.wireOp",EDGE,"E1254");
            var Q2213;
            Q2213=sQuery(id+"F0.wireOp",EDGE,"E1158");
            var Q2214;
            Q2214=sQuery(id+"F0.wireOp",EDGE,"E2198");
            var Q2215;
            Q2215=sQuery(id+"F0.wireOp",EDGE,"E1271");
            var Q2216;
            Q2216=sQuery(id+"F0.wireOp",EDGE,"E1772");
            var Q2217;
            Q2217=sQuery(id+"F0.wireOp",EDGE,"E2302");
            var Q2218;
            Q2218=sQuery(id+"F0.wireOp",EDGE,"E1756");
            var Q2219;
            Q2219=sQuery(id+"F0.wireOp",EDGE,"E1653");
            var Q2220;
            Q2220=sQuery(id+"F0.wireOp",EDGE,"E1215");
            var Q2221;
            Q2221=sQuery(id+"F0.wireOp",EDGE,"E2159");
            var Q2222;
            Q2222=sQuery(id+"F0.wireOp",EDGE,"E1510");
            var Q2223;
            Q2223=sQuery(id+"F0.wireOp",EDGE,"E1086");
            var Q2224;
            Q2224=sQuery(id+"F0.wireOp",EDGE,"E1828");
            var Q2225;
            Q2225=sQuery(id+"F0.wireOp",EDGE,"E443");
            var Q2226;
            Q2226=sQuery(id+"F0.wireOp",EDGE,"E475");
            var Q2227;
            Q2227=sQuery(id+"F0.wireOp",EDGE,"E538");
            var Q2228;
            Q2228=sQuery(id+"F0.wireOp",EDGE,"E426");
            var Q2229;
            Q2229=sQuery(id+"F0.wireOp",EDGE,"E2294");
            var Q2230;
            Q2230=sQuery(id+"F0.wireOp",EDGE,"E633");
            var Q2231;
            Q2231=sQuery(id+"F0.wireOp",EDGE,"E649");
            var Q2232;
            Q2232=sQuery(id+"F0.wireOp",EDGE,"E2405");
            var Q2233;
            Q2233=sQuery(id+"F0.wireOp",EDGE,"E504");
            var Q2234;
            Q2234=sQuery(id+"F0.wireOp",EDGE,"E648");
            var Q2235;
            Q2235=sQuery(id+"F0.wireOp",EDGE,"E1420");
            var Q2236;
            Q2236=sQuery(id+"F0.wireOp",EDGE,"E2293");
            var Q2237;
            Q2237=sQuery(id+"F0.wireOp",EDGE,"E695");
            var Q2238;
            Q2238=sQuery(id+"F0.wireOp",EDGE,"E1812");
            var Q2239;
            Q2239=sQuery(id+"F0.wireOp",EDGE,"E119");
            var Q2240;
            Q2240=sQuery(id+"F0.wireOp",EDGE,"E1372");
            var Q2241;
            Q2241=sQuery(id+"F0.wireOp",EDGE,"E1796");
            var Q2242;
            Q2242=sQuery(id+"F0.wireOp",EDGE,"E1565");
            var Q2243;
            Q2243=sQuery(id+"F0.wireOp",EDGE,"E1949");
            var Q2244;
            Q2244=sQuery(id+"F0.wireOp",EDGE,"E406");
            var Q2245;
            Q2245=sQuery(id+"F0.wireOp",EDGE,"E1933");
            var Q2246;
            Q2246=sQuery(id+"F0.wireOp",EDGE,"E646");
            var Q2247;
            Q2247=sQuery(id+"F0.wireOp",EDGE,"E566");
            var Q2248;
            Q2248=sQuery(id+"F0.wireOp",EDGE,"E470");
            var Q2249;
            Q2249=sQuery(id+"F0.wireOp",EDGE,"E422");
            var Q2250;
            Q2250=sQuery(id+"F0.wireOp",EDGE,"E1803");
            var Q2251;
            Q2251=sQuery(id+"F0.wireOp",EDGE,"E1276");
            var Q2252;
            Q2252=sQuery(id+"F0.wireOp",EDGE,"E1787");
            var Q2253;
            Q2253=sQuery(id+"F0.wireOp",EDGE,"E1260");
            var Q2254;
            Q2254=sQuery(id+"F0.wireOp",EDGE,"E501");
            var Q2255;
            Q2255=sQuery(id+"F0.wireOp",EDGE,"E2316");
            var Q2256;
            Q2256=sQuery(id+"F0.wireOp",EDGE,"E965");
            var Q2257;
            Q2257=sQuery(id+"F0.wireOp",EDGE,"E1418");
            var Q2258;
            Q2258=sQuery(id+"F0.wireOp",EDGE,"E1132");
            var Q2259;
            Q2259=sQuery(id+"F0.wireOp",EDGE,"E1434");
            var Q2260;
            Q2260=sQuery(id+"F0.wireOp",EDGE,"E692");
            var Q2261;
            Q2261=sQuery(id+"F0.wireOp",EDGE,"E1354");
            var Q2262;
            Q2262=sQuery(id+"F0.wireOp",EDGE,"E1155");
            var Q2263;
            Q2263=sQuery(id+"F0.wireOp",EDGE,"E1355");
            var Q2264;
            Q2264=sQuery(id+"F0.wireOp",EDGE,"E1162");
            var Q2265;
            Q2265=sQuery(id+"F0.wireOp",EDGE,"E1763");
            var Q2266;
            Q2266=sQuery(id+"F0.wireOp",EDGE,"E2283");
            var Q2267;
            Q2267=sQuery(id+"F0.wireOp",EDGE,"E1754");
            var Q2268;
            Q2268=sQuery(id+"F0.wireOp",EDGE,"E1562");
            var Q2269;
            Q2269=sQuery(id+"F0.wireOp",EDGE,"E1427");
            var Q2270;
            Q2270=sQuery(id+"F0.wireOp",EDGE,"E2276");
            var Q2271;
            Q2271=sQuery(id+"F0.wireOp",EDGE,"E2204");
            var Q2272;
            Q2272=sQuery(id+"F0.wireOp",EDGE,"E1826");
            var Q2273;
            Q2273=sQuery(id+"F0.wireOp",EDGE,"E1762");
            var Q2274;
            Q2274=sQuery(id+"F0.wireOp",EDGE,"E1211");
            var Q2275;
            Q2275=sQuery(id+"F0.wireOp",EDGE,"E1140");
            var Q2276;
            Q2276=sQuery(id+"F0.wireOp",EDGE,"E1195");
            var Q2277;
            Q2277=sQuery(id+"F0.wireOp",EDGE,"E2297");
            var Q2278;
            Q2278=sQuery(id+"F0.wireOp",EDGE,"E1257");
            var Q2279;
            Q2279=sQuery(id+"F0.wireOp",EDGE,"E1289");
            var Q2280;
            Q2280=sQuery(id+"F0.wireOp",EDGE,"E1180");
            var Q2281;
            Q2281=sQuery(id+"F0.wireOp",EDGE,"E1636");
            var Q2282;
            Q2282=sQuery(id+"F0.wireOp",EDGE,"E2073");
            var Q2283;
            Q2283=sQuery(id+"F0.wireOp",EDGE,"E1986");
            var Q2284;
            Q2284=sQuery(id+"F0.wireOp",EDGE,"E1650");
            var Q2285;
            Q2285=sQuery(id+"F0.wireOp",EDGE,"E1657");
            var Q2286;
            Q2286=sQuery(id+"F0.wireOp",EDGE,"E1577");
            var Q2287;
            Q2287=sQuery(id+"F0.wireOp",EDGE,"E1109");
            var Q2288;
            Q2288=sQuery(id+"F0.wireOp",EDGE,"E1147");
            var Q2289;
            Q2289=sQuery(id+"F0.wireOp",EDGE,"E1164");
            var Q2290;
            Q2290=sQuery(id+"F0.wireOp",EDGE,"E2100");
            var Q2291;
            Q2291=sQuery(id+"F0.wireOp",EDGE,"E1282");
            var Q2292;
            Q2292=sQuery(id+"F0.wireOp",EDGE,"E1330");
            var Q2293;
            Q2293=sQuery(id+"F0.wireOp",EDGE,"E1369");
            var Q2294;
            Q2294=sQuery(id+"F0.wireOp",EDGE,"E1832");
            var Q2295;
            Q2295=sQuery(id+"F0.wireOp",EDGE,"E1569");
            var Q2296;
            Q2296=sQuery(id+"F0.wireOp",EDGE,"E563");
            var Q2297;
            Q2297=sQuery(id+"F0.wireOp",EDGE,"E467");
            var Q2298;
            Q2298=sQuery(id+"F0.wireOp",EDGE,"E1643");
            var Q2299;
            Q2299=sQuery(id+"F0.wireOp",EDGE,"E1149");
            var Q2300;
            Q2300=sQuery(id+"F0.wireOp",EDGE,"E1105");
            var Q2301;
            Q2301=sQuery(id+"F0.wireOp",EDGE,"E1750");
            var Q2302;
            Q2302=sQuery(id+"F0.wireOp",EDGE,"E2081");
            var Q2303;
            Q2303=sQuery(id+"F0.wireOp",EDGE,"E1985");
            var Q2304;
            Q2304=sQuery(id+"F0.wireOp",EDGE,"E1083");
            var Q2305;
            Q2305=sQuery(id+"F0.wireOp",EDGE,"E1937");
            var Q2306;
            Q2306=sQuery(id+"F0.wireOp",EDGE,"E1448");
            var Q2307;
            Q2307=sQuery(id+"F0.wireOp",EDGE,"E1425");
            var Q2308;
            Q2308=sQuery(id+"F0.wireOp",EDGE,"E1361");
            var Q2309;
            Q2309=sQuery(id+"F0.wireOp",EDGE,"E1416");
            var Q2310;
            Q2310=sQuery(id+"F0.wireOp",EDGE,"E1272");
            var Q2311;
            Q2311=sQuery(id+"F0.wireOp",EDGE,"E2028");
            var Q2312;
            Q2312=sQuery(id+"F0.wireOp",EDGE,"E1169");
            var Q2313;
            Q2313=sQuery(id+"F0.wireOp",EDGE,"E1831");
            var Q2314;
            Q2314=sQuery(id+"F0.wireOp",EDGE,"E962");
            var Q2315;
            Q2315=sQuery(id+"F0.wireOp",EDGE,"E1845");
            var Q2316;
            Q2316=sQuery(id+"F0.wireOp",EDGE,"E1165");
            var Q2317;
            Q2317=sQuery(id+"F0.wireOp",EDGE,"E1991");
            var Q2318;
            Q2318=sQuery(id+"F0.wireOp",EDGE,"E498");
            var Q2319;
            Q2319=sQuery(id+"F0.wireOp",EDGE,"E1943");
            var Q2320;
            Q2320=sQuery(id+"F0.wireOp",EDGE,"E2023");
            var Q2321;
            Q2321=sQuery(id+"F0.wireOp",EDGE,"E1085");
            var Q2322;
            Q2322=sQuery(id+"F0.wireOp",EDGE,"E689");
            var Q2323;
            Q2323=sQuery(id+"F0.wireOp",EDGE,"E2076");
            var Q2324;
            Q2324=sQuery(id+"F0.wireOp",EDGE,"E1438");
            var Q2325;
            Q2325=sQuery(id+"F0.wireOp",EDGE,"E1579");
            var Q2326;
            Q2326=sQuery(id+"F0.wireOp",EDGE,"E1444");
            var Q2327;
            Q2327=sQuery(id+"F0.wireOp",EDGE,"E1431");
            var Q2328;
            Q2328=sQuery(id+"F0.wireOp",EDGE,"E401");
            var Q2329;
            Q2329=sQuery(id+"F0.wireOp",EDGE,"E1335");
            var Q2330;
            Q2330=sQuery(id+"F0.wireOp",EDGE,"E416");
            var Q2331;
            Q2331=sQuery(id+"F0.wireOp",EDGE,"E464");
            var Q2332;
            Q2332=sQuery(id+"F0.wireOp",EDGE,"E399");
            var Q2333;
            Q2333=sQuery(id+"F0.wireOp",EDGE,"E767");
            var Q2334;
            Q2334=sQuery(id+"F0.wireOp",EDGE,"E463");
            var Q2335;
            Q2335=sQuery(id+"F0.wireOp",EDGE,"E1806");
            var Q2336;
            Q2336=sQuery(id+"F0.wireOp",EDGE,"E959");
            var Q2337;
            Q2337=sQuery(id+"F0.wireOp",EDGE,"E2021");
            var Q2338;
            Q2338=sQuery(id+"F0.wireOp",EDGE,"E125");
            var Q2339;
            Q2339=sQuery(id+"F0.wireOp",EDGE,"E973");
            var Q2340;
            Q2340=sQuery(id+"F0.wireOp",EDGE,"E637");
            var Q2341;
            Q2341=sQuery(id+"F0.wireOp",EDGE,"E1582");
            var Q2342;
            Q2342=sQuery(id+"F0.wireOp",EDGE,"E2031");
            var Q2343;
            Q2343=sQuery(id+"F0.wireOp",EDGE,"E1222");
            var Q2344;
            Q2344=sQuery(id+"F0.wireOp",EDGE,"E1174");
            var Q2345;
            Q2345=sQuery(id+"F0.wireOp",EDGE,"E1264");
            var Q2346;
            Q2346=sQuery(id+"F0.wireOp",EDGE,"E2272");
            var Q2347;
            Q2347=sQuery(id+"F0.wireOp",EDGE,"E1168");
            var Q2348;
            Q2348=sQuery(id+"F0.wireOp",EDGE,"E2080");
            var Q2349;
            Q2349=sQuery(id+"F0.wireOp",EDGE,"E1804");
            var Q2350;
            Q2350=sQuery(id+"F0.wireOp",EDGE,"E1839");
            var Q2351;
            Q2351=sQuery(id+"F0.wireOp",EDGE,"E1844");
            var Q2352;
            Q2352=sQuery(id+"F0.wireOp",EDGE,"E1580");
            var Q2353;
            Q2353=sQuery(id+"F0.wireOp",EDGE,"E1509");
            var Q2354;
            Q2354=sQuery(id+"F0.wireOp",EDGE,"E1430");
            var Q2355;
            Q2355=sQuery(id+"F0.wireOp",EDGE,"E2027");
            var Q2356;
            Q2356=sQuery(id+"F0.wireOp",EDGE,"E1334");
            var Q2357;
            Q2357=sQuery(id+"F0.wireOp",EDGE,"E1995");
            var Q2358;
            Q2358=sQuery(id+"F0.wireOp",EDGE,"E474");
            var Q2359;
            Q2359=sQuery(id+"F0.wireOp",EDGE,"E1270");
            var Q2360;
            Q2360=sQuery(id+"F0.wireOp",EDGE,"E632");
            var Q2361;
            Q2361=sQuery(id+"F0.wireOp",EDGE,"E1835");
            var Q2362;
            Q2362=sQuery(id+"F0.wireOp",EDGE,"E1764");
            var Q2363;
            Q2363=sQuery(id+"F0.wireOp",EDGE,"E647");
            var Q2364;
            Q2364=sQuery(id+"F0.wireOp",EDGE,"E1356");
            var Q2365;
            Q2365=sQuery(id+"F0.wireOp",EDGE,"E1364");
            var Q2366;
            Q2366=sQuery(id+"F0.wireOp",EDGE,"E1771");
            var Q2367;
            Q2367=sQuery(id+"F0.wireOp",EDGE,"E2030");
            var Q2368;
            Q2368=sQuery(id+"F0.wireOp",EDGE,"E2301");
            var Q2369;
            Q2369=sQuery(id+"F0.wireOp",EDGE,"E1419");
            var Q2370;
            Q2370=sQuery(id+"F0.wireOp",EDGE,"E1755");
            var Q2371;
            Q2371=sQuery(id+"F0.wireOp",EDGE,"E2308");
            var Q2372;
            Q2372=sQuery(id+"F0.wireOp",EDGE,"E1221");
            var Q2373;
            Q2373=sQuery(id+"F0.wireOp",EDGE,"E1830");
            var Q2374;
            Q2374=sQuery(id+"F0.wireOp",EDGE,"E469");
            var Q2375;
            Q2375=sQuery(id+"F0.wireOp",EDGE,"E420");
            var Q2376;
            Q2376=sQuery(id+"F0.wireOp",EDGE,"E2379");
            var Q2377;
            Q2377=sQuery(id+"F0.wireOp",EDGE,"E1275");
            var Q2378;
            Q2378=sQuery(id+"F0.wireOp",EDGE,"E1753");
            var Q2379;
            Q2379=sQuery(id+"F0.wireOp",EDGE,"E1994");
            var Q2380;
            Q2380=sQuery(id+"F0.wireOp",EDGE,"E1213");
            var Q2381;
            Q2381=sQuery(id+"F0.wireOp",EDGE,"E1188");
            var Q2382;
            Q2382=sQuery(id+"F0.wireOp",EDGE,"E2274");
            var Q2383;
            Q2383=sQuery(id+"F0.wireOp",EDGE,"E2313");
            var Q2384;
            Q2384=sQuery(id+"F0.wireOp",EDGE,"E1561");
            var Q2385;
            Q2385=sQuery(id+"F0.wireOp",EDGE,"E1417");
            var Q2386;
            Q2386=sQuery(id+"F0.wireOp",EDGE,"E1433");
            var Q2387;
            Q2387=sQuery(id+"F0.wireOp",EDGE,"E1353");
            var Q2388;
            Q2388=sQuery(id+"F0.wireOp",EDGE,"E691");
            var Q2389;
            Q2389=sQuery(id+"F0.wireOp",EDGE,"E1825");
            var Q2390;
            Q2390=sQuery(id+"F0.wireOp",EDGE,"E1656");
            var Q2391;
            Q2391=sQuery(id+"F0.wireOp",EDGE,"E1229");
            var Q2392;
            Q2392=sQuery(id+"F0.wireOp",EDGE,"E2200");
            var Q2393;
            Q2393=sQuery(id+"F0.wireOp",EDGE,"E1160");
            var Q2394;
            Q2394=sQuery(id+"F0.wireOp",EDGE,"E1576");
            var Q2395;
            Q2395=sQuery(id+"F0.wireOp",EDGE,"E1173");
            var Q2396;
            Q2396=sQuery(id+"F0.wireOp",EDGE,"E1377");
            var Q2397;
            Q2397=sQuery(id+"F0.wireOp",EDGE,"E1281");
            var Q2398;
            Q2398=sQuery(id+"F0.wireOp",EDGE,"E1329");
            var Q2399;
            Q2399=sQuery(id+"F0.wireOp",EDGE,"E1368");
            var Q2400;
            Q2400=sQuery(id+"F0.wireOp",EDGE,"E1767");
            var Q2401;
            Q2401=sQuery(id+"F0.wireOp",EDGE,"E1568");
            var Q2402;
            Q2402=sQuery(id+"F0.wireOp",EDGE,"E1559");
            var Q2403;
            Q2403=sQuery(id+"F0.wireOp",EDGE,"E1010");
            var Q2404;
            Q2404=sQuery(id+"F0.wireOp",EDGE,"E466");
            var Q2405;
            Q2405=sQuery(id+"F0.wireOp",EDGE,"E2022");
            var Q2406;
            Q2406=sQuery(id+"F0.wireOp",EDGE,"E2020");
            var Q2407;
            Q2407=sQuery(id+"F0.wireOp",EDGE,"E1424");
            var Q2408;
            Q2408=sQuery(id+"F0.wireOp",EDGE,"E1563");
            var Q2409;
            Q2409=sQuery(id+"F0.wireOp",EDGE,"E1360");
            var Q2410;
            Q2410=sQuery(id+"F0.wireOp",EDGE,"E2077");
            var Q2411;
            Q2411=sQuery(id+"F0.wireOp",EDGE,"E497");
            var Q2412;
            Q2412=sQuery(id+"F0.wireOp",EDGE,"E688");
            var Q2413;
            Q2413=sQuery(id+"F0.wireOp",EDGE,"E415");
            var Q2414;
            Q2414=sQuery(id+"F0.wireOp",EDGE,"E1941");
            var Q2415;
            Q2415=sQuery(id+"F0.wireOp",EDGE,"E1948");
            var Q2416;
            Q2416=sQuery(id+"F0.wireOp",EDGE,"E958");
            var Q2417;
            Q2417=sQuery(id+"F0.wireOp",EDGE,"E541");
            var Q2418;
            Q2418=sQuery(id+"F0.wireOp",EDGE,"E1206");
            var Q2419;
            Q2419=sQuery(id+"F0.wireOp",EDGE,"E1990");
            var Q2420;
            Q2420=sQuery(id+"F0.wireOp",EDGE,"E1159");
            var Q2421;
            Q2421=sQuery(id+"F0.wireOp",EDGE,"E1262");
            var Q2422;
            Q2422=sQuery(id+"F0.wireOp",EDGE,"E1654");
            var Q2423;
            Q2423=sQuery(id+"F0.wireOp",EDGE,"E2271");
            var Q2424;
            Q2424=sQuery(id+"F0.wireOp",EDGE,"E2127");
            var Q2425;
            Q2425=sQuery(id+"F0.wireOp",EDGE,"E1940");
            var Q2426;
            Q2426=sQuery(id+"F0.wireOp",EDGE,"E1429");
            var Q2427;
            Q2427=sQuery(id+"F0.wireOp",EDGE,"E569");
            var Q2428;
            Q2428=sQuery(id+"F0.wireOp",EDGE,"E1333");
            var Q2429;
            Q2429=sQuery(id+"F0.wireOp",EDGE,"E1981");
            var Q2430;
            Q2430=sQuery(id+"F0.wireOp",EDGE,"E1421");
            var Q2431;
            Q2431=sQuery(id+"F0.wireOp",EDGE,"E1348");
            var Q2432;
            Q2432=sQuery(id+"F0.wireOp",EDGE,"E1567");
            var Q2433;
            Q2433=sQuery(id+"F0.wireOp",EDGE,"E1269");
            var Q2434;
            Q2434=sQuery(id+"F0.wireOp",EDGE,"E1357");
            var Q2435;
            Q2435=sQuery(id+"F0.wireOp",EDGE,"E1277");
            var Q2436;
            Q2436=sQuery(id+"F0.wireOp",EDGE,"E1205");
            var Q2437;
            Q2437=sQuery(id+"F0.wireOp",EDGE,"E773");
            var Q2438;
            Q2438=sQuery(id+"F0.wireOp",EDGE,"E645");
            var Q2439;
            Q2439=sQuery(id+"F0.wireOp",EDGE,"E1339");
            var Q2440;
            Q2440=sQuery(id+"F0.wireOp",EDGE,"E1347");
            var Q2441;
            Q2441=sQuery(id+"F0.wireOp",EDGE,"E1338");
            var Q2442;
            Q2442=sQuery(id+"F0.wireOp",EDGE,"E1766");
            var Q2443;
            Q2443=sQuery(id+"F0.wireOp",EDGE,"E468");
            var Q2444;
            Q2444=sQuery(id+"F0.wireOp",EDGE,"E1371");
            var Q2445;
            Q2445=sQuery(id+"F0.wireOp",EDGE,"E2131");
            var Q2446;
            Q2446=sQuery(id+"F0.wireOp",EDGE,"E2029");
            var Q2447;
            Q2447=sQuery(id+"F0.wireOp",EDGE,"E1154");
            var Q2448;
            Q2448=sQuery(id+"F0.wireOp",EDGE,"E2130");
            var Q2449;
            Q2449=sQuery(id+"F0.wireOp",EDGE,"E1359");
            var Q2450;
            Q2450=sQuery(id+"F0.wireOp",EDGE,"E1993");
            var Q2451;
            Q2451=sQuery(id+"F0.wireOp",EDGE,"E1897");
            var Q2452;
            Q2452=sQuery(id+"F0.wireOp",EDGE,"E1426");
            var Q2453;
            Q2453=sQuery(id+"F0.wireOp",EDGE,"E1263");
            var Q2454;
            Q2454=sQuery(id+"F0.wireOp",EDGE,"E1131");
            var Q2455;
            Q2455=sQuery(id+"F0.wireOp",EDGE,"E1752");
            var Q2456;
            Q2456=sQuery(id+"F0.wireOp",EDGE,"E2203");
            var Q2457;
            Q2457=sQuery(id+"F0.wireOp",EDGE,"E419");
            var Q2458;
            Q2458=sQuery(id+"F0.wireOp",EDGE,"E2072");
            var Q2459;
            Q2459=sQuery(id+"F0.wireOp",EDGE,"E690");
            var Q2460;
            Q2460=sQuery(id+"F0.wireOp",EDGE,"E1560");
            var Q2461;
            Q2461=sQuery(id+"F0.wireOp",EDGE,"E2157");
            var Q2462;
            Q2462=sQuery(id+"F0.wireOp",EDGE,"E1432");
            var Q2463;
            Q2463=sQuery(id+"F0.wireOp",EDGE,"E1352");
            var Q2464;
            Q2464=sQuery(id+"F0.wireOp",EDGE,"E2084");
            var Q2465;
            Q2465=sQuery(id+"F0.wireOp",EDGE,"E1288");
            var Q2466;
            Q2466=sQuery(id+"F0.wireOp",EDGE,"E1824");
            var Q2467;
            Q2467=sQuery(id+"F0.wireOp",EDGE,"E1575");
            var Q2468;
            Q2468=sQuery(id+"F0.wireOp",EDGE,"E1181");
            var Q2469;
            Q2469=sQuery(id+"F0.wireOp",EDGE,"E1936");
            var Q2470;
            Q2470=sQuery(id+"F0.wireOp",EDGE,"E2124");
            var Q2471;
            Q2471=sQuery(id+"F0.wireOp",EDGE,"E1508");
            var Q2472;
            Q2472=sQuery(id+"F0.wireOp",EDGE,"E1344");
            var Q2473;
            Q2473=sQuery(id+"F0.wireOp",EDGE,"E1415");
            var Q2474;
            Q2474=sQuery(id+"F0.wireOp",EDGE,"E1009");
            var Q2475;
            Q2475=sQuery(id+"F0.wireOp",EDGE,"E465");
            var Q2476;
            Q2476=sQuery(id+"F0.wireOp",EDGE,"E1351");
            var Q2477;
            Q2477=sQuery(id+"F0.wireOp",EDGE,"E1280");
            var Q2478;
            Q2478=sQuery(id+"F0.wireOp",EDGE,"E1328");
            var Q2479;
            Q2479=sQuery(id+"F0.wireOp",EDGE,"E1838");
            var Q2480;
            Q2480=sQuery(id+"F0.wireOp",EDGE,"E1367");
            var Q2481;
            Q2481=sQuery(id+"F0.wireOp",EDGE,"E414");
            var Q2482;
            Q2482=sQuery(id+"F0.wireOp",EDGE,"E1843");
            var Q2483;
            Q2483=sQuery(id+"F0.wireOp",EDGE,"E493");
            var Q2484;
            Q2484=sQuery(id+"F0.wireOp",EDGE,"E2075");
            var Q2485;
            Q2485=sQuery(id+"F0.wireOp",EDGE,"E1358");
            var Q2486;
            Q2486=sQuery(id+"F0.wireOp",EDGE,"E2199");
            var Q2487;
            Q2487=sQuery(id+"F0.wireOp",EDGE,"E1823");
            var Q2488;
            Q2488=sQuery(id+"F0.wireOp",EDGE,"E1574");
            var Q2489;
            Q2489=sQuery(id+"F0.wireOp",EDGE,"E1414");
            var Q2490;
            Q2490=sQuery(id+"F0.wireOp",EDGE,"E2142");
            var Q2491;
            Q2491=sQuery(id+"F0.wireOp",EDGE,"E1350");
            var Q2492;
            Q2492=sQuery(id+"F0.wireOp",EDGE,"E473");
            var Q2493;
            Q2493=sQuery(id+"F0.wireOp",EDGE,"E1902");
            var Q2494;
            Q2494=sQuery(id+"F0.wireOp",EDGE,"E1436");
            var Q2495;
            Q2495=sQuery(id+"F0.wireOp",EDGE,"E1332");
            var Q2496;
            Q2496=sQuery(id+"F0.wireOp",EDGE,"E1899");
            var Q2497;
            Q2497=sQuery(id+"F0.wireOp",EDGE,"E1581");
            var Q2498;
            Q2498=sQuery(id+"F0.wireOp",EDGE,"E1373");
            var Q2499;
            Q2499=sQuery(id+"F0.wireOp",EDGE,"E1261");
            var Q2500;
            Q2500=sQuery(id+"F0.wireOp",EDGE,"E1652");
            var Q2501;
            Q2501=sQuery(id+"F0.wireOp",EDGE,"E772");
            var Q2502;
            Q2502=sQuery(id+"F0.wireOp",EDGE,"E1947");
            var Q2503;
            Q2503=sQuery(id+"F0.wireOp",EDGE,"E1423");
            var Q2504;
            Q2504=sQuery(id+"F0.wireOp",EDGE,"E1343");
            var Q2505;
            Q2505=sQuery(id+"F0.wireOp",EDGE,"E2138");
            var Q2506;
            Q2506=sQuery(id+"F0.wireOp",EDGE,"E1204");
            var Q2507;
            Q2507=sQuery(id+"F0.wireOp",EDGE,"E1259");
            var Q2508;
            Q2508=sQuery(id+"F0.wireOp",EDGE,"E2315");
            var Q2509;
            Q2509=sQuery(id+"F0.wireOp",EDGE,"E1291");
            var Q2510;
            Q2510=sQuery(id+"F0.wireOp",EDGE,"E1898");
            var Q2511;
            Q2511=sQuery(id+"F0.wireOp",EDGE,"E1279");
            var Q2512;
            Q2512=sQuery(id+"F0.wireOp",EDGE,"E2196");
            var Q2513;
            Q2513=sQuery(id+"F0.wireOp",EDGE,"E1337");
            var Q2514;
            Q2514=sQuery(id+"F0.wireOp",EDGE,"E1761");
            var Q2515;
            Q2515=sQuery(id+"F0.wireOp",EDGE,"E2018");
            var Q2516;
            Q2516=sQuery(id+"F0.wireOp",EDGE,"E2132");
            var Q2517;
            Q2517=sQuery(id+"F0.wireOp",EDGE,"E2129");
            var Q2518;
            Q2518=sQuery(id+"F0.wireOp",EDGE,"E2136");
            var Q2519;
            Q2519=sQuery(id+"F0.wireOp",EDGE,"E2017");
            var Q2520;
            Q2520=sQuery(id+"F0.wireOp",EDGE,"E2273");
            var Q2521;
            Q2521=sQuery(id+"F0.wireOp",EDGE,"E2312");
            var Q2522;
            Q2522=sQuery(id+"F0.wireOp",EDGE,"E1751");
            var Q2523;
            Q2523=sQuery(id+"F0.wireOp",EDGE,"E1655");
            var Q2524;
            Q2524=sQuery(id+"F0.wireOp",EDGE,"E418");
            var Q2525;
            Q2525=sQuery(id+"F0.wireOp",EDGE,"E1989");
            var Q2526;
            Q2526=sQuery(id+"F0.wireOp",EDGE,"E2123");
            var Q2527;
            Q2527=sQuery(id+"F0.wireOp",EDGE,"E1376");
            var Q2528;
            Q2528=sQuery(id+"F0.wireOp",EDGE,"E1836");
            var Q2529;
            Q2529=sQuery(id+"F0.wireOp",EDGE,"E736");
            var Q2530;
            Q2530=sQuery(id+"F0.wireOp",EDGE,"E1765");
            var Q2531;
            Q2531=sQuery(id+"F0.wireOp",EDGE,"E1008");
            var Q2532;
            Q2532=sQuery(id+"F0.wireOp",EDGE,"E1988");
            var Q2533;
            Q2533=sQuery(id+"F0.wireOp",EDGE,"E2128");
            var Q2534;
            Q2534=sQuery(id+"F0.wireOp",EDGE,"E2158");
            var Q2535;
            Q2535=sQuery(id+"F0.wireOp",EDGE,"E1573");
            var Q2536;
            Q2536=sQuery(id+"F0.wireOp",EDGE,"E2015");
            var Q2537;
            Q2537=sQuery(id+"F0.wireOp",EDGE,"E1837");
            var Q2538;
            Q2538=sQuery(id+"F0.wireOp",EDGE,"E1413");
            var Q2539;
            Q2539=sQuery(id+"F0.wireOp",EDGE,"E1286");
            var Q2540;
            Q2540=sQuery(id+"F0.wireOp",EDGE,"E1349");
            var Q2541;
            Q2541=sQuery(id+"F0.wireOp",EDGE,"E472");
            var Q2542;
            Q2542=sQuery(id+"F0.wireOp",EDGE,"E1435");
            var Q2543;
            Q2543=sQuery(id+"F0.wireOp",EDGE,"E1268");
            var Q2544;
            Q2544=sQuery(id+"F0.wireOp",EDGE,"E771");
            var Q2545;
            Q2545=sQuery(id+"F0.wireOp",EDGE,"E1375");
            var Q2546;
            Q2546=sQuery(id+"F0.wireOp",EDGE,"E2146");
            var Q2547;
            Q2547=sQuery(id+"F0.wireOp",EDGE,"E1346");
            var Q2548;
            Q2548=sQuery(id+"F0.wireOp",EDGE,"E1163");
            var Q2549;
            Q2549=sQuery(id+"F0.wireOp",EDGE,"E1992");
            var Q2550;
            Q2550=sQuery(id+"F0.wireOp",EDGE,"E1336");
            var Q2551;
            Q2551=sQuery(id+"F0.wireOp",EDGE,"E1153");
            var Q2552;
            Q2552=sQuery(id+"F0.wireOp",EDGE,"E2193");
            var Q2553;
            Q2553=sQuery(id+"F0.wireOp",EDGE,"E2140");
            var Q2554;
            Q2554=sQuery(id+"F0.wireOp",EDGE,"E2016");
            var Q2555;
            Q2555=sQuery(id+"F0.wireOp",EDGE,"E1422");
            var Q2556;
            Q2556=sQuery(id+"F0.wireOp",EDGE,"E1342");
            var Q2557;
            Q2557=sQuery(id+"F0.wireOp",EDGE,"E1822");
            var Q2558;
            Q2558=sQuery(id+"F0.wireOp",EDGE,"E1900");
            var Q2559;
            Q2559=sQuery(id+"F0.wireOp",EDGE,"E735");
            var Q2560;
            Q2560=sQuery(id+"F0.wireOp",EDGE,"E2311");
            var Q2561;
            Q2561=sQuery(id+"F0.wireOp",EDGE,"E2192");
            var Q2562;
            Q2562=sQuery(id+"F0.wireOp",EDGE,"E2270");
            var Q2563;
            Q2563=sQuery(id+"F0.wireOp",EDGE,"E2143");
            var Q2564;
            Q2564=sQuery(id+"F0.wireOp",EDGE,"E2126");
            var Q2565;
            Q2565=sQuery(id+"F0.wireOp",EDGE,"E1437");
            var Q2566;
            Q2566=sQuery(id+"F0.wireOp",EDGE,"E1428");
            var Q2567;
            Q2567=sQuery(id+"F0.wireOp",EDGE,"E471");
            var Q2568;
            Q2568=sQuery(id+"F0.wireOp",EDGE,"E1901");
            var Q2569;
            Q2569=sQuery(id+"F0.wireOp",EDGE,"E1340");
            var Q2570;
            Q2570=sQuery(id+"F0.wireOp",EDGE,"E1285");
            var Q2571;
            Q2571=sQuery(id+"F0.wireOp",EDGE,"E1157");
            var Q2572;
            Q2572=sQuery(id+"F0.wireOp",EDGE,"E2137");
            var Q2573;
            Q2573=sQuery(id+"F0.wireOp",EDGE,"E1896");
            var Q2574;
            Q2574=sQuery(id+"F0.wireOp",EDGE,"E1572");
            var Q2575;
            Q2575=sQuery(id+"F0.wireOp",EDGE,"E1760");
            var Q2576;
            Q2576=sQuery(id+"F0.wireOp",EDGE,"E2141");
            var Q2577;
            Q2577=sQuery(id+"F0.wireOp",EDGE,"E734");
            var Q2578;
            Q2578=sQuery(id+"F0.wireOp",EDGE,"E2135");
            var Q2579;
            Q2579=sQuery(id+"F0.wireOp",EDGE,"E1759");
            var Q2580;
            Q2580=sQuery(id+"F0.wireOp",EDGE,"E2014");
            var Q2581;
            Q2581=sQuery(id+"F0.wireOp",EDGE,"E1341");
            var Q2582;
            Q2582=sQuery(id+"F0.wireOp",EDGE,"E1156");
            var Q2583;
            Q2583=sQuery(id+"F0.wireOp",EDGE,"E2269");
            var Q2584;
            Q2584=sQuery(id+"F0.wireOp",EDGE,"E2145");
            var Q2585;
            Q2585=sQuery(id+"F0.wireOp",EDGE,"E1345");
            var Q2586;
            Q2586=sQuery(id+"F0.wireOp",EDGE,"E2125");
            var Q2587;
            Q2587=sQuery(id+"F0.wireOp",EDGE,"E2144");
            var Q2588;
            Q2588=sQuery(id+"F0.wireOp",EDGE,"E2191");
            var Q2589;
            Q2589=sQuery(id+"F0.wireOp",EDGE,"E1758");
            var Q2590;
            Q2590=sQuery(id+"F0.wireOp",EDGE,"E2134");
            var Q2591;
            Q2591=sQuery(id+"F0.wireOp",EDGE,"E1757");
            var Q2592;
            Q2592=sQuery(id+"F0.wireOp",EDGE,"E2139");
            var Q2593;
            Q2593=sQuery(id+"F0.wireOp",EDGE,"E2190");
            var Q2594;
            Q2594=sQuery(id+"F0.wireOp",EDGE,"E2133");
            extrude(context, id + "F1", {"entities" : qUnion([Q0, Q1, Q2, Q3, Q4, Q5, Q6, Q7, Q8, Q9, Q10, Q11, Q12, Q13, Q14, Q15, Q16, Q17, Q18, Q19, Q20, Q21, Q22, Q23, Q24, Q25, Q26, Q27, Q28, Q29, Q30, Q31, Q32, Q33, Q34, Q35, Q36, Q37, Q38, Q39, Q40, Q41, Q42, Q43, Q44, Q45, Q46, Q47, Q48, Q49, Q50, Q51, Q52, Q53, Q54, Q55, Q56, Q57, Q58, Q59, Q60, Q61, Q62, Q63, Q64, Q65, Q66, Q67, Q68, Q69, Q70, Q71, Q72, Q73, Q74, Q75, Q76, Q77, Q78, Q79, Q80, Q81, Q82, Q83, Q84, Q85, Q86, Q87, Q88, Q89, Q90, Q91, Q92]), "surfaceOperationType" : NewSurfaceOperationType.ADD, "surfaceEntities" : qUnion([Q93, Q94, Q95, Q96, Q97, Q98, Q99, Q100, Q101, Q102, Q103, Q104, Q105, Q106, Q107, Q108, Q109, Q110, Q111, Q112, Q113, Q114, Q115, Q116, Q117, Q118, Q119, Q120, Q121, Q122, Q123, Q124, Q125, Q126, Q127, Q128, Q129, Q130, Q131, Q132, Q133, Q134, Q135, Q136, Q137, Q138, Q139, Q140, Q141, Q142, Q143, Q144, Q145, Q146, Q147, Q148, Q149, Q150, Q151, Q152, Q153, Q154, Q155, Q156, Q157, Q158, Q159, Q160, Q161, Q162, Q163, Q164, Q165, Q166, Q167, Q168, Q169, Q170, Q171, Q172, Q173, Q174, Q175, Q176, Q177, Q178, Q179, Q180, Q181, Q182, Q183, Q184, Q185, Q186, Q187, Q188, Q189, Q190, Q191, Q192, Q193, Q194, Q195, Q196, Q197, Q198, Q199, Q200, Q201, Q202, Q203, Q204, Q205, Q206, Q207, Q208, Q209, Q210, Q211, Q212, Q213, Q214, Q215, Q216, Q217, Q218, Q219, Q220, Q221, Q222, Q223, Q224, Q225, Q226, Q227, Q228, Q229, Q230, Q231, Q232, Q233, Q234, Q235, Q236, Q237, Q238, Q239, Q240, Q241, Q242, Q243, Q244, Q245, Q246, Q247, Q248, Q249, Q250, Q251, Q252, Q253, Q254, Q255, Q256, Q257, Q258, Q259, Q260, Q261, Q262, Q263, Q264, Q265, Q266, Q267, Q268, Q269, Q270, Q271, Q272, Q273, Q274, Q275, Q276, Q277, Q278, Q279, Q280, Q281, Q282, Q283, Q284, Q285, Q286, Q287, Q288, Q289, Q290, Q291, Q292, Q293, Q294, Q295, Q296, Q297, Q298, Q299, Q300, Q301, Q302, Q303, Q304, Q305, Q306, Q307, Q308, Q309, Q310, Q311, Q312, Q313, Q314, Q315, Q316, Q317, Q318, Q319, Q320, Q321, Q322, Q323, Q324, Q325, Q326, Q327, Q328, Q329, Q330, Q331, Q332, Q333, Q334, Q335, Q336, Q337, Q338, Q339, Q340, Q341, Q342, Q343, Q344, Q345, Q346, Q347, Q348, Q349, Q350, Q351, Q352, Q353, Q354, Q355, Q356, Q357, Q358, Q359, Q360, Q361, Q362, Q363, Q364, Q365, Q366, Q367, Q368, Q369, Q370, Q371, Q372, Q373, Q374, Q375, Q376, Q377, Q378, Q379, Q380, Q381, Q382, Q383, Q384, Q385, Q386, Q387, Q388, Q389, Q390, Q391, Q392, Q393, Q394, Q395, Q396, Q397, Q398, Q399, Q400, Q401, Q402, Q403, Q404, Q405, Q406, Q407, Q408, Q409, Q410, Q411, Q412, Q413, Q414, Q415, Q416, Q417, Q418, Q419, Q420, Q421, Q422, Q423, Q424, Q425, Q426, Q427, Q428, Q429, Q430, Q431, Q432, Q433, Q434, Q435, Q436, Q437, Q438, Q439, Q440, Q441, Q442, Q443, Q444, Q445, Q446, Q447, Q448, Q449, Q450, Q451, Q452, Q453, Q454, Q455, Q456, Q457, Q458, Q459, Q460, Q461, Q462, Q463, Q464, Q465, Q466, Q467, Q468, Q469, Q470, Q471, Q472, Q473, Q474, Q475, Q476, Q477, Q478, Q479, Q480, Q481, Q482, Q483, Q484, Q485, Q486, Q487, Q488, Q489, Q490, Q491, Q492, Q493, Q494, Q495, Q496, Q497, Q498, Q499, Q500, Q501, Q502, Q503, Q504, Q505, Q506, Q507, Q508, Q509, Q510, Q511, Q512, Q513, Q514, Q515, Q516, Q517, Q518, Q519, Q520, Q521, Q522, Q523, Q524, Q525, Q526, Q527, Q528, Q529, Q530, Q531, Q532, Q533, Q534, Q535, Q536, Q537, Q538, Q539, Q540, Q541, Q542, Q543, Q544, Q545, Q546, Q547, Q548, Q549, Q550, Q551, Q552, Q553, Q554, Q555, Q556, Q557, Q558, Q559, Q560, Q561, Q562, Q563, Q564, Q565, Q566, Q567, Q568, Q569, Q570, Q571, Q572, Q573, Q574, Q575, Q576, Q577, Q578, Q579, Q580, Q581, Q582, Q583, Q584, Q585, Q586, Q587, Q588, Q589, Q590, Q591, Q592, Q593, Q594, Q595, Q596, Q597, Q598, Q599, Q600, Q601, Q602, Q603, Q604, Q605, Q606, Q607, Q608, Q609, Q610, Q611, Q612, Q613, Q614, Q615, Q616, Q617, Q618, Q619, Q620, Q621, Q622, Q623, Q624, Q625, Q626, Q627, Q628, Q629, Q630, Q631, Q632, Q633, Q634, Q635, Q636, Q637, Q638, Q639, Q640, Q641, Q642, Q643, Q644, Q645, Q646, Q647, Q648, Q649, Q650, Q651, Q652, Q653, Q654, Q655, Q656, Q657, Q658, Q659, Q660, Q661, Q662, Q663, Q664, Q665, Q666, Q667, Q668, Q669, Q670, Q671, Q672, Q673, Q674, Q675, Q676, Q677, Q678, Q679, Q680, Q681, Q682, Q683, Q684, Q685, Q686, Q687, Q688, Q689, Q690, Q691, Q692, Q693, Q694, Q695, Q696, Q697, Q698, Q699, Q700, Q701, Q702, Q703, Q704, Q705, Q706, Q707, Q708, Q709, Q710, Q711, Q712, Q713, Q714, Q715, Q716, Q717, Q718, Q719, Q720, Q721, Q722, Q723, Q724, Q725, Q726, Q727, Q728, Q729, Q730, Q731, Q732, Q733, Q734, Q735, Q736, Q737, Q738, Q739, Q740, Q741, Q742, Q743, Q744, Q745, Q746, Q747, Q748, Q749, Q750, Q751, Q752, Q753, Q754, Q755, Q756, Q757, Q758, Q759, Q760, Q761, Q762, Q763, Q764, Q765, Q766, Q767, Q768, Q769, Q770, Q771, Q772, Q773, Q774, Q775, Q776, Q777, Q778, Q779, Q780, Q781, Q782, Q783, Q784, Q785, Q786, Q787, Q788, Q789, Q790, Q791, Q792, Q793, Q794, Q795, Q796, Q797, Q798, Q799, Q800, Q801, Q802, Q803, Q804, Q805, Q806, Q807, Q808, Q809, Q810, Q811, Q812, Q813, Q814, Q815, Q816, Q817, Q818, Q819, Q820, Q821, Q822, Q823, Q824, Q825, Q826, Q827, Q828, Q829, Q830, Q831, Q832, Q833, Q834, Q835, Q836, Q837, Q838, Q839, Q840, Q841, Q842, Q843, Q844, Q845, Q846, Q847, Q848, Q849, Q850, Q851, Q852, Q853, Q854, Q855, Q856, Q857, Q858, Q859, Q860, Q861, Q862, Q863, Q864, Q865, Q866, Q867, Q868, Q869, Q870, Q871, Q872, Q873, Q874, Q875, Q876, Q877, Q878, Q879, Q880, Q881, Q882, Q883, Q884, Q885, Q886, Q887, Q888, Q889, Q890, Q891, Q892, Q893, Q894, Q895, Q896, Q897, Q898, Q899, Q900, Q901, Q902, Q903, Q904, Q905, Q906, Q907, Q908, Q909, Q910, Q911, Q912, Q913, Q914, Q915, Q916, Q917, Q918, Q919, Q920, Q921, Q922, Q923, Q924, Q925, Q926, Q927, Q928, Q929, Q930, Q931, Q932, Q933, Q934, Q935, Q936, Q937, Q938, Q939, Q940, Q941, Q942, Q943, Q944, Q945, Q946, Q947, Q948, Q949, Q950, Q951, Q952, Q953, Q954, Q955, Q956, Q957, Q958, Q959, Q960, Q961, Q962, Q963, Q964, Q965, Q966, Q967, Q968, Q969, Q970, Q971, Q972, Q973, Q974, Q975, Q976, Q977, Q978, Q979, Q980, Q981, Q982, Q983, Q984, Q985, Q986, Q987, Q988, Q989, Q990, Q991, Q992, Q993, Q994, Q995, Q996, Q997, Q998, Q999, Q1000, Q1001, Q1002, Q1003, Q1004, Q1005, Q1006, Q1007, Q1008, Q1009, Q1010, Q1011, Q1012, Q1013, Q1014, Q1015, Q1016, Q1017, Q1018, Q1019, Q1020, Q1021, Q1022, Q1023, Q1024, Q1025, Q1026, Q1027, Q1028, Q1029, Q1030, Q1031, Q1032, Q1033, Q1034, Q1035, Q1036, Q1037, Q1038, Q1039, Q1040, Q1041, Q1042, Q1043, Q1044, Q1045, Q1046, Q1047, Q1048, Q1049, Q1050, Q1051, Q1052, Q1053, Q1054, Q1055, Q1056, Q1057, Q1058, Q1059, Q1060, Q1061, Q1062, Q1063, Q1064, Q1065, Q1066, Q1067, Q1068, Q1069, Q1070, Q1071, Q1072, Q1073, Q1074, Q1075, Q1076, Q1077, Q1078, Q1079, Q1080, Q1081, Q1082, Q1083, Q1084, Q1085, Q1086, Q1087, Q1088, Q1089, Q1090, Q1091, Q1092, Q1093, Q1094, Q1095, Q1096, Q1097, Q1098, Q1099, Q1100, Q1101, Q1102, Q1103, Q1104, Q1105, Q1106, Q1107, Q1108, Q1109, Q1110, Q1111, Q1112, Q1113, Q1114, Q1115, Q1116, Q1117, Q1118, Q1119, Q1120, Q1121, Q1122, Q1123, Q1124, Q1125, Q1126, Q1127, Q1128, Q1129, Q1130, Q1131, Q1132, Q1133, Q1134, Q1135, Q1136, Q1137, Q1138, Q1139, Q1140, Q1141, Q1142, Q1143, Q1144, Q1145, Q1146, Q1147, Q1148, Q1149, Q1150, Q1151, Q1152, Q1153, Q1154, Q1155, Q1156, Q1157, Q1158, Q1159, Q1160, Q1161, Q1162, Q1163, Q1164, Q1165, Q1166, Q1167, Q1168, Q1169, Q1170, Q1171, Q1172, Q1173, Q1174, Q1175, Q1176, Q1177, Q1178, Q1179, Q1180, Q1181, Q1182, Q1183, Q1184, Q1185, Q1186, Q1187, Q1188, Q1189, Q1190, Q1191, Q1192, Q1193, Q1194, Q1195, Q1196, Q1197, Q1198, Q1199, Q1200, Q1201, Q1202, Q1203, Q1204, Q1205, Q1206, Q1207, Q1208, Q1209, Q1210, Q1211, Q1212, Q1213, Q1214, Q1215, Q1216, Q1217, Q1218, Q1219, Q1220, Q1221, Q1222, Q1223, Q1224, Q1225, Q1226, Q1227, Q1228, Q1229, Q1230, Q1231, Q1232, Q1233, Q1234, Q1235, Q1236, Q1237, Q1238, Q1239, Q1240, Q1241, Q1242, Q1243, Q1244, Q1245, Q1246, Q1247, Q1248, Q1249, Q1250, Q1251, Q1252, Q1253, Q1254, Q1255, Q1256, Q1257, Q1258, Q1259, Q1260, Q1261, Q1262, Q1263, Q1264, Q1265, Q1266, Q1267, Q1268, Q1269, Q1270, Q1271, Q1272, Q1273, Q1274, Q1275, Q1276, Q1277, Q1278, Q1279, Q1280, Q1281, Q1282, Q1283, Q1284, Q1285, Q1286, Q1287, Q1288, Q1289, Q1290, Q1291, Q1292, Q1293, Q1294, Q1295, Q1296, Q1297, Q1298, Q1299, Q1300, Q1301, Q1302, Q1303, Q1304, Q1305, Q1306, Q1307, Q1308, Q1309, Q1310, Q1311, Q1312, Q1313, Q1314, Q1315, Q1316, Q1317, Q1318, Q1319, Q1320, Q1321, Q1322, Q1323, Q1324, Q1325, Q1326, Q1327, Q1328, Q1329, Q1330, Q1331, Q1332, Q1333, Q1334, Q1335, Q1336, Q1337, Q1338, Q1339, Q1340, Q1341, Q1342, Q1343, Q1344, Q1345, Q1346, Q1347, Q1348, Q1349, Q1350, Q1351, Q1352, Q1353, Q1354, Q1355, Q1356, Q1357, Q1358, Q1359, Q1360, Q1361, Q1362, Q1363, Q1364, Q1365, Q1366, Q1367, Q1368, Q1369, Q1370, Q1371, Q1372, Q1373, Q1374, Q1375, Q1376, Q1377, Q1378, Q1379, Q1380, Q1381, Q1382, Q1383, Q1384, Q1385, Q1386, Q1387, Q1388, Q1389, Q1390, Q1391, Q1392, Q1393, Q1394, Q1395, Q1396, Q1397, Q1398, Q1399, Q1400, Q1401, Q1402, Q1403, Q1404, Q1405, Q1406, Q1407, Q1408, Q1409, Q1410, Q1411, Q1412, Q1413, Q1414, Q1415, Q1416, Q1417, Q1418, Q1419, Q1420, Q1421, Q1422, Q1423, Q1424, Q1425, Q1426, Q1427, Q1428, Q1429, Q1430, Q1431, Q1432, Q1433, Q1434, Q1435, Q1436, Q1437, Q1438, Q1439, Q1440, Q1441, Q1442, Q1443, Q1444, Q1445, Q1446, Q1447, Q1448, Q1449, Q1450, Q1451, Q1452, Q1453, Q1454, Q1455, Q1456, Q1457, Q1458, Q1459, Q1460, Q1461, Q1462, Q1463, Q1464, Q1465, Q1466, Q1467, Q1468, Q1469, Q1470, Q1471, Q1472, Q1473, Q1474, Q1475, Q1476, Q1477, Q1478, Q1479, Q1480, Q1481, Q1482, Q1483, Q1484, Q1485, Q1486, Q1487, Q1488, Q1489, Q1490, Q1491, Q1492, Q1493, Q1494, Q1495, Q1496, Q1497, Q1498, Q1499, Q1500, Q1501, Q1502, Q1503, Q1504, Q1505, Q1506, Q1507, Q1508, Q1509, Q1510, Q1511, Q1512, Q1513, Q1514, Q1515, Q1516, Q1517, Q1518, Q1519, Q1520, Q1521, Q1522, Q1523, Q1524, Q1525, Q1526, Q1527, Q1528, Q1529, Q1530, Q1531, Q1532, Q1533, Q1534, Q1535, Q1536, Q1537, Q1538, Q1539, Q1540, Q1541, Q1542, Q1543, Q1544, Q1545, Q1546, Q1547, Q1548, Q1549, Q1550, Q1551, Q1552, Q1553, Q1554, Q1555, Q1556, Q1557, Q1558, Q1559, Q1560, Q1561, Q1562, Q1563, Q1564, Q1565, Q1566, Q1567, Q1568, Q1569, Q1570, Q1571, Q1572, Q1573, Q1574, Q1575, Q1576, Q1577, Q1578, Q1579, Q1580, Q1581, Q1582, Q1583, Q1584, Q1585, Q1586, Q1587, Q1588, Q1589, Q1590, Q1591, Q1592, Q1593, Q1594, Q1595, Q1596, Q1597, Q1598, Q1599, Q1600, Q1601, Q1602, Q1603, Q1604, Q1605, Q1606, Q1607, Q1608, Q1609, Q1610, Q1611, Q1612, Q1613, Q1614, Q1615, Q1616, Q1617, Q1618, Q1619, Q1620, Q1621, Q1622, Q1623, Q1624, Q1625, Q1626, Q1627, Q1628, Q1629, Q1630, Q1631, Q1632, Q1633, Q1634, Q1635, Q1636, Q1637, Q1638, Q1639, Q1640, Q1641, Q1642, Q1643, Q1644, Q1645, Q1646, Q1647, Q1648, Q1649, Q1650, Q1651, Q1652, Q1653, Q1654, Q1655, Q1656, Q1657, Q1658, Q1659, Q1660, Q1661, Q1662, Q1663, Q1664, Q1665, Q1666, Q1667, Q1668, Q1669, Q1670, Q1671, Q1672, Q1673, Q1674, Q1675, Q1676, Q1677, Q1678, Q1679, Q1680, Q1681, Q1682, Q1683, Q1684, Q1685, Q1686, Q1687, Q1688, Q1689, Q1690, Q1691, Q1692, Q1693, Q1694, Q1695, Q1696, Q1697, Q1698, Q1699, Q1700, Q1701, Q1702, Q1703, Q1704, Q1705, Q1706, Q1707, Q1708, Q1709, Q1710, Q1711, Q1712, Q1713, Q1714, Q1715, Q1716, Q1717, Q1718, Q1719, Q1720, Q1721, Q1722, Q1723, Q1724, Q1725, Q1726, Q1727, Q1728, Q1729, Q1730, Q1731, Q1732, Q1733, Q1734, Q1735, Q1736, Q1737, Q1738, Q1739, Q1740, Q1741, Q1742, Q1743, Q1744, Q1745, Q1746, Q1747, Q1748, Q1749, Q1750, Q1751, Q1752, Q1753, Q1754, Q1755, Q1756, Q1757, Q1758, Q1759, Q1760, Q1761, Q1762, Q1763, Q1764, Q1765, Q1766, Q1767, Q1768, Q1769, Q1770, Q1771, Q1772, Q1773, Q1774, Q1775, Q1776, Q1777, Q1778, Q1779, Q1780, Q1781, Q1782, Q1783, Q1784, Q1785, Q1786, Q1787, Q1788, Q1789, Q1790, Q1791, Q1792, Q1793, Q1794, Q1795, Q1796, Q1797, Q1798, Q1799, Q1800, Q1801, Q1802, Q1803, Q1804, Q1805, Q1806, Q1807, Q1808, Q1809, Q1810, Q1811, Q1812, Q1813, Q1814, Q1815, Q1816, Q1817, Q1818, Q1819, Q1820, Q1821, Q1822, Q1823, Q1824, Q1825, Q1826, Q1827, Q1828, Q1829, Q1830, Q1831, Q1832, Q1833, Q1834, Q1835, Q1836, Q1837, Q1838, Q1839, Q1840, Q1841, Q1842, Q1843, Q1844, Q1845, Q1846, Q1847, Q1848, Q1849, Q1850, Q1851, Q1852, Q1853, Q1854, Q1855, Q1856, Q1857, Q1858, Q1859, Q1860, Q1861, Q1862, Q1863, Q1864, Q1865, Q1866, Q1867, Q1868, Q1869, Q1870, Q1871, Q1872, Q1873, Q1874, Q1875, Q1876, Q1877, Q1878, Q1879, Q1880, Q1881, Q1882, Q1883, Q1884, Q1885, Q1886, Q1887, Q1888, Q1889, Q1890, Q1891, Q1892, Q1893, Q1894, Q1895, Q1896, Q1897, Q1898, Q1899, Q1900, Q1901, Q1902, Q1903, Q1904, Q1905, Q1906, Q1907, Q1908, Q1909, Q1910, Q1911, Q1912, Q1913, Q1914, Q1915, Q1916, Q1917, Q1918, Q1919, Q1920, Q1921, Q1922, Q1923, Q1924, Q1925, Q1926, Q1927, Q1928, Q1929, Q1930, Q1931, Q1932, Q1933, Q1934, Q1935, Q1936, Q1937, Q1938, Q1939, Q1940, Q1941, Q1942, Q1943, Q1944, Q1945, Q1946, Q1947, Q1948, Q1949, Q1950, Q1951, Q1952, Q1953, Q1954, Q1955, Q1956, Q1957, Q1958, Q1959, Q1960, Q1961, Q1962, Q1963, Q1964, Q1965, Q1966, Q1967, Q1968, Q1969, Q1970, Q1971, Q1972, Q1973, Q1974, Q1975, Q1976, Q1977, Q1978, Q1979, Q1980, Q1981, Q1982, Q1983, Q1984, Q1985, Q1986, Q1987, Q1988, Q1989, Q1990, Q1991, Q1992, Q1993, Q1994, Q1995, Q1996, Q1997, Q1998, Q1999, Q2000, Q2001, Q2002, Q2003, Q2004, Q2005, Q2006, Q2007, Q2008, Q2009, Q2010, Q2011, Q2012, Q2013, Q2014, Q2015, Q2016, Q2017, Q2018, Q2019, Q2020, Q2021, Q2022, Q2023, Q2024, Q2025, Q2026, Q2027, Q2028, Q2029, Q2030, Q2031, Q2032, Q2033, Q2034, Q2035, Q2036, Q2037, Q2038, Q2039, Q2040, Q2041, Q2042, Q2043, Q2044, Q2045, Q2046, Q2047, Q2048, Q2049, Q2050, Q2051, Q2052, Q2053, Q2054, Q2055, Q2056, Q2057, Q2058, Q2059, Q2060, Q2061, Q2062, Q2063, Q2064, Q2065, Q2066, Q2067, Q2068, Q2069, Q2070, Q2071, Q2072, Q2073, Q2074, Q2075, Q2076, Q2077, Q2078, Q2079, Q2080, Q2081, Q2082, Q2083, Q2084, Q2085, Q2086, Q2087, Q2088, Q2089, Q2090, Q2091, Q2092, Q2093, Q2094, Q2095, Q2096, Q2097, Q2098, Q2099, Q2100, Q2101, Q2102, Q2103, Q2104, Q2105, Q2106, Q2107, Q2108, Q2109, Q2110, Q2111, Q2112, Q2113, Q2114, Q2115, Q2116, Q2117, Q2118, Q2119, Q2120, Q2121, Q2122, Q2123, Q2124, Q2125, Q2126, Q2127, Q2128, Q2129, Q2130, Q2131, Q2132, Q2133, Q2134, Q2135, Q2136, Q2137, Q2138, Q2139, Q2140, Q2141, Q2142, Q2143, Q2144, Q2145, Q2146, Q2147, Q2148, Q2149, Q2150, Q2151, Q2152, Q2153, Q2154, Q2155, Q2156, Q2157, Q2158, Q2159, Q2160, Q2161, Q2162, Q2163, Q2164, Q2165, Q2166, Q2167, Q2168, Q2169, Q2170, Q2171, Q2172, Q2173, Q2174, Q2175, Q2176, Q2177, Q2178, Q2179, Q2180, Q2181, Q2182, Q2183, Q2184, Q2185, Q2186, Q2187, Q2188, Q2189, Q2190, Q2191, Q2192, Q2193, Q2194, Q2195, Q2196, Q2197, Q2198, Q2199, Q2200, Q2201, Q2202, Q2203, Q2204, Q2205, Q2206, Q2207, Q2208, Q2209, Q2210, Q2211, Q2212, Q2213, Q2214, Q2215, Q2216, Q2217, Q2218, Q2219, Q2220, Q2221, Q2222, Q2223, Q2224, Q2225, Q2226, Q2227, Q2228, Q2229, Q2230, Q2231, Q2232, Q2233, Q2234, Q2235, Q2236, Q2237, Q2238, Q2239, Q2240, Q2241, Q2242, Q2243, Q2244, Q2245, Q2246, Q2247, Q2248, Q2249, Q2250, Q2251, Q2252, Q2253, Q2254, Q2255, Q2256, Q2257, Q2258, Q2259, Q2260, Q2261, Q2262, Q2263, Q2264, Q2265, Q2266, Q2267, Q2268, Q2269, Q2270, Q2271, Q2272, Q2273, Q2274, Q2275, Q2276, Q2277, Q2278, Q2279, Q2280, Q2281, Q2282, Q2283, Q2284, Q2285, Q2286, Q2287, Q2288, Q2289, Q2290, Q2291, Q2292, Q2293, Q2294, Q2295, Q2296, Q2297, Q2298, Q2299, Q2300, Q2301, Q2302, Q2303, Q2304, Q2305, Q2306, Q2307, Q2308, Q2309, Q2310, Q2311, Q2312, Q2313, Q2314, Q2315, Q2316, Q2317, Q2318, Q2319, Q2320, Q2321, Q2322, Q2323, Q2324, Q2325, Q2326, Q2327, Q2328, Q2329, Q2330, Q2331, Q2332, Q2333, Q2334, Q2335, Q2336, Q2337, Q2338, Q2339, Q2340, Q2341, Q2342, Q2343, Q2344, Q2345, Q2346, Q2347, Q2348, Q2349, Q2350, Q2351, Q2352, Q2353, Q2354, Q2355, Q2356, Q2357, Q2358, Q2359, Q2360, Q2361, Q2362, Q2363, Q2364, Q2365, Q2366, Q2367, Q2368, Q2369, Q2370, Q2371, Q2372, Q2373, Q2374, Q2375, Q2376, Q2377, Q2378, Q2379, Q2380, Q2381, Q2382, Q2383, Q2384, Q2385, Q2386, Q2387, Q2388, Q2389, Q2390, Q2391, Q2392, Q2393, Q2394, Q2395, Q2396, Q2397, Q2398, Q2399, Q2400, Q2401, Q2402, Q2403, Q2404, Q2405, Q2406, Q2407, Q2408, Q2409, Q2410, Q2411, Q2412, Q2413, Q2414, Q2415, Q2416, Q2417, Q2418, Q2419, Q2420, Q2421, Q2422, Q2423, Q2424, Q2425, Q2426, Q2427, Q2428, Q2429, Q2430, Q2431, Q2432, Q2433, Q2434, Q2435, Q2436, Q2437, Q2438, Q2439, Q2440, Q2441, Q2442, Q2443, Q2444, Q2445, Q2446, Q2447, Q2448, Q2449, Q2450, Q2451, Q2452, Q2453, Q2454, Q2455, Q2456, Q2457, Q2458, Q2459, Q2460, Q2461, Q2462, Q2463, Q2464, Q2465, Q2466, Q2467, Q2468, Q2469, Q2470, Q2471, Q2472, Q2473, Q2474, Q2475, Q2476, Q2477, Q2478, Q2479, Q2480, Q2481, Q2482, Q2483, Q2484, Q2485, Q2486, Q2487, Q2488, Q2489, Q2490, Q2491, Q2492, Q2493, Q2494, Q2495, Q2496, Q2497, Q2498, Q2499, Q2500, Q2501, Q2502, Q2503, Q2504, Q2505, Q2506, Q2507, Q2508, Q2509, Q2510, Q2511, Q2512, Q2513, Q2514, Q2515, Q2516, Q2517, Q2518, Q2519, Q2520, Q2521, Q2522, Q2523, Q2524, Q2525, Q2526, Q2527, Q2528, Q2529, Q2530, Q2531, Q2532, Q2533, Q2534, Q2535, Q2536, Q2537, Q2538, Q2539, Q2540, Q2541, Q2542, Q2543, Q2544, Q2545, Q2546, Q2547, Q2548, Q2549, Q2550, Q2551, Q2552, Q2553, Q2554, Q2555, Q2556, Q2557, Q2558, Q2559, Q2560, Q2561, Q2562, Q2563, Q2564, Q2565, Q2566, Q2567, Q2568, Q2569, Q2570, Q2571, Q2572, Q2573, Q2574, Q2575, Q2576, Q2577, Q2578, Q2579, Q2580, Q2581, Q2582, Q2583, Q2584, Q2585, Q2586, Q2587, Q2588, Q2589, Q2590, Q2591, Q2592, Q2593, Q2594]), "depth" : 0.4 * mm, "offsetDistance" : 25 * mm});
        }
    });
